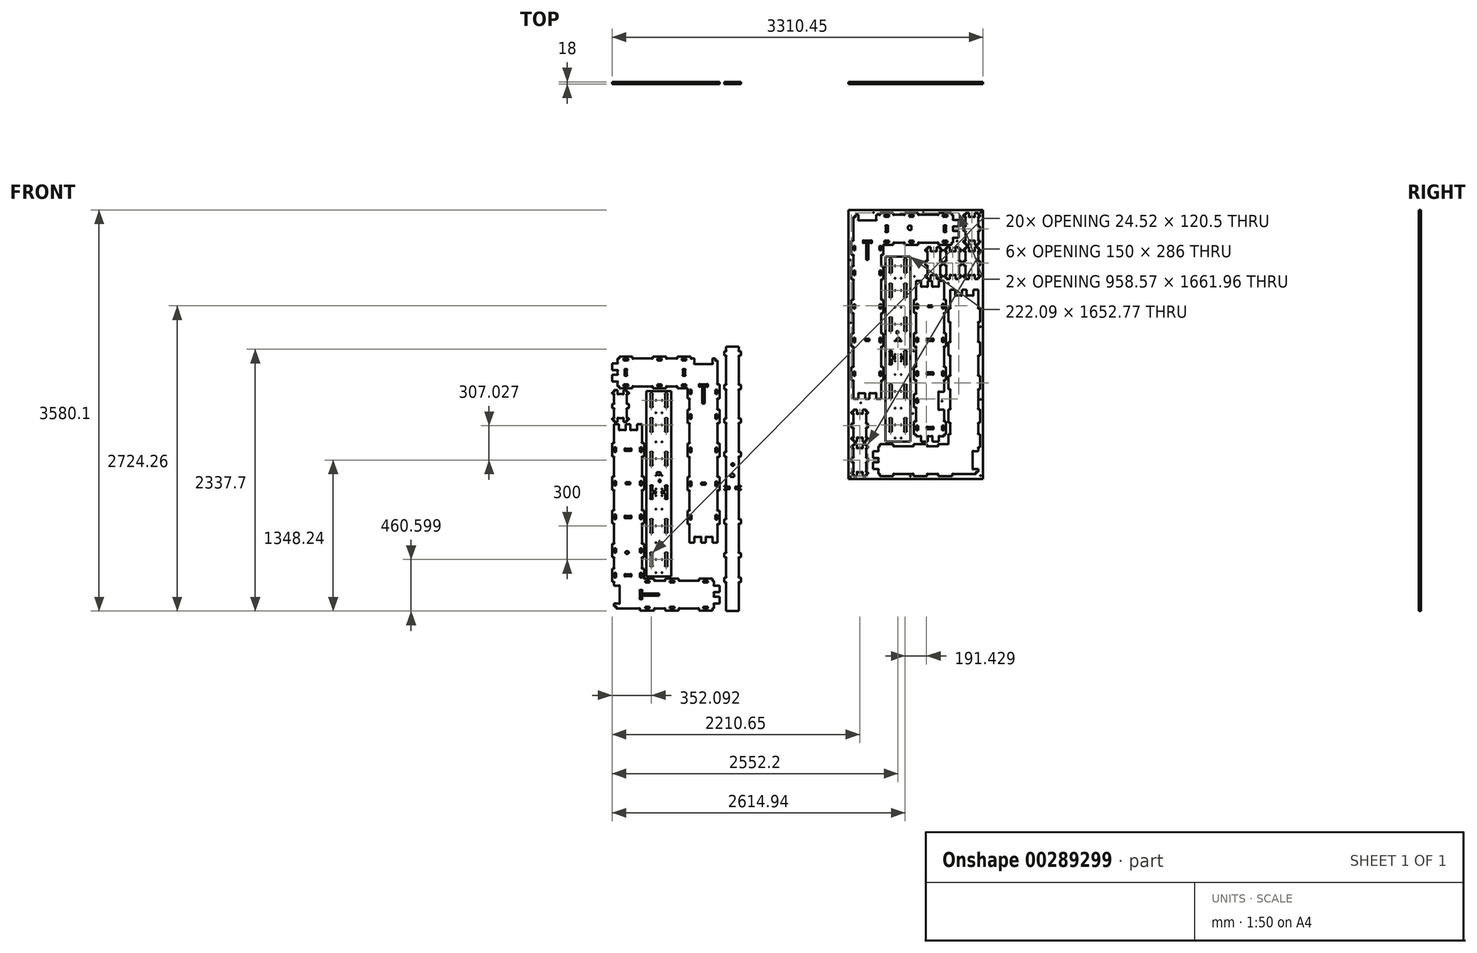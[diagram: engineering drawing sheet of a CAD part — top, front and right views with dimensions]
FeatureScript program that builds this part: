
annotation { "Feature Type Name" : "Feature", "Feature Type Description" : "" }
export const myFeature = defineFeature(function(context is Context, id is Id, definition is map)
    precondition{}
    {
        {
            var Q0;
            Q0=qCreatedBy(makeId("Front.planeOp"),FACE);
            var sketch = newSketch(context, id + "F0", { "sketchPlane" : qUnion([Q0])});
            skLineSegment(sketch, "E0", {"start": v(348.3, 849.32) * mm, "end": v(348.3, 1056.8) * mm});
            skLineSegment(sketch, "E1", {"start": v(348.3, 1056.8) * mm, "end": v(334.83, 1056.8) * mm});
            skArc(sketch, "E2", {"start": v(334.83, 1056.8) * mm, "mid": v(331.45, 1053.78) * mm, "end": v(328.3, 1057.05) * mm});
            skLineSegment(sketch, "E3", {"start": v(328.3, 1057.05) * mm, "end": v(328.3, 1074.8) * mm});
            skLineSegment(sketch, "E4", {"start": v(328.3, 1074.8) * mm, "end": v(303.8, 1074.8) * mm});
            skLineSegment(sketch, "E5", {"start": v(303.8, 1074.8) * mm, "end": v(303.8, 1031.32) * mm});
            skArc(sketch, "E6", {"start": v(303.8, 1031.32) * mm, "mid": v(306.82, 1027.93) * mm, "end": v(303.56, 1024.8) * mm});
            skLineSegment(sketch, "E7", {"start": v(303.56, 1024.8) * mm, "end": v(143.56, 1024.8) * mm});
            skArc(sketch, "E8", {"start": v(143.56, 1024.8) * mm, "mid": v(140.3, 1027.94) * mm, "end": v(143.3, 1031.32) * mm});
            skLineSegment(sketch, "E9", {"start": v(143.3, 1031.32) * mm, "end": v(143.3, 1074.8) * mm});
            skLineSegment(sketch, "E10", {"start": v(143.3, 1074.8) * mm, "end": v(117.06, 1074.8) * mm});
            skArc(sketch, "E11", {"start": v(117.06, 1074.8) * mm, "mid": v(113.68, 1071.78) * mm, "end": v(110.54, 1075.05) * mm});
            skLineSegment(sketch, "E12", {"start": v(110.54, 1075.05) * mm, "end": v(110.54, 1092.8) * mm});
            skLineSegment(sketch, "E13", {"start": v(110.54, 1092.8) * mm, "end": v(-8.96, 1092.8) * mm});
            skLineSegment(sketch, "E14", {"start": v(-8.96, 1092.8) * mm, "end": v(-8.96, 1075.05) * mm});
            skArc(sketch, "E15", {"start": v(-8.96, 1075.05) * mm, "mid": v(-12.1, 1071.79) * mm, "end": v(-15.48, 1074.8) * mm});
            skLineSegment(sketch, "E16", {"start": v(-15.48, 1074.8) * mm, "end": v(-102.94, 1074.8) * mm});
            skArc(sketch, "E17", {"start": v(-102.94, 1074.8) * mm, "mid": v(-106.32, 1071.78) * mm, "end": v(-109.46, 1075.05) * mm});
            skLineSegment(sketch, "E18", {"start": v(-109.46, 1075.05) * mm, "end": v(-109.46, 1092.8) * mm});
            skLineSegment(sketch, "E19", {"start": v(-109.46, 1092.8) * mm, "end": v(-228.96, 1092.8) * mm});
            skLineSegment(sketch, "E20", {"start": v(-228.96, 1092.8) * mm, "end": v(-228.96, 1075.05) * mm});
            skArc(sketch, "E21", {"start": v(-228.96, 1075.05) * mm, "mid": v(-232.1, 1071.79) * mm, "end": v(-235.48, 1074.8) * mm});
            skLineSegment(sketch, "E22", {"start": v(-235.48, 1074.8) * mm, "end": v(-402.94, 1074.8) * mm});
            skArc(sketch, "E23", {"start": v(-402.94, 1074.8) * mm, "mid": v(-406.32, 1071.78) * mm, "end": v(-409.46, 1075.05) * mm});
            skLineSegment(sketch, "E24", {"start": v(-409.46, 1075.05) * mm, "end": v(-409.46, 1092.8) * mm});
            skLineSegment(sketch, "E25", {"start": v(-409.46, 1092.8) * mm, "end": v(-528.96, 1092.8) * mm});
            skLineSegment(sketch, "E26", {"start": v(-528.96, 1092.8) * mm, "end": v(-528.96, 1075.05) * mm});
            skArc(sketch, "E27", {"start": v(-528.96, 1075.05) * mm, "mid": v(-532.1, 1071.79) * mm, "end": v(-535.48, 1074.8) * mm});
            skLineSegment(sketch, "E28", {"start": v(-535.48, 1074.8) * mm, "end": v(-542.26, 1074.8) * mm});
            skLineSegment(sketch, "E29", {"start": v(-542.26, 1074.8) * mm, "end": v(-542.26, 1036.32) * mm});
            skArc(sketch, "E30", {"start": v(-542.26, 1036.32) * mm, "mid": v(-539.25, 1032.94) * mm, "end": v(-542.51, 1029.8) * mm});
            skLineSegment(sketch, "E31", {"start": v(-542.51, 1029.8) * mm, "end": v(-592.26, 1029.8) * mm});
            skLineSegment(sketch, "E32", {"start": v(-592.26, 1029.8) * mm, "end": v(-592.26, 970.3) * mm});
            skLineSegment(sketch, "E33", {"start": v(-592.26, 970.3) * mm, "end": v(-542.51, 970.3) * mm});
            skArc(sketch, "E34", {"start": v(-542.51, 970.3) * mm, "mid": v(-539.26, 967.16) * mm, "end": v(-542.26, 963.78) * mm});
            skLineSegment(sketch, "E35", {"start": v(-542.26, 963.78) * mm, "end": v(-542.26, 936.32) * mm});
            skArc(sketch, "E36", {"start": v(-542.26, 936.32) * mm, "mid": v(-539.25, 932.94) * mm, "end": v(-542.51, 929.8) * mm});
            skLineSegment(sketch, "E37", {"start": v(-542.51, 929.8) * mm, "end": v(-592.26, 929.8) * mm});
            skLineSegment(sketch, "E38", {"start": v(-592.26, 929.8) * mm, "end": v(-592.26, 870.3) * mm});
            skLineSegment(sketch, "E39", {"start": v(-592.26, 870.3) * mm, "end": v(-542.51, 870.3) * mm});
            skArc(sketch, "E40", {"start": v(-542.51, 870.3) * mm, "mid": v(-539.26, 867.16) * mm, "end": v(-542.26, 863.78) * mm});
            skLineSegment(sketch, "E41", {"start": v(-542.26, 863.78) * mm, "end": v(-542.26, 825.3) * mm});
            skLineSegment(sketch, "E42", {"start": v(-542.26, 825.3) * mm, "end": v(-535.48, 825.3) * mm});
            skArc(sketch, "E43", {"start": v(-535.48, 825.3) * mm, "mid": v(-532.1, 828.31) * mm, "end": v(-528.96, 825.05) * mm});
            skLineSegment(sketch, "E44", {"start": v(-528.96, 825.05) * mm, "end": v(-528.96, 807.3) * mm});
            skLineSegment(sketch, "E45", {"start": v(-528.96, 807.3) * mm, "end": v(-409.46, 807.3) * mm});
            skLineSegment(sketch, "E46", {"start": v(-409.46, 807.3) * mm, "end": v(-409.46, 825.05) * mm});
            skArc(sketch, "E47", {"start": v(-409.46, 825.05) * mm, "mid": v(-406.32, 828.3) * mm, "end": v(-402.94, 825.3) * mm});
            skLineSegment(sketch, "E48", {"start": v(-402.94, 825.3) * mm, "end": v(-235.48, 825.3) * mm});
            skArc(sketch, "E49", {"start": v(-235.48, 825.3) * mm, "mid": v(-232.1, 828.31) * mm, "end": v(-228.96, 825.05) * mm});
            skLineSegment(sketch, "E50", {"start": v(-228.96, 825.05) * mm, "end": v(-228.96, 807.3) * mm});
            skLineSegment(sketch, "E51", {"start": v(-228.96, 807.3) * mm, "end": v(-109.46, 807.3) * mm});
            skLineSegment(sketch, "E52", {"start": v(-109.46, 807.3) * mm, "end": v(-109.46, 825.05) * mm});
            skArc(sketch, "E53", {"start": v(-109.46, 825.05) * mm, "mid": v(-106.32, 828.3) * mm, "end": v(-102.94, 825.3) * mm});
            skLineSegment(sketch, "E54", {"start": v(-102.94, 825.3) * mm, "end": v(-15.48, 825.3) * mm});
            skArc(sketch, "E55", {"start": v(-15.48, 825.3) * mm, "mid": v(-12.1, 828.31) * mm, "end": v(-8.96, 825.05) * mm});
            skLineSegment(sketch, "E56", {"start": v(-8.96, 825.05) * mm, "end": v(-8.96, 807.3) * mm});
            skLineSegment(sketch, "E57", {"start": v(-8.96, 807.3) * mm, "end": v(74.29, 807.3) * mm});
            skArc(sketch, "E58", {"start": v(74.29, 807.3) * mm, "mid": v(77.67, 810.31) * mm, "end": v(80.8, 807.05) * mm});
            skLineSegment(sketch, "E59", {"start": v(80.8, 807.05) * mm, "end": v(80.8, 717.53) * mm});
            skLineSegment(sketch, "E60", {"start": v(80.8, 717.53) * mm, "end": v(98.56, 717.53) * mm});
            skArc(sketch, "E61", {"start": v(98.56, 717.53) * mm, "mid": v(101.81, 714.39) * mm, "end": v(98.8, 711) * mm});
            skLineSegment(sketch, "E62", {"start": v(98.8, 711) * mm, "end": v(98.8, 623.55) * mm});
            skArc(sketch, "E63", {"start": v(98.8, 623.55) * mm, "mid": v(101.82, 620.17) * mm, "end": v(98.56, 617.03) * mm});
            skLineSegment(sketch, "E64", {"start": v(98.56, 617.03) * mm, "end": v(80.8, 617.03) * mm});
            skLineSegment(sketch, "E65", {"start": v(80.8, 617.03) * mm, "end": v(80.8, 497.53) * mm});
            skLineSegment(sketch, "E66", {"start": v(80.8, 497.53) * mm, "end": v(98.56, 497.53) * mm});
            skArc(sketch, "E67", {"start": v(98.56, 497.53) * mm, "mid": v(101.81, 494.39) * mm, "end": v(98.8, 491) * mm});
            skLineSegment(sketch, "E68", {"start": v(98.8, 491) * mm, "end": v(98.8, 323.55) * mm});
            skArc(sketch, "E69", {"start": v(98.8, 323.55) * mm, "mid": v(101.82, 320.17) * mm, "end": v(98.56, 317.03) * mm});
            skLineSegment(sketch, "E70", {"start": v(98.56, 317.03) * mm, "end": v(80.8, 317.03) * mm});
            skLineSegment(sketch, "E71", {"start": v(80.8, 317.03) * mm, "end": v(80.8, 197.53) * mm});
            skLineSegment(sketch, "E72", {"start": v(80.8, 197.53) * mm, "end": v(98.56, 197.53) * mm});
            skArc(sketch, "E73", {"start": v(98.56, 197.53) * mm, "mid": v(101.81, 194.39) * mm, "end": v(98.8, 191) * mm});
            skLineSegment(sketch, "E74", {"start": v(98.8, 191) * mm, "end": v(98.8, 23.55) * mm});
            skArc(sketch, "E75", {"start": v(98.8, 23.55) * mm, "mid": v(101.82, 20.17) * mm, "end": v(98.56, 17.03) * mm});
            skLineSegment(sketch, "E76", {"start": v(98.56, 17.03) * mm, "end": v(80.8, 17.03) * mm});
            skLineSegment(sketch, "E77", {"start": v(80.8, 17.03) * mm, "end": v(80.8, -102.47) * mm});
            skLineSegment(sketch, "E78", {"start": v(80.8, -102.47) * mm, "end": v(98.56, -102.47) * mm});
            skArc(sketch, "E79", {"start": v(98.56, -102.47) * mm, "mid": v(101.81, -105.61) * mm, "end": v(98.8, -109) * mm});
            skLineSegment(sketch, "E80", {"start": v(98.8, -109) * mm, "end": v(98.8, -276.45) * mm});
            skArc(sketch, "E81", {"start": v(98.8, -276.45) * mm, "mid": v(101.82, -279.83) * mm, "end": v(98.56, -282.97) * mm});
            skLineSegment(sketch, "E82", {"start": v(98.56, -282.97) * mm, "end": v(80.8, -282.97) * mm});
            skLineSegment(sketch, "E83", {"start": v(80.8, -282.97) * mm, "end": v(80.8, -402.47) * mm});
            skLineSegment(sketch, "E84", {"start": v(80.8, -402.47) * mm, "end": v(98.56, -402.47) * mm});
            skArc(sketch, "E85", {"start": v(98.56, -402.47) * mm, "mid": v(101.81, -405.61) * mm, "end": v(98.8, -409) * mm});
            skLineSegment(sketch, "E86", {"start": v(98.8, -409) * mm, "end": v(98.8, -569.17) * mm});
            skLineSegment(sketch, "E87", {"start": v(98.8, -569.17) * mm, "end": v(143.3, -569.17) * mm});
            skLineSegment(sketch, "E88", {"start": v(143.3, -569.17) * mm, "end": v(143.3, -519.42) * mm});
            skArc(sketch, "E89", {"start": v(143.3, -519.42) * mm, "mid": v(146.45, -516.16) * mm, "end": v(149.83, -519.17) * mm});
            skLineSegment(sketch, "E90", {"start": v(149.83, -519.17) * mm, "end": v(197.29, -519.17) * mm});
            skArc(sketch, "E91", {"start": v(197.29, -519.17) * mm, "mid": v(200.67, -516.15) * mm, "end": v(203.8, -519.42) * mm});
            skLineSegment(sketch, "E92", {"start": v(203.8, -519.42) * mm, "end": v(203.8, -569.17) * mm});
            skLineSegment(sketch, "E93", {"start": v(203.8, -569.17) * mm, "end": v(243.3, -569.17) * mm});
            skLineSegment(sketch, "E94", {"start": v(243.3, -569.17) * mm, "end": v(243.3, -519.42) * mm});
            skArc(sketch, "E95", {"start": v(243.3, -519.42) * mm, "mid": v(246.45, -516.16) * mm, "end": v(249.83, -519.17) * mm});
            skLineSegment(sketch, "E96", {"start": v(249.83, -519.17) * mm, "end": v(297.29, -519.17) * mm});
            skArc(sketch, "E97", {"start": v(297.29, -519.17) * mm, "mid": v(300.67, -516.15) * mm, "end": v(303.8, -519.42) * mm});
            skLineSegment(sketch, "E98", {"start": v(303.8, -519.42) * mm, "end": v(303.8, -569.17) * mm});
            skLineSegment(sketch, "E99", {"start": v(303.8, -569.17) * mm, "end": v(348.3, -569.17) * mm});
            skLineSegment(sketch, "E100", {"start": v(348.3, -569.17) * mm, "end": v(348.3, -409) * mm});
            skArc(sketch, "E101", {"start": v(348.3, -409) * mm, "mid": v(345.29, -405.6) * mm, "end": v(348.56, -402.47) * mm});
            skLineSegment(sketch, "E102", {"start": v(348.56, -402.47) * mm, "end": v(366.3, -402.47) * mm});
            skLineSegment(sketch, "E103", {"start": v(366.3, -402.47) * mm, "end": v(366.3, -282.97) * mm});
            skLineSegment(sketch, "E104", {"start": v(366.3, -282.97) * mm, "end": v(348.56, -282.97) * mm});
            skArc(sketch, "E105", {"start": v(348.56, -282.97) * mm, "mid": v(345.3, -279.83) * mm, "end": v(348.3, -276.45) * mm});
            skLineSegment(sketch, "E106", {"start": v(348.3, -276.45) * mm, "end": v(348.3, -109) * mm});
            skArc(sketch, "E107", {"start": v(348.3, -109) * mm, "mid": v(345.29, -105.6) * mm, "end": v(348.56, -102.47) * mm});
            skLineSegment(sketch, "E108", {"start": v(348.56, -102.47) * mm, "end": v(366.3, -102.47) * mm});
            skLineSegment(sketch, "E109", {"start": v(366.3, -102.47) * mm, "end": v(366.3, 17.03) * mm});
            skLineSegment(sketch, "E110", {"start": v(366.3, 17.03) * mm, "end": v(348.56, 17.03) * mm});
            skArc(sketch, "E111", {"start": v(348.56, 17.03) * mm, "mid": v(345.3, 20.17) * mm, "end": v(348.3, 23.55) * mm});
            skLineSegment(sketch, "E112", {"start": v(348.3, 23.55) * mm, "end": v(348.3, 191) * mm});
            skArc(sketch, "E113", {"start": v(348.3, 191) * mm, "mid": v(345.29, 194.4) * mm, "end": v(348.56, 197.53) * mm});
            skLineSegment(sketch, "E114", {"start": v(348.56, 197.53) * mm, "end": v(366.3, 197.53) * mm});
            skLineSegment(sketch, "E115", {"start": v(366.3, 197.53) * mm, "end": v(366.3, 317.03) * mm});
            skLineSegment(sketch, "E116", {"start": v(366.3, 317.03) * mm, "end": v(348.56, 317.03) * mm});
            skArc(sketch, "E117", {"start": v(348.56, 317.03) * mm, "mid": v(345.3, 320.17) * mm, "end": v(348.3, 323.55) * mm});
            skLineSegment(sketch, "E118", {"start": v(348.3, 323.55) * mm, "end": v(348.3, 491) * mm});
            skArc(sketch, "E119", {"start": v(348.3, 491) * mm, "mid": v(345.29, 494.39) * mm, "end": v(348.56, 497.53) * mm});
            skLineSegment(sketch, "E120", {"start": v(348.56, 497.53) * mm, "end": v(366.3, 497.53) * mm});
            skLineSegment(sketch, "E121", {"start": v(366.3, 497.53) * mm, "end": v(366.3, 617.03) * mm});
            skLineSegment(sketch, "E122", {"start": v(366.3, 617.03) * mm, "end": v(348.56, 617.03) * mm});
            skArc(sketch, "E123", {"start": v(348.56, 617.03) * mm, "mid": v(345.3, 620.17) * mm, "end": v(348.3, 623.55) * mm});
            skLineSegment(sketch, "E124", {"start": v(348.3, 623.55) * mm, "end": v(348.3, 711) * mm});
            skArc(sketch, "E125", {"start": v(348.3, 711) * mm, "mid": v(345.29, 714.39) * mm, "end": v(348.56, 717.53) * mm});
            skLineSegment(sketch, "E126", {"start": v(348.56, 717.53) * mm, "end": v(366.3, 717.53) * mm});
            skLineSegment(sketch, "E127", {"start": v(366.3, 717.53) * mm, "end": v(366.3, 842.8) * mm});
            skLineSegment(sketch, "E128", {"start": v(366.3, 842.8) * mm, "end": v(348.56, 842.8) * mm});
            skArc(sketch, "E129", {"start": v(348.56, 842.8) * mm, "mid": v(345.3, 845.94) * mm, "end": v(348.3, 849.32) * mm});
            skLineSegment(sketch, "E130", {"start": v(-588.56, 629.92) * mm, "end": v(-573.56, 629.92) * mm});
            skArc(sketch, "E131", {"start": v(-573.56, 629.92) * mm, "mid": v(-570.55, 626.9) * mm, "end": v(-573.56, 623.9) * mm});
            skLineSegment(sketch, "E132", {"start": v(-573.56, 623.9) * mm, "end": v(-573.56, 548.94) * mm});
            skArc(sketch, "E133", {"start": v(-573.56, 548.94) * mm, "mid": v(-570.55, 545.93) * mm, "end": v(-573.56, 542.92) * mm});
            skLineSegment(sketch, "E134", {"start": v(-573.56, 542.92) * mm, "end": v(-591.56, 542.92) * mm});
            skLineSegment(sketch, "E135", {"start": v(-591.56, 542.92) * mm, "end": v(-591.56, 524.92) * mm});
            skLineSegment(sketch, "E136", {"start": v(-591.56, 524.92) * mm, "end": v(-573.56, 524.92) * mm});
            skArc(sketch, "E137", {"start": v(-573.56, 524.92) * mm, "mid": v(-570.55, 521.9) * mm, "end": v(-573.56, 518.9) * mm});
            skLineSegment(sketch, "E138", {"start": v(-573.56, 518.9) * mm, "end": v(-573.56, 506.92) * mm});
            skLineSegment(sketch, "E139", {"start": v(-573.56, 506.92) * mm, "end": v(-542.56, 506.92) * mm});
            skLineSegment(sketch, "E140", {"start": v(-542.56, 506.92) * mm, "end": v(-542.56, 542.92) * mm});
            skArc(sketch, "E141", {"start": v(-542.56, 542.92) * mm, "mid": v(-539.55, 545.93) * mm, "end": v(-536.54, 542.92) * mm});
            skLineSegment(sketch, "E142", {"start": v(-536.54, 542.92) * mm, "end": v(-496.59, 542.92) * mm});
            skArc(sketch, "E143", {"start": v(-496.59, 542.92) * mm, "mid": v(-493.58, 545.93) * mm, "end": v(-490.57, 542.92) * mm});
            skLineSegment(sketch, "E144", {"start": v(-490.57, 542.92) * mm, "end": v(-490.57, 506.92) * mm});
            skLineSegment(sketch, "E145", {"start": v(-490.57, 506.92) * mm, "end": v(-459.57, 506.92) * mm});
            skLineSegment(sketch, "E146", {"start": v(-459.57, 506.92) * mm, "end": v(-459.57, 518.9) * mm});
            skArc(sketch, "E147", {"start": v(-459.57, 518.9) * mm, "mid": v(-462.58, 521.9) * mm, "end": v(-459.57, 524.92) * mm});
            skLineSegment(sketch, "E148", {"start": v(-459.57, 524.92) * mm, "end": v(-441.57, 524.92) * mm});
            skLineSegment(sketch, "E149", {"start": v(-441.57, 524.92) * mm, "end": v(-441.57, 542.92) * mm});
            skLineSegment(sketch, "E150", {"start": v(-441.57, 542.92) * mm, "end": v(-459.57, 542.92) * mm});
            skArc(sketch, "E151", {"start": v(-459.57, 542.92) * mm, "mid": v(-462.58, 545.93) * mm, "end": v(-459.57, 548.94) * mm});
            skLineSegment(sketch, "E152", {"start": v(-459.57, 548.94) * mm, "end": v(-459.57, 623.9) * mm});
            skArc(sketch, "E153", {"start": v(-459.57, 623.9) * mm, "mid": v(-462.58, 626.9) * mm, "end": v(-459.57, 629.92) * mm});
            skLineSegment(sketch, "E154", {"start": v(-459.57, 629.92) * mm, "end": v(-444.57, 629.92) * mm});
            skLineSegment(sketch, "E155", {"start": v(-444.57, 629.92) * mm, "end": v(-441.57, 632.92) * mm});
            skLineSegment(sketch, "E156", {"start": v(-441.57, 632.92) * mm, "end": v(-441.57, 666.92) * mm});
            skLineSegment(sketch, "E157", {"start": v(-441.57, 666.92) * mm, "end": v(-444.57, 669.92) * mm});
            skLineSegment(sketch, "E158", {"start": v(-444.57, 669.92) * mm, "end": v(-459.57, 669.92) * mm});
            skArc(sketch, "E159", {"start": v(-459.57, 669.92) * mm, "mid": v(-462.58, 672.93) * mm, "end": v(-459.57, 675.94) * mm});
            skLineSegment(sketch, "E160", {"start": v(-459.57, 675.94) * mm, "end": v(-459.57, 750.9) * mm});
            skArc(sketch, "E161", {"start": v(-459.57, 750.9) * mm, "mid": v(-462.58, 753.9) * mm, "end": v(-459.57, 756.92) * mm});
            skLineSegment(sketch, "E162", {"start": v(-459.57, 756.92) * mm, "end": v(-441.57, 756.92) * mm});
            skLineSegment(sketch, "E163", {"start": v(-441.57, 756.92) * mm, "end": v(-441.57, 774.92) * mm});
            skLineSegment(sketch, "E164", {"start": v(-441.57, 774.92) * mm, "end": v(-459.57, 774.92) * mm});
            skArc(sketch, "E165", {"start": v(-459.57, 774.92) * mm, "mid": v(-462.58, 777.93) * mm, "end": v(-459.57, 780.94) * mm});
            skLineSegment(sketch, "E166", {"start": v(-459.57, 780.94) * mm, "end": v(-459.57, 792.92) * mm});
            skLineSegment(sketch, "E167", {"start": v(-459.57, 792.92) * mm, "end": v(-490.57, 792.92) * mm});
            skLineSegment(sketch, "E168", {"start": v(-490.57, 792.92) * mm, "end": v(-490.57, 756.96) * mm});
            skArc(sketch, "E169", {"start": v(-490.57, 756.96) * mm, "mid": v(-493.58, 753.95) * mm, "end": v(-496.59, 756.96) * mm});
            skLineSegment(sketch, "E170", {"start": v(-496.59, 756.96) * mm, "end": v(-536.54, 756.96) * mm});
            skArc(sketch, "E171", {"start": v(-536.54, 756.96) * mm, "mid": v(-539.55, 753.95) * mm, "end": v(-542.56, 756.96) * mm});
            skLineSegment(sketch, "E172", {"start": v(-542.56, 756.96) * mm, "end": v(-542.56, 792.92) * mm});
            skLineSegment(sketch, "E173", {"start": v(-542.56, 792.92) * mm, "end": v(-573.56, 792.92) * mm});
            skLineSegment(sketch, "E174", {"start": v(-573.56, 792.92) * mm, "end": v(-573.56, 780.94) * mm});
            skArc(sketch, "E175", {"start": v(-573.56, 780.94) * mm, "mid": v(-570.55, 777.93) * mm, "end": v(-573.56, 774.92) * mm});
            skLineSegment(sketch, "E176", {"start": v(-573.56, 774.92) * mm, "end": v(-591.56, 774.92) * mm});
            skLineSegment(sketch, "E177", {"start": v(-591.56, 774.92) * mm, "end": v(-591.56, 756.92) * mm});
            skLineSegment(sketch, "E178", {"start": v(-591.56, 756.92) * mm, "end": v(-573.56, 756.92) * mm});
            skArc(sketch, "E179", {"start": v(-573.56, 756.92) * mm, "mid": v(-570.55, 753.9) * mm, "end": v(-573.56, 750.9) * mm});
            skLineSegment(sketch, "E180", {"start": v(-573.56, 750.9) * mm, "end": v(-573.56, 675.94) * mm});
            skArc(sketch, "E181", {"start": v(-573.56, 675.94) * mm, "mid": v(-570.55, 672.93) * mm, "end": v(-573.56, 669.92) * mm});
            skLineSegment(sketch, "E182", {"start": v(-573.56, 669.92) * mm, "end": v(-588.56, 669.92) * mm});
            skLineSegment(sketch, "E183", {"start": v(-588.56, 669.92) * mm, "end": v(-591.56, 666.92) * mm});
            skLineSegment(sketch, "E184", {"start": v(-591.56, 666.92) * mm, "end": v(-591.56, 632.92) * mm});
            skLineSegment(sketch, "E185", {"start": v(-591.56, 632.92) * mm, "end": v(-588.56, 629.92) * mm});
            skLineSegment(sketch, "E186", {"start": v(-40.77, 301.48) * mm, "end": v(-32.55, 293.27) * mm});
            skLineSegment(sketch, "E187", {"start": v(-32.55, 293.27) * mm, "end": v(51.01, 293.27) * mm});
            skLineSegment(sketch, "E188", {"start": v(51.01, 293.27) * mm, "end": v(59.23, 301.48) * mm});
            skLineSegment(sketch, "E189", {"start": v(59.23, 301.48) * mm, "end": v(59.23, 435.05) * mm});
            skLineSegment(sketch, "E190", {"start": v(59.23, 435.05) * mm, "end": v(51.01, 443.27) * mm});
            skLineSegment(sketch, "E191", {"start": v(51.01, 443.27) * mm, "end": v(-32.55, 443.27) * mm});
            skLineSegment(sketch, "E192", {"start": v(-32.55, 443.27) * mm, "end": v(-40.77, 435.05) * mm});
            skLineSegment(sketch, "E193", {"start": v(-40.77, 435.05) * mm, "end": v(-40.77, 301.48) * mm});
            skLineSegment(sketch, "E194", {"start": v(-40.77, 131.48) * mm, "end": v(-32.55, 123.27) * mm});
            skLineSegment(sketch, "E195", {"start": v(-32.55, 123.27) * mm, "end": v(51.01, 123.27) * mm});
            skLineSegment(sketch, "E196", {"start": v(51.01, 123.27) * mm, "end": v(59.23, 131.48) * mm});
            skLineSegment(sketch, "E197", {"start": v(59.23, 131.48) * mm, "end": v(59.23, 265.05) * mm});
            skLineSegment(sketch, "E198", {"start": v(59.23, 265.05) * mm, "end": v(51.01, 273.27) * mm});
            skLineSegment(sketch, "E199", {"start": v(51.01, 273.27) * mm, "end": v(-32.55, 273.27) * mm});
            skLineSegment(sketch, "E200", {"start": v(-32.55, 273.27) * mm, "end": v(-40.77, 265.05) * mm});
            skLineSegment(sketch, "E201", {"start": v(-40.77, 265.05) * mm, "end": v(-40.77, 131.48) * mm});
            skLineSegment(sketch, "E202", {"start": v(-40.77, -38.52) * mm, "end": v(-32.55, -46.73) * mm});
            skLineSegment(sketch, "E203", {"start": v(-32.55, -46.73) * mm, "end": v(51.01, -46.73) * mm});
            skLineSegment(sketch, "E204", {"start": v(51.01, -46.73) * mm, "end": v(59.23, -38.52) * mm});
            skLineSegment(sketch, "E205", {"start": v(59.23, -38.52) * mm, "end": v(59.23, 95.05) * mm});
            skLineSegment(sketch, "E206", {"start": v(59.23, 95.05) * mm, "end": v(51.01, 103.27) * mm});
            skLineSegment(sketch, "E207", {"start": v(51.01, 103.27) * mm, "end": v(-32.55, 103.27) * mm});
            skLineSegment(sketch, "E208", {"start": v(-32.55, 103.27) * mm, "end": v(-40.77, 95.05) * mm});
            skLineSegment(sketch, "E209", {"start": v(-40.77, 95.05) * mm, "end": v(-40.77, -38.52) * mm});
            skLineSegment(sketch, "E210", {"start": v(-40.77, -208.52) * mm, "end": v(-32.55, -216.73) * mm});
            skLineSegment(sketch, "E211", {"start": v(-32.55, -216.73) * mm, "end": v(51.01, -216.73) * mm});
            skLineSegment(sketch, "E212", {"start": v(51.01, -216.73) * mm, "end": v(59.23, -208.52) * mm});
            skLineSegment(sketch, "E213", {"start": v(59.23, -208.52) * mm, "end": v(59.23, -74.95) * mm});
            skLineSegment(sketch, "E214", {"start": v(59.23, -74.95) * mm, "end": v(51.01, -66.73) * mm});
            skLineSegment(sketch, "E215", {"start": v(51.01, -66.73) * mm, "end": v(-32.55, -66.73) * mm});
            skLineSegment(sketch, "E216", {"start": v(-32.55, -66.73) * mm, "end": v(-40.77, -74.95) * mm});
            skLineSegment(sketch, "E217", {"start": v(-40.77, -74.95) * mm, "end": v(-40.77, -208.52) * mm});
            skLineSegment(sketch, "E218", {"start": v(-40.77, -378.52) * mm, "end": v(-32.55, -386.74) * mm});
            skLineSegment(sketch, "E219", {"start": v(-32.55, -386.74) * mm, "end": v(51.01, -386.74) * mm});
            skLineSegment(sketch, "E220", {"start": v(51.01, -386.74) * mm, "end": v(59.23, -378.52) * mm});
            skLineSegment(sketch, "E221", {"start": v(59.23, -378.52) * mm, "end": v(59.23, -244.95) * mm});
            skLineSegment(sketch, "E222", {"start": v(59.23, -244.95) * mm, "end": v(51.01, -236.73) * mm});
            skLineSegment(sketch, "E223", {"start": v(51.01, -236.73) * mm, "end": v(-32.55, -236.73) * mm});
            skLineSegment(sketch, "E224", {"start": v(-32.55, -236.73) * mm, "end": v(-40.77, -244.95) * mm});
            skLineSegment(sketch, "E225", {"start": v(-40.77, -244.95) * mm, "end": v(-40.77, -378.52) * mm});
            skLineSegment(sketch, "E226", {"start": v(-40.77, -548.52) * mm, "end": v(-32.55, -556.74) * mm});
            skLineSegment(sketch, "E227", {"start": v(-32.55, -556.74) * mm, "end": v(51.01, -556.74) * mm});
            skLineSegment(sketch, "E228", {"start": v(51.01, -556.74) * mm, "end": v(59.23, -548.52) * mm});
            skLineSegment(sketch, "E229", {"start": v(59.23, -548.52) * mm, "end": v(59.23, -414.95) * mm});
            skLineSegment(sketch, "E230", {"start": v(59.23, -414.95) * mm, "end": v(51.01, -406.74) * mm});
            skLineSegment(sketch, "E231", {"start": v(51.01, -406.74) * mm, "end": v(-32.55, -406.74) * mm});
            skLineSegment(sketch, "E232", {"start": v(-32.55, -406.74) * mm, "end": v(-40.77, -414.95) * mm});
            skLineSegment(sketch, "E233", {"start": v(-40.77, -414.95) * mm, "end": v(-40.77, -548.52) * mm});
            skLineSegment(sketch, "E234", {"start": v(302.81, -1175) * mm, "end": v(302.81, -1157.25) * mm});
            skArc(sketch, "E235", {"start": v(302.81, -1157.25) * mm, "mid": v(305.95, -1154) * mm, "end": v(309.33, -1157) * mm});
            skLineSegment(sketch, "E236", {"start": v(309.33, -1157) * mm, "end": v(316.12, -1157) * mm});
            skLineSegment(sketch, "E237", {"start": v(316.12, -1157) * mm, "end": v(316.12, -1118.52) * mm});
            skArc(sketch, "E238", {"start": v(316.12, -1118.52) * mm, "mid": v(313.1, -1115.14) * mm, "end": v(316.37, -1112) * mm});
            skLineSegment(sketch, "E239", {"start": v(316.37, -1112) * mm, "end": v(366.12, -1112) * mm});
            skLineSegment(sketch, "E240", {"start": v(366.12, -1112) * mm, "end": v(366.12, -1052.5) * mm});
            skLineSegment(sketch, "E241", {"start": v(366.12, -1052.5) * mm, "end": v(316.37, -1052.5) * mm});
            skArc(sketch, "E242", {"start": v(316.37, -1052.5) * mm, "mid": v(313.11, -1049.36) * mm, "end": v(316.12, -1045.98) * mm});
            skLineSegment(sketch, "E243", {"start": v(316.12, -1045.98) * mm, "end": v(316.12, -1018.52) * mm});
            skArc(sketch, "E244", {"start": v(316.12, -1018.52) * mm, "mid": v(313.1, -1015.14) * mm, "end": v(316.37, -1012) * mm});
            skLineSegment(sketch, "E245", {"start": v(316.37, -1012) * mm, "end": v(366.12, -1012) * mm});
            skLineSegment(sketch, "E246", {"start": v(366.12, -1012) * mm, "end": v(366.12, -952.5) * mm});
            skLineSegment(sketch, "E247", {"start": v(366.12, -952.5) * mm, "end": v(316.37, -952.5) * mm});
            skArc(sketch, "E248", {"start": v(316.37, -952.5) * mm, "mid": v(313.11, -949.36) * mm, "end": v(316.12, -945.98) * mm});
            skLineSegment(sketch, "E249", {"start": v(316.12, -945.98) * mm, "end": v(316.12, -907.5) * mm});
            skLineSegment(sketch, "E250", {"start": v(316.12, -907.5) * mm, "end": v(309.33, -907.5) * mm});
            skArc(sketch, "E251", {"start": v(309.33, -907.5) * mm, "mid": v(305.95, -910.52) * mm, "end": v(302.81, -907.25) * mm});
            skLineSegment(sketch, "E252", {"start": v(302.81, -907.25) * mm, "end": v(302.81, -889.5) * mm});
            skLineSegment(sketch, "E253", {"start": v(302.81, -889.5) * mm, "end": v(183.31, -889.5) * mm});
            skLineSegment(sketch, "E254", {"start": v(183.31, -889.5) * mm, "end": v(183.31, -907.25) * mm});
            skArc(sketch, "E255", {"start": v(183.31, -907.25) * mm, "mid": v(180.17, -910.5) * mm, "end": v(176.8, -907.5) * mm});
            skLineSegment(sketch, "E256", {"start": v(176.8, -907.5) * mm, "end": v(9.33, -907.5) * mm});
            skArc(sketch, "E257", {"start": v(9.33, -907.5) * mm, "mid": v(5.95, -910.52) * mm, "end": v(2.81, -907.25) * mm});
            skLineSegment(sketch, "E258", {"start": v(2.81, -907.25) * mm, "end": v(2.81, -889.5) * mm});
            skLineSegment(sketch, "E259", {"start": v(2.81, -889.5) * mm, "end": v(-116.69, -889.5) * mm});
            skLineSegment(sketch, "E260", {"start": v(-116.69, -889.5) * mm, "end": v(-116.69, -907.25) * mm});
            skArc(sketch, "E261", {"start": v(-116.69, -907.25) * mm, "mid": v(-119.83, -910.5) * mm, "end": v(-123.2, -907.5) * mm});
            skLineSegment(sketch, "E262", {"start": v(-123.2, -907.5) * mm, "end": v(-210.67, -907.5) * mm});
            skArc(sketch, "E263", {"start": v(-210.67, -907.5) * mm, "mid": v(-214.05, -910.52) * mm, "end": v(-217.19, -907.25) * mm});
            skLineSegment(sketch, "E264", {"start": v(-217.19, -907.25) * mm, "end": v(-217.19, -889.5) * mm});
            skLineSegment(sketch, "E265", {"start": v(-217.19, -889.5) * mm, "end": v(-306.7, -889.5) * mm});
            skArc(sketch, "E266", {"start": v(-306.7, -889.5) * mm, "mid": v(-309.96, -886.36) * mm, "end": v(-306.95, -882.98) * mm});
            skLineSegment(sketch, "E267", {"start": v(-306.95, -882.98) * mm, "end": v(-306.95, -799.73) * mm});
            skLineSegment(sketch, "E268", {"start": v(-306.95, -799.73) * mm, "end": v(-324.7, -799.73) * mm});
            skArc(sketch, "E269", {"start": v(-324.7, -799.73) * mm, "mid": v(-327.96, -796.6) * mm, "end": v(-324.95, -793.21) * mm});
            skLineSegment(sketch, "E270", {"start": v(-324.95, -793.21) * mm, "end": v(-324.95, -705.75) * mm});
            skArc(sketch, "E271", {"start": v(-324.95, -705.75) * mm, "mid": v(-327.97, -702.37) * mm, "end": v(-324.7, -699.23) * mm});
            skLineSegment(sketch, "E272", {"start": v(-324.7, -699.23) * mm, "end": v(-306.95, -699.23) * mm});
            skLineSegment(sketch, "E273", {"start": v(-306.95, -699.23) * mm, "end": v(-306.95, -579.73) * mm});
            skLineSegment(sketch, "E274", {"start": v(-306.95, -579.73) * mm, "end": v(-324.7, -579.73) * mm});
            skArc(sketch, "E275", {"start": v(-324.7, -579.73) * mm, "mid": v(-327.96, -576.6) * mm, "end": v(-324.95, -573.21) * mm});
            skLineSegment(sketch, "E276", {"start": v(-324.95, -573.21) * mm, "end": v(-324.95, -405.75) * mm});
            skArc(sketch, "E277", {"start": v(-324.95, -405.75) * mm, "mid": v(-327.97, -402.37) * mm, "end": v(-324.7, -399.23) * mm});
            skLineSegment(sketch, "E278", {"start": v(-324.7, -399.23) * mm, "end": v(-306.95, -399.23) * mm});
            skLineSegment(sketch, "E279", {"start": v(-306.95, -399.23) * mm, "end": v(-306.95, -279.73) * mm});
            skLineSegment(sketch, "E280", {"start": v(-306.95, -279.73) * mm, "end": v(-324.7, -279.73) * mm});
            skArc(sketch, "E281", {"start": v(-324.7, -279.73) * mm, "mid": v(-327.96, -276.6) * mm, "end": v(-324.95, -273.21) * mm});
            skLineSegment(sketch, "E282", {"start": v(-324.95, -273.21) * mm, "end": v(-324.95, -105.75) * mm});
            skArc(sketch, "E283", {"start": v(-324.95, -105.75) * mm, "mid": v(-327.97, -102.37) * mm, "end": v(-324.7, -99.23) * mm});
            skLineSegment(sketch, "E284", {"start": v(-324.7, -99.23) * mm, "end": v(-306.95, -99.23) * mm});
            skLineSegment(sketch, "E285", {"start": v(-306.95, -99.23) * mm, "end": v(-306.95, 20.27) * mm});
            skLineSegment(sketch, "E286", {"start": v(-306.95, 20.27) * mm, "end": v(-324.7, 20.27) * mm});
            skArc(sketch, "E287", {"start": v(-324.7, 20.27) * mm, "mid": v(-327.96, 23.4) * mm, "end": v(-324.95, 26.79) * mm});
            skLineSegment(sketch, "E288", {"start": v(-324.95, 26.79) * mm, "end": v(-324.95, 194.25) * mm});
            skArc(sketch, "E289", {"start": v(-324.95, 194.25) * mm, "mid": v(-327.97, 197.63) * mm, "end": v(-324.7, 200.77) * mm});
            skLineSegment(sketch, "E290", {"start": v(-324.7, 200.77) * mm, "end": v(-306.95, 200.77) * mm});
            skLineSegment(sketch, "E291", {"start": v(-306.95, 200.77) * mm, "end": v(-306.95, 320.27) * mm});
            skLineSegment(sketch, "E292", {"start": v(-306.95, 320.27) * mm, "end": v(-324.7, 320.27) * mm});
            skArc(sketch, "E293", {"start": v(-324.7, 320.27) * mm, "mid": v(-327.96, 323.4) * mm, "end": v(-324.95, 326.79) * mm});
            skLineSegment(sketch, "E294", {"start": v(-324.95, 326.79) * mm, "end": v(-324.95, 486.96) * mm});
            skLineSegment(sketch, "E295", {"start": v(-324.95, 486.96) * mm, "end": v(-369.45, 486.96) * mm});
            skLineSegment(sketch, "E296", {"start": v(-369.45, 486.96) * mm, "end": v(-369.45, 437.21) * mm});
            skArc(sketch, "E297", {"start": v(-369.45, 437.21) * mm, "mid": v(-372.6, 433.95) * mm, "end": v(-375.97, 436.96) * mm});
            skLineSegment(sketch, "E298", {"start": v(-375.97, 436.96) * mm, "end": v(-423.43, 436.96) * mm});
            skArc(sketch, "E299", {"start": v(-423.43, 436.96) * mm, "mid": v(-426.81, 433.94) * mm, "end": v(-429.95, 437.21) * mm});
            skLineSegment(sketch, "E300", {"start": v(-429.95, 437.21) * mm, "end": v(-429.95, 486.96) * mm});
            skLineSegment(sketch, "E301", {"start": v(-429.95, 486.96) * mm, "end": v(-469.45, 486.96) * mm});
            skLineSegment(sketch, "E302", {"start": v(-469.45, 486.96) * mm, "end": v(-469.45, 437.21) * mm});
            skArc(sketch, "E303", {"start": v(-469.45, 437.21) * mm, "mid": v(-472.6, 433.95) * mm, "end": v(-475.97, 436.96) * mm});
            skLineSegment(sketch, "E304", {"start": v(-475.97, 436.96) * mm, "end": v(-523.43, 436.96) * mm});
            skArc(sketch, "E305", {"start": v(-523.43, 436.96) * mm, "mid": v(-526.81, 433.94) * mm, "end": v(-529.95, 437.21) * mm});
            skLineSegment(sketch, "E306", {"start": v(-529.95, 437.21) * mm, "end": v(-529.95, 486.96) * mm});
            skLineSegment(sketch, "E307", {"start": v(-529.95, 486.96) * mm, "end": v(-574.45, 486.96) * mm});
            skLineSegment(sketch, "E308", {"start": v(-574.45, 486.96) * mm, "end": v(-574.45, 326.79) * mm});
            skArc(sketch, "E309", {"start": v(-574.45, 326.79) * mm, "mid": v(-571.44, 323.4) * mm, "end": v(-574.7, 320.27) * mm});
            skLineSegment(sketch, "E310", {"start": v(-574.7, 320.27) * mm, "end": v(-592.45, 320.27) * mm});
            skLineSegment(sketch, "E311", {"start": v(-592.45, 320.27) * mm, "end": v(-592.45, 200.77) * mm});
            skLineSegment(sketch, "E312", {"start": v(-592.45, 200.77) * mm, "end": v(-574.7, 200.77) * mm});
            skArc(sketch, "E313", {"start": v(-574.7, 200.77) * mm, "mid": v(-571.45, 197.63) * mm, "end": v(-574.45, 194.25) * mm});
            skLineSegment(sketch, "E314", {"start": v(-574.45, 194.25) * mm, "end": v(-574.45, 26.79) * mm});
            skArc(sketch, "E315", {"start": v(-574.45, 26.79) * mm, "mid": v(-571.44, 23.4) * mm, "end": v(-574.7, 20.27) * mm});
            skLineSegment(sketch, "E316", {"start": v(-574.7, 20.27) * mm, "end": v(-592.45, 20.27) * mm});
            skLineSegment(sketch, "E317", {"start": v(-592.45, 20.27) * mm, "end": v(-592.45, -99.23) * mm});
            skLineSegment(sketch, "E318", {"start": v(-592.45, -99.23) * mm, "end": v(-574.7, -99.23) * mm});
            skArc(sketch, "E319", {"start": v(-574.7, -99.23) * mm, "mid": v(-571.45, -102.37) * mm, "end": v(-574.45, -105.75) * mm});
            skLineSegment(sketch, "E320", {"start": v(-574.45, -105.75) * mm, "end": v(-574.45, -273.21) * mm});
            skArc(sketch, "E321", {"start": v(-574.45, -273.21) * mm, "mid": v(-571.44, -276.6) * mm, "end": v(-574.7, -279.73) * mm});
            skLineSegment(sketch, "E322", {"start": v(-574.7, -279.73) * mm, "end": v(-592.45, -279.73) * mm});
            skLineSegment(sketch, "E323", {"start": v(-592.45, -279.73) * mm, "end": v(-592.45, -399.23) * mm});
            skLineSegment(sketch, "E324", {"start": v(-592.45, -399.23) * mm, "end": v(-574.7, -399.23) * mm});
            skArc(sketch, "E325", {"start": v(-574.7, -399.23) * mm, "mid": v(-571.45, -402.37) * mm, "end": v(-574.45, -405.75) * mm});
            skLineSegment(sketch, "E326", {"start": v(-574.45, -405.75) * mm, "end": v(-574.45, -573.21) * mm});
            skArc(sketch, "E327", {"start": v(-574.45, -573.21) * mm, "mid": v(-571.44, -576.6) * mm, "end": v(-574.7, -579.73) * mm});
            skLineSegment(sketch, "E328", {"start": v(-574.7, -579.73) * mm, "end": v(-592.45, -579.73) * mm});
            skLineSegment(sketch, "E329", {"start": v(-592.45, -579.73) * mm, "end": v(-592.45, -699.23) * mm});
            skLineSegment(sketch, "E330", {"start": v(-592.45, -699.23) * mm, "end": v(-574.7, -699.23) * mm});
            skArc(sketch, "E331", {"start": v(-574.7, -699.23) * mm, "mid": v(-571.45, -702.37) * mm, "end": v(-574.45, -705.75) * mm});
            skLineSegment(sketch, "E332", {"start": v(-574.45, -705.75) * mm, "end": v(-574.45, -793.21) * mm});
            skArc(sketch, "E333", {"start": v(-574.45, -793.21) * mm, "mid": v(-571.44, -796.6) * mm, "end": v(-574.7, -799.73) * mm});
            skLineSegment(sketch, "E334", {"start": v(-574.7, -799.73) * mm, "end": v(-592.45, -799.73) * mm});
            skLineSegment(sketch, "E335", {"start": v(-592.45, -799.73) * mm, "end": v(-592.45, -919.23) * mm});
            skLineSegment(sketch, "E336", {"start": v(-592.45, -919.23) * mm, "end": v(-574.7, -919.23) * mm});
            skArc(sketch, "E337", {"start": v(-574.7, -919.23) * mm, "mid": v(-571.45, -922.37) * mm, "end": v(-574.45, -925.75) * mm});
            skLineSegment(sketch, "E338", {"start": v(-574.45, -925.75) * mm, "end": v(-574.45, -952) * mm});
            skLineSegment(sketch, "E339", {"start": v(-574.45, -952) * mm, "end": v(-530.97, -952) * mm});
            skArc(sketch, "E340", {"start": v(-530.97, -952) * mm, "mid": v(-527.6, -948.98) * mm, "end": v(-524.45, -952.25) * mm});
            skLineSegment(sketch, "E341", {"start": v(-524.45, -952.25) * mm, "end": v(-524.45, -1112.25) * mm});
            skArc(sketch, "E342", {"start": v(-524.45, -1112.25) * mm, "mid": v(-527.6, -1115.5) * mm, "end": v(-530.97, -1112.5) * mm});
            skLineSegment(sketch, "E343", {"start": v(-530.97, -1112.5) * mm, "end": v(-574.45, -1112.5) * mm});
            skLineSegment(sketch, "E344", {"start": v(-574.45, -1112.5) * mm, "end": v(-574.45, -1137) * mm});
            skLineSegment(sketch, "E345", {"start": v(-574.45, -1137) * mm, "end": v(-556.7, -1137) * mm});
            skArc(sketch, "E346", {"start": v(-556.7, -1137) * mm, "mid": v(-553.45, -1140.14) * mm, "end": v(-556.45, -1143.52) * mm});
            skLineSegment(sketch, "E347", {"start": v(-556.45, -1143.52) * mm, "end": v(-556.45, -1157) * mm});
            skLineSegment(sketch, "E348", {"start": v(-556.45, -1157) * mm, "end": v(-348.98, -1157) * mm});
            skArc(sketch, "E349", {"start": v(-348.98, -1157) * mm, "mid": v(-345.6, -1153.98) * mm, "end": v(-342.46, -1157.25) * mm});
            skLineSegment(sketch, "E350", {"start": v(-342.46, -1157.25) * mm, "end": v(-342.46, -1175) * mm});
            skLineSegment(sketch, "E351", {"start": v(-342.46, -1175) * mm, "end": v(-217.19, -1175) * mm});
            skLineSegment(sketch, "E352", {"start": v(-217.19, -1175) * mm, "end": v(-217.19, -1157.25) * mm});
            skArc(sketch, "E353", {"start": v(-217.19, -1157.25) * mm, "mid": v(-214.05, -1154) * mm, "end": v(-210.67, -1157) * mm});
            skLineSegment(sketch, "E354", {"start": v(-210.67, -1157) * mm, "end": v(-123.2, -1157) * mm});
            skArc(sketch, "E355", {"start": v(-123.2, -1157) * mm, "mid": v(-119.83, -1153.98) * mm, "end": v(-116.69, -1157.25) * mm});
            skLineSegment(sketch, "E356", {"start": v(-116.69, -1157.25) * mm, "end": v(-116.69, -1175) * mm});
            skLineSegment(sketch, "E357", {"start": v(-116.69, -1175) * mm, "end": v(2.81, -1175) * mm});
            skLineSegment(sketch, "E358", {"start": v(2.81, -1175) * mm, "end": v(2.81, -1157.25) * mm});
            skArc(sketch, "E359", {"start": v(2.81, -1157.25) * mm, "mid": v(5.95, -1154) * mm, "end": v(9.33, -1157) * mm});
            skLineSegment(sketch, "E360", {"start": v(9.33, -1157) * mm, "end": v(176.8, -1157) * mm});
            skArc(sketch, "E361", {"start": v(176.8, -1157) * mm, "mid": v(180.17, -1153.98) * mm, "end": v(183.31, -1157.25) * mm});
            skLineSegment(sketch, "E362", {"start": v(183.31, -1157.25) * mm, "end": v(183.31, -1175) * mm});
            skLineSegment(sketch, "E363", {"start": v(183.31, -1175) * mm, "end": v(302.81, -1175) * mm});
            skLineSegment(sketch, "E364", {"start": v(-63.27, -869.5) * mm, "end": v(-63.27, 783.27) * mm});
            skLineSegment(sketch, "E365", {"start": v(-63.27, 783.27) * mm, "end": v(-285.36, 783.27) * mm});
            skLineSegment(sketch, "E366", {"start": v(-285.36, 783.27) * mm, "end": v(-285.36, -869.5) * mm});
            skLineSegment(sketch, "E367", {"start": v(-285.36, -869.5) * mm, "end": v(-63.27, -869.5) * mm});
            skLineSegment(sketch, "E368", {"start": v(554.55, 539.67) * mm, "end": v(539.55, 539.67) * mm});
            skArc(sketch, "E369", {"start": v(539.55, 539.67) * mm, "mid": v(536.54, 542.68) * mm, "end": v(539.55, 545.69) * mm});
            skLineSegment(sketch, "E370", {"start": v(539.55, 545.69) * mm, "end": v(539.55, 793.65) * mm});
            skArc(sketch, "E371", {"start": v(539.55, 793.65) * mm, "mid": v(536.54, 796.66) * mm, "end": v(539.55, 799.67) * mm});
            skLineSegment(sketch, "E372", {"start": v(539.55, 799.67) * mm, "end": v(554.55, 799.67) * mm});
            skLineSegment(sketch, "E373", {"start": v(554.55, 799.67) * mm, "end": v(557.55, 802.67) * mm});
            skLineSegment(sketch, "E374", {"start": v(557.55, 802.67) * mm, "end": v(557.55, 836.67) * mm});
            skLineSegment(sketch, "E375", {"start": v(557.55, 836.67) * mm, "end": v(554.55, 839.67) * mm});
            skLineSegment(sketch, "E376", {"start": v(554.55, 839.67) * mm, "end": v(539.55, 839.67) * mm});
            skArc(sketch, "E377", {"start": v(539.55, 839.67) * mm, "mid": v(536.54, 842.68) * mm, "end": v(539.55, 845.69) * mm});
            skLineSegment(sketch, "E378", {"start": v(539.55, 845.69) * mm, "end": v(539.55, 1093.65) * mm});
            skArc(sketch, "E379", {"start": v(539.55, 1093.65) * mm, "mid": v(536.54, 1096.66) * mm, "end": v(539.55, 1099.67) * mm});
            skLineSegment(sketch, "E380", {"start": v(539.55, 1099.67) * mm, "end": v(554.55, 1099.67) * mm});
            skLineSegment(sketch, "E381", {"start": v(554.55, 1099.67) * mm, "end": v(557.55, 1102.67) * mm});
            skLineSegment(sketch, "E382", {"start": v(557.55, 1102.67) * mm, "end": v(557.55, 1136.67) * mm});
            skLineSegment(sketch, "E383", {"start": v(557.55, 1136.67) * mm, "end": v(554.55, 1139.67) * mm});
            skLineSegment(sketch, "E384", {"start": v(554.55, 1139.67) * mm, "end": v(539.55, 1139.67) * mm});
            skArc(sketch, "E385", {"start": v(539.55, 1139.67) * mm, "mid": v(536.54, 1142.68) * mm, "end": v(539.55, 1145.7) * mm});
            skLineSegment(sketch, "E386", {"start": v(539.55, 1145.7) * mm, "end": v(539.55, 1179.67) * mm});
            skLineSegment(sketch, "E387", {"start": v(539.55, 1179.67) * mm, "end": v(425.55, 1179.67) * mm});
            skLineSegment(sketch, "E388", {"start": v(425.55, 1179.67) * mm, "end": v(425.55, 1145.7) * mm});
            skArc(sketch, "E389", {"start": v(425.55, 1145.7) * mm, "mid": v(428.56, 1142.68) * mm, "end": v(425.55, 1139.67) * mm});
            skLineSegment(sketch, "E390", {"start": v(425.55, 1139.67) * mm, "end": v(410.55, 1139.67) * mm});
            skLineSegment(sketch, "E391", {"start": v(410.55, 1139.67) * mm, "end": v(407.55, 1136.67) * mm});
            skLineSegment(sketch, "E392", {"start": v(407.55, 1136.67) * mm, "end": v(407.55, 1102.67) * mm});
            skLineSegment(sketch, "E393", {"start": v(407.55, 1102.67) * mm, "end": v(410.55, 1099.67) * mm});
            skLineSegment(sketch, "E394", {"start": v(410.55, 1099.67) * mm, "end": v(425.55, 1099.67) * mm});
            skArc(sketch, "E395", {"start": v(425.55, 1099.67) * mm, "mid": v(428.56, 1096.66) * mm, "end": v(425.55, 1093.65) * mm});
            skLineSegment(sketch, "E396", {"start": v(425.55, 1093.65) * mm, "end": v(425.55, 845.69) * mm});
            skArc(sketch, "E397", {"start": v(425.55, 845.69) * mm, "mid": v(428.56, 842.68) * mm, "end": v(425.55, 839.67) * mm});
            skLineSegment(sketch, "E398", {"start": v(425.55, 839.67) * mm, "end": v(410.55, 839.67) * mm});
            skLineSegment(sketch, "E399", {"start": v(410.55, 839.67) * mm, "end": v(407.55, 836.67) * mm});
            skLineSegment(sketch, "E400", {"start": v(407.55, 836.67) * mm, "end": v(407.55, 802.67) * mm});
            skLineSegment(sketch, "E401", {"start": v(407.55, 802.67) * mm, "end": v(410.55, 799.67) * mm});
            skLineSegment(sketch, "E402", {"start": v(410.55, 799.67) * mm, "end": v(425.55, 799.67) * mm});
            skArc(sketch, "E403", {"start": v(425.55, 799.67) * mm, "mid": v(428.56, 796.66) * mm, "end": v(425.55, 793.65) * mm});
            skLineSegment(sketch, "E404", {"start": v(425.55, 793.65) * mm, "end": v(425.55, 545.69) * mm});
            skArc(sketch, "E405", {"start": v(425.55, 545.69) * mm, "mid": v(428.56, 542.68) * mm, "end": v(425.55, 539.67) * mm});
            skLineSegment(sketch, "E406", {"start": v(425.55, 539.67) * mm, "end": v(410.55, 539.67) * mm});
            skLineSegment(sketch, "E407", {"start": v(410.55, 539.67) * mm, "end": v(407.55, 536.67) * mm});
            skLineSegment(sketch, "E408", {"start": v(407.55, 536.67) * mm, "end": v(407.55, 502.67) * mm});
            skLineSegment(sketch, "E409", {"start": v(407.55, 502.67) * mm, "end": v(410.55, 499.67) * mm});
            skLineSegment(sketch, "E410", {"start": v(410.55, 499.67) * mm, "end": v(425.55, 499.67) * mm});
            skArc(sketch, "E411", {"start": v(425.55, 499.67) * mm, "mid": v(428.56, 496.66) * mm, "end": v(425.55, 493.65) * mm});
            skLineSegment(sketch, "E412", {"start": v(425.55, 493.65) * mm, "end": v(425.55, 245.69) * mm});
            skArc(sketch, "E413", {"start": v(425.55, 245.69) * mm, "mid": v(428.56, 242.68) * mm, "end": v(425.55, 239.67) * mm});
            skLineSegment(sketch, "E414", {"start": v(425.55, 239.67) * mm, "end": v(410.55, 239.67) * mm});
            skLineSegment(sketch, "E415", {"start": v(410.55, 239.67) * mm, "end": v(407.55, 236.67) * mm});
            skLineSegment(sketch, "E416", {"start": v(407.55, 236.67) * mm, "end": v(407.55, 202.67) * mm});
            skLineSegment(sketch, "E417", {"start": v(407.55, 202.67) * mm, "end": v(410.55, 199.67) * mm});
            skLineSegment(sketch, "E418", {"start": v(410.55, 199.67) * mm, "end": v(425.55, 199.67) * mm});
            skArc(sketch, "E419", {"start": v(425.55, 199.67) * mm, "mid": v(428.56, 196.66) * mm, "end": v(425.55, 193.65) * mm});
            skLineSegment(sketch, "E420", {"start": v(425.55, 193.65) * mm, "end": v(425.55, -54.31) * mm});
            skArc(sketch, "E421", {"start": v(425.55, -54.31) * mm, "mid": v(428.56, -57.32) * mm, "end": v(425.55, -60.33) * mm});
            skLineSegment(sketch, "E422", {"start": v(425.55, -60.33) * mm, "end": v(410.55, -60.33) * mm});
            skLineSegment(sketch, "E423", {"start": v(410.55, -60.33) * mm, "end": v(407.55, -63.33) * mm});
            skLineSegment(sketch, "E424", {"start": v(407.55, -63.33) * mm, "end": v(407.55, -71.33) * mm});
            skLineSegment(sketch, "E425", {"start": v(407.55, -71.33) * mm, "end": v(450.53, -71.33) * mm});
            skArc(sketch, "E426", {"start": v(450.53, -71.33) * mm, "mid": v(453.54, -68.32) * mm, "end": v(456.55, -71.33) * mm});
            skLineSegment(sketch, "E427", {"start": v(456.55, -71.33) * mm, "end": v(456.55, -89.33) * mm});
            skArc(sketch, "E428", {"start": v(456.55, -89.33) * mm, "mid": v(453.54, -92.34) * mm, "end": v(450.53, -89.33) * mm});
            skLineSegment(sketch, "E429", {"start": v(450.53, -89.33) * mm, "end": v(407.55, -89.33) * mm});
            skLineSegment(sketch, "E430", {"start": v(407.55, -89.33) * mm, "end": v(407.55, -97.33) * mm});
            skLineSegment(sketch, "E431", {"start": v(407.55, -97.33) * mm, "end": v(410.55, -100.33) * mm});
            skLineSegment(sketch, "E432", {"start": v(410.55, -100.33) * mm, "end": v(425.55, -100.33) * mm});
            skArc(sketch, "E433", {"start": v(425.55, -100.33) * mm, "mid": v(428.56, -103.34) * mm, "end": v(425.55, -106.35) * mm});
            skLineSegment(sketch, "E434", {"start": v(425.55, -106.35) * mm, "end": v(425.55, -354.31) * mm});
            skArc(sketch, "E435", {"start": v(425.55, -354.31) * mm, "mid": v(428.56, -357.32) * mm, "end": v(425.55, -360.33) * mm});
            skLineSegment(sketch, "E436", {"start": v(425.55, -360.33) * mm, "end": v(410.55, -360.33) * mm});
            skLineSegment(sketch, "E437", {"start": v(410.55, -360.33) * mm, "end": v(407.55, -363.33) * mm});
            skLineSegment(sketch, "E438", {"start": v(407.55, -363.33) * mm, "end": v(407.55, -397.33) * mm});
            skLineSegment(sketch, "E439", {"start": v(407.55, -397.33) * mm, "end": v(410.55, -400.33) * mm});
            skLineSegment(sketch, "E440", {"start": v(410.55, -400.33) * mm, "end": v(425.55, -400.33) * mm});
            skArc(sketch, "E441", {"start": v(425.55, -400.33) * mm, "mid": v(428.56, -403.34) * mm, "end": v(425.55, -406.35) * mm});
            skLineSegment(sketch, "E442", {"start": v(425.55, -406.35) * mm, "end": v(425.55, -654.31) * mm});
            skArc(sketch, "E443", {"start": v(425.55, -654.31) * mm, "mid": v(428.56, -657.32) * mm, "end": v(425.55, -660.33) * mm});
            skLineSegment(sketch, "E444", {"start": v(425.55, -660.33) * mm, "end": v(410.55, -660.33) * mm});
            skLineSegment(sketch, "E445", {"start": v(410.55, -660.33) * mm, "end": v(407.55, -663.33) * mm});
            skLineSegment(sketch, "E446", {"start": v(407.55, -663.33) * mm, "end": v(407.55, -697.33) * mm});
            skLineSegment(sketch, "E447", {"start": v(407.55, -697.33) * mm, "end": v(410.55, -700.33) * mm});
            skLineSegment(sketch, "E448", {"start": v(410.55, -700.33) * mm, "end": v(425.55, -700.33) * mm});
            skArc(sketch, "E449", {"start": v(425.55, -700.33) * mm, "mid": v(428.56, -703.34) * mm, "end": v(425.55, -706.35) * mm});
            skLineSegment(sketch, "E450", {"start": v(425.55, -706.35) * mm, "end": v(425.55, -874.31) * mm});
            skArc(sketch, "E451", {"start": v(425.55, -874.31) * mm, "mid": v(428.56, -877.32) * mm, "end": v(425.55, -880.33) * mm});
            skLineSegment(sketch, "E452", {"start": v(425.55, -880.33) * mm, "end": v(410.55, -880.33) * mm});
            skLineSegment(sketch, "E453", {"start": v(410.55, -880.33) * mm, "end": v(407.55, -883.33) * mm});
            skLineSegment(sketch, "E454", {"start": v(407.55, -883.33) * mm, "end": v(407.55, -917.33) * mm});
            skLineSegment(sketch, "E455", {"start": v(407.55, -917.33) * mm, "end": v(410.55, -920.33) * mm});
            skLineSegment(sketch, "E456", {"start": v(410.55, -920.33) * mm, "end": v(425.55, -920.33) * mm});
            skArc(sketch, "E457", {"start": v(425.55, -920.33) * mm, "mid": v(428.56, -923.34) * mm, "end": v(425.55, -926.35) * mm});
            skLineSegment(sketch, "E458", {"start": v(425.55, -926.35) * mm, "end": v(425.55, -1180.1) * mm});
            skLineSegment(sketch, "E459", {"start": v(425.55, -1180.1) * mm, "end": v(539.55, -1180.1) * mm});
            skLineSegment(sketch, "E460", {"start": v(539.55, -1180.1) * mm, "end": v(539.55, -926.35) * mm});
            skArc(sketch, "E461", {"start": v(539.55, -926.35) * mm, "mid": v(536.54, -923.34) * mm, "end": v(539.55, -920.33) * mm});
            skLineSegment(sketch, "E462", {"start": v(539.55, -920.33) * mm, "end": v(554.55, -920.33) * mm});
            skLineSegment(sketch, "E463", {"start": v(554.55, -920.33) * mm, "end": v(557.55, -917.33) * mm});
            skLineSegment(sketch, "E464", {"start": v(557.55, -917.33) * mm, "end": v(557.55, -883.33) * mm});
            skLineSegment(sketch, "E465", {"start": v(557.55, -883.33) * mm, "end": v(554.55, -880.33) * mm});
            skLineSegment(sketch, "E466", {"start": v(554.55, -880.33) * mm, "end": v(539.55, -880.33) * mm});
            skArc(sketch, "E467", {"start": v(539.55, -880.33) * mm, "mid": v(536.54, -877.32) * mm, "end": v(539.55, -874.31) * mm});
            skLineSegment(sketch, "E468", {"start": v(539.55, -874.31) * mm, "end": v(539.55, -706.35) * mm});
            skArc(sketch, "E469", {"start": v(539.55, -706.35) * mm, "mid": v(536.54, -703.34) * mm, "end": v(539.55, -700.33) * mm});
            skLineSegment(sketch, "E470", {"start": v(539.55, -700.33) * mm, "end": v(554.55, -700.33) * mm});
            skLineSegment(sketch, "E471", {"start": v(554.55, -700.33) * mm, "end": v(557.55, -697.33) * mm});
            skLineSegment(sketch, "E472", {"start": v(557.55, -697.33) * mm, "end": v(557.55, -663.33) * mm});
            skLineSegment(sketch, "E473", {"start": v(557.55, -663.33) * mm, "end": v(554.55, -660.33) * mm});
            skLineSegment(sketch, "E474", {"start": v(554.55, -660.33) * mm, "end": v(539.55, -660.33) * mm});
            skArc(sketch, "E475", {"start": v(539.55, -660.33) * mm, "mid": v(536.54, -657.32) * mm, "end": v(539.55, -654.31) * mm});
            skLineSegment(sketch, "E476", {"start": v(539.55, -654.31) * mm, "end": v(539.55, -406.35) * mm});
            skArc(sketch, "E477", {"start": v(539.55, -406.35) * mm, "mid": v(536.54, -403.34) * mm, "end": v(539.55, -400.33) * mm});
            skLineSegment(sketch, "E478", {"start": v(539.55, -400.33) * mm, "end": v(554.55, -400.33) * mm});
            skLineSegment(sketch, "E479", {"start": v(554.55, -400.33) * mm, "end": v(557.55, -397.33) * mm});
            skLineSegment(sketch, "E480", {"start": v(557.55, -397.33) * mm, "end": v(557.55, -363.33) * mm});
            skLineSegment(sketch, "E481", {"start": v(557.55, -363.33) * mm, "end": v(554.55, -360.33) * mm});
            skLineSegment(sketch, "E482", {"start": v(554.55, -360.33) * mm, "end": v(539.55, -360.33) * mm});
            skArc(sketch, "E483", {"start": v(539.55, -360.33) * mm, "mid": v(536.54, -357.32) * mm, "end": v(539.55, -354.31) * mm});
            skLineSegment(sketch, "E484", {"start": v(539.55, -354.31) * mm, "end": v(539.55, -106.35) * mm});
            skArc(sketch, "E485", {"start": v(539.55, -106.35) * mm, "mid": v(536.54, -103.34) * mm, "end": v(539.55, -100.33) * mm});
            skLineSegment(sketch, "E486", {"start": v(539.55, -100.33) * mm, "end": v(554.55, -100.33) * mm});
            skLineSegment(sketch, "E487", {"start": v(554.55, -100.33) * mm, "end": v(557.55, -97.33) * mm});
            skLineSegment(sketch, "E488", {"start": v(557.55, -97.33) * mm, "end": v(557.54, -89.33) * mm});
            skLineSegment(sketch, "E489", {"start": v(557.54, -89.33) * mm, "end": v(514.56, -89.33) * mm});
            skArc(sketch, "E490", {"start": v(514.56, -89.33) * mm, "mid": v(511.55, -92.34) * mm, "end": v(508.54, -89.33) * mm});
            skLineSegment(sketch, "E491", {"start": v(508.54, -89.33) * mm, "end": v(508.54, -71.33) * mm});
            skArc(sketch, "E492", {"start": v(508.54, -71.33) * mm, "mid": v(511.55, -68.32) * mm, "end": v(514.56, -71.33) * mm});
            skLineSegment(sketch, "E493", {"start": v(514.56, -71.33) * mm, "end": v(557.54, -71.33) * mm});
            skLineSegment(sketch, "E494", {"start": v(557.54, -71.33) * mm, "end": v(557.55, -63.33) * mm});
            skLineSegment(sketch, "E495", {"start": v(557.55, -63.33) * mm, "end": v(554.55, -60.33) * mm});
            skLineSegment(sketch, "E496", {"start": v(554.55, -60.33) * mm, "end": v(539.55, -60.33) * mm});
            skArc(sketch, "E497", {"start": v(539.55, -60.33) * mm, "mid": v(536.54, -57.32) * mm, "end": v(539.55, -54.31) * mm});
            skLineSegment(sketch, "E498", {"start": v(539.55, -54.31) * mm, "end": v(539.55, 193.65) * mm});
            skArc(sketch, "E499", {"start": v(539.55, 193.65) * mm, "mid": v(536.54, 196.66) * mm, "end": v(539.55, 199.67) * mm});
            skLineSegment(sketch, "E500", {"start": v(539.55, 199.67) * mm, "end": v(554.55, 199.67) * mm});
            skLineSegment(sketch, "E501", {"start": v(554.55, 199.67) * mm, "end": v(557.55, 202.67) * mm});
            skLineSegment(sketch, "E502", {"start": v(557.55, 202.67) * mm, "end": v(557.55, 236.67) * mm});
            skLineSegment(sketch, "E503", {"start": v(557.55, 236.67) * mm, "end": v(554.55, 239.67) * mm});
            skLineSegment(sketch, "E504", {"start": v(554.55, 239.67) * mm, "end": v(539.55, 239.67) * mm});
            skArc(sketch, "E505", {"start": v(539.55, 239.67) * mm, "mid": v(536.54, 242.68) * mm, "end": v(539.55, 245.69) * mm});
            skLineSegment(sketch, "E506", {"start": v(539.55, 245.69) * mm, "end": v(539.55, 493.65) * mm});
            skArc(sketch, "E507", {"start": v(539.55, 493.65) * mm, "mid": v(536.54, 496.66) * mm, "end": v(539.55, 499.67) * mm});
            skLineSegment(sketch, "E508", {"start": v(539.55, 499.67) * mm, "end": v(554.55, 499.67) * mm});
            skLineSegment(sketch, "E509", {"start": v(554.55, 499.67) * mm, "end": v(557.55, 502.67) * mm});
            skLineSegment(sketch, "E510", {"start": v(557.55, 502.67) * mm, "end": v(557.55, 536.67) * mm});
            skLineSegment(sketch, "E511", {"start": v(557.55, 536.67) * mm, "end": v(554.55, 539.67) * mm});
            skLineSegment(sketch, "E512", {"start": v(-25.4, -627.52) * mm, "end": v(-25.4, -677.52) * mm});
            skLineSegment(sketch, "E513", {"start": v(-25.4, -677.52) * mm, "end": v(-2.4, -677.52) * mm});
            skLineSegment(sketch, "E514", {"start": v(-2.4, -677.52) * mm, "end": v(-2.4, -687.52) * mm});
            skLineSegment(sketch, "E515", {"start": v(-2.4, -687.52) * mm, "end": v(-7.4, -687.52) * mm});
            skLineSegment(sketch, "E516", {"start": v(-7.4, -687.52) * mm, "end": v(-7.4, -767.52) * mm});
            skLineSegment(sketch, "E517", {"start": v(-7.4, -767.52) * mm, "end": v(-2.4, -767.52) * mm});
            skLineSegment(sketch, "E518", {"start": v(-2.4, -767.52) * mm, "end": v(-2.4, -777.52) * mm});
            skLineSegment(sketch, "E519", {"start": v(-2.4, -777.52) * mm, "end": v(-25.4, -777.52) * mm});
            skLineSegment(sketch, "E520", {"start": v(-25.4, -777.52) * mm, "end": v(-25.4, -827.52) * mm});
            skLineSegment(sketch, "E521", {"start": v(-25.4, -827.52) * mm, "end": v(374.6, -827.52) * mm});
            skLineSegment(sketch, "E522", {"start": v(374.6, -827.52) * mm, "end": v(374.6, -777.52) * mm});
            skLineSegment(sketch, "E523", {"start": v(374.6, -777.52) * mm, "end": v(351.6, -777.52) * mm});
            skLineSegment(sketch, "E524", {"start": v(351.6, -777.52) * mm, "end": v(351.6, -767.52) * mm});
            skLineSegment(sketch, "E525", {"start": v(351.6, -767.52) * mm, "end": v(356.6, -767.52) * mm});
            skLineSegment(sketch, "E526", {"start": v(356.6, -767.52) * mm, "end": v(356.6, -687.52) * mm});
            skLineSegment(sketch, "E527", {"start": v(356.6, -687.52) * mm, "end": v(351.6, -687.52) * mm});
            skLineSegment(sketch, "E528", {"start": v(351.6, -687.52) * mm, "end": v(351.6, -677.52) * mm});
            skLineSegment(sketch, "E529", {"start": v(351.6, -677.52) * mm, "end": v(374.6, -677.52) * mm});
            skLineSegment(sketch, "E530", {"start": v(374.6, -677.52) * mm, "end": v(374.6, -627.52) * mm});
            skLineSegment(sketch, "E531", {"start": v(374.6, -627.52) * mm, "end": v(-25.4, -627.52) * mm});
            skLineSegment(sketch, "E532", {"start": v(223.06, -1139.25) * mm, "end": v(223.06, -1157.25) * mm});
            skLineSegment(sketch, "E533", {"start": v(223.06, -1157.25) * mm, "end": v(263.06, -1157.25) * mm});
            skLineSegment(sketch, "E534", {"start": v(263.06, -1157.25) * mm, "end": v(263.06, -1139.25) * mm});
            skLineSegment(sketch, "E535", {"start": v(263.06, -1139.25) * mm, "end": v(223.06, -1139.25) * mm});
            skLineSegment(sketch, "E536", {"start": v(-76.94, -1139.25) * mm, "end": v(-76.94, -1157.25) * mm});
            skLineSegment(sketch, "E537", {"start": v(-76.94, -1157.25) * mm, "end": v(-36.94, -1157.25) * mm});
            skLineSegment(sketch, "E538", {"start": v(-36.94, -1157.25) * mm, "end": v(-36.94, -1139.25) * mm});
            skLineSegment(sketch, "E539", {"start": v(-36.94, -1139.25) * mm, "end": v(-76.94, -1139.25) * mm});
            skLineSegment(sketch, "E540", {"start": v(-296.94, -1139.25) * mm, "end": v(-296.94, -1157.25) * mm});
            skLineSegment(sketch, "E541", {"start": v(-296.94, -1157.25) * mm, "end": v(-256.94, -1157.25) * mm});
            skLineSegment(sketch, "E542", {"start": v(-256.94, -1157.25) * mm, "end": v(-256.94, -1139.25) * mm});
            skLineSegment(sketch, "E543", {"start": v(-256.94, -1139.25) * mm, "end": v(-296.94, -1139.25) * mm});
            skLineSegment(sketch, "E544", {"start": v(223.06, -907.25) * mm, "end": v(223.06, -925.25) * mm});
            skLineSegment(sketch, "E545", {"start": v(223.06, -925.25) * mm, "end": v(263.06, -925.25) * mm});
            skLineSegment(sketch, "E546", {"start": v(263.06, -925.25) * mm, "end": v(263.06, -907.25) * mm});
            skLineSegment(sketch, "E547", {"start": v(263.06, -907.25) * mm, "end": v(223.06, -907.25) * mm});
            skLineSegment(sketch, "E548", {"start": v(-76.94, -907.25) * mm, "end": v(-76.94, -925.25) * mm});
            skLineSegment(sketch, "E549", {"start": v(-76.94, -925.25) * mm, "end": v(-36.94, -925.25) * mm});
            skLineSegment(sketch, "E550", {"start": v(-36.94, -925.25) * mm, "end": v(-36.94, -907.25) * mm});
            skLineSegment(sketch, "E551", {"start": v(-36.94, -907.25) * mm, "end": v(-76.94, -907.25) * mm});
            skLineSegment(sketch, "E552", {"start": v(-296.94, -907.25) * mm, "end": v(-296.94, -925.25) * mm});
            skLineSegment(sketch, "E553", {"start": v(-296.94, -925.25) * mm, "end": v(-256.94, -925.25) * mm});
            skLineSegment(sketch, "E554", {"start": v(-256.94, -925.25) * mm, "end": v(-256.94, -907.25) * mm});
            skLineSegment(sketch, "E555", {"start": v(-256.94, -907.25) * mm, "end": v(-296.94, -907.25) * mm});
            skLineSegment(sketch, "E556", {"start": v(-556.7, -839.48) * mm, "end": v(-574.7, -839.48) * mm});
            skLineSegment(sketch, "E557", {"start": v(-574.7, -839.48) * mm, "end": v(-574.7, -879.48) * mm});
            skLineSegment(sketch, "E558", {"start": v(-574.7, -879.48) * mm, "end": v(-556.7, -879.48) * mm});
            skLineSegment(sketch, "E559", {"start": v(-556.7, -879.48) * mm, "end": v(-556.7, -839.48) * mm});
            skLineSegment(sketch, "E560", {"start": v(-342.7, -839.48) * mm, "end": v(-342.7, -879.48) * mm});
            skLineSegment(sketch, "E561", {"start": v(-342.7, -879.48) * mm, "end": v(-324.7, -879.48) * mm});
            skLineSegment(sketch, "E562", {"start": v(-324.7, -879.48) * mm, "end": v(-324.7, -839.48) * mm});
            skLineSegment(sketch, "E563", {"start": v(-324.7, -839.48) * mm, "end": v(-342.7, -839.48) * mm});
            skLineSegment(sketch, "E564", {"start": v(-556.7, -619.48) * mm, "end": v(-574.7, -619.48) * mm});
            skLineSegment(sketch, "E565", {"start": v(-574.7, -619.48) * mm, "end": v(-574.7, -659.48) * mm});
            skLineSegment(sketch, "E566", {"start": v(-574.7, -659.48) * mm, "end": v(-556.7, -659.48) * mm});
            skLineSegment(sketch, "E567", {"start": v(-556.7, -659.48) * mm, "end": v(-556.7, -619.48) * mm});
            skLineSegment(sketch, "E568", {"start": v(-342.7, -619.48) * mm, "end": v(-342.7, -659.48) * mm});
            skLineSegment(sketch, "E569", {"start": v(-342.7, -659.48) * mm, "end": v(-324.7, -659.48) * mm});
            skLineSegment(sketch, "E570", {"start": v(-324.7, -659.48) * mm, "end": v(-324.7, -619.48) * mm});
            skLineSegment(sketch, "E571", {"start": v(-324.7, -619.48) * mm, "end": v(-342.7, -619.48) * mm});
            skLineSegment(sketch, "E572", {"start": v(-556.7, -319.48) * mm, "end": v(-574.7, -319.48) * mm});
            skLineSegment(sketch, "E573", {"start": v(-574.7, -319.48) * mm, "end": v(-574.7, -359.48) * mm});
            skLineSegment(sketch, "E574", {"start": v(-574.7, -359.48) * mm, "end": v(-556.7, -359.48) * mm});
            skLineSegment(sketch, "E575", {"start": v(-556.7, -359.48) * mm, "end": v(-556.7, -319.48) * mm});
            skLineSegment(sketch, "E576", {"start": v(-342.7, -319.48) * mm, "end": v(-342.7, -359.48) * mm});
            skLineSegment(sketch, "E577", {"start": v(-342.7, -359.48) * mm, "end": v(-324.7, -359.48) * mm});
            skLineSegment(sketch, "E578", {"start": v(-324.7, -359.48) * mm, "end": v(-324.7, -319.48) * mm});
            skLineSegment(sketch, "E579", {"start": v(-324.7, -319.48) * mm, "end": v(-342.7, -319.48) * mm});
            skLineSegment(sketch, "E580", {"start": v(-556.7, 240.52) * mm, "end": v(-556.7, 280.52) * mm});
            skLineSegment(sketch, "E581", {"start": v(-556.7, 280.52) * mm, "end": v(-574.7, 280.52) * mm});
            skLineSegment(sketch, "E582", {"start": v(-574.7, 280.52) * mm, "end": v(-574.7, 240.52) * mm});
            skLineSegment(sketch, "E583", {"start": v(-574.7, 240.52) * mm, "end": v(-556.7, 240.52) * mm});
            skLineSegment(sketch, "E584", {"start": v(-556.7, -19.48) * mm, "end": v(-574.7, -19.48) * mm});
            skLineSegment(sketch, "E585", {"start": v(-574.7, -19.48) * mm, "end": v(-574.7, -59.48) * mm});
            skLineSegment(sketch, "E586", {"start": v(-574.7, -59.48) * mm, "end": v(-556.7, -59.48) * mm});
            skLineSegment(sketch, "E587", {"start": v(-556.7, -59.48) * mm, "end": v(-556.7, -19.48) * mm});
            skLineSegment(sketch, "E588", {"start": v(-342.7, 240.52) * mm, "end": v(-324.7, 240.52) * mm});
            skLineSegment(sketch, "E589", {"start": v(-324.7, 240.52) * mm, "end": v(-324.7, 280.52) * mm});
            skLineSegment(sketch, "E590", {"start": v(-324.7, 280.52) * mm, "end": v(-342.7, 280.52) * mm});
            skLineSegment(sketch, "E591", {"start": v(-342.7, 280.52) * mm, "end": v(-342.7, 240.52) * mm});
            skLineSegment(sketch, "E592", {"start": v(-429.7, -30.48) * mm, "end": v(-469.7, -30.48) * mm});
            skLineSegment(sketch, "E593", {"start": v(-469.7, -30.48) * mm, "end": v(-469.7, -48.48) * mm});
            skLineSegment(sketch, "E594", {"start": v(-469.7, -48.48) * mm, "end": v(-429.7, -48.48) * mm});
            skLineSegment(sketch, "E595", {"start": v(-429.7, -48.48) * mm, "end": v(-429.7, -30.48) * mm});
            skLineSegment(sketch, "E596", {"start": v(-342.7, -19.48) * mm, "end": v(-342.7, -59.48) * mm});
            skLineSegment(sketch, "E597", {"start": v(-342.7, -59.48) * mm, "end": v(-324.7, -59.48) * mm});
            skLineSegment(sketch, "E598", {"start": v(-324.7, -59.48) * mm, "end": v(-324.7, -19.48) * mm});
            skLineSegment(sketch, "E599", {"start": v(-324.7, -19.48) * mm, "end": v(-342.7, -19.48) * mm});
            skArc(sketch, "E600", {"start": v(-419.45, 269.52) * mm, "mid": v(-422.6, 272.78) * mm, "end": v(-425.97, 269.77) * mm});
            skLineSegment(sketch, "E601", {"start": v(-425.97, 269.77) * mm, "end": v(-473.44, 269.77) * mm});
            skArc(sketch, "E602", {"start": v(-473.44, 269.77) * mm, "mid": v(-476.81, 272.77) * mm, "end": v(-479.95, 269.52) * mm});
            skLineSegment(sketch, "E603", {"start": v(-479.95, 269.52) * mm, "end": v(-479.95, 251.52) * mm});
            skArc(sketch, "E604", {"start": v(-479.95, 251.52) * mm, "mid": v(-476.81, 248.25) * mm, "end": v(-473.44, 251.27) * mm});
            skLineSegment(sketch, "E605", {"start": v(-473.44, 251.27) * mm, "end": v(-425.97, 251.27) * mm});
            skArc(sketch, "E606", {"start": v(-425.97, 251.27) * mm, "mid": v(-422.6, 248.26) * mm, "end": v(-419.45, 251.52) * mm});
            skLineSegment(sketch, "E607", {"start": v(-419.45, 251.52) * mm, "end": v(-419.45, 269.52) * mm});
            skArc(sketch, "E608", {"start": v(-419.45, -330.48) * mm, "mid": v(-422.6, -327.22) * mm, "end": v(-425.97, -330.23) * mm});
            skLineSegment(sketch, "E609", {"start": v(-425.97, -330.23) * mm, "end": v(-473.44, -330.23) * mm});
            skArc(sketch, "E610", {"start": v(-473.44, -330.23) * mm, "mid": v(-476.81, -327.23) * mm, "end": v(-479.95, -330.48) * mm});
            skLineSegment(sketch, "E611", {"start": v(-479.95, -330.48) * mm, "end": v(-479.95, -348.48) * mm});
            skArc(sketch, "E612", {"start": v(-479.95, -348.48) * mm, "mid": v(-476.81, -351.75) * mm, "end": v(-473.44, -348.73) * mm});
            skLineSegment(sketch, "E613", {"start": v(-473.44, -348.73) * mm, "end": v(-425.97, -348.73) * mm});
            skArc(sketch, "E614", {"start": v(-425.97, -348.73) * mm, "mid": v(-422.6, -351.74) * mm, "end": v(-419.45, -348.48) * mm});
            skLineSegment(sketch, "E615", {"start": v(-419.45, -348.48) * mm, "end": v(-419.45, -330.48) * mm});
            skArc(sketch, "E616", {"start": v(-419.45, -850.48) * mm, "mid": v(-422.6, -847.22) * mm, "end": v(-425.97, -850.23) * mm});
            skLineSegment(sketch, "E617", {"start": v(-425.97, -850.23) * mm, "end": v(-473.44, -850.23) * mm});
            skArc(sketch, "E618", {"start": v(-473.44, -850.23) * mm, "mid": v(-476.81, -847.23) * mm, "end": v(-479.95, -850.48) * mm});
            skLineSegment(sketch, "E619", {"start": v(-479.95, -850.48) * mm, "end": v(-479.95, -868.48) * mm});
            skArc(sketch, "E620", {"start": v(-479.95, -868.48) * mm, "mid": v(-476.81, -871.75) * mm, "end": v(-473.44, -868.73) * mm});
            skLineSegment(sketch, "E621", {"start": v(-473.44, -868.73) * mm, "end": v(-425.97, -868.73) * mm});
            skArc(sketch, "E622", {"start": v(-425.97, -868.73) * mm, "mid": v(-422.6, -871.74) * mm, "end": v(-419.45, -868.48) * mm});
            skLineSegment(sketch, "E623", {"start": v(-419.45, -868.48) * mm, "end": v(-419.45, -850.48) * mm});
            skArc(sketch, "E624", {"start": v(-342.7, -992) * mm, "mid": v(-345.97, -995.14) * mm, "end": v(-342.95, -998.52) * mm});
            skLineSegment(sketch, "E625", {"start": v(-342.95, -998.52) * mm, "end": v(-342.95, -1065.98) * mm});
            skArc(sketch, "E626", {"start": v(-342.95, -1065.98) * mm, "mid": v(-345.96, -1069.36) * mm, "end": v(-342.7, -1072.5) * mm});
            skLineSegment(sketch, "E627", {"start": v(-342.7, -1072.5) * mm, "end": v(-324.7, -1072.5) * mm});
            skArc(sketch, "E628", {"start": v(-324.7, -1072.5) * mm, "mid": v(-321.44, -1069.36) * mm, "end": v(-324.45, -1065.98) * mm});
            skLineSegment(sketch, "E629", {"start": v(-324.45, -1065.98) * mm, "end": v(-324.45, -998.52) * mm});
            skArc(sketch, "E630", {"start": v(-324.45, -998.52) * mm, "mid": v(-321.45, -995.14) * mm, "end": v(-324.7, -992) * mm});
            skLineSegment(sketch, "E631", {"start": v(-324.7, -992) * mm, "end": v(-342.7, -992) * mm});
            skLineSegment(sketch, "E632", {"start": v(330.56, -322.72) * mm, "end": v(330.56, -362.72) * mm});
            skLineSegment(sketch, "E633", {"start": v(330.56, -362.72) * mm, "end": v(348.56, -362.72) * mm});
            skLineSegment(sketch, "E634", {"start": v(348.56, -362.72) * mm, "end": v(348.56, -322.72) * mm});
            skLineSegment(sketch, "E635", {"start": v(348.56, -322.72) * mm, "end": v(330.56, -322.72) * mm});
            skLineSegment(sketch, "E636", {"start": v(98.56, -322.72) * mm, "end": v(98.56, -362.72) * mm});
            skLineSegment(sketch, "E637", {"start": v(98.56, -362.72) * mm, "end": v(116.56, -362.72) * mm});
            skLineSegment(sketch, "E638", {"start": v(116.56, -362.72) * mm, "end": v(116.56, -322.72) * mm});
            skLineSegment(sketch, "E639", {"start": v(116.56, -322.72) * mm, "end": v(98.56, -322.72) * mm});
            skLineSegment(sketch, "E640", {"start": v(330.56, -22.72) * mm, "end": v(330.56, -62.72) * mm});
            skLineSegment(sketch, "E641", {"start": v(330.56, -62.72) * mm, "end": v(348.56, -62.72) * mm});
            skLineSegment(sketch, "E642", {"start": v(348.56, -62.72) * mm, "end": v(348.56, -22.72) * mm});
            skLineSegment(sketch, "E643", {"start": v(348.56, -22.72) * mm, "end": v(330.56, -22.72) * mm});
            skLineSegment(sketch, "E644", {"start": v(203.56, -33.72) * mm, "end": v(203.56, -51.72) * mm});
            skLineSegment(sketch, "E645", {"start": v(203.56, -51.72) * mm, "end": v(243.56, -51.72) * mm});
            skLineSegment(sketch, "E646", {"start": v(243.56, -51.72) * mm, "end": v(243.56, -33.72) * mm});
            skLineSegment(sketch, "E647", {"start": v(243.56, -33.72) * mm, "end": v(203.56, -33.72) * mm});
            skLineSegment(sketch, "E648", {"start": v(98.56, -22.72) * mm, "end": v(98.56, -62.72) * mm});
            skLineSegment(sketch, "E649", {"start": v(98.56, -62.72) * mm, "end": v(116.56, -62.72) * mm});
            skLineSegment(sketch, "E650", {"start": v(116.56, -62.72) * mm, "end": v(116.56, -22.72) * mm});
            skLineSegment(sketch, "E651", {"start": v(116.56, -22.72) * mm, "end": v(98.56, -22.72) * mm});
            skLineSegment(sketch, "E652", {"start": v(330.56, 277.28) * mm, "end": v(330.56, 237.28) * mm});
            skLineSegment(sketch, "E653", {"start": v(330.56, 237.28) * mm, "end": v(348.56, 237.28) * mm});
            skLineSegment(sketch, "E654", {"start": v(348.56, 237.28) * mm, "end": v(348.56, 277.28) * mm});
            skLineSegment(sketch, "E655", {"start": v(348.56, 277.28) * mm, "end": v(330.56, 277.28) * mm});
            skLineSegment(sketch, "E656", {"start": v(98.56, 277.28) * mm, "end": v(98.56, 237.28) * mm});
            skLineSegment(sketch, "E657", {"start": v(98.56, 237.28) * mm, "end": v(116.56, 237.28) * mm});
            skLineSegment(sketch, "E658", {"start": v(116.56, 237.28) * mm, "end": v(116.56, 277.28) * mm});
            skLineSegment(sketch, "E659", {"start": v(116.56, 277.28) * mm, "end": v(98.56, 277.28) * mm});
            skLineSegment(sketch, "E660", {"start": v(330.56, 577.28) * mm, "end": v(330.56, 537.28) * mm});
            skLineSegment(sketch, "E661", {"start": v(330.56, 537.28) * mm, "end": v(348.56, 537.28) * mm});
            skLineSegment(sketch, "E662", {"start": v(348.56, 537.28) * mm, "end": v(348.56, 577.28) * mm});
            skLineSegment(sketch, "E663", {"start": v(348.56, 577.28) * mm, "end": v(330.56, 577.28) * mm});
            skLineSegment(sketch, "E664", {"start": v(330.56, 797.28) * mm, "end": v(330.56, 757.28) * mm});
            skLineSegment(sketch, "E665", {"start": v(330.56, 757.28) * mm, "end": v(348.56, 757.28) * mm});
            skLineSegment(sketch, "E666", {"start": v(348.56, 757.28) * mm, "end": v(348.56, 797.28) * mm});
            skLineSegment(sketch, "E667", {"start": v(348.56, 797.28) * mm, "end": v(330.56, 797.28) * mm});
            skLineSegment(sketch, "E668", {"start": v(98.56, 577.28) * mm, "end": v(98.56, 537.28) * mm});
            skLineSegment(sketch, "E669", {"start": v(98.56, 537.28) * mm, "end": v(116.56, 537.28) * mm});
            skLineSegment(sketch, "E670", {"start": v(116.56, 537.28) * mm, "end": v(116.56, 577.28) * mm});
            skLineSegment(sketch, "E671", {"start": v(116.56, 577.28) * mm, "end": v(98.56, 577.28) * mm});
            skLineSegment(sketch, "E672", {"start": v(-449.2, 843.05) * mm, "end": v(-489.2, 843.05) * mm});
            skLineSegment(sketch, "E673", {"start": v(-489.2, 843.05) * mm, "end": v(-489.2, 825.05) * mm});
            skLineSegment(sketch, "E674", {"start": v(-489.2, 825.05) * mm, "end": v(-449.2, 825.05) * mm});
            skLineSegment(sketch, "E675", {"start": v(-449.2, 825.05) * mm, "end": v(-449.2, 843.05) * mm});
            skLineSegment(sketch, "E676", {"start": v(98.56, 797.28) * mm, "end": v(98.56, 757.28) * mm});
            skLineSegment(sketch, "E677", {"start": v(98.56, 757.28) * mm, "end": v(116.56, 757.28) * mm});
            skLineSegment(sketch, "E678", {"start": v(116.56, 757.28) * mm, "end": v(116.56, 797.28) * mm});
            skLineSegment(sketch, "E679", {"start": v(116.56, 797.28) * mm, "end": v(98.56, 797.28) * mm});
            skLineSegment(sketch, "E680", {"start": v(-449.2, 1057.05) * mm, "end": v(-449.2, 1075.05) * mm});
            skLineSegment(sketch, "E681", {"start": v(-449.2, 1075.05) * mm, "end": v(-489.2, 1075.05) * mm});
            skLineSegment(sketch, "E682", {"start": v(-489.2, 1075.05) * mm, "end": v(-489.2, 1057.05) * mm});
            skLineSegment(sketch, "E683", {"start": v(-489.2, 1057.05) * mm, "end": v(-449.2, 1057.05) * mm});
            skLineSegment(sketch, "E684", {"start": v(30.8, 843.05) * mm, "end": v(30.8, 825.05) * mm});
            skLineSegment(sketch, "E685", {"start": v(30.8, 825.05) * mm, "end": v(70.8, 825.05) * mm});
            skLineSegment(sketch, "E686", {"start": v(70.8, 825.05) * mm, "end": v(70.8, 843.05) * mm});
            skLineSegment(sketch, "E687", {"start": v(70.8, 843.05) * mm, "end": v(30.8, 843.05) * mm});
            skLineSegment(sketch, "E688", {"start": v(30.8, 1057.05) * mm, "end": v(70.8, 1057.05) * mm});
            skLineSegment(sketch, "E689", {"start": v(70.8, 1057.05) * mm, "end": v(70.8, 1075.05) * mm});
            skLineSegment(sketch, "E690", {"start": v(70.8, 1075.05) * mm, "end": v(30.8, 1075.05) * mm});
            skLineSegment(sketch, "E691", {"start": v(30.8, 1075.05) * mm, "end": v(30.8, 1057.05) * mm});
            skLineSegment(sketch, "E692", {"start": v(-149.2, 843.05) * mm, "end": v(-189.2, 843.05) * mm});
            skLineSegment(sketch, "E693", {"start": v(-189.2, 843.05) * mm, "end": v(-189.2, 825.05) * mm});
            skLineSegment(sketch, "E694", {"start": v(-189.2, 825.05) * mm, "end": v(-149.2, 825.05) * mm});
            skLineSegment(sketch, "E695", {"start": v(-149.2, 825.05) * mm, "end": v(-149.2, 843.05) * mm});
            skLineSegment(sketch, "E696", {"start": v(-149.2, 1057.05) * mm, "end": v(-149.2, 1075.05) * mm});
            skLineSegment(sketch, "E697", {"start": v(-149.2, 1075.05) * mm, "end": v(-189.2, 1075.05) * mm});
            skLineSegment(sketch, "E698", {"start": v(-189.2, 1075.05) * mm, "end": v(-189.2, 1057.05) * mm});
            skLineSegment(sketch, "E699", {"start": v(-189.2, 1057.05) * mm, "end": v(-149.2, 1057.05) * mm});
            skArc(sketch, "E700", {"start": v(-478.46, 926.31) * mm, "mid": v(-481.47, 922.94) * mm, "end": v(-478.2, 919.8) * mm});
            skLineSegment(sketch, "E701", {"start": v(-478.2, 919.8) * mm, "end": v(-460.2, 919.8) * mm});
            skArc(sketch, "E702", {"start": v(-460.2, 919.8) * mm, "mid": v(-456.95, 922.94) * mm, "end": v(-459.96, 926.31) * mm});
            skLineSegment(sketch, "E703", {"start": v(-459.96, 926.31) * mm, "end": v(-459.96, 973.78) * mm});
            skArc(sketch, "E704", {"start": v(-459.96, 973.78) * mm, "mid": v(-456.95, 977.16) * mm, "end": v(-460.2, 980.3) * mm});
            skLineSegment(sketch, "E705", {"start": v(-460.2, 980.3) * mm, "end": v(-478.2, 980.3) * mm});
            skArc(sketch, "E706", {"start": v(-478.2, 980.3) * mm, "mid": v(-481.47, 977.16) * mm, "end": v(-478.46, 973.78) * mm});
            skLineSegment(sketch, "E707", {"start": v(-478.46, 973.78) * mm, "end": v(-478.46, 926.31) * mm});
            skArc(sketch, "E708", {"start": v(41.54, 926.31) * mm, "mid": v(38.53, 922.93) * mm, "end": v(41.8, 919.8) * mm});
            skLineSegment(sketch, "E709", {"start": v(41.8, 919.8) * mm, "end": v(59.8, 919.8) * mm});
            skArc(sketch, "E710", {"start": v(59.8, 919.8) * mm, "mid": v(63.05, 922.93) * mm, "end": v(60.04, 926.31) * mm});
            skLineSegment(sketch, "E711", {"start": v(60.04, 926.31) * mm, "end": v(60.04, 973.78) * mm});
            skArc(sketch, "E712", {"start": v(60.04, 973.78) * mm, "mid": v(63.05, 977.16) * mm, "end": v(59.8, 980.3) * mm});
            skLineSegment(sketch, "E713", {"start": v(59.8, 980.3) * mm, "end": v(41.8, 980.3) * mm});
            skArc(sketch, "E714", {"start": v(41.8, 980.3) * mm, "mid": v(38.53, 977.16) * mm, "end": v(41.54, 973.78) * mm});
            skLineSegment(sketch, "E715", {"start": v(41.54, 973.78) * mm, "end": v(41.54, 926.31) * mm});
            skArc(sketch, "E716", {"start": v(183.3, 825.05) * mm, "mid": v(186.44, 821.78) * mm, "end": v(189.82, 824.8) * mm});
            skLineSegment(sketch, "E717", {"start": v(189.82, 824.8) * mm, "end": v(257.29, 824.8) * mm});
            skArc(sketch, "E718", {"start": v(257.29, 824.8) * mm, "mid": v(260.67, 821.79) * mm, "end": v(263.8, 825.05) * mm});
            skLineSegment(sketch, "E719", {"start": v(263.8, 825.05) * mm, "end": v(263.8, 843.05) * mm});
            skArc(sketch, "E720", {"start": v(263.8, 843.05) * mm, "mid": v(260.67, 846.31) * mm, "end": v(257.29, 843.3) * mm});
            skLineSegment(sketch, "E721", {"start": v(257.29, 843.3) * mm, "end": v(189.82, 843.3) * mm});
            skArc(sketch, "E722", {"start": v(189.82, 843.3) * mm, "mid": v(186.44, 846.3) * mm, "end": v(183.3, 843.05) * mm});
            skLineSegment(sketch, "E723", {"start": v(183.3, 843.05) * mm, "end": v(183.3, 825.05) * mm});
            skLineSegment(sketch, "E724", {"start": v(-117.52, 640.25) * mm, "end": v(-99.02, 640.25) * mm});
            skArc(sketch, "E725", {"start": v(-99.02, 640.25) * mm, "mid": v(-96, 643.26) * mm, "end": v(-99.02, 646.27) * mm});
            skLineSegment(sketch, "E726", {"start": v(-99.02, 646.27) * mm, "end": v(-99.02, 754.73) * mm});
            skArc(sketch, "E727", {"start": v(-99.02, 754.73) * mm, "mid": v(-96, 757.74) * mm, "end": v(-99.02, 760.75) * mm});
            skLineSegment(sketch, "E728", {"start": v(-99.02, 760.75) * mm, "end": v(-117.52, 760.75) * mm});
            skArc(sketch, "E729", {"start": v(-117.52, 760.75) * mm, "mid": v(-120.53, 757.74) * mm, "end": v(-117.52, 754.73) * mm});
            skLineSegment(sketch, "E730", {"start": v(-117.52, 754.73) * mm, "end": v(-117.52, 646.27) * mm});
            skArc(sketch, "E731", {"start": v(-117.52, 646.27) * mm, "mid": v(-120.53, 643.26) * mm, "end": v(-117.52, 640.25) * mm});
            skLineSegment(sketch, "E732", {"start": v(-249.6, 754.73) * mm, "end": v(-249.6, 646.27) * mm});
            skArc(sketch, "E733", {"start": v(-249.6, 646.27) * mm, "mid": v(-252.62, 643.26) * mm, "end": v(-249.6, 640.25) * mm});
            skLineSegment(sketch, "E734", {"start": v(-249.6, 640.25) * mm, "end": v(-231.1, 640.25) * mm});
            skArc(sketch, "E735", {"start": v(-231.1, 640.25) * mm, "mid": v(-228.1, 643.26) * mm, "end": v(-231.1, 646.27) * mm});
            skLineSegment(sketch, "E736", {"start": v(-231.1, 646.27) * mm, "end": v(-231.1, 754.73) * mm});
            skArc(sketch, "E737", {"start": v(-231.1, 754.73) * mm, "mid": v(-228.1, 757.74) * mm, "end": v(-231.1, 760.75) * mm});
            skLineSegment(sketch, "E738", {"start": v(-231.1, 760.75) * mm, "end": v(-249.6, 760.75) * mm});
            skArc(sketch, "E739", {"start": v(-249.6, 760.75) * mm, "mid": v(-252.62, 757.74) * mm, "end": v(-249.6, 754.73) * mm});
            skLineSegment(sketch, "E740", {"start": v(-231.1, 426.27) * mm, "end": v(-231.1, 534.73) * mm});
            skArc(sketch, "E741", {"start": v(-231.1, 534.73) * mm, "mid": v(-228.1, 537.74) * mm, "end": v(-231.1, 540.75) * mm});
            skLineSegment(sketch, "E742", {"start": v(-231.1, 540.75) * mm, "end": v(-249.6, 540.75) * mm});
            skArc(sketch, "E743", {"start": v(-249.6, 540.75) * mm, "mid": v(-252.62, 537.74) * mm, "end": v(-249.6, 534.73) * mm});
            skLineSegment(sketch, "E744", {"start": v(-249.6, 534.73) * mm, "end": v(-249.6, 426.27) * mm});
            skArc(sketch, "E745", {"start": v(-249.6, 426.27) * mm, "mid": v(-252.62, 423.26) * mm, "end": v(-249.6, 420.25) * mm});
            skLineSegment(sketch, "E746", {"start": v(-249.6, 420.25) * mm, "end": v(-231.1, 420.25) * mm});
            skArc(sketch, "E747", {"start": v(-231.1, 420.25) * mm, "mid": v(-228.1, 423.26) * mm, "end": v(-231.1, 426.27) * mm});
            skLineSegment(sketch, "E748", {"start": v(-231.1, 126.27) * mm, "end": v(-231.1, 234.73) * mm});
            skArc(sketch, "E749", {"start": v(-231.1, 234.73) * mm, "mid": v(-228.1, 237.74) * mm, "end": v(-231.1, 240.75) * mm});
            skLineSegment(sketch, "E750", {"start": v(-231.1, 240.75) * mm, "end": v(-249.6, 240.75) * mm});
            skArc(sketch, "E751", {"start": v(-249.6, 240.75) * mm, "mid": v(-252.62, 237.74) * mm, "end": v(-249.6, 234.73) * mm});
            skLineSegment(sketch, "E752", {"start": v(-249.6, 234.73) * mm, "end": v(-249.6, 126.27) * mm});
            skArc(sketch, "E753", {"start": v(-249.6, 126.27) * mm, "mid": v(-252.62, 123.26) * mm, "end": v(-249.6, 120.25) * mm});
            skLineSegment(sketch, "E754", {"start": v(-249.6, 120.25) * mm, "end": v(-231.1, 120.25) * mm});
            skArc(sketch, "E755", {"start": v(-231.1, 120.25) * mm, "mid": v(-228.1, 123.26) * mm, "end": v(-231.1, 126.27) * mm});
            skLineSegment(sketch, "E756", {"start": v(-249.6, -65.27) * mm, "end": v(-249.6, -173.73) * mm});
            skArc(sketch, "E757", {"start": v(-249.6, -173.73) * mm, "mid": v(-252.62, -176.74) * mm, "end": v(-249.6, -179.75) * mm});
            skLineSegment(sketch, "E758", {"start": v(-249.6, -179.75) * mm, "end": v(-231.1, -179.75) * mm});
            skArc(sketch, "E759", {"start": v(-231.1, -179.75) * mm, "mid": v(-228.1, -176.74) * mm, "end": v(-231.1, -173.73) * mm});
            skLineSegment(sketch, "E760", {"start": v(-231.1, -173.73) * mm, "end": v(-231.1, -128.75) * mm});
            skLineSegment(sketch, "E761", {"start": v(-231.1, -128.75) * mm, "end": v(-206.13, -128.75) * mm});
            skArc(sketch, "E762", {"start": v(-206.13, -128.75) * mm, "mid": v(-203.12, -131.76) * mm, "end": v(-200.1, -128.75) * mm});
            skLineSegment(sketch, "E763", {"start": v(-200.1, -128.75) * mm, "end": v(-200.1, -110.25) * mm});
            skArc(sketch, "E764", {"start": v(-200.1, -110.25) * mm, "mid": v(-203.12, -107.24) * mm, "end": v(-206.13, -110.25) * mm});
            skLineSegment(sketch, "E765", {"start": v(-206.13, -110.25) * mm, "end": v(-231.1, -110.25) * mm});
            skLineSegment(sketch, "E766", {"start": v(-231.1, -110.25) * mm, "end": v(-231.1, -65.27) * mm});
            skArc(sketch, "E767", {"start": v(-231.1, -65.27) * mm, "mid": v(-228.1, -62.26) * mm, "end": v(-231.1, -59.25) * mm});
            skLineSegment(sketch, "E768", {"start": v(-231.1, -59.25) * mm, "end": v(-249.6, -59.25) * mm});
            skArc(sketch, "E769", {"start": v(-249.6, -59.25) * mm, "mid": v(-252.62, -62.26) * mm, "end": v(-249.6, -65.27) * mm});
            skLineSegment(sketch, "E770", {"start": v(-249.6, -479.75) * mm, "end": v(-231.1, -479.75) * mm});
            skArc(sketch, "E771", {"start": v(-231.1, -479.75) * mm, "mid": v(-228.1, -476.74) * mm, "end": v(-231.1, -473.73) * mm});
            skLineSegment(sketch, "E772", {"start": v(-231.1, -473.73) * mm, "end": v(-231.1, -365.27) * mm});
            skArc(sketch, "E773", {"start": v(-231.1, -365.27) * mm, "mid": v(-228.1, -362.26) * mm, "end": v(-231.1, -359.25) * mm});
            skLineSegment(sketch, "E774", {"start": v(-231.1, -359.25) * mm, "end": v(-249.6, -359.25) * mm});
            skArc(sketch, "E775", {"start": v(-249.6, -359.25) * mm, "mid": v(-252.62, -362.26) * mm, "end": v(-249.6, -365.27) * mm});
            skLineSegment(sketch, "E776", {"start": v(-249.6, -365.27) * mm, "end": v(-249.6, -473.73) * mm});
            skArc(sketch, "E777", {"start": v(-249.6, -473.73) * mm, "mid": v(-252.62, -476.74) * mm, "end": v(-249.6, -479.75) * mm});
            skLineSegment(sketch, "E778", {"start": v(-249.6, -665.27) * mm, "end": v(-249.6, -773.73) * mm});
            skArc(sketch, "E779", {"start": v(-249.6, -773.73) * mm, "mid": v(-252.62, -776.74) * mm, "end": v(-249.6, -779.75) * mm});
            skLineSegment(sketch, "E780", {"start": v(-249.6, -779.75) * mm, "end": v(-231.1, -779.75) * mm});
            skArc(sketch, "E781", {"start": v(-231.1, -779.75) * mm, "mid": v(-228.1, -776.74) * mm, "end": v(-231.1, -773.73) * mm});
            skLineSegment(sketch, "E782", {"start": v(-231.1, -773.73) * mm, "end": v(-231.1, -665.27) * mm});
            skArc(sketch, "E783", {"start": v(-231.1, -665.27) * mm, "mid": v(-228.1, -662.26) * mm, "end": v(-231.1, -659.25) * mm});
            skLineSegment(sketch, "E784", {"start": v(-231.1, -659.25) * mm, "end": v(-249.6, -659.25) * mm});
            skArc(sketch, "E785", {"start": v(-249.6, -659.25) * mm, "mid": v(-252.62, -662.26) * mm, "end": v(-249.6, -665.27) * mm});
            skLineSegment(sketch, "E786", {"start": v(-99.02, -773.73) * mm, "end": v(-99.02, -665.27) * mm});
            skArc(sketch, "E787", {"start": v(-99.02, -665.27) * mm, "mid": v(-96, -662.26) * mm, "end": v(-99.02, -659.25) * mm});
            skLineSegment(sketch, "E788", {"start": v(-99.02, -659.25) * mm, "end": v(-117.52, -659.25) * mm});
            skArc(sketch, "E789", {"start": v(-117.52, -659.25) * mm, "mid": v(-120.53, -662.26) * mm, "end": v(-117.52, -665.27) * mm});
            skLineSegment(sketch, "E790", {"start": v(-117.52, -665.27) * mm, "end": v(-117.52, -773.73) * mm});
            skArc(sketch, "E791", {"start": v(-117.52, -773.73) * mm, "mid": v(-120.53, -776.74) * mm, "end": v(-117.52, -779.75) * mm});
            skLineSegment(sketch, "E792", {"start": v(-117.52, -779.75) * mm, "end": v(-99.02, -779.75) * mm});
            skArc(sketch, "E793", {"start": v(-99.02, -779.75) * mm, "mid": v(-96, -776.74) * mm, "end": v(-99.02, -773.73) * mm});
            skLineSegment(sketch, "E794", {"start": v(-117.52, -365.27) * mm, "end": v(-117.52, -473.73) * mm});
            skArc(sketch, "E795", {"start": v(-117.52, -473.73) * mm, "mid": v(-120.53, -476.74) * mm, "end": v(-117.52, -479.75) * mm});
            skLineSegment(sketch, "E796", {"start": v(-117.52, -479.75) * mm, "end": v(-99.02, -479.75) * mm});
            skArc(sketch, "E797", {"start": v(-99.02, -479.75) * mm, "mid": v(-96, -476.74) * mm, "end": v(-99.02, -473.73) * mm});
            skLineSegment(sketch, "E798", {"start": v(-99.02, -473.73) * mm, "end": v(-99.02, -365.27) * mm});
            skArc(sketch, "E799", {"start": v(-99.02, -365.27) * mm, "mid": v(-96, -362.26) * mm, "end": v(-99.02, -359.25) * mm});
            skLineSegment(sketch, "E800", {"start": v(-99.02, -359.25) * mm, "end": v(-117.52, -359.25) * mm});
            skArc(sketch, "E801", {"start": v(-117.52, -359.25) * mm, "mid": v(-120.53, -362.26) * mm, "end": v(-117.52, -365.27) * mm});
            skLineSegment(sketch, "E802", {"start": v(-148.6, -110.25) * mm, "end": v(-148.6, -128.75) * mm});
            skArc(sketch, "E803", {"start": v(-148.6, -128.75) * mm, "mid": v(-145.6, -131.76) * mm, "end": v(-142.59, -128.75) * mm});
            skLineSegment(sketch, "E804", {"start": v(-142.59, -128.75) * mm, "end": v(-117.52, -128.75) * mm});
            skLineSegment(sketch, "E805", {"start": v(-117.52, -128.75) * mm, "end": v(-117.52, -173.73) * mm});
            skArc(sketch, "E806", {"start": v(-117.52, -173.73) * mm, "mid": v(-120.53, -176.74) * mm, "end": v(-117.52, -179.75) * mm});
            skLineSegment(sketch, "E807", {"start": v(-117.52, -179.75) * mm, "end": v(-99.02, -179.75) * mm});
            skArc(sketch, "E808", {"start": v(-99.02, -179.75) * mm, "mid": v(-96, -176.74) * mm, "end": v(-99.02, -173.73) * mm});
            skLineSegment(sketch, "E809", {"start": v(-99.02, -173.73) * mm, "end": v(-99.02, -65.27) * mm});
            skArc(sketch, "E810", {"start": v(-99.02, -65.27) * mm, "mid": v(-96, -62.26) * mm, "end": v(-99.02, -59.25) * mm});
            skLineSegment(sketch, "E811", {"start": v(-99.02, -59.25) * mm, "end": v(-117.52, -59.25) * mm});
            skArc(sketch, "E812", {"start": v(-117.52, -59.25) * mm, "mid": v(-120.53, -62.26) * mm, "end": v(-117.52, -65.27) * mm});
            skLineSegment(sketch, "E813", {"start": v(-117.52, -65.27) * mm, "end": v(-117.52, -110.25) * mm});
            skLineSegment(sketch, "E814", {"start": v(-117.52, -110.25) * mm, "end": v(-142.59, -110.25) * mm});
            skArc(sketch, "E815", {"start": v(-142.59, -110.25) * mm, "mid": v(-145.6, -107.24) * mm, "end": v(-148.6, -110.25) * mm});
            skLineSegment(sketch, "E816", {"start": v(-117.52, 234.73) * mm, "end": v(-117.52, 126.27) * mm});
            skArc(sketch, "E817", {"start": v(-117.52, 126.27) * mm, "mid": v(-120.53, 123.26) * mm, "end": v(-117.52, 120.25) * mm});
            skLineSegment(sketch, "E818", {"start": v(-117.52, 120.25) * mm, "end": v(-99.02, 120.25) * mm});
            skArc(sketch, "E819", {"start": v(-99.02, 120.25) * mm, "mid": v(-96, 123.26) * mm, "end": v(-99.02, 126.27) * mm});
            skLineSegment(sketch, "E820", {"start": v(-99.02, 126.27) * mm, "end": v(-99.02, 234.73) * mm});
            skArc(sketch, "E821", {"start": v(-99.02, 234.73) * mm, "mid": v(-96, 237.74) * mm, "end": v(-99.02, 240.75) * mm});
            skLineSegment(sketch, "E822", {"start": v(-99.02, 240.75) * mm, "end": v(-117.52, 240.75) * mm});
            skArc(sketch, "E823", {"start": v(-117.52, 240.75) * mm, "mid": v(-120.53, 237.74) * mm, "end": v(-117.52, 234.73) * mm});
            skLineSegment(sketch, "E824", {"start": v(-117.52, 534.73) * mm, "end": v(-117.52, 426.27) * mm});
            skArc(sketch, "E825", {"start": v(-117.52, 426.27) * mm, "mid": v(-120.53, 423.26) * mm, "end": v(-117.52, 420.25) * mm});
            skLineSegment(sketch, "E826", {"start": v(-117.52, 420.25) * mm, "end": v(-99.02, 420.25) * mm});
            skArc(sketch, "E827", {"start": v(-99.02, 420.25) * mm, "mid": v(-96, 423.26) * mm, "end": v(-99.02, 426.27) * mm});
            skLineSegment(sketch, "E828", {"start": v(-99.02, 426.27) * mm, "end": v(-99.02, 534.73) * mm});
            skArc(sketch, "E829", {"start": v(-99.02, 534.73) * mm, "mid": v(-96, 537.74) * mm, "end": v(-99.02, 540.75) * mm});
            skLineSegment(sketch, "E830", {"start": v(-99.02, 540.75) * mm, "end": v(-117.52, 540.75) * mm});
            skArc(sketch, "E831", {"start": v(-117.52, 540.75) * mm, "mid": v(-120.53, 537.74) * mm, "end": v(-117.52, 534.73) * mm});
            skLineSegment(sketch, "E832", {"start": v(124.6, -685.52) * mm, "end": v(124.6, -660.52) * mm});
            skLineSegment(sketch, "E833", {"start": v(124.6, -660.52) * mm, "end": v(224.6, -660.52) * mm});
            skLineSegment(sketch, "E834", {"start": v(224.6, -660.52) * mm, "end": v(224.6, -685.52) * mm});
            skLineSegment(sketch, "E835", {"start": v(224.6, -685.52) * mm, "end": v(124.6, -685.52) * mm});
            skLineSegment(sketch, "E836", {"start": v(-473.14, -526.6) * mm, "end": v(-433.14, -526.6) * mm});
            skLineSegment(sketch, "E837", {"start": v(-433.14, -526.6) * mm, "end": v(-433.14, -551.46) * mm});
            skLineSegment(sketch, "E838", {"start": v(-452.25, -526.6) * mm, "end": v(-452.25, -549.67) * mm});
            skLineSegment(sketch, "E839", {"start": v(-473.12, -612.9) * mm, "end": v(-433.14, -635.37) * mm});
            skLineSegment(sketch, "E840", {"start": v(-473.55, -657.55) * mm, "end": v(-473.55, -657.24) * mm});
            skLineSegment(sketch, "E841", {"start": v(-473.55, -657.24) * mm, "end": v(-473.54, -656.92) * mm});
            skLineSegment(sketch, "E842", {"start": v(-473.54, -656.92) * mm, "end": v(-473.53, -656.61) * mm});
            skLineSegment(sketch, "E843", {"start": v(-473.53, -656.61) * mm, "end": v(-473.5, -656.3) * mm});
            skLineSegment(sketch, "E844", {"start": v(-473.5, -656.3) * mm, "end": v(-473.47, -655.99) * mm});
            skLineSegment(sketch, "E845", {"start": v(-473.47, -655.99) * mm, "end": v(-473.43, -655.68) * mm});
            skLineSegment(sketch, "E846", {"start": v(-473.43, -655.68) * mm, "end": v(-473.38, -655.37) * mm});
            skLineSegment(sketch, "E847", {"start": v(-473.38, -655.37) * mm, "end": v(-473.33, -655.07) * mm});
            skLineSegment(sketch, "E848", {"start": v(-473.33, -655.07) * mm, "end": v(-473.26, -654.76) * mm});
            skLineSegment(sketch, "E849", {"start": v(-473.26, -654.76) * mm, "end": v(-473.2, -654.46) * mm});
            skLineSegment(sketch, "E850", {"start": v(-473.2, -654.46) * mm, "end": v(-473.11, -654.16) * mm});
            skLineSegment(sketch, "E851", {"start": v(-473.11, -654.16) * mm, "end": v(-473.03, -653.86) * mm});
            skLineSegment(sketch, "E852", {"start": v(-473.03, -653.86) * mm, "end": v(-472.93, -653.57) * mm});
            skLineSegment(sketch, "E853", {"start": v(-472.93, -653.57) * mm, "end": v(-472.83, -653.27) * mm});
            skLineSegment(sketch, "E854", {"start": v(-472.83, -653.27) * mm, "end": v(-472.73, -652.98) * mm});
            skLineSegment(sketch, "E855", {"start": v(-472.73, -652.98) * mm, "end": v(-472.61, -652.7) * mm});
            skLineSegment(sketch, "E856", {"start": v(-472.61, -652.7) * mm, "end": v(-472.49, -652.4) * mm});
            skLineSegment(sketch, "E857", {"start": v(-472.49, -652.4) * mm, "end": v(-472.36, -652.13) * mm});
            skLineSegment(sketch, "E858", {"start": v(-472.36, -652.13) * mm, "end": v(-472.22, -651.85) * mm});
            skLineSegment(sketch, "E859", {"start": v(-472.22, -651.85) * mm, "end": v(-472.08, -651.58) * mm});
            skLineSegment(sketch, "E860", {"start": v(-472.08, -651.58) * mm, "end": v(-471.93, -651.3) * mm});
            skLineSegment(sketch, "E861", {"start": v(-471.93, -651.3) * mm, "end": v(-471.77, -651.04) * mm});
            skLineSegment(sketch, "E862", {"start": v(-471.77, -651.04) * mm, "end": v(-471.6, -650.77) * mm});
            skLineSegment(sketch, "E863", {"start": v(-471.6, -650.77) * mm, "end": v(-471.44, -650.51) * mm});
            skLineSegment(sketch, "E864", {"start": v(-471.44, -650.51) * mm, "end": v(-471.26, -650.26) * mm});
            skLineSegment(sketch, "E865", {"start": v(-471.26, -650.26) * mm, "end": v(-471.07, -650) * mm});
            skLineSegment(sketch, "E866", {"start": v(-471.07, -650) * mm, "end": v(-470.88, -649.76) * mm});
            skLineSegment(sketch, "E867", {"start": v(-470.88, -649.76) * mm, "end": v(-470.69, -649.52) * mm});
            skLineSegment(sketch, "E868", {"start": v(-470.69, -649.52) * mm, "end": v(-470.48, -649.28) * mm});
            skLineSegment(sketch, "E869", {"start": v(-470.48, -649.28) * mm, "end": v(-470.27, -649.05) * mm});
            skLineSegment(sketch, "E870", {"start": v(-470.27, -649.05) * mm, "end": v(-470.06, -648.82) * mm});
            skLineSegment(sketch, "E871", {"start": v(-470.06, -648.82) * mm, "end": v(-469.83, -648.6) * mm});
            skLineSegment(sketch, "E872", {"start": v(-469.83, -648.6) * mm, "end": v(-469.55, -648.32) * mm});
            skLineSegment(sketch, "E873", {"start": v(-469.55, -648.32) * mm, "end": v(-469.26, -648.05) * mm});
            skLineSegment(sketch, "E874", {"start": v(-469.26, -648.05) * mm, "end": v(-468.96, -647.8) * mm});
            skLineSegment(sketch, "E875", {"start": v(-468.96, -647.8) * mm, "end": v(-468.66, -647.54) * mm});
            skLineSegment(sketch, "E876", {"start": v(-468.66, -647.54) * mm, "end": v(-468.34, -647.3) * mm});
            skLineSegment(sketch, "E877", {"start": v(-468.34, -647.3) * mm, "end": v(-468.03, -647.06) * mm});
            skLineSegment(sketch, "E878", {"start": v(-468.03, -647.06) * mm, "end": v(-467.7, -646.83) * mm});
            skLineSegment(sketch, "E879", {"start": v(-467.7, -646.83) * mm, "end": v(-467.38, -646.61) * mm});
            skLineSegment(sketch, "E880", {"start": v(-467.38, -646.61) * mm, "end": v(-467.05, -646.4) * mm});
            skLineSegment(sketch, "E881", {"start": v(-467.05, -646.4) * mm, "end": v(-466.7, -646.2) * mm});
            skLineSegment(sketch, "E882", {"start": v(-466.7, -646.2) * mm, "end": v(-466.37, -646) * mm});
            skLineSegment(sketch, "E883", {"start": v(-466.37, -646) * mm, "end": v(-466.02, -645.83) * mm});
            skLineSegment(sketch, "E884", {"start": v(-466.02, -645.83) * mm, "end": v(-465.67, -645.65) * mm});
            skLineSegment(sketch, "E885", {"start": v(-465.67, -645.65) * mm, "end": v(-465.31, -645.49) * mm});
            skLineSegment(sketch, "E886", {"start": v(-465.31, -645.49) * mm, "end": v(-464.95, -645.33) * mm});
            skLineSegment(sketch, "E887", {"start": v(-464.95, -645.33) * mm, "end": v(-464.6, -645.19) * mm});
            skLineSegment(sketch, "E888", {"start": v(-464.6, -645.19) * mm, "end": v(-464.22, -645.05) * mm});
            skLineSegment(sketch, "E889", {"start": v(-464.22, -645.05) * mm, "end": v(-463.85, -644.92) * mm});
            skLineSegment(sketch, "E890", {"start": v(-463.85, -644.92) * mm, "end": v(-463.48, -644.8) * mm});
            skLineSegment(sketch, "E891", {"start": v(-463.48, -644.8) * mm, "end": v(-463.1, -644.7) * mm});
            skLineSegment(sketch, "E892", {"start": v(-463.1, -644.7) * mm, "end": v(-462.72, -644.6) * mm});
            skLineSegment(sketch, "E893", {"start": v(-462.72, -644.6) * mm, "end": v(-462.34, -644.5) * mm});
            skLineSegment(sketch, "E894", {"start": v(-462.34, -644.5) * mm, "end": v(-461.96, -644.43) * mm});
            skLineSegment(sketch, "E895", {"start": v(-461.96, -644.43) * mm, "end": v(-461.57, -644.36) * mm});
            skLineSegment(sketch, "E896", {"start": v(-461.57, -644.36) * mm, "end": v(-461.18, -644.3) * mm});
            skLineSegment(sketch, "E897", {"start": v(-461.18, -644.3) * mm, "end": v(-460.79, -644.25) * mm});
            skLineSegment(sketch, "E898", {"start": v(-460.79, -644.25) * mm, "end": v(-460.4, -644.21) * mm});
            skLineSegment(sketch, "E899", {"start": v(-460.4, -644.21) * mm, "end": v(-460, -644.18) * mm});
            skLineSegment(sketch, "E900", {"start": v(-460, -644.18) * mm, "end": v(-459.6, -644.17) * mm});
            skLineSegment(sketch, "E901", {"start": v(-459.6, -644.17) * mm, "end": v(-459.21, -644.16) * mm});
            skLineSegment(sketch, "E902", {"start": v(-459.21, -644.16) * mm, "end": v(-458.81, -644.16) * mm});
            skLineSegment(sketch, "E903", {"start": v(-458.81, -644.16) * mm, "end": v(-458.42, -644.17) * mm});
            skLineSegment(sketch, "E904", {"start": v(-458.42, -644.17) * mm, "end": v(-457.99, -644.16) * mm});
            skLineSegment(sketch, "E905", {"start": v(-457.99, -644.16) * mm, "end": v(-457.56, -644.15) * mm});
            skLineSegment(sketch, "E906", {"start": v(-457.56, -644.15) * mm, "end": v(-457.14, -644.16) * mm});
            skLineSegment(sketch, "E907", {"start": v(-457.14, -644.16) * mm, "end": v(-456.72, -644.18) * mm});
            skLineSegment(sketch, "E908", {"start": v(-456.72, -644.18) * mm, "end": v(-456.3, -644.2) * mm});
            skLineSegment(sketch, "E909", {"start": v(-456.3, -644.2) * mm, "end": v(-455.87, -644.24) * mm});
            skLineSegment(sketch, "E910", {"start": v(-455.87, -644.24) * mm, "end": v(-455.45, -644.29) * mm});
            skLineSegment(sketch, "E911", {"start": v(-455.45, -644.29) * mm, "end": v(-455.04, -644.35) * mm});
            skLineSegment(sketch, "E912", {"start": v(-455.04, -644.35) * mm, "end": v(-454.62, -644.42) * mm});
            skLineSegment(sketch, "E913", {"start": v(-454.62, -644.42) * mm, "end": v(-454.2, -644.5) * mm});
            skLineSegment(sketch, "E914", {"start": v(-454.2, -644.5) * mm, "end": v(-453.8, -644.59) * mm});
            skLineSegment(sketch, "E915", {"start": v(-453.8, -644.59) * mm, "end": v(-453.39, -644.69) * mm});
            skLineSegment(sketch, "E916", {"start": v(-453.39, -644.69) * mm, "end": v(-452.98, -644.8) * mm});
            skLineSegment(sketch, "E917", {"start": v(-452.98, -644.8) * mm, "end": v(-452.58, -644.91) * mm});
            skLineSegment(sketch, "E918", {"start": v(-452.58, -644.91) * mm, "end": v(-452.18, -645.04) * mm});
            skLineSegment(sketch, "E919", {"start": v(-452.18, -645.04) * mm, "end": v(-451.78, -645.18) * mm});
            skLineSegment(sketch, "E920", {"start": v(-451.78, -645.18) * mm, "end": v(-451.4, -645.33) * mm});
            skLineSegment(sketch, "E921", {"start": v(-451.4, -645.33) * mm, "end": v(-451, -645.5) * mm});
            skLineSegment(sketch, "E922", {"start": v(-451, -645.5) * mm, "end": v(-450.62, -645.66) * mm});
            skLineSegment(sketch, "E923", {"start": v(-450.62, -645.66) * mm, "end": v(-450.24, -645.84) * mm});
            skLineSegment(sketch, "E924", {"start": v(-450.24, -645.84) * mm, "end": v(-449.86, -646.02) * mm});
            skLineSegment(sketch, "E925", {"start": v(-449.86, -646.02) * mm, "end": v(-449.49, -646.22) * mm});
            skLineSegment(sketch, "E926", {"start": v(-449.49, -646.22) * mm, "end": v(-449.12, -646.43) * mm});
            skLineSegment(sketch, "E927", {"start": v(-449.12, -646.43) * mm, "end": v(-448.76, -646.64) * mm});
            skLineSegment(sketch, "E928", {"start": v(-448.76, -646.64) * mm, "end": v(-448.4, -646.87) * mm});
            skLineSegment(sketch, "E929", {"start": v(-448.4, -646.87) * mm, "end": v(-448.05, -647.1) * mm});
            skLineSegment(sketch, "E930", {"start": v(-448.05, -647.1) * mm, "end": v(-447.7, -647.34) * mm});
            skLineSegment(sketch, "E931", {"start": v(-447.7, -647.34) * mm, "end": v(-447.37, -647.6) * mm});
            skLineSegment(sketch, "E932", {"start": v(-447.37, -647.6) * mm, "end": v(-447.03, -647.85) * mm});
            skLineSegment(sketch, "E933", {"start": v(-447.03, -647.85) * mm, "end": v(-446.7, -648.12) * mm});
            skLineSegment(sketch, "E934", {"start": v(-446.7, -648.12) * mm, "end": v(-446.38, -648.4) * mm});
            skLineSegment(sketch, "E935", {"start": v(-446.38, -648.4) * mm, "end": v(-446.07, -648.69) * mm});
            skLineSegment(sketch, "E936", {"start": v(-446.07, -648.69) * mm, "end": v(-445.67, -649.08) * mm});
            skLineSegment(sketch, "E937", {"start": v(-445.67, -649.08) * mm, "end": v(-445.3, -649.5) * mm});
            skLineSegment(sketch, "E938", {"start": v(-445.3, -649.5) * mm, "end": v(-444.95, -649.92) * mm});
            skLineSegment(sketch, "E939", {"start": v(-444.95, -649.92) * mm, "end": v(-444.63, -650.37) * mm});
            skLineSegment(sketch, "E940", {"start": v(-444.63, -650.37) * mm, "end": v(-444.32, -650.83) * mm});
            skLineSegment(sketch, "E941", {"start": v(-444.32, -650.83) * mm, "end": v(-444.05, -651.3) * mm});
            skLineSegment(sketch, "E942", {"start": v(-444.05, -651.3) * mm, "end": v(-443.8, -651.8) * mm});
            skLineSegment(sketch, "E943", {"start": v(-443.8, -651.8) * mm, "end": v(-443.57, -652.3) * mm});
            skLineSegment(sketch, "E944", {"start": v(-443.57, -652.3) * mm, "end": v(-443.37, -652.8) * mm});
            skLineSegment(sketch, "E945", {"start": v(-443.37, -652.8) * mm, "end": v(-443.2, -653.33) * mm});
            skLineSegment(sketch, "E946", {"start": v(-443.2, -653.33) * mm, "end": v(-443.04, -653.86) * mm});
            skLineSegment(sketch, "E947", {"start": v(-443.04, -653.86) * mm, "end": v(-442.92, -654.4) * mm});
            skLineSegment(sketch, "E948", {"start": v(-442.92, -654.4) * mm, "end": v(-442.83, -654.94) * mm});
            skLineSegment(sketch, "E949", {"start": v(-442.83, -654.94) * mm, "end": v(-442.76, -655.49) * mm});
            skLineSegment(sketch, "E950", {"start": v(-442.76, -655.49) * mm, "end": v(-442.73, -656.04) * mm});
            skLineSegment(sketch, "E951", {"start": v(-442.73, -656.04) * mm, "end": v(-442.72, -656.6) * mm});
            skLineSegment(sketch, "E952", {"start": v(-442.72, -656.6) * mm, "end": v(-442.72, -656.91) * mm});
            skLineSegment(sketch, "E953", {"start": v(-442.72, -656.91) * mm, "end": v(-442.73, -657.23) * mm});
            skLineSegment(sketch, "E954", {"start": v(-442.73, -657.23) * mm, "end": v(-442.75, -657.54) * mm});
            skLineSegment(sketch, "E955", {"start": v(-442.75, -657.54) * mm, "end": v(-442.78, -657.85) * mm});
            skLineSegment(sketch, "E956", {"start": v(-442.78, -657.85) * mm, "end": v(-442.82, -658.16) * mm});
            skLineSegment(sketch, "E957", {"start": v(-442.82, -658.16) * mm, "end": v(-442.86, -658.47) * mm});
            skLineSegment(sketch, "E958", {"start": v(-442.86, -658.47) * mm, "end": v(-442.91, -658.77) * mm});
            skLineSegment(sketch, "E959", {"start": v(-442.91, -658.77) * mm, "end": v(-442.97, -659.08) * mm});
            skLineSegment(sketch, "E960", {"start": v(-442.97, -659.08) * mm, "end": v(-443.04, -659.38) * mm});
            skLineSegment(sketch, "E961", {"start": v(-443.04, -659.38) * mm, "end": v(-443.11, -659.68) * mm});
            skLineSegment(sketch, "E962", {"start": v(-443.11, -659.68) * mm, "end": v(-443.2, -659.98) * mm});
            skLineSegment(sketch, "E963", {"start": v(-443.2, -659.98) * mm, "end": v(-443.28, -660.27) * mm});
            skLineSegment(sketch, "E964", {"start": v(-443.28, -660.27) * mm, "end": v(-443.38, -660.57) * mm});
            skLineSegment(sketch, "E965", {"start": v(-443.38, -660.57) * mm, "end": v(-443.48, -660.86) * mm});
            skLineSegment(sketch, "E966", {"start": v(-443.48, -660.86) * mm, "end": v(-443.6, -661.15) * mm});
            skLineSegment(sketch, "E967", {"start": v(-443.6, -661.15) * mm, "end": v(-443.7, -661.43) * mm});
            skLineSegment(sketch, "E968", {"start": v(-443.7, -661.43) * mm, "end": v(-443.83, -661.71) * mm});
            skLineSegment(sketch, "E969", {"start": v(-443.83, -661.71) * mm, "end": v(-443.97, -662) * mm});
            skLineSegment(sketch, "E970", {"start": v(-443.97, -662) * mm, "end": v(-444.1, -662.27) * mm});
            skLineSegment(sketch, "E971", {"start": v(-444.1, -662.27) * mm, "end": v(-444.25, -662.54) * mm});
            skLineSegment(sketch, "E972", {"start": v(-444.25, -662.54) * mm, "end": v(-444.4, -662.81) * mm});
            skLineSegment(sketch, "E973", {"start": v(-444.4, -662.81) * mm, "end": v(-444.56, -663.08) * mm});
            skLineSegment(sketch, "E974", {"start": v(-444.56, -663.08) * mm, "end": v(-444.73, -663.34) * mm});
            skLineSegment(sketch, "E975", {"start": v(-444.73, -663.34) * mm, "end": v(-444.9, -663.6) * mm});
            skLineSegment(sketch, "E976", {"start": v(-444.9, -663.6) * mm, "end": v(-445.08, -663.85) * mm});
            skLineSegment(sketch, "E977", {"start": v(-445.08, -663.85) * mm, "end": v(-445.27, -664.1) * mm});
            skLineSegment(sketch, "E978", {"start": v(-445.27, -664.1) * mm, "end": v(-445.46, -664.34) * mm});
            skLineSegment(sketch, "E979", {"start": v(-445.46, -664.34) * mm, "end": v(-445.66, -664.58) * mm});
            skLineSegment(sketch, "E980", {"start": v(-445.66, -664.58) * mm, "end": v(-445.86, -664.81) * mm});
            skLineSegment(sketch, "E981", {"start": v(-445.86, -664.81) * mm, "end": v(-446.07, -665.04) * mm});
            skLineSegment(sketch, "E982", {"start": v(-446.07, -665.04) * mm, "end": v(-446.3, -665.27) * mm});
            skLineSegment(sketch, "E983", {"start": v(-446.3, -665.27) * mm, "end": v(-446.51, -665.49) * mm});
            skLineSegment(sketch, "E984", {"start": v(-446.51, -665.49) * mm, "end": v(-446.81, -665.75) * mm});
            skLineSegment(sketch, "E985", {"start": v(-446.81, -665.75) * mm, "end": v(-447.12, -666) * mm});
            skLineSegment(sketch, "E986", {"start": v(-447.12, -666) * mm, "end": v(-447.43, -666.26) * mm});
            skLineSegment(sketch, "E987", {"start": v(-447.43, -666.26) * mm, "end": v(-447.75, -666.5) * mm});
            skLineSegment(sketch, "E988", {"start": v(-447.75, -666.5) * mm, "end": v(-448.07, -666.73) * mm});
            skLineSegment(sketch, "E989", {"start": v(-448.07, -666.73) * mm, "end": v(-448.4, -666.95) * mm});
            skLineSegment(sketch, "E990", {"start": v(-448.4, -666.95) * mm, "end": v(-448.74, -667.17) * mm});
            skLineSegment(sketch, "E991", {"start": v(-448.74, -667.17) * mm, "end": v(-449.07, -667.38) * mm});
            skLineSegment(sketch, "E992", {"start": v(-449.07, -667.38) * mm, "end": v(-449.42, -667.57) * mm});
            skLineSegment(sketch, "E993", {"start": v(-449.42, -667.57) * mm, "end": v(-449.76, -667.76) * mm});
            skLineSegment(sketch, "E994", {"start": v(-449.76, -667.76) * mm, "end": v(-450.12, -667.94) * mm});
            skLineSegment(sketch, "E995", {"start": v(-450.12, -667.94) * mm, "end": v(-450.47, -668.12) * mm});
            skLineSegment(sketch, "E996", {"start": v(-450.47, -668.12) * mm, "end": v(-450.83, -668.28) * mm});
            skLineSegment(sketch, "E997", {"start": v(-450.83, -668.28) * mm, "end": v(-451.2, -668.43) * mm});
            skLineSegment(sketch, "E998", {"start": v(-451.2, -668.43) * mm, "end": v(-451.56, -668.58) * mm});
            skLineSegment(sketch, "E999", {"start": v(-451.56, -668.58) * mm, "end": v(-451.93, -668.71) * mm});
            skLineSegment(sketch, "E1000", {"start": v(-451.93, -668.71) * mm, "end": v(-452.3, -668.84) * mm});
            skLineSegment(sketch, "E1001", {"start": v(-452.3, -668.84) * mm, "end": v(-452.68, -668.96) * mm});
            skLineSegment(sketch, "E1002", {"start": v(-452.68, -668.96) * mm, "end": v(-453.06, -669.07) * mm});
            skLineSegment(sketch, "E1003", {"start": v(-453.06, -669.07) * mm, "end": v(-453.45, -669.17) * mm});
            skLineSegment(sketch, "E1004", {"start": v(-453.45, -669.17) * mm, "end": v(-453.83, -669.26) * mm});
            skLineSegment(sketch, "E1005", {"start": v(-453.83, -669.26) * mm, "end": v(-454.22, -669.34) * mm});
            skLineSegment(sketch, "E1006", {"start": v(-454.22, -669.34) * mm, "end": v(-454.6, -669.4) * mm});
            skLineSegment(sketch, "E1007", {"start": v(-454.6, -669.4) * mm, "end": v(-455, -669.47) * mm});
            skLineSegment(sketch, "E1008", {"start": v(-455, -669.47) * mm, "end": v(-455.4, -669.52) * mm});
            skLineSegment(sketch, "E1009", {"start": v(-455.4, -669.52) * mm, "end": v(-455.79, -669.56) * mm});
            skLineSegment(sketch, "E1010", {"start": v(-455.79, -669.56) * mm, "end": v(-456.18, -669.6) * mm});
            skLineSegment(sketch, "E1011", {"start": v(-456.18, -669.6) * mm, "end": v(-456.58, -669.62) * mm});
            skLineSegment(sketch, "E1012", {"start": v(-456.58, -669.62) * mm, "end": v(-456.98, -669.63) * mm});
            skLineSegment(sketch, "E1013", {"start": v(-456.98, -669.63) * mm, "end": v(-457.38, -669.64) * mm});
            skLineSegment(sketch, "E1014", {"start": v(-457.38, -669.64) * mm, "end": v(-457.78, -669.63) * mm});
            skLineSegment(sketch, "E1015", {"start": v(-457.78, -669.63) * mm, "end": v(-458.18, -669.61) * mm});
            skLineSegment(sketch, "E1016", {"start": v(-458.18, -669.61) * mm, "end": v(-458.58, -669.63) * mm});
            skLineSegment(sketch, "E1017", {"start": v(-458.58, -669.63) * mm, "end": v(-459, -669.63) * mm});
            skLineSegment(sketch, "E1018", {"start": v(-459, -669.63) * mm, "end": v(-459.4, -669.63) * mm});
            skLineSegment(sketch, "E1019", {"start": v(-459.4, -669.63) * mm, "end": v(-459.8, -669.61) * mm});
            skLineSegment(sketch, "E1020", {"start": v(-459.8, -669.61) * mm, "end": v(-460.21, -669.59) * mm});
            skLineSegment(sketch, "E1021", {"start": v(-460.21, -669.59) * mm, "end": v(-460.62, -669.55) * mm});
            skLineSegment(sketch, "E1022", {"start": v(-460.62, -669.55) * mm, "end": v(-461.02, -669.5) * mm});
            skLineSegment(sketch, "E1023", {"start": v(-461.02, -669.5) * mm, "end": v(-461.42, -669.45) * mm});
            skLineSegment(sketch, "E1024", {"start": v(-461.42, -669.45) * mm, "end": v(-461.82, -669.38) * mm});
            skLineSegment(sketch, "E1025", {"start": v(-461.82, -669.38) * mm, "end": v(-462.22, -669.3) * mm});
            skLineSegment(sketch, "E1026", {"start": v(-462.22, -669.3) * mm, "end": v(-462.61, -669.22) * mm});
            skLineSegment(sketch, "E1027", {"start": v(-462.61, -669.22) * mm, "end": v(-463, -669.12) * mm});
            skLineSegment(sketch, "E1028", {"start": v(-463, -669.12) * mm, "end": v(-463.4, -669.01) * mm});
            skLineSegment(sketch, "E1029", {"start": v(-463.4, -669.01) * mm, "end": v(-463.78, -668.9) * mm});
            skLineSegment(sketch, "E1030", {"start": v(-463.78, -668.9) * mm, "end": v(-464.16, -668.77) * mm});
            skLineSegment(sketch, "E1031", {"start": v(-464.16, -668.77) * mm, "end": v(-464.54, -668.64) * mm});
            skLineSegment(sketch, "E1032", {"start": v(-464.54, -668.64) * mm, "end": v(-464.92, -668.5) * mm});
            skLineSegment(sketch, "E1033", {"start": v(-464.92, -668.5) * mm, "end": v(-465.3, -668.34) * mm});
            skLineSegment(sketch, "E1034", {"start": v(-465.3, -668.34) * mm, "end": v(-465.66, -668.18) * mm});
            skLineSegment(sketch, "E1035", {"start": v(-465.66, -668.18) * mm, "end": v(-466.03, -668) * mm});
            skLineSegment(sketch, "E1036", {"start": v(-466.03, -668) * mm, "end": v(-466.39, -667.83) * mm});
            skLineSegment(sketch, "E1037", {"start": v(-466.39, -667.83) * mm, "end": v(-466.74, -667.64) * mm});
            skLineSegment(sketch, "E1038", {"start": v(-466.74, -667.64) * mm, "end": v(-467.1, -667.44) * mm});
            skLineSegment(sketch, "E1039", {"start": v(-467.1, -667.44) * mm, "end": v(-467.44, -667.23) * mm});
            skLineSegment(sketch, "E1040", {"start": v(-467.44, -667.23) * mm, "end": v(-467.78, -667.01) * mm});
            skLineSegment(sketch, "E1041", {"start": v(-467.78, -667.01) * mm, "end": v(-468.12, -666.79) * mm});
            skLineSegment(sketch, "E1042", {"start": v(-468.12, -666.79) * mm, "end": v(-468.45, -666.55) * mm});
            skLineSegment(sketch, "E1043", {"start": v(-468.45, -666.55) * mm, "end": v(-468.78, -666.3) * mm});
            skLineSegment(sketch, "E1044", {"start": v(-468.78, -666.3) * mm, "end": v(-469.1, -666.06) * mm});
            skLineSegment(sketch, "E1045", {"start": v(-469.1, -666.06) * mm, "end": v(-469.4, -665.8) * mm});
            skLineSegment(sketch, "E1046", {"start": v(-469.4, -665.8) * mm, "end": v(-469.72, -665.53) * mm});
            skLineSegment(sketch, "E1047", {"start": v(-469.72, -665.53) * mm, "end": v(-470.02, -665.25) * mm});
            skLineSegment(sketch, "E1048", {"start": v(-470.02, -665.25) * mm, "end": v(-470.42, -664.87) * mm});
            skLineSegment(sketch, "E1049", {"start": v(-470.42, -664.87) * mm, "end": v(-470.8, -664.47) * mm});
            skLineSegment(sketch, "E1050", {"start": v(-470.8, -664.47) * mm, "end": v(-471.15, -664.06) * mm});
            skLineSegment(sketch, "E1051", {"start": v(-471.15, -664.06) * mm, "end": v(-471.48, -663.63) * mm});
            skLineSegment(sketch, "E1052", {"start": v(-471.48, -663.63) * mm, "end": v(-471.79, -663.18) * mm});
            skLineSegment(sketch, "E1053", {"start": v(-471.79, -663.18) * mm, "end": v(-472.08, -662.72) * mm});
            skLineSegment(sketch, "E1054", {"start": v(-472.08, -662.72) * mm, "end": v(-472.34, -662.25) * mm});
            skLineSegment(sketch, "E1055", {"start": v(-472.34, -662.25) * mm, "end": v(-472.58, -661.76) * mm});
            skLineSegment(sketch, "E1056", {"start": v(-472.58, -661.76) * mm, "end": v(-472.79, -661.27) * mm});
            skLineSegment(sketch, "E1057", {"start": v(-472.79, -661.27) * mm, "end": v(-472.98, -660.76) * mm});
            skLineSegment(sketch, "E1058", {"start": v(-472.98, -660.76) * mm, "end": v(-473.14, -660.24) * mm});
            skLineSegment(sketch, "E1059", {"start": v(-473.14, -660.24) * mm, "end": v(-473.28, -659.72) * mm});
            skLineSegment(sketch, "E1060", {"start": v(-473.28, -659.72) * mm, "end": v(-473.39, -659.18) * mm});
            skLineSegment(sketch, "E1061", {"start": v(-473.39, -659.18) * mm, "end": v(-473.47, -658.64) * mm});
            skLineSegment(sketch, "E1062", {"start": v(-473.47, -658.64) * mm, "end": v(-473.52, -658.1) * mm});
            skLineSegment(sketch, "E1063", {"start": v(-473.52, -658.1) * mm, "end": v(-473.55, -657.55) * mm});
            skLineSegment(sketch, "E1064", {"start": v(-473.12, -669.61) * mm, "end": v(-433.14, -669.61) * mm});
            skLineSegment(sketch, "E1065", {"start": v(-138.75, 971.77) * mm, "end": v(-138.75, 931.78) * mm});
            skLineSegment(sketch, "E1066", {"start": v(-138.75, 931.78) * mm, "end": v(-163.62, 931.78) * mm});
            skLineSegment(sketch, "E1067", {"start": v(-138.75, 950.89) * mm, "end": v(-161.82, 950.89) * mm});
            skLineSegment(sketch, "E1068", {"start": v(-225.05, 971.75) * mm, "end": v(-247.52, 931.78) * mm});
            skLineSegment(sketch, "E1069", {"start": v(-261.69, 971.75) * mm, "end": v(-261.69, 935.1) * mm});
            skLineSegment(sketch, "E1070", {"start": v(-261.69, 935.1) * mm, "end": v(-261.7, 934.94) * mm});
            skLineSegment(sketch, "E1071", {"start": v(-261.7, 934.94) * mm, "end": v(-261.7, 934.8) * mm});
            skLineSegment(sketch, "E1072", {"start": v(-261.7, 934.8) * mm, "end": v(-261.72, 934.64) * mm});
            skLineSegment(sketch, "E1073", {"start": v(-261.72, 934.64) * mm, "end": v(-261.75, 934.5) * mm});
            skLineSegment(sketch, "E1074", {"start": v(-261.75, 934.5) * mm, "end": v(-261.83, 934.2) * mm});
            skLineSegment(sketch, "E1075", {"start": v(-261.83, 934.2) * mm, "end": v(-261.93, 933.92) * mm});
            skLineSegment(sketch, "E1076", {"start": v(-261.93, 933.92) * mm, "end": v(-262.06, 933.66) * mm});
            skLineSegment(sketch, "E1077", {"start": v(-262.06, 933.66) * mm, "end": v(-262.22, 933.4) * mm});
            skLineSegment(sketch, "E1078", {"start": v(-262.22, 933.4) * mm, "end": v(-262.3, 933.28) * mm});
            skLineSegment(sketch, "E1079", {"start": v(-262.3, 933.28) * mm, "end": v(-262.4, 933.16) * mm});
            skLineSegment(sketch, "E1080", {"start": v(-262.4, 933.16) * mm, "end": v(-262.5, 933.05) * mm});
            skLineSegment(sketch, "E1081", {"start": v(-262.5, 933.05) * mm, "end": v(-262.6, 932.94) * mm});
            skLineSegment(sketch, "E1082", {"start": v(-262.6, 932.94) * mm, "end": v(-262.83, 932.76) * mm});
            skLineSegment(sketch, "E1083", {"start": v(-262.83, 932.76) * mm, "end": v(-263.06, 932.6) * mm});
            skLineSegment(sketch, "E1084", {"start": v(-263.06, 932.6) * mm, "end": v(-263.3, 932.44) * mm});
            skLineSegment(sketch, "E1085", {"start": v(-263.3, 932.44) * mm, "end": v(-263.55, 932.3) * mm});
            skLineSegment(sketch, "E1086", {"start": v(-263.55, 932.3) * mm, "end": v(-263.8, 932.18) * mm});
            skLineSegment(sketch, "E1087", {"start": v(-263.8, 932.18) * mm, "end": v(-264.06, 932.06) * mm});
            skLineSegment(sketch, "E1088", {"start": v(-264.06, 932.06) * mm, "end": v(-264.32, 931.97) * mm});
            skLineSegment(sketch, "E1089", {"start": v(-264.32, 931.97) * mm, "end": v(-264.6, 931.88) * mm});
            skLineSegment(sketch, "E1090", {"start": v(-264.6, 931.88) * mm, "end": v(-264.87, 931.82) * mm});
            skLineSegment(sketch, "E1091", {"start": v(-264.87, 931.82) * mm, "end": v(-265.14, 931.76) * mm});
            skLineSegment(sketch, "E1092", {"start": v(-265.14, 931.76) * mm, "end": v(-265.42, 931.73) * mm});
            skLineSegment(sketch, "E1093", {"start": v(-265.42, 931.73) * mm, "end": v(-265.7, 931.7) * mm});
            skLineSegment(sketch, "E1094", {"start": v(-265.7, 931.7) * mm, "end": v(-266, 931.7) * mm});
            skLineSegment(sketch, "E1095", {"start": v(-266, 931.7) * mm, "end": v(-266.27, 931.7) * mm});
            skLineSegment(sketch, "E1096", {"start": v(-266.27, 931.7) * mm, "end": v(-266.56, 931.73) * mm});
            skLineSegment(sketch, "E1097", {"start": v(-266.56, 931.73) * mm, "end": v(-266.84, 931.78) * mm});
            skLineSegment(sketch, "E1098", {"start": v(-267.95, 941.8) * mm, "end": v(-256.32, 941.8) * mm});
            skLineSegment(sketch, "E1099", {"start": v(-158, 101.6) * mm, "end": v(-181.03, 101.59) * mm});
            skLineSegment(sketch, "E1100", {"start": v(-181.03, 101.59) * mm, "end": v(-181.33, 101.6) * mm});
            skLineSegment(sketch, "E1101", {"start": v(-181.33, 101.6) * mm, "end": v(-181.62, 101.6) * mm});
            skLineSegment(sketch, "E1102", {"start": v(-181.62, 101.6) * mm, "end": v(-181.92, 101.62) * mm});
            skLineSegment(sketch, "E1103", {"start": v(-181.92, 101.62) * mm, "end": v(-182.21, 101.64) * mm});
            skLineSegment(sketch, "E1104", {"start": v(-182.21, 101.64) * mm, "end": v(-182.8, 101.72) * mm});
            skLineSegment(sketch, "E1105", {"start": v(-182.8, 101.72) * mm, "end": v(-183.37, 101.82) * mm});
            skLineSegment(sketch, "E1106", {"start": v(-183.37, 101.82) * mm, "end": v(-183.94, 101.95) * mm});
            skLineSegment(sketch, "E1107", {"start": v(-183.94, 101.95) * mm, "end": v(-184.5, 102.11) * mm});
            skLineSegment(sketch, "E1108", {"start": v(-184.5, 102.11) * mm, "end": v(-185.06, 102.3) * mm});
            skLineSegment(sketch, "E1109", {"start": v(-185.06, 102.3) * mm, "end": v(-185.6, 102.52) * mm});
            skLineSegment(sketch, "E1110", {"start": v(-185.6, 102.52) * mm, "end": v(-186.13, 102.76) * mm});
            skLineSegment(sketch, "E1111", {"start": v(-186.13, 102.76) * mm, "end": v(-186.65, 103.03) * mm});
            skLineSegment(sketch, "E1112", {"start": v(-186.65, 103.03) * mm, "end": v(-187.15, 103.32) * mm});
            skLineSegment(sketch, "E1113", {"start": v(-187.15, 103.32) * mm, "end": v(-187.64, 103.64) * mm});
            skLineSegment(sketch, "E1114", {"start": v(-187.64, 103.64) * mm, "end": v(-188.12, 104) * mm});
            skLineSegment(sketch, "E1115", {"start": v(-188.12, 104) * mm, "end": v(-188.35, 104.17) * mm});
            skLineSegment(sketch, "E1116", {"start": v(-188.35, 104.17) * mm, "end": v(-188.57, 104.36) * mm});
            skLineSegment(sketch, "E1117", {"start": v(-188.57, 104.36) * mm, "end": v(-188.8, 104.55) * mm});
            skLineSegment(sketch, "E1118", {"start": v(-188.8, 104.55) * mm, "end": v(-189.01, 104.76) * mm});
            skLineSegment(sketch, "E1119", {"start": v(-189.01, 104.76) * mm, "end": v(-189.22, 104.96) * mm});
            skLineSegment(sketch, "E1120", {"start": v(-189.22, 104.96) * mm, "end": v(-189.43, 105.17) * mm});
            skLineSegment(sketch, "E1121", {"start": v(-189.43, 105.17) * mm, "end": v(-189.66, 105.4) * mm});
            skLineSegment(sketch, "E1122", {"start": v(-189.66, 105.4) * mm, "end": v(-189.88, 105.64) * mm});
            skLineSegment(sketch, "E1123", {"start": v(-189.88, 105.64) * mm, "end": v(-190.09, 105.88) * mm});
            skLineSegment(sketch, "E1124", {"start": v(-190.09, 105.88) * mm, "end": v(-190.3, 106.12) * mm});
            skLineSegment(sketch, "E1125", {"start": v(-190.3, 106.12) * mm, "end": v(-190.5, 106.37) * mm});
            skLineSegment(sketch, "E1126", {"start": v(-190.5, 106.37) * mm, "end": v(-190.69, 106.63) * mm});
            skLineSegment(sketch, "E1127", {"start": v(-190.69, 106.63) * mm, "end": v(-190.87, 106.89) * mm});
            skLineSegment(sketch, "E1128", {"start": v(-190.87, 106.89) * mm, "end": v(-191.05, 107.15) * mm});
            skLineSegment(sketch, "E1129", {"start": v(-191.05, 107.15) * mm, "end": v(-191.23, 107.42) * mm});
            skLineSegment(sketch, "E1130", {"start": v(-191.23, 107.42) * mm, "end": v(-191.4, 107.69) * mm});
            skLineSegment(sketch, "E1131", {"start": v(-191.4, 107.69) * mm, "end": v(-191.55, 107.96) * mm});
            skLineSegment(sketch, "E1132", {"start": v(-191.55, 107.96) * mm, "end": v(-191.7, 108.24) * mm});
            skLineSegment(sketch, "E1133", {"start": v(-191.7, 108.24) * mm, "end": v(-191.85, 108.52) * mm});
            skLineSegment(sketch, "E1134", {"start": v(-191.85, 108.52) * mm, "end": v(-192, 108.8) * mm});
            skLineSegment(sketch, "E1135", {"start": v(-192, 108.8) * mm, "end": v(-192.13, 109.1) * mm});
            skLineSegment(sketch, "E1136", {"start": v(-192.13, 109.1) * mm, "end": v(-192.25, 109.39) * mm});
            skLineSegment(sketch, "E1137", {"start": v(-192.25, 109.39) * mm, "end": v(-192.37, 109.68) * mm});
            skLineSegment(sketch, "E1138", {"start": v(-192.37, 109.68) * mm, "end": v(-192.48, 109.98) * mm});
            skLineSegment(sketch, "E1139", {"start": v(-192.48, 109.98) * mm, "end": v(-192.58, 110.28) * mm});
            skLineSegment(sketch, "E1140", {"start": v(-192.58, 110.28) * mm, "end": v(-192.68, 110.58) * mm});
            skLineSegment(sketch, "E1141", {"start": v(-192.68, 110.58) * mm, "end": v(-192.77, 110.89) * mm});
            skLineSegment(sketch, "E1142", {"start": v(-192.77, 110.89) * mm, "end": v(-192.85, 111.2) * mm});
            skLineSegment(sketch, "E1143", {"start": v(-192.85, 111.2) * mm, "end": v(-192.93, 111.5) * mm});
            skLineSegment(sketch, "E1144", {"start": v(-192.93, 111.5) * mm, "end": v(-193, 111.81) * mm});
            skLineSegment(sketch, "E1145", {"start": v(-193, 111.81) * mm, "end": v(-193.05, 112.13) * mm});
            skLineSegment(sketch, "E1146", {"start": v(-193.05, 112.13) * mm, "end": v(-193.1, 112.44) * mm});
            skLineSegment(sketch, "E1147", {"start": v(-193.1, 112.44) * mm, "end": v(-193.15, 112.76) * mm});
            skLineSegment(sketch, "E1148", {"start": v(-193.15, 112.76) * mm, "end": v(-193.18, 113.08) * mm});
            skLineSegment(sketch, "E1149", {"start": v(-193.18, 113.08) * mm, "end": v(-193.21, 113.4) * mm});
            skLineSegment(sketch, "E1150", {"start": v(-193.21, 113.4) * mm, "end": v(-193.23, 113.71) * mm});
            skLineSegment(sketch, "E1151", {"start": v(-193.23, 113.71) * mm, "end": v(-193.24, 114.04) * mm});
            skLineSegment(sketch, "E1152", {"start": v(-193.24, 114.04) * mm, "end": v(-193.25, 114.36) * mm});
            skLineSegment(sketch, "E1153", {"start": v(-193.25, 114.36) * mm, "end": v(-193.25, 114.68) * mm});
            skLineSegment(sketch, "E1154", {"start": v(-193.25, 114.68) * mm, "end": v(-193.24, 115) * mm});
            skLineSegment(sketch, "E1155", {"start": v(-193.24, 115) * mm, "end": v(-193.23, 115.32) * mm});
            skLineSegment(sketch, "E1156", {"start": v(-193.23, 115.32) * mm, "end": v(-193.2, 115.64) * mm});
            skLineSegment(sketch, "E1157", {"start": v(-193.2, 115.64) * mm, "end": v(-193.18, 115.95) * mm});
            skLineSegment(sketch, "E1158", {"start": v(-193.18, 115.95) * mm, "end": v(-193.14, 116.27) * mm});
            skLineSegment(sketch, "E1159", {"start": v(-193.14, 116.27) * mm, "end": v(-193.1, 116.59) * mm});
            skLineSegment(sketch, "E1160", {"start": v(-193.1, 116.59) * mm, "end": v(-193.04, 116.9) * mm});
            skLineSegment(sketch, "E1161", {"start": v(-193.04, 116.9) * mm, "end": v(-192.98, 117.2) * mm});
            skLineSegment(sketch, "E1162", {"start": v(-192.98, 117.2) * mm, "end": v(-192.9, 117.52) * mm});
            skLineSegment(sketch, "E1163", {"start": v(-192.9, 117.52) * mm, "end": v(-192.83, 117.83) * mm});
            skLineSegment(sketch, "E1164", {"start": v(-192.83, 117.83) * mm, "end": v(-192.75, 118.13) * mm});
            skLineSegment(sketch, "E1165", {"start": v(-192.75, 118.13) * mm, "end": v(-192.66, 118.44) * mm});
            skLineSegment(sketch, "E1166", {"start": v(-192.66, 118.44) * mm, "end": v(-192.56, 118.74) * mm});
            skLineSegment(sketch, "E1167", {"start": v(-192.56, 118.74) * mm, "end": v(-192.45, 119.03) * mm});
            skLineSegment(sketch, "E1168", {"start": v(-192.45, 119.03) * mm, "end": v(-192.34, 119.33) * mm});
            skLineSegment(sketch, "E1169", {"start": v(-192.34, 119.33) * mm, "end": v(-192.22, 119.62) * mm});
            skLineSegment(sketch, "E1170", {"start": v(-192.22, 119.62) * mm, "end": v(-192.1, 119.91) * mm});
            skLineSegment(sketch, "E1171", {"start": v(-192.1, 119.91) * mm, "end": v(-191.96, 120.2) * mm});
            skLineSegment(sketch, "E1172", {"start": v(-191.96, 120.2) * mm, "end": v(-191.82, 120.48) * mm});
            skLineSegment(sketch, "E1173", {"start": v(-191.82, 120.48) * mm, "end": v(-191.67, 120.76) * mm});
            skLineSegment(sketch, "E1174", {"start": v(-191.67, 120.76) * mm, "end": v(-191.51, 121.04) * mm});
            skLineSegment(sketch, "E1175", {"start": v(-191.51, 121.04) * mm, "end": v(-191.35, 121.31) * mm});
            skLineSegment(sketch, "E1176", {"start": v(-191.35, 121.31) * mm, "end": v(-191.18, 121.58) * mm});
            skLineSegment(sketch, "E1177", {"start": v(-191.18, 121.58) * mm, "end": v(-191, 121.84) * mm});
            skLineSegment(sketch, "E1178", {"start": v(-191, 121.84) * mm, "end": v(-190.83, 122.1) * mm});
            skLineSegment(sketch, "E1179", {"start": v(-190.83, 122.1) * mm, "end": v(-190.64, 122.36) * mm});
            skLineSegment(sketch, "E1180", {"start": v(-190.64, 122.36) * mm, "end": v(-190.44, 122.61) * mm});
            skLineSegment(sketch, "E1181", {"start": v(-190.44, 122.61) * mm, "end": v(-190.24, 122.86) * mm});
            skLineSegment(sketch, "E1182", {"start": v(-190.24, 122.86) * mm, "end": v(-190.03, 123.1) * mm});
            skLineSegment(sketch, "E1183", {"start": v(-190.03, 123.1) * mm, "end": v(-189.82, 123.34) * mm});
            skLineSegment(sketch, "E1184", {"start": v(-189.82, 123.34) * mm, "end": v(-189.6, 123.57) * mm});
            skLineSegment(sketch, "E1185", {"start": v(-189.6, 123.57) * mm, "end": v(-189.39, 123.8) * mm});
            skLineSegment(sketch, "E1186", {"start": v(-189.39, 123.8) * mm, "end": v(-189.17, 124) * mm});
            skLineSegment(sketch, "E1187", {"start": v(-189.17, 124) * mm, "end": v(-188.95, 124.2) * mm});
            skLineSegment(sketch, "E1188", {"start": v(-188.95, 124.2) * mm, "end": v(-188.72, 124.4) * mm});
            skLineSegment(sketch, "E1189", {"start": v(-188.72, 124.4) * mm, "end": v(-188.5, 124.6) * mm});
            skLineSegment(sketch, "E1190", {"start": v(-188.5, 124.6) * mm, "end": v(-188.26, 124.79) * mm});
            skLineSegment(sketch, "E1191", {"start": v(-188.26, 124.79) * mm, "end": v(-188.02, 124.97) * mm});
            skLineSegment(sketch, "E1192", {"start": v(-188.02, 124.97) * mm, "end": v(-187.78, 125.14) * mm});
            skLineSegment(sketch, "E1193", {"start": v(-187.78, 125.14) * mm, "end": v(-187.53, 125.31) * mm});
            skLineSegment(sketch, "E1194", {"start": v(-187.53, 125.31) * mm, "end": v(-187.28, 125.47) * mm});
            skLineSegment(sketch, "E1195", {"start": v(-187.28, 125.47) * mm, "end": v(-187.02, 125.63) * mm});
            skLineSegment(sketch, "E1196", {"start": v(-187.02, 125.63) * mm, "end": v(-186.76, 125.78) * mm});
            skLineSegment(sketch, "E1197", {"start": v(-186.76, 125.78) * mm, "end": v(-186.24, 126.06) * mm});
            skLineSegment(sketch, "E1198", {"start": v(-186.24, 126.06) * mm, "end": v(-185.7, 126.3) * mm});
            skLineSegment(sketch, "E1199", {"start": v(-185.7, 126.3) * mm, "end": v(-185.14, 126.53) * mm});
            skLineSegment(sketch, "E1200", {"start": v(-185.14, 126.53) * mm, "end": v(-184.86, 126.63) * mm});
            skLineSegment(sketch, "E1201", {"start": v(-184.86, 126.63) * mm, "end": v(-184.58, 126.72) * mm});
            skLineSegment(sketch, "E1202", {"start": v(-184.58, 126.72) * mm, "end": v(-184.3, 126.81) * mm});
            skLineSegment(sketch, "E1203", {"start": v(-184.3, 126.81) * mm, "end": v(-184, 126.9) * mm});
            skLineSegment(sketch, "E1204", {"start": v(-184, 126.9) * mm, "end": v(-183.71, 126.96) * mm});
            skLineSegment(sketch, "E1205", {"start": v(-183.71, 126.96) * mm, "end": v(-183.42, 127.03) * mm});
            skLineSegment(sketch, "E1206", {"start": v(-183.42, 127.03) * mm, "end": v(-183.13, 127.09) * mm});
            skLineSegment(sketch, "E1207", {"start": v(-183.13, 127.09) * mm, "end": v(-182.83, 127.14) * mm});
            skLineSegment(sketch, "E1208", {"start": v(-182.83, 127.14) * mm, "end": v(-182.54, 127.18) * mm});
            skLineSegment(sketch, "E1209", {"start": v(-182.54, 127.18) * mm, "end": v(-182.24, 127.21) * mm});
            skLineSegment(sketch, "E1210", {"start": v(-182.24, 127.21) * mm, "end": v(-181.94, 127.24) * mm});
            skLineSegment(sketch, "E1211", {"start": v(-181.94, 127.24) * mm, "end": v(-181.64, 127.26) * mm});
            skLineSegment(sketch, "E1212", {"start": v(-181.64, 127.26) * mm, "end": v(-181.33, 127.27) * mm});
            skLineSegment(sketch, "E1213", {"start": v(-181.33, 127.27) * mm, "end": v(-181.03, 127.28) * mm});
            skLineSegment(sketch, "E1214", {"start": v(-181.03, 127.28) * mm, "end": v(-158, 127.28) * mm});
            skLineSegment(sketch, "E1215", {"start": v(-192.95, 93.7) * mm, "end": v(-157.98, 93.7) * mm});
            skLineSegment(sketch, "E1216", {"start": v(-157.98, 93.7) * mm, "end": v(-157.98, 92.36) * mm});
            skLineSegment(sketch, "E1217", {"start": v(-157.98, 92.36) * mm, "end": v(-192.95, 69.4) * mm});
            skLineSegment(sketch, "E1218", {"start": v(-192.95, 69.4) * mm, "end": v(-192.95, 68) * mm});
            skLineSegment(sketch, "E1219", {"start": v(-192.95, 68) * mm, "end": v(-158, 68) * mm});
            skLineSegment(sketch, "E1220", {"start": v(-192.96, 60.1) * mm, "end": v(-157.98, 60.1) * mm});
            skLineSegment(sketch, "E1221", {"start": v(-157.98, 60.1) * mm, "end": v(-157.98, 47.28) * mm});
            skLineSegment(sketch, "E1222", {"start": v(-157.98, 47.28) * mm, "end": v(-158, 46.97) * mm});
            skLineSegment(sketch, "E1223", {"start": v(-158, 46.97) * mm, "end": v(-158.01, 46.67) * mm});
            skLineSegment(sketch, "E1224", {"start": v(-158.01, 46.67) * mm, "end": v(-158.04, 46.37) * mm});
            skLineSegment(sketch, "E1225", {"start": v(-158.04, 46.37) * mm, "end": v(-158.08, 46.07) * mm});
            skLineSegment(sketch, "E1226", {"start": v(-158.08, 46.07) * mm, "end": v(-158.12, 45.77) * mm});
            skLineSegment(sketch, "E1227", {"start": v(-158.12, 45.77) * mm, "end": v(-158.18, 45.47) * mm});
            skLineSegment(sketch, "E1228", {"start": v(-158.18, 45.47) * mm, "end": v(-158.24, 45.18) * mm});
            skLineSegment(sketch, "E1229", {"start": v(-158.24, 45.18) * mm, "end": v(-158.3, 44.88) * mm});
            skLineSegment(sketch, "E1230", {"start": v(-158.3, 44.88) * mm, "end": v(-158.38, 44.6) * mm});
            skLineSegment(sketch, "E1231", {"start": v(-158.38, 44.6) * mm, "end": v(-158.46, 44.3) * mm});
            skLineSegment(sketch, "E1232", {"start": v(-158.46, 44.3) * mm, "end": v(-158.55, 44.02) * mm});
            skLineSegment(sketch, "E1233", {"start": v(-158.55, 44.02) * mm, "end": v(-158.65, 43.73) * mm});
            skLineSegment(sketch, "E1234", {"start": v(-158.65, 43.73) * mm, "end": v(-158.86, 43.17) * mm});
            skLineSegment(sketch, "E1235", {"start": v(-158.86, 43.17) * mm, "end": v(-159.1, 42.62) * mm});
            skLineSegment(sketch, "E1236", {"start": v(-159.1, 42.62) * mm, "end": v(-159.37, 42.09) * mm});
            skLineSegment(sketch, "E1237", {"start": v(-159.37, 42.09) * mm, "end": v(-159.66, 41.56) * mm});
            skLineSegment(sketch, "E1238", {"start": v(-159.66, 41.56) * mm, "end": v(-159.82, 41.3) * mm});
            skLineSegment(sketch, "E1239", {"start": v(-159.82, 41.3) * mm, "end": v(-159.98, 41.06) * mm});
            skLineSegment(sketch, "E1240", {"start": v(-159.98, 41.06) * mm, "end": v(-160.15, 40.8) * mm});
            skLineSegment(sketch, "E1241", {"start": v(-160.15, 40.8) * mm, "end": v(-160.33, 40.57) * mm});
            skLineSegment(sketch, "E1242", {"start": v(-160.33, 40.57) * mm, "end": v(-160.5, 40.33) * mm});
            skLineSegment(sketch, "E1243", {"start": v(-160.5, 40.33) * mm, "end": v(-160.7, 40.1) * mm});
            skLineSegment(sketch, "E1244", {"start": v(-160.7, 40.1) * mm, "end": v(-160.9, 39.86) * mm});
            skLineSegment(sketch, "E1245", {"start": v(-160.9, 39.86) * mm, "end": v(-161.1, 39.63) * mm});
            skLineSegment(sketch, "E1246", {"start": v(-161.1, 39.63) * mm, "end": v(-161.3, 39.41) * mm});
            skLineSegment(sketch, "E1247", {"start": v(-161.3, 39.41) * mm, "end": v(-161.51, 39.2) * mm});
            skLineSegment(sketch, "E1248", {"start": v(-161.51, 39.2) * mm, "end": v(-161.73, 38.99) * mm});
            skLineSegment(sketch, "E1249", {"start": v(-161.73, 38.99) * mm, "end": v(-161.95, 38.78) * mm});
            skLineSegment(sketch, "E1250", {"start": v(-161.95, 38.78) * mm, "end": v(-162.32, 38.43) * mm});
            skLineSegment(sketch, "E1251", {"start": v(-162.32, 38.43) * mm, "end": v(-162.68, 38.09) * mm});
            skLineSegment(sketch, "E1252", {"start": v(-162.68, 38.09) * mm, "end": v(-163.06, 37.76) * mm});
            skLineSegment(sketch, "E1253", {"start": v(-163.06, 37.76) * mm, "end": v(-163.45, 37.44) * mm});
            skLineSegment(sketch, "E1254", {"start": v(-163.45, 37.44) * mm, "end": v(-163.84, 37.13) * mm});
            skLineSegment(sketch, "E1255", {"start": v(-163.84, 37.13) * mm, "end": v(-164.24, 36.83) * mm});
            skLineSegment(sketch, "E1256", {"start": v(-164.24, 36.83) * mm, "end": v(-164.64, 36.54) * mm});
            skLineSegment(sketch, "E1257", {"start": v(-164.64, 36.54) * mm, "end": v(-165.05, 36.26) * mm});
            skLineSegment(sketch, "E1258", {"start": v(-165.05, 36.26) * mm, "end": v(-165.47, 36) * mm});
            skLineSegment(sketch, "E1259", {"start": v(-165.47, 36) * mm, "end": v(-165.9, 35.74) * mm});
            skLineSegment(sketch, "E1260", {"start": v(-165.9, 35.74) * mm, "end": v(-166.33, 35.49) * mm});
            skLineSegment(sketch, "E1261", {"start": v(-166.33, 35.49) * mm, "end": v(-166.77, 35.25) * mm});
            skLineSegment(sketch, "E1262", {"start": v(-166.77, 35.25) * mm, "end": v(-167.2, 35.03) * mm});
            skLineSegment(sketch, "E1263", {"start": v(-167.2, 35.03) * mm, "end": v(-167.66, 34.82) * mm});
            skLineSegment(sketch, "E1264", {"start": v(-167.66, 34.82) * mm, "end": v(-168.1, 34.61) * mm});
            skLineSegment(sketch, "E1265", {"start": v(-168.1, 34.61) * mm, "end": v(-168.57, 34.42) * mm});
            skLineSegment(sketch, "E1266", {"start": v(-168.57, 34.42) * mm, "end": v(-169.03, 34.25) * mm});
            skLineSegment(sketch, "E1267", {"start": v(-169.03, 34.25) * mm, "end": v(-169.5, 34.08) * mm});
            skLineSegment(sketch, "E1268", {"start": v(-169.5, 34.08) * mm, "end": v(-169.96, 33.92) * mm});
            skLineSegment(sketch, "E1269", {"start": v(-169.96, 33.92) * mm, "end": v(-170.44, 33.78) * mm});
            skLineSegment(sketch, "E1270", {"start": v(-170.44, 33.78) * mm, "end": v(-170.92, 33.64) * mm});
            skLineSegment(sketch, "E1271", {"start": v(-170.92, 33.64) * mm, "end": v(-171.4, 33.52) * mm});
            skLineSegment(sketch, "E1272", {"start": v(-171.4, 33.52) * mm, "end": v(-171.88, 33.42) * mm});
            skLineSegment(sketch, "E1273", {"start": v(-171.88, 33.42) * mm, "end": v(-172.37, 33.32) * mm});
            skLineSegment(sketch, "E1274", {"start": v(-172.37, 33.32) * mm, "end": v(-172.86, 33.23) * mm});
            skLineSegment(sketch, "E1275", {"start": v(-172.86, 33.23) * mm, "end": v(-173.36, 33.16) * mm});
            skLineSegment(sketch, "E1276", {"start": v(-173.36, 33.16) * mm, "end": v(-173.85, 33.1) * mm});
            skLineSegment(sketch, "E1277", {"start": v(-173.85, 33.1) * mm, "end": v(-174.35, 33.05) * mm});
            skLineSegment(sketch, "E1278", {"start": v(-174.35, 33.05) * mm, "end": v(-174.85, 33.02) * mm});
            skLineSegment(sketch, "E1279", {"start": v(-174.85, 33.02) * mm, "end": v(-175.35, 33) * mm});
            skLineSegment(sketch, "E1280", {"start": v(-175.35, 33) * mm, "end": v(-175.85, 32.99) * mm});
            skLineSegment(sketch, "E1281", {"start": v(-175.85, 32.99) * mm, "end": v(-176.35, 33) * mm});
            skLineSegment(sketch, "E1282", {"start": v(-176.35, 33) * mm, "end": v(-176.78, 32.98) * mm});
            skLineSegment(sketch, "E1283", {"start": v(-176.78, 32.98) * mm, "end": v(-177.2, 32.98) * mm});
            skLineSegment(sketch, "E1284", {"start": v(-177.2, 32.98) * mm, "end": v(-177.62, 33) * mm});
            skLineSegment(sketch, "E1285", {"start": v(-177.62, 33) * mm, "end": v(-178.04, 33.01) * mm});
            skLineSegment(sketch, "E1286", {"start": v(-178.04, 33.01) * mm, "end": v(-178.45, 33.05) * mm});
            skLineSegment(sketch, "E1287", {"start": v(-178.45, 33.05) * mm, "end": v(-178.87, 33.09) * mm});
            skLineSegment(sketch, "E1288", {"start": v(-178.87, 33.09) * mm, "end": v(-179.28, 33.14) * mm});
            skLineSegment(sketch, "E1289", {"start": v(-179.28, 33.14) * mm, "end": v(-179.7, 33.2) * mm});
            skLineSegment(sketch, "E1290", {"start": v(-179.7, 33.2) * mm, "end": v(-180.1, 33.27) * mm});
            skLineSegment(sketch, "E1291", {"start": v(-180.1, 33.27) * mm, "end": v(-180.52, 33.36) * mm});
            skLineSegment(sketch, "E1292", {"start": v(-180.52, 33.36) * mm, "end": v(-180.92, 33.45) * mm});
            skLineSegment(sketch, "E1293", {"start": v(-180.92, 33.45) * mm, "end": v(-181.33, 33.55) * mm});
            skLineSegment(sketch, "E1294", {"start": v(-181.33, 33.55) * mm, "end": v(-181.73, 33.66) * mm});
            skLineSegment(sketch, "E1295", {"start": v(-181.73, 33.66) * mm, "end": v(-182.12, 33.78) * mm});
            skLineSegment(sketch, "E1296", {"start": v(-182.12, 33.78) * mm, "end": v(-182.52, 33.91) * mm});
            skLineSegment(sketch, "E1297", {"start": v(-182.52, 33.91) * mm, "end": v(-182.9, 34.06) * mm});
            skLineSegment(sketch, "E1298", {"start": v(-182.9, 34.06) * mm, "end": v(-183.3, 34.2) * mm});
            skLineSegment(sketch, "E1299", {"start": v(-183.3, 34.2) * mm, "end": v(-183.68, 34.37) * mm});
            skLineSegment(sketch, "E1300", {"start": v(-183.68, 34.37) * mm, "end": v(-184.06, 34.53) * mm});
            skLineSegment(sketch, "E1301", {"start": v(-184.06, 34.53) * mm, "end": v(-184.44, 34.71) * mm});
            skLineSegment(sketch, "E1302", {"start": v(-184.44, 34.71) * mm, "end": v(-184.8, 34.9) * mm});
            skLineSegment(sketch, "E1303", {"start": v(-184.8, 34.9) * mm, "end": v(-185.18, 35.1) * mm});
            skLineSegment(sketch, "E1304", {"start": v(-185.18, 35.1) * mm, "end": v(-185.54, 35.3) * mm});
            skLineSegment(sketch, "E1305", {"start": v(-185.54, 35.3) * mm, "end": v(-185.9, 35.52) * mm});
            skLineSegment(sketch, "E1306", {"start": v(-185.9, 35.52) * mm, "end": v(-186.25, 35.74) * mm});
            skLineSegment(sketch, "E1307", {"start": v(-186.25, 35.74) * mm, "end": v(-186.6, 35.97) * mm});
            skLineSegment(sketch, "E1308", {"start": v(-186.6, 35.97) * mm, "end": v(-186.94, 36.21) * mm});
            skLineSegment(sketch, "E1309", {"start": v(-186.94, 36.21) * mm, "end": v(-187.27, 36.46) * mm});
            skLineSegment(sketch, "E1310", {"start": v(-187.27, 36.46) * mm, "end": v(-187.6, 36.72) * mm});
            skLineSegment(sketch, "E1311", {"start": v(-187.6, 36.72) * mm, "end": v(-187.93, 37) * mm});
            skLineSegment(sketch, "E1312", {"start": v(-187.93, 37) * mm, "end": v(-188.24, 37.27) * mm});
            skLineSegment(sketch, "E1313", {"start": v(-188.24, 37.27) * mm, "end": v(-188.56, 37.55) * mm});
            skLineSegment(sketch, "E1314", {"start": v(-188.56, 37.55) * mm, "end": v(-188.8, 37.8) * mm});
            skLineSegment(sketch, "E1315", {"start": v(-188.8, 37.8) * mm, "end": v(-189.05, 38.04) * mm});
            skLineSegment(sketch, "E1316", {"start": v(-189.05, 38.04) * mm, "end": v(-189.28, 38.29) * mm});
            skLineSegment(sketch, "E1317", {"start": v(-189.28, 38.29) * mm, "end": v(-189.51, 38.54) * mm});
            skLineSegment(sketch, "E1318", {"start": v(-189.51, 38.54) * mm, "end": v(-189.73, 38.8) * mm});
            skLineSegment(sketch, "E1319", {"start": v(-189.73, 38.8) * mm, "end": v(-189.95, 39.07) * mm});
            skLineSegment(sketch, "E1320", {"start": v(-189.95, 39.07) * mm, "end": v(-190.16, 39.34) * mm});
            skLineSegment(sketch, "E1321", {"start": v(-190.16, 39.34) * mm, "end": v(-190.36, 39.62) * mm});
            skLineSegment(sketch, "E1322", {"start": v(-190.36, 39.62) * mm, "end": v(-190.56, 39.9) * mm});
            skLineSegment(sketch, "E1323", {"start": v(-190.56, 39.9) * mm, "end": v(-190.74, 40.18) * mm});
            skLineSegment(sketch, "E1324", {"start": v(-190.74, 40.18) * mm, "end": v(-190.92, 40.47) * mm});
            skLineSegment(sketch, "E1325", {"start": v(-190.92, 40.47) * mm, "end": v(-191.1, 40.77) * mm});
            skLineSegment(sketch, "E1326", {"start": v(-191.1, 40.77) * mm, "end": v(-191.26, 41.06) * mm});
            skLineSegment(sketch, "E1327", {"start": v(-191.26, 41.06) * mm, "end": v(-191.42, 41.36) * mm});
            skLineSegment(sketch, "E1328", {"start": v(-191.42, 41.36) * mm, "end": v(-191.57, 41.67) * mm});
            skLineSegment(sketch, "E1329", {"start": v(-191.57, 41.67) * mm, "end": v(-191.72, 41.98) * mm});
            skLineSegment(sketch, "E1330", {"start": v(-191.72, 41.98) * mm, "end": v(-191.85, 42.3) * mm});
            skLineSegment(sketch, "E1331", {"start": v(-191.85, 42.3) * mm, "end": v(-191.98, 42.6) * mm});
            skLineSegment(sketch, "E1332", {"start": v(-191.98, 42.6) * mm, "end": v(-192.1, 42.92) * mm});
            skLineSegment(sketch, "E1333", {"start": v(-192.1, 42.92) * mm, "end": v(-192.22, 43.24) * mm});
            skLineSegment(sketch, "E1334", {"start": v(-192.22, 43.24) * mm, "end": v(-192.32, 43.57) * mm});
            skLineSegment(sketch, "E1335", {"start": v(-192.32, 43.57) * mm, "end": v(-192.42, 43.9) * mm});
            skLineSegment(sketch, "E1336", {"start": v(-192.42, 43.9) * mm, "end": v(-192.51, 44.23) * mm});
            skLineSegment(sketch, "E1337", {"start": v(-192.51, 44.23) * mm, "end": v(-192.6, 44.56) * mm});
            skLineSegment(sketch, "E1338", {"start": v(-192.6, 44.56) * mm, "end": v(-192.67, 44.9) * mm});
            skLineSegment(sketch, "E1339", {"start": v(-192.67, 44.9) * mm, "end": v(-192.73, 45.23) * mm});
            skLineSegment(sketch, "E1340", {"start": v(-192.73, 45.23) * mm, "end": v(-192.8, 45.56) * mm});
            skLineSegment(sketch, "E1341", {"start": v(-192.8, 45.56) * mm, "end": v(-192.84, 45.9) * mm});
            skLineSegment(sketch, "E1342", {"start": v(-192.84, 45.9) * mm, "end": v(-192.88, 46.24) * mm});
            skLineSegment(sketch, "E1343", {"start": v(-192.88, 46.24) * mm, "end": v(-192.92, 46.59) * mm});
            skLineSegment(sketch, "E1344", {"start": v(-192.92, 46.59) * mm, "end": v(-192.94, 46.93) * mm});
            skLineSegment(sketch, "E1345", {"start": v(-192.94, 46.93) * mm, "end": v(-192.96, 47.28) * mm});
            skLineSegment(sketch, "E1346", {"start": v(-192.96, 47.28) * mm, "end": v(-192.96, 60.1) * mm});
            skLineSegment(sketch, "E1347", {"start": v(-192.95, 2.07) * mm, "end": v(-192.95, 25.1) * mm});
            skLineSegment(sketch, "E1348", {"start": v(-192.95, 25.1) * mm, "end": v(-158, 25.1) * mm});
            skLineSegment(sketch, "E1349", {"start": v(-158, 25.1) * mm, "end": v(-158, 2.07) * mm});
            skLineSegment(sketch, "E1350", {"start": v(-174.84, 25.1) * mm, "end": v(-174.84, 4.96) * mm});
            skLineSegment(sketch, "E1351", {"start": v(-192.95, -5.63) * mm, "end": v(-157.98, -5.63) * mm});
            skLineSegment(sketch, "E1352", {"start": v(-157.98, -5.63) * mm, "end": v(-157.98, -21) * mm});
            skLineSegment(sketch, "E1353", {"start": v(-157.98, -21) * mm, "end": v(-157.99, -21.43) * mm});
            skLineSegment(sketch, "E1354", {"start": v(-157.99, -21.43) * mm, "end": v(-158.01, -21.86) * mm});
            skLineSegment(sketch, "E1355", {"start": v(-158.01, -21.86) * mm, "end": v(-158.06, -22.28) * mm});
            skLineSegment(sketch, "E1356", {"start": v(-158.06, -22.28) * mm, "end": v(-158.13, -22.7) * mm});
            skLineSegment(sketch, "E1357", {"start": v(-158.13, -22.7) * mm, "end": v(-158.22, -23.12) * mm});
            skLineSegment(sketch, "E1358", {"start": v(-158.22, -23.12) * mm, "end": v(-158.33, -23.54) * mm});
            skLineSegment(sketch, "E1359", {"start": v(-158.33, -23.54) * mm, "end": v(-158.46, -23.94) * mm});
            skLineSegment(sketch, "E1360", {"start": v(-158.46, -23.94) * mm, "end": v(-158.61, -24.34) * mm});
            skLineSegment(sketch, "E1361", {"start": v(-158.61, -24.34) * mm, "end": v(-158.79, -24.73) * mm});
            skLineSegment(sketch, "E1362", {"start": v(-158.79, -24.73) * mm, "end": v(-158.98, -25.1) * mm});
            skLineSegment(sketch, "E1363", {"start": v(-158.98, -25.1) * mm, "end": v(-159.19, -25.48) * mm});
            skLineSegment(sketch, "E1364", {"start": v(-159.19, -25.48) * mm, "end": v(-159.42, -25.84) * mm});
            skLineSegment(sketch, "E1365", {"start": v(-159.42, -25.84) * mm, "end": v(-159.67, -26.19) * mm});
            skLineSegment(sketch, "E1366", {"start": v(-159.67, -26.19) * mm, "end": v(-159.93, -26.52) * mm});
            skLineSegment(sketch, "E1367", {"start": v(-159.93, -26.52) * mm, "end": v(-160.22, -26.85) * mm});
            skLineSegment(sketch, "E1368", {"start": v(-160.22, -26.85) * mm, "end": v(-160.52, -27.16) * mm});
            skLineSegment(sketch, "E1369", {"start": v(-160.52, -27.16) * mm, "end": v(-160.83, -27.45) * mm});
            skLineSegment(sketch, "E1370", {"start": v(-160.83, -27.45) * mm, "end": v(-161.15, -27.74) * mm});
            skLineSegment(sketch, "E1371", {"start": v(-161.15, -27.74) * mm, "end": v(-161.48, -28) * mm});
            skLineSegment(sketch, "E1372", {"start": v(-161.48, -28) * mm, "end": v(-161.83, -28.25) * mm});
            skLineSegment(sketch, "E1373", {"start": v(-161.83, -28.25) * mm, "end": v(-162.19, -28.47) * mm});
            skLineSegment(sketch, "E1374", {"start": v(-162.19, -28.47) * mm, "end": v(-162.55, -28.68) * mm});
            skLineSegment(sketch, "E1375", {"start": v(-162.55, -28.68) * mm, "end": v(-162.93, -28.87) * mm});
            skLineSegment(sketch, "E1376", {"start": v(-162.93, -28.87) * mm, "end": v(-163.32, -29.05) * mm});
            skLineSegment(sketch, "E1377", {"start": v(-163.32, -29.05) * mm, "end": v(-163.71, -29.2) * mm});
            skLineSegment(sketch, "E1378", {"start": v(-163.71, -29.2) * mm, "end": v(-164.11, -29.33) * mm});
            skLineSegment(sketch, "E1379", {"start": v(-164.11, -29.33) * mm, "end": v(-164.52, -29.45) * mm});
            skLineSegment(sketch, "E1380", {"start": v(-164.52, -29.45) * mm, "end": v(-164.93, -29.54) * mm});
            skLineSegment(sketch, "E1381", {"start": v(-164.93, -29.54) * mm, "end": v(-165.35, -29.62) * mm});
            skLineSegment(sketch, "E1382", {"start": v(-165.35, -29.62) * mm, "end": v(-165.77, -29.67) * mm});
            skLineSegment(sketch, "E1383", {"start": v(-165.77, -29.67) * mm, "end": v(-166.2, -29.7) * mm});
            skLineSegment(sketch, "E1384", {"start": v(-166.2, -29.7) * mm, "end": v(-166.63, -29.7) * mm});
            skLineSegment(sketch, "E1385", {"start": v(-166.63, -29.7) * mm, "end": v(-167.06, -29.71) * mm});
            skLineSegment(sketch, "E1386", {"start": v(-167.06, -29.71) * mm, "end": v(-167.5, -29.7) * mm});
            skLineSegment(sketch, "E1387", {"start": v(-167.5, -29.7) * mm, "end": v(-167.93, -29.65) * mm});
            skLineSegment(sketch, "E1388", {"start": v(-167.93, -29.65) * mm, "end": v(-168.36, -29.59) * mm});
            skLineSegment(sketch, "E1389", {"start": v(-168.36, -29.59) * mm, "end": v(-168.79, -29.5) * mm});
            skLineSegment(sketch, "E1390", {"start": v(-168.79, -29.5) * mm, "end": v(-169.2, -29.4) * mm});
            skLineSegment(sketch, "E1391", {"start": v(-169.2, -29.4) * mm, "end": v(-169.62, -29.27) * mm});
            skLineSegment(sketch, "E1392", {"start": v(-169.62, -29.27) * mm, "end": v(-170.03, -29.12) * mm});
            skLineSegment(sketch, "E1393", {"start": v(-170.03, -29.12) * mm, "end": v(-170.43, -28.95) * mm});
            skLineSegment(sketch, "E1394", {"start": v(-170.43, -28.95) * mm, "end": v(-170.82, -28.76) * mm});
            skLineSegment(sketch, "E1395", {"start": v(-170.82, -28.76) * mm, "end": v(-171.2, -28.55) * mm});
            skLineSegment(sketch, "E1396", {"start": v(-171.2, -28.55) * mm, "end": v(-171.57, -28.32) * mm});
            skLineSegment(sketch, "E1397", {"start": v(-171.57, -28.32) * mm, "end": v(-171.92, -28.08) * mm});
            skLineSegment(sketch, "E1398", {"start": v(-171.92, -28.08) * mm, "end": v(-172.27, -27.81) * mm});
            skLineSegment(sketch, "E1399", {"start": v(-172.27, -27.81) * mm, "end": v(-172.6, -27.53) * mm});
            skLineSegment(sketch, "E1400", {"start": v(-172.6, -27.53) * mm, "end": v(-172.92, -27.23) * mm});
            skLineSegment(sketch, "E1401", {"start": v(-172.92, -27.23) * mm, "end": v(-173.22, -26.91) * mm});
            skLineSegment(sketch, "E1402", {"start": v(-173.22, -26.91) * mm, "end": v(-173.5, -26.58) * mm});
            skLineSegment(sketch, "E1403", {"start": v(-173.5, -26.58) * mm, "end": v(-173.77, -26.24) * mm});
            skLineSegment(sketch, "E1404", {"start": v(-173.77, -26.24) * mm, "end": v(-174.02, -25.89) * mm});
            skLineSegment(sketch, "E1405", {"start": v(-174.02, -25.89) * mm, "end": v(-174.25, -25.52) * mm});
            skLineSegment(sketch, "E1406", {"start": v(-174.25, -25.52) * mm, "end": v(-174.46, -25.15) * mm});
            skLineSegment(sketch, "E1407", {"start": v(-174.46, -25.15) * mm, "end": v(-174.65, -24.76) * mm});
            skLineSegment(sketch, "E1408", {"start": v(-174.65, -24.76) * mm, "end": v(-174.82, -24.37) * mm});
            skLineSegment(sketch, "E1409", {"start": v(-174.82, -24.37) * mm, "end": v(-174.97, -23.97) * mm});
            skLineSegment(sketch, "E1410", {"start": v(-174.97, -23.97) * mm, "end": v(-175.1, -23.56) * mm});
            skLineSegment(sketch, "E1411", {"start": v(-175.1, -23.56) * mm, "end": v(-175.22, -23.14) * mm});
            skLineSegment(sketch, "E1412", {"start": v(-175.22, -23.14) * mm, "end": v(-175.3, -22.72) * mm});
            skLineSegment(sketch, "E1413", {"start": v(-175.3, -22.72) * mm, "end": v(-175.38, -22.3) * mm});
            skLineSegment(sketch, "E1414", {"start": v(-175.38, -22.3) * mm, "end": v(-175.43, -21.86) * mm});
            skLineSegment(sketch, "E1415", {"start": v(-175.43, -21.86) * mm, "end": v(-175.45, -21.43) * mm});
            skLineSegment(sketch, "E1416", {"start": v(-175.45, -21.43) * mm, "end": v(-175.46, -21) * mm});
            skLineSegment(sketch, "E1417", {"start": v(-175.46, -21) * mm, "end": v(-175.46, -5.63) * mm});
            skLineSegment(sketch, "E1418", {"start": v(-175.46, -21) * mm, "end": v(-175.46, -21.35) * mm});
            skLineSegment(sketch, "E1419", {"start": v(-175.46, -21.35) * mm, "end": v(-175.48, -21.7) * mm});
            skLineSegment(sketch, "E1420", {"start": v(-175.48, -21.7) * mm, "end": v(-175.52, -22.06) * mm});
            skLineSegment(sketch, "E1421", {"start": v(-175.52, -22.06) * mm, "end": v(-175.57, -22.41) * mm});
            skLineSegment(sketch, "E1422", {"start": v(-175.57, -22.41) * mm, "end": v(-175.65, -22.76) * mm});
            skLineSegment(sketch, "E1423", {"start": v(-175.65, -22.76) * mm, "end": v(-175.74, -23.1) * mm});
            skLineSegment(sketch, "E1424", {"start": v(-175.74, -23.1) * mm, "end": v(-175.85, -23.44) * mm});
            skLineSegment(sketch, "E1425", {"start": v(-175.85, -23.44) * mm, "end": v(-175.97, -23.77) * mm});
            skLineSegment(sketch, "E1426", {"start": v(-175.97, -23.77) * mm, "end": v(-176.11, -24.1) * mm});
            skLineSegment(sketch, "E1427", {"start": v(-176.11, -24.1) * mm, "end": v(-176.27, -24.4) * mm});
            skLineSegment(sketch, "E1428", {"start": v(-176.27, -24.4) * mm, "end": v(-176.44, -24.72) * mm});
            skLineSegment(sketch, "E1429", {"start": v(-176.44, -24.72) * mm, "end": v(-176.63, -25.02) * mm});
            skLineSegment(sketch, "E1430", {"start": v(-176.63, -25.02) * mm, "end": v(-176.84, -25.3) * mm});
            skLineSegment(sketch, "E1431", {"start": v(-176.84, -25.3) * mm, "end": v(-177.06, -25.59) * mm});
            skLineSegment(sketch, "E1432", {"start": v(-177.06, -25.59) * mm, "end": v(-177.3, -25.86) * mm});
            skLineSegment(sketch, "E1433", {"start": v(-177.3, -25.86) * mm, "end": v(-177.54, -26.11) * mm});
            skLineSegment(sketch, "E1434", {"start": v(-177.54, -26.11) * mm, "end": v(-177.98, -26.41) * mm});
            skLineSegment(sketch, "E1435", {"start": v(-177.98, -26.41) * mm, "end": v(-178.43, -26.7) * mm});
            skLineSegment(sketch, "E1436", {"start": v(-178.43, -26.7) * mm, "end": v(-178.89, -26.95) * mm});
            skLineSegment(sketch, "E1437", {"start": v(-178.89, -26.95) * mm, "end": v(-179.36, -27.18) * mm});
            skLineSegment(sketch, "E1438", {"start": v(-179.36, -27.18) * mm, "end": v(-179.84, -27.4) * mm});
            skLineSegment(sketch, "E1439", {"start": v(-179.84, -27.4) * mm, "end": v(-180.33, -27.59) * mm});
            skLineSegment(sketch, "E1440", {"start": v(-180.33, -27.59) * mm, "end": v(-180.82, -27.76) * mm});
            skLineSegment(sketch, "E1441", {"start": v(-180.82, -27.76) * mm, "end": v(-181.32, -27.9) * mm});
            skLineSegment(sketch, "E1442", {"start": v(-181.32, -27.9) * mm, "end": v(-181.83, -28.03) * mm});
            skLineSegment(sketch, "E1443", {"start": v(-181.83, -28.03) * mm, "end": v(-182.35, -28.14) * mm});
            skLineSegment(sketch, "E1444", {"start": v(-182.35, -28.14) * mm, "end": v(-182.86, -28.22) * mm});
            skLineSegment(sketch, "E1445", {"start": v(-182.86, -28.22) * mm, "end": v(-183.39, -28.27) * mm});
            skLineSegment(sketch, "E1446", {"start": v(-183.39, -28.27) * mm, "end": v(-183.91, -28.3) * mm});
            skLineSegment(sketch, "E1447", {"start": v(-183.91, -28.3) * mm, "end": v(-184.44, -28.32) * mm});
            skLineSegment(sketch, "E1448", {"start": v(-184.44, -28.32) * mm, "end": v(-184.96, -28.3) * mm});
            skLineSegment(sketch, "E1449", {"start": v(-184.96, -28.3) * mm, "end": v(-185.5, -28.27) * mm});
            skLineSegment(sketch, "E1450", {"start": v(-185.5, -28.27) * mm, "end": v(-185.96, -28.26) * mm});
            skLineSegment(sketch, "E1451", {"start": v(-185.96, -28.26) * mm, "end": v(-186.43, -28.26) * mm});
            skLineSegment(sketch, "E1452", {"start": v(-186.43, -28.26) * mm, "end": v(-186.9, -28.27) * mm});
            skLineSegment(sketch, "E1453", {"start": v(-186.9, -28.27) * mm, "end": v(-187.38, -28.3) * mm});
            skLineSegment(sketch, "E1454", {"start": v(-187.38, -28.3) * mm, "end": v(-187.85, -28.32) * mm});
            skLineSegment(sketch, "E1455", {"start": v(-187.85, -28.32) * mm, "end": v(-188.32, -28.35) * mm});
            skLineSegment(sketch, "E1456", {"start": v(-188.32, -28.35) * mm, "end": v(-188.78, -28.4) * mm});
            skLineSegment(sketch, "E1457", {"start": v(-188.78, -28.4) * mm, "end": v(-189.25, -28.45) * mm});
            skLineSegment(sketch, "E1458", {"start": v(-189.25, -28.45) * mm, "end": v(-189.72, -28.51) * mm});
            skLineSegment(sketch, "E1459", {"start": v(-189.72, -28.51) * mm, "end": v(-190.19, -28.58) * mm});
            skLineSegment(sketch, "E1460", {"start": v(-190.19, -28.58) * mm, "end": v(-190.65, -28.66) * mm});
            skLineSegment(sketch, "E1461", {"start": v(-190.65, -28.66) * mm, "end": v(-191.11, -28.74) * mm});
            skLineSegment(sketch, "E1462", {"start": v(-191.11, -28.74) * mm, "end": v(-191.58, -28.84) * mm});
            skLineSegment(sketch, "E1463", {"start": v(-191.58, -28.84) * mm, "end": v(-192.04, -28.94) * mm});
            skLineSegment(sketch, "E1464", {"start": v(-192.04, -28.94) * mm, "end": v(-192.5, -29.05) * mm});
            skLineSegment(sketch, "E1465", {"start": v(-192.5, -29.05) * mm, "end": v(-192.95, -29.17) * mm});
            skLineSegment(sketch, "E1466", {"start": v(489.44, -21.04) * mm, "end": v(489.84, -20.9) * mm});
            skLineSegment(sketch, "E1467", {"start": v(489.84, -20.9) * mm, "end": v(490.22, -20.76) * mm});
            skLineSegment(sketch, "E1468", {"start": v(490.22, -20.76) * mm, "end": v(490.6, -20.6) * mm});
            skLineSegment(sketch, "E1469", {"start": v(490.6, -20.6) * mm, "end": v(490.98, -20.44) * mm});
            skLineSegment(sketch, "E1470", {"start": v(490.98, -20.44) * mm, "end": v(491.35, -20.26) * mm});
            skLineSegment(sketch, "E1471", {"start": v(491.35, -20.26) * mm, "end": v(491.72, -20.07) * mm});
            skLineSegment(sketch, "E1472", {"start": v(491.72, -20.07) * mm, "end": v(492.08, -19.86) * mm});
            skLineSegment(sketch, "E1473", {"start": v(492.08, -19.86) * mm, "end": v(492.43, -19.65) * mm});
            skLineSegment(sketch, "E1474", {"start": v(492.43, -19.65) * mm, "end": v(492.78, -19.43) * mm});
            skLineSegment(sketch, "E1475", {"start": v(492.78, -19.43) * mm, "end": v(493.11, -19.2) * mm});
            skLineSegment(sketch, "E1476", {"start": v(493.11, -19.2) * mm, "end": v(493.44, -18.94) * mm});
            skLineSegment(sketch, "E1477", {"start": v(493.44, -18.94) * mm, "end": v(493.77, -18.69) * mm});
            skLineSegment(sketch, "E1478", {"start": v(493.77, -18.69) * mm, "end": v(494.08, -18.42) * mm});
            skLineSegment(sketch, "E1479", {"start": v(494.08, -18.42) * mm, "end": v(494.39, -18.14) * mm});
            skLineSegment(sketch, "E1480", {"start": v(494.39, -18.14) * mm, "end": v(494.69, -17.86) * mm});
            skLineSegment(sketch, "E1481", {"start": v(494.69, -17.86) * mm, "end": v(494.97, -17.56) * mm});
            skLineSegment(sketch, "E1482", {"start": v(494.97, -17.56) * mm, "end": v(495.2, -17.31) * mm});
            skLineSegment(sketch, "E1483", {"start": v(495.2, -17.31) * mm, "end": v(495.43, -17.06) * mm});
            skLineSegment(sketch, "E1484", {"start": v(495.43, -17.06) * mm, "end": v(495.64, -16.8) * mm});
            skLineSegment(sketch, "E1485", {"start": v(495.64, -16.8) * mm, "end": v(495.85, -16.54) * mm});
            skLineSegment(sketch, "E1486", {"start": v(495.85, -16.54) * mm, "end": v(496.05, -16.27) * mm});
            skLineSegment(sketch, "E1487", {"start": v(496.05, -16.27) * mm, "end": v(496.25, -16) * mm});
            skLineSegment(sketch, "E1488", {"start": v(496.25, -16) * mm, "end": v(496.43, -15.73) * mm});
            skLineSegment(sketch, "E1489", {"start": v(496.43, -15.73) * mm, "end": v(496.61, -15.45) * mm});
            skLineSegment(sketch, "E1490", {"start": v(496.61, -15.45) * mm, "end": v(496.79, -15.16) * mm});
            skLineSegment(sketch, "E1491", {"start": v(496.79, -15.16) * mm, "end": v(496.95, -14.87) * mm});
            skLineSegment(sketch, "E1492", {"start": v(496.95, -14.87) * mm, "end": v(497.1, -14.58) * mm});
            skLineSegment(sketch, "E1493", {"start": v(497.1, -14.58) * mm, "end": v(497.26, -14.28) * mm});
            skLineSegment(sketch, "E1494", {"start": v(497.26, -14.28) * mm, "end": v(497.4, -13.98) * mm});
            skLineSegment(sketch, "E1495", {"start": v(497.4, -13.98) * mm, "end": v(497.53, -13.68) * mm});
            skLineSegment(sketch, "E1496", {"start": v(497.53, -13.68) * mm, "end": v(497.66, -13.37) * mm});
            skLineSegment(sketch, "E1497", {"start": v(497.66, -13.37) * mm, "end": v(497.78, -13.06) * mm});
            skLineSegment(sketch, "E1498", {"start": v(497.78, -13.06) * mm, "end": v(497.9, -12.75) * mm});
            skLineSegment(sketch, "E1499", {"start": v(497.9, -12.75) * mm, "end": v(498, -12.43) * mm});
            skLineSegment(sketch, "E1500", {"start": v(498, -12.43) * mm, "end": v(498.09, -12.12) * mm});
            skLineSegment(sketch, "E1501", {"start": v(498.09, -12.12) * mm, "end": v(498.17, -11.8) * mm});
            skLineSegment(sketch, "E1502", {"start": v(498.17, -11.8) * mm, "end": v(498.25, -11.47) * mm});
            skLineSegment(sketch, "E1503", {"start": v(498.25, -11.47) * mm, "end": v(498.32, -11.15) * mm});
            skLineSegment(sketch, "E1504", {"start": v(498.32, -11.15) * mm, "end": v(498.39, -10.82) * mm});
            skLineSegment(sketch, "E1505", {"start": v(498.39, -10.82) * mm, "end": v(498.44, -10.5) * mm});
            skLineSegment(sketch, "E1506", {"start": v(498.44, -10.5) * mm, "end": v(498.48, -10.16) * mm});
            skLineSegment(sketch, "E1507", {"start": v(498.48, -10.16) * mm, "end": v(498.52, -9.83) * mm});
            skLineSegment(sketch, "E1508", {"start": v(498.52, -9.83) * mm, "end": v(498.55, -9.5) * mm});
            skLineSegment(sketch, "E1509", {"start": v(498.55, -9.5) * mm, "end": v(498.57, -9.16) * mm});
            skLineSegment(sketch, "E1510", {"start": v(498.57, -9.16) * mm, "end": v(498.58, -8.83) * mm});
            skLineSegment(sketch, "E1511", {"start": v(498.58, -8.83) * mm, "end": v(498.58, -8.5) * mm});
            skLineSegment(sketch, "E1512", {"start": v(498.58, -8.5) * mm, "end": v(498.58, -8.16) * mm});
            skLineSegment(sketch, "E1513", {"start": v(498.58, -8.16) * mm, "end": v(498.56, -7.82) * mm});
            skLineSegment(sketch, "E1514", {"start": v(498.56, -7.82) * mm, "end": v(498.57, -7.51) * mm});
            skLineSegment(sketch, "E1515", {"start": v(498.57, -7.51) * mm, "end": v(498.57, -7.2) * mm});
            skLineSegment(sketch, "E1516", {"start": v(498.57, -7.2) * mm, "end": v(498.57, -6.9) * mm});
            skLineSegment(sketch, "E1517", {"start": v(498.57, -6.9) * mm, "end": v(498.55, -6.59) * mm});
            skLineSegment(sketch, "E1518", {"start": v(498.55, -6.59) * mm, "end": v(498.53, -6.28) * mm});
            skLineSegment(sketch, "E1519", {"start": v(498.53, -6.28) * mm, "end": v(498.5, -5.97) * mm});
            skLineSegment(sketch, "E1520", {"start": v(498.5, -5.97) * mm, "end": v(498.46, -5.67) * mm});
            skLineSegment(sketch, "E1521", {"start": v(498.46, -5.67) * mm, "end": v(498.41, -5.37) * mm});
            skLineSegment(sketch, "E1522", {"start": v(498.41, -5.37) * mm, "end": v(498.36, -5.07) * mm});
            skLineSegment(sketch, "E1523", {"start": v(498.36, -5.07) * mm, "end": v(498.3, -4.77) * mm});
            skLineSegment(sketch, "E1524", {"start": v(498.3, -4.77) * mm, "end": v(498.23, -4.47) * mm});
            skLineSegment(sketch, "E1525", {"start": v(498.23, -4.47) * mm, "end": v(498.15, -4.17) * mm});
            skLineSegment(sketch, "E1526", {"start": v(498.15, -4.17) * mm, "end": v(498.07, -3.88) * mm});
            skLineSegment(sketch, "E1527", {"start": v(498.07, -3.88) * mm, "end": v(497.98, -3.59) * mm});
            skLineSegment(sketch, "E1528", {"start": v(497.98, -3.59) * mm, "end": v(497.88, -3.3) * mm});
            skLineSegment(sketch, "E1529", {"start": v(497.88, -3.3) * mm, "end": v(497.77, -3.01) * mm});
            skLineSegment(sketch, "E1530", {"start": v(497.77, -3.01) * mm, "end": v(497.66, -2.73) * mm});
            skLineSegment(sketch, "E1531", {"start": v(497.66, -2.73) * mm, "end": v(497.54, -2.45) * mm});
            skLineSegment(sketch, "E1532", {"start": v(497.54, -2.45) * mm, "end": v(497.4, -2.17) * mm});
            skLineSegment(sketch, "E1533", {"start": v(497.4, -2.17) * mm, "end": v(497.27, -1.9) * mm});
            skLineSegment(sketch, "E1534", {"start": v(497.27, -1.9) * mm, "end": v(497.13, -1.63) * mm});
            skLineSegment(sketch, "E1535", {"start": v(497.13, -1.63) * mm, "end": v(496.98, -1.36) * mm});
            skLineSegment(sketch, "E1536", {"start": v(496.98, -1.36) * mm, "end": v(496.83, -1.1) * mm});
            skLineSegment(sketch, "E1537", {"start": v(496.83, -1.1) * mm, "end": v(496.67, -0.84) * mm});
            skLineSegment(sketch, "E1538", {"start": v(496.67, -0.84) * mm, "end": v(496.5, -0.59) * mm});
            skLineSegment(sketch, "E1539", {"start": v(496.5, -0.59) * mm, "end": v(496.32, -0.33) * mm});
            skLineSegment(sketch, "E1540", {"start": v(496.32, -0.33) * mm, "end": v(496.14, -0.09) * mm});
            skLineSegment(sketch, "E1541", {"start": v(496.14, -0.09) * mm, "end": v(495.95, 0.15) * mm});
            skLineSegment(sketch, "E1542", {"start": v(495.95, 0.15) * mm, "end": v(495.75, 0.4) * mm});
            skLineSegment(sketch, "E1543", {"start": v(495.75, 0.4) * mm, "end": v(495.55, 0.63) * mm});
            skLineSegment(sketch, "E1544", {"start": v(495.55, 0.63) * mm, "end": v(495.34, 0.85) * mm});
            skLineSegment(sketch, "E1545", {"start": v(495.34, 0.85) * mm, "end": v(495.13, 1.08) * mm});
            skLineSegment(sketch, "E1546", {"start": v(495.13, 1.08) * mm, "end": v(494.83, 1.38) * mm});
            skLineSegment(sketch, "E1547", {"start": v(494.83, 1.38) * mm, "end": v(494.52, 1.66) * mm});
            skLineSegment(sketch, "E1548", {"start": v(494.52, 1.66) * mm, "end": v(494.2, 1.93) * mm});
            skLineSegment(sketch, "E1549", {"start": v(494.2, 1.93) * mm, "end": v(493.87, 2.18) * mm});
            skLineSegment(sketch, "E1550", {"start": v(493.87, 2.18) * mm, "end": v(493.53, 2.42) * mm});
            skLineSegment(sketch, "E1551", {"start": v(493.53, 2.42) * mm, "end": v(493.18, 2.63) * mm});
            skLineSegment(sketch, "E1552", {"start": v(493.18, 2.63) * mm, "end": v(492.82, 2.83) * mm});
            skLineSegment(sketch, "E1553", {"start": v(492.82, 2.83) * mm, "end": v(492.46, 3) * mm});
            skLineSegment(sketch, "E1554", {"start": v(492.46, 3) * mm, "end": v(492.08, 3.17) * mm});
            skLineSegment(sketch, "E1555", {"start": v(492.08, 3.17) * mm, "end": v(491.7, 3.32) * mm});
            skLineSegment(sketch, "E1556", {"start": v(491.7, 3.32) * mm, "end": v(491.33, 3.45) * mm});
            skLineSegment(sketch, "E1557", {"start": v(491.33, 3.45) * mm, "end": v(490.94, 3.55) * mm});
            skLineSegment(sketch, "E1558", {"start": v(490.94, 3.55) * mm, "end": v(490.55, 3.65) * mm});
            skLineSegment(sketch, "E1559", {"start": v(490.55, 3.65) * mm, "end": v(490.15, 3.72) * mm});
            skLineSegment(sketch, "E1560", {"start": v(490.15, 3.72) * mm, "end": v(489.76, 3.78) * mm});
            skLineSegment(sketch, "E1561", {"start": v(489.76, 3.78) * mm, "end": v(489.36, 3.81) * mm});
            skLineSegment(sketch, "E1562", {"start": v(489.36, 3.81) * mm, "end": v(488.96, 3.83) * mm});
            skLineSegment(sketch, "E1563", {"start": v(488.96, 3.83) * mm, "end": v(488.56, 3.84) * mm});
            skLineSegment(sketch, "E1564", {"start": v(488.56, 3.84) * mm, "end": v(488.16, 3.82) * mm});
            skLineSegment(sketch, "E1565", {"start": v(488.16, 3.82) * mm, "end": v(487.76, 3.79) * mm});
            skLineSegment(sketch, "E1566", {"start": v(487.76, 3.79) * mm, "end": v(487.36, 3.73) * mm});
            skLineSegment(sketch, "E1567", {"start": v(487.36, 3.73) * mm, "end": v(486.96, 3.66) * mm});
            skLineSegment(sketch, "E1568", {"start": v(486.96, 3.66) * mm, "end": v(486.57, 3.57) * mm});
            skLineSegment(sketch, "E1569", {"start": v(486.57, 3.57) * mm, "end": v(486.17, 3.46) * mm});
            skLineSegment(sketch, "E1570", {"start": v(486.17, 3.46) * mm, "end": v(485.79, 3.34) * mm});
            skLineSegment(sketch, "E1571", {"start": v(485.79, 3.34) * mm, "end": v(485.4, 3.2) * mm});
            skLineSegment(sketch, "E1572", {"start": v(485.4, 3.2) * mm, "end": v(485.03, 3.03) * mm});
            skLineSegment(sketch, "E1573", {"start": v(485.03, 3.03) * mm, "end": v(484.66, 2.85) * mm});
            skLineSegment(sketch, "E1574", {"start": v(484.66, 2.85) * mm, "end": v(484.3, 2.65) * mm});
            skLineSegment(sketch, "E1575", {"start": v(484.3, 2.65) * mm, "end": v(483.94, 2.43) * mm});
            skLineSegment(sketch, "E1576", {"start": v(483.94, 2.43) * mm, "end": v(483.6, 2.2) * mm});
            skLineSegment(sketch, "E1577", {"start": v(483.6, 2.2) * mm, "end": v(483.25, 1.94) * mm});
            skLineSegment(sketch, "E1578", {"start": v(483.25, 1.94) * mm, "end": v(482.99, 1.68) * mm});
            skLineSegment(sketch, "E1579", {"start": v(482.99, 1.68) * mm, "end": v(482.73, 1.41) * mm});
            skLineSegment(sketch, "E1580", {"start": v(482.73, 1.41) * mm, "end": v(482.49, 1.14) * mm});
            skLineSegment(sketch, "E1581", {"start": v(482.49, 1.14) * mm, "end": v(482.25, 0.87) * mm});
            skLineSegment(sketch, "E1582", {"start": v(482.25, 0.87) * mm, "end": v(482.02, 0.58) * mm});
            skLineSegment(sketch, "E1583", {"start": v(482.02, 0.58) * mm, "end": v(481.8, 0.3) * mm});
            skLineSegment(sketch, "E1584", {"start": v(481.8, 0.3) * mm, "end": v(481.58, 0) * mm});
            skLineSegment(sketch, "E1585", {"start": v(481.58, 0) * mm, "end": v(481.37, -0.3) * mm});
            skLineSegment(sketch, "E1586", {"start": v(481.37, -0.3) * mm, "end": v(481.17, -0.6) * mm});
            skLineSegment(sketch, "E1587", {"start": v(481.17, -0.6) * mm, "end": v(480.98, -0.91) * mm});
            skLineSegment(sketch, "E1588", {"start": v(480.98, -0.91) * mm, "end": v(480.8, -1.23) * mm});
            skLineSegment(sketch, "E1589", {"start": v(480.8, -1.23) * mm, "end": v(480.63, -1.55) * mm});
            skLineSegment(sketch, "E1590", {"start": v(480.63, -1.55) * mm, "end": v(480.47, -1.87) * mm});
            skLineSegment(sketch, "E1591", {"start": v(480.47, -1.87) * mm, "end": v(480.31, -2.2) * mm});
            skLineSegment(sketch, "E1592", {"start": v(480.31, -2.2) * mm, "end": v(480.17, -2.53) * mm});
            skLineSegment(sketch, "E1593", {"start": v(480.17, -2.53) * mm, "end": v(480.03, -2.86) * mm});
            skLineSegment(sketch, "E1594", {"start": v(480.03, -2.86) * mm, "end": v(479.9, -3.2) * mm});
            skLineSegment(sketch, "E1595", {"start": v(479.9, -3.2) * mm, "end": v(479.78, -3.54) * mm});
            skLineSegment(sketch, "E1596", {"start": v(479.78, -3.54) * mm, "end": v(479.67, -3.88) * mm});
            skLineSegment(sketch, "E1597", {"start": v(479.67, -3.88) * mm, "end": v(479.57, -4.23) * mm});
            skLineSegment(sketch, "E1598", {"start": v(479.57, -4.23) * mm, "end": v(479.48, -4.58) * mm});
            skLineSegment(sketch, "E1599", {"start": v(479.48, -4.58) * mm, "end": v(479.4, -4.94) * mm});
            skLineSegment(sketch, "E1600", {"start": v(479.4, -4.94) * mm, "end": v(479.32, -5.3) * mm});
            skLineSegment(sketch, "E1601", {"start": v(479.32, -5.3) * mm, "end": v(479.26, -5.65) * mm});
            skLineSegment(sketch, "E1602", {"start": v(479.26, -5.65) * mm, "end": v(479.2, -6) * mm});
            skLineSegment(sketch, "E1603", {"start": v(479.2, -6) * mm, "end": v(479.16, -6.37) * mm});
            skLineSegment(sketch, "E1604", {"start": v(479.16, -6.37) * mm, "end": v(479.12, -6.73) * mm});
            skLineSegment(sketch, "E1605", {"start": v(479.12, -6.73) * mm, "end": v(479.1, -7.1) * mm});
            skLineSegment(sketch, "E1606", {"start": v(479.1, -7.1) * mm, "end": v(479.08, -7.46) * mm});
            skLineSegment(sketch, "E1607", {"start": v(479.08, -7.46) * mm, "end": v(479.08, -7.83) * mm});
            skLineSegment(sketch, "E1608", {"start": v(479.08, -7.83) * mm, "end": v(479.08, -8.2) * mm});
            skLineSegment(sketch, "E1609", {"start": v(479.08, -8.2) * mm, "end": v(479.1, -8.57) * mm});
            skLineSegment(sketch, "E1610", {"start": v(479.1, -8.57) * mm, "end": v(479.15, -9.06) * mm});
            skLineSegment(sketch, "E1611", {"start": v(479.15, -9.06) * mm, "end": v(479.18, -9.54) * mm});
            skLineSegment(sketch, "E1612", {"start": v(479.18, -9.54) * mm, "end": v(479.19, -10.03) * mm});
            skLineSegment(sketch, "E1613", {"start": v(479.19, -10.03) * mm, "end": v(479.17, -10.51) * mm});
            skLineSegment(sketch, "E1614", {"start": v(479.17, -10.51) * mm, "end": v(479.13, -10.99) * mm});
            skLineSegment(sketch, "E1615", {"start": v(479.13, -10.99) * mm, "end": v(479.07, -11.46) * mm});
            skLineSegment(sketch, "E1616", {"start": v(479.07, -11.46) * mm, "end": v(478.99, -11.93) * mm});
            skLineSegment(sketch, "E1617", {"start": v(478.99, -11.93) * mm, "end": v(478.88, -12.39) * mm});
            skLineSegment(sketch, "E1618", {"start": v(478.88, -12.39) * mm, "end": v(478.75, -12.84) * mm});
            skLineSegment(sketch, "E1619", {"start": v(478.75, -12.84) * mm, "end": v(478.6, -13.28) * mm});
            skLineSegment(sketch, "E1620", {"start": v(478.6, -13.28) * mm, "end": v(478.44, -13.72) * mm});
            skLineSegment(sketch, "E1621", {"start": v(478.44, -13.72) * mm, "end": v(478.25, -14.15) * mm});
            skLineSegment(sketch, "E1622", {"start": v(478.25, -14.15) * mm, "end": v(478.04, -14.56) * mm});
            skLineSegment(sketch, "E1623", {"start": v(478.04, -14.56) * mm, "end": v(477.82, -14.97) * mm});
            skLineSegment(sketch, "E1624", {"start": v(477.82, -14.97) * mm, "end": v(477.58, -15.36) * mm});
            skLineSegment(sketch, "E1625", {"start": v(477.58, -15.36) * mm, "end": v(477.31, -15.75) * mm});
            skLineSegment(sketch, "E1626", {"start": v(477.31, -15.75) * mm, "end": v(477.03, -16.12) * mm});
            skLineSegment(sketch, "E1627", {"start": v(477.03, -16.12) * mm, "end": v(476.74, -16.48) * mm});
            skLineSegment(sketch, "E1628", {"start": v(476.74, -16.48) * mm, "end": v(476.43, -16.82) * mm});
            skLineSegment(sketch, "E1629", {"start": v(476.43, -16.82) * mm, "end": v(476.1, -17.15) * mm});
            skLineSegment(sketch, "E1630", {"start": v(476.1, -17.15) * mm, "end": v(475.75, -17.47) * mm});
            skLineSegment(sketch, "E1631", {"start": v(475.75, -17.47) * mm, "end": v(475.4, -17.77) * mm});
            skLineSegment(sketch, "E1632", {"start": v(475.4, -17.77) * mm, "end": v(475.02, -18.05) * mm});
            skLineSegment(sketch, "E1633", {"start": v(475.02, -18.05) * mm, "end": v(474.63, -18.32) * mm});
            skLineSegment(sketch, "E1634", {"start": v(474.63, -18.32) * mm, "end": v(474.23, -18.56) * mm});
            skLineSegment(sketch, "E1635", {"start": v(474.23, -18.56) * mm, "end": v(473.82, -18.8) * mm});
            skLineSegment(sketch, "E1636", {"start": v(473.82, -18.8) * mm, "end": v(473.4, -19) * mm});
            skLineSegment(sketch, "E1637", {"start": v(473.4, -19) * mm, "end": v(472.95, -19.2) * mm});
            skLineSegment(sketch, "E1638", {"start": v(472.95, -19.2) * mm, "end": v(472.5, -19.37) * mm});
            skLineSegment(sketch, "E1639", {"start": v(472.5, -19.37) * mm, "end": v(472.04, -19.52) * mm});
            skLineSegment(sketch, "E1640", {"start": v(472.04, -19.52) * mm, "end": v(471.57, -19.64) * mm});
            skLineSegment(sketch, "E1641", {"start": v(471.57, -19.64) * mm, "end": v(471.09, -19.75) * mm});
            skLineSegment(sketch, "E1642", {"start": v(471.09, -19.75) * mm, "end": v(470.69, -19.75) * mm});
            skLineSegment(sketch, "E1643", {"start": v(470.69, -19.75) * mm, "end": v(470.29, -19.72) * mm});
            skLineSegment(sketch, "E1644", {"start": v(470.29, -19.72) * mm, "end": v(469.9, -19.68) * mm});
            skLineSegment(sketch, "E1645", {"start": v(469.9, -19.68) * mm, "end": v(469.5, -19.61) * mm});
            skLineSegment(sketch, "E1646", {"start": v(469.5, -19.61) * mm, "end": v(469.12, -19.52) * mm});
            skLineSegment(sketch, "E1647", {"start": v(469.12, -19.52) * mm, "end": v(468.75, -19.41) * mm});
            skLineSegment(sketch, "E1648", {"start": v(468.75, -19.41) * mm, "end": v(468.38, -19.28) * mm});
            skLineSegment(sketch, "E1649", {"start": v(468.38, -19.28) * mm, "end": v(468.01, -19.13) * mm});
            skLineSegment(sketch, "E1650", {"start": v(468.01, -19.13) * mm, "end": v(467.66, -18.96) * mm});
            skLineSegment(sketch, "E1651", {"start": v(467.66, -18.96) * mm, "end": v(467.32, -18.77) * mm});
            skLineSegment(sketch, "E1652", {"start": v(467.32, -18.77) * mm, "end": v(466.98, -18.56) * mm});
            skLineSegment(sketch, "E1653", {"start": v(466.98, -18.56) * mm, "end": v(466.66, -18.34) * mm});
            skLineSegment(sketch, "E1654", {"start": v(466.66, -18.34) * mm, "end": v(466.35, -18.09) * mm});
            skLineSegment(sketch, "E1655", {"start": v(466.35, -18.09) * mm, "end": v(466.06, -17.83) * mm});
            skLineSegment(sketch, "E1656", {"start": v(466.06, -17.83) * mm, "end": v(465.78, -17.55) * mm});
            skLineSegment(sketch, "E1657", {"start": v(465.78, -17.55) * mm, "end": v(465.5, -17.25) * mm});
            skLineSegment(sketch, "E1658", {"start": v(465.5, -17.25) * mm, "end": v(465.3, -17) * mm});
            skLineSegment(sketch, "E1659", {"start": v(465.3, -17) * mm, "end": v(465.08, -16.75) * mm});
            skLineSegment(sketch, "E1660", {"start": v(465.08, -16.75) * mm, "end": v(464.88, -16.5) * mm});
            skLineSegment(sketch, "E1661", {"start": v(464.88, -16.5) * mm, "end": v(464.68, -16.24) * mm});
            skLineSegment(sketch, "E1662", {"start": v(464.68, -16.24) * mm, "end": v(464.5, -15.98) * mm});
            skLineSegment(sketch, "E1663", {"start": v(464.5, -15.98) * mm, "end": v(464.3, -15.71) * mm});
            skLineSegment(sketch, "E1664", {"start": v(464.3, -15.71) * mm, "end": v(464.13, -15.44) * mm});
            skLineSegment(sketch, "E1665", {"start": v(464.13, -15.44) * mm, "end": v(463.96, -15.16) * mm});
            skLineSegment(sketch, "E1666", {"start": v(463.96, -15.16) * mm, "end": v(463.8, -14.88) * mm});
            skLineSegment(sketch, "E1667", {"start": v(463.8, -14.88) * mm, "end": v(463.65, -14.6) * mm});
            skLineSegment(sketch, "E1668", {"start": v(463.65, -14.6) * mm, "end": v(463.5, -14.31) * mm});
            skLineSegment(sketch, "E1669", {"start": v(463.5, -14.31) * mm, "end": v(463.36, -14.02) * mm});
            skLineSegment(sketch, "E1670", {"start": v(463.36, -14.02) * mm, "end": v(463.23, -13.73) * mm});
            skLineSegment(sketch, "E1671", {"start": v(463.23, -13.73) * mm, "end": v(463.1, -13.43) * mm});
            skLineSegment(sketch, "E1672", {"start": v(463.1, -13.43) * mm, "end": v(462.98, -13.13) * mm});
            skLineSegment(sketch, "E1673", {"start": v(462.98, -13.13) * mm, "end": v(462.87, -12.83) * mm});
            skLineSegment(sketch, "E1674", {"start": v(462.87, -12.83) * mm, "end": v(462.77, -12.53) * mm});
            skLineSegment(sketch, "E1675", {"start": v(462.77, -12.53) * mm, "end": v(462.67, -12.22) * mm});
            skLineSegment(sketch, "E1676", {"start": v(462.67, -12.22) * mm, "end": v(462.59, -11.9) * mm});
            skLineSegment(sketch, "E1677", {"start": v(462.59, -11.9) * mm, "end": v(462.5, -11.6) * mm});
            skLineSegment(sketch, "E1678", {"start": v(462.5, -11.6) * mm, "end": v(462.43, -11.28) * mm});
            skLineSegment(sketch, "E1679", {"start": v(462.43, -11.28) * mm, "end": v(462.37, -10.97) * mm});
            skLineSegment(sketch, "E1680", {"start": v(462.37, -10.97) * mm, "end": v(462.31, -10.65) * mm});
            skLineSegment(sketch, "E1681", {"start": v(462.31, -10.65) * mm, "end": v(462.27, -10.33) * mm});
            skLineSegment(sketch, "E1682", {"start": v(462.27, -10.33) * mm, "end": v(462.22, -10) * mm});
            skLineSegment(sketch, "E1683", {"start": v(462.22, -10) * mm, "end": v(462.2, -9.68) * mm});
            skLineSegment(sketch, "E1684", {"start": v(462.2, -9.68) * mm, "end": v(462.17, -9.36) * mm});
            skLineSegment(sketch, "E1685", {"start": v(462.17, -9.36) * mm, "end": v(462.15, -9.04) * mm});
            skLineSegment(sketch, "E1686", {"start": v(462.15, -9.04) * mm, "end": v(462.14, -8.71) * mm});
            skLineSegment(sketch, "E1687", {"start": v(462.14, -8.71) * mm, "end": v(462.14, -8.39) * mm});
            skLineSegment(sketch, "E1688", {"start": v(462.14, -8.39) * mm, "end": v(462.15, -8.06) * mm});
            skLineSegment(sketch, "E1689", {"start": v(462.15, -8.06) * mm, "end": v(462.17, -7.73) * mm});
            skLineSegment(sketch, "E1690", {"start": v(462.17, -7.73) * mm, "end": v(462.17, -7.16) * mm});
            skLineSegment(sketch, "E1691", {"start": v(462.17, -7.16) * mm, "end": v(462.2, -6.59) * mm});
            skLineSegment(sketch, "E1692", {"start": v(462.2, -6.59) * mm, "end": v(462.25, -6.02) * mm});
            skLineSegment(sketch, "E1693", {"start": v(462.25, -6.02) * mm, "end": v(462.34, -5.46) * mm});
            skLineSegment(sketch, "E1694", {"start": v(462.34, -5.46) * mm, "end": v(462.44, -4.9) * mm});
            skLineSegment(sketch, "E1695", {"start": v(462.44, -4.9) * mm, "end": v(462.58, -4.35) * mm});
            skLineSegment(sketch, "E1696", {"start": v(462.58, -4.35) * mm, "end": v(462.74, -3.8) * mm});
            skLineSegment(sketch, "E1697", {"start": v(462.74, -3.8) * mm, "end": v(462.93, -3.27) * mm});
            skLineSegment(sketch, "E1698", {"start": v(462.93, -3.27) * mm, "end": v(463.14, -2.74) * mm});
            skLineSegment(sketch, "E1699", {"start": v(463.14, -2.74) * mm, "end": v(463.38, -2.23) * mm});
            skLineSegment(sketch, "E1700", {"start": v(463.38, -2.23) * mm, "end": v(463.64, -1.72) * mm});
            skLineSegment(sketch, "E1701", {"start": v(463.64, -1.72) * mm, "end": v(463.93, -1.23) * mm});
            skLineSegment(sketch, "E1702", {"start": v(463.93, -1.23) * mm, "end": v(464.24, -0.75) * mm});
            skLineSegment(sketch, "E1703", {"start": v(464.24, -0.75) * mm, "end": v(464.58, -0.3) * mm});
            skLineSegment(sketch, "E1704", {"start": v(464.58, -0.3) * mm, "end": v(464.93, 0.16) * mm});
            skLineSegment(sketch, "E1705", {"start": v(464.93, 0.16) * mm, "end": v(465.31, 0.59) * mm});
            skLineSegment(sketch, "E1706", {"start": v(465.31, 0.59) * mm, "end": v(465.6, 0.85) * mm});
            skLineSegment(sketch, "E1707", {"start": v(465.6, 0.85) * mm, "end": v(465.9, 1.1) * mm});
            skLineSegment(sketch, "E1708", {"start": v(465.9, 1.1) * mm, "end": v(466.2, 1.34) * mm});
            skLineSegment(sketch, "E1709", {"start": v(466.2, 1.34) * mm, "end": v(466.5, 1.57) * mm});
            skLineSegment(sketch, "E1710", {"start": v(466.5, 1.57) * mm, "end": v(466.83, 1.78) * mm});
            skLineSegment(sketch, "E1711", {"start": v(466.83, 1.78) * mm, "end": v(467.15, 2) * mm});
            skLineSegment(sketch, "E1712", {"start": v(467.15, 2) * mm, "end": v(467.48, 2.19) * mm});
            skLineSegment(sketch, "E1713", {"start": v(467.48, 2.19) * mm, "end": v(467.82, 2.37) * mm});
            skLineSegment(sketch, "E1714", {"start": v(467.82, 2.37) * mm, "end": v(468.17, 2.54) * mm});
            skLineSegment(sketch, "E1715", {"start": v(468.17, 2.54) * mm, "end": v(468.52, 2.7) * mm});
            skLineSegment(sketch, "E1716", {"start": v(468.52, 2.7) * mm, "end": v(468.87, 2.85) * mm});
            skLineSegment(sketch, "E1717", {"start": v(468.87, 2.85) * mm, "end": v(469.24, 2.98) * mm});
            skLineSegment(sketch, "E1718", {"start": v(469.24, 2.98) * mm, "end": v(469.6, 3.1) * mm});
            skLineSegment(sketch, "E1719", {"start": v(469.6, 3.1) * mm, "end": v(469.97, 3.22) * mm});
            skLineSegment(sketch, "E1720", {"start": v(469.97, 3.22) * mm, "end": v(470.35, 3.31) * mm});
            skLineSegment(sketch, "E1721", {"start": v(470.35, 3.31) * mm, "end": v(470.72, 3.4) * mm});
            skLineSegment(sketch, "E1722", {"start": v(497.84, 11.68) * mm, "end": v(462.88, 11.68) * mm});
            skLineSegment(sketch, "E1723", {"start": v(497.84, 19.38) * mm, "end": v(462.86, 19.38) * mm});
            skLineSegment(sketch, "E1724", {"start": v(462.86, 19.38) * mm, "end": v(462.86, 32.2) * mm});
            skLineSegment(sketch, "E1725", {"start": v(462.86, 32.2) * mm, "end": v(462.88, 32.51) * mm});
            skLineSegment(sketch, "E1726", {"start": v(462.88, 32.51) * mm, "end": v(462.9, 32.81) * mm});
            skLineSegment(sketch, "E1727", {"start": v(462.9, 32.81) * mm, "end": v(462.93, 33.12) * mm});
            skLineSegment(sketch, "E1728", {"start": v(462.93, 33.12) * mm, "end": v(462.97, 33.42) * mm});
            skLineSegment(sketch, "E1729", {"start": v(462.97, 33.42) * mm, "end": v(463.01, 33.72) * mm});
            skLineSegment(sketch, "E1730", {"start": v(463.01, 33.72) * mm, "end": v(463.06, 34.01) * mm});
            skLineSegment(sketch, "E1731", {"start": v(463.06, 34.01) * mm, "end": v(463.12, 34.3) * mm});
            skLineSegment(sketch, "E1732", {"start": v(463.12, 34.3) * mm, "end": v(463.2, 34.6) * mm});
            skLineSegment(sketch, "E1733", {"start": v(463.2, 34.6) * mm, "end": v(463.27, 34.9) * mm});
            skLineSegment(sketch, "E1734", {"start": v(463.27, 34.9) * mm, "end": v(463.35, 35.18) * mm});
            skLineSegment(sketch, "E1735", {"start": v(463.35, 35.18) * mm, "end": v(463.44, 35.47) * mm});
            skLineSegment(sketch, "E1736", {"start": v(463.44, 35.47) * mm, "end": v(463.53, 35.75) * mm});
            skLineSegment(sketch, "E1737", {"start": v(463.53, 35.75) * mm, "end": v(463.75, 36.31) * mm});
            skLineSegment(sketch, "E1738", {"start": v(463.75, 36.31) * mm, "end": v(463.99, 36.86) * mm});
            skLineSegment(sketch, "E1739", {"start": v(463.99, 36.86) * mm, "end": v(464.25, 37.4) * mm});
            skLineSegment(sketch, "E1740", {"start": v(464.25, 37.4) * mm, "end": v(464.55, 37.92) * mm});
            skLineSegment(sketch, "E1741", {"start": v(464.55, 37.92) * mm, "end": v(464.7, 38.18) * mm});
            skLineSegment(sketch, "E1742", {"start": v(464.7, 38.18) * mm, "end": v(464.87, 38.43) * mm});
            skLineSegment(sketch, "E1743", {"start": v(464.87, 38.43) * mm, "end": v(465.04, 38.68) * mm});
            skLineSegment(sketch, "E1744", {"start": v(465.04, 38.68) * mm, "end": v(465.21, 38.92) * mm});
            skLineSegment(sketch, "E1745", {"start": v(465.21, 38.92) * mm, "end": v(465.4, 39.16) * mm});
            skLineSegment(sketch, "E1746", {"start": v(465.4, 39.16) * mm, "end": v(465.58, 39.4) * mm});
            skLineSegment(sketch, "E1747", {"start": v(465.58, 39.4) * mm, "end": v(465.78, 39.62) * mm});
            skLineSegment(sketch, "E1748", {"start": v(465.78, 39.62) * mm, "end": v(465.98, 39.85) * mm});
            skLineSegment(sketch, "E1749", {"start": v(465.98, 39.85) * mm, "end": v(466.19, 40.07) * mm});
            skLineSegment(sketch, "E1750", {"start": v(466.19, 40.07) * mm, "end": v(466.4, 40.29) * mm});
            skLineSegment(sketch, "E1751", {"start": v(466.4, 40.29) * mm, "end": v(466.62, 40.5) * mm});
            skLineSegment(sketch, "E1752", {"start": v(466.62, 40.5) * mm, "end": v(466.84, 40.7) * mm});
            skLineSegment(sketch, "E1753", {"start": v(466.84, 40.7) * mm, "end": v(467.2, 41.05) * mm});
            skLineSegment(sketch, "E1754", {"start": v(467.2, 41.05) * mm, "end": v(467.57, 41.4) * mm});
            skLineSegment(sketch, "E1755", {"start": v(467.57, 41.4) * mm, "end": v(467.95, 41.73) * mm});
            skLineSegment(sketch, "E1756", {"start": v(467.95, 41.73) * mm, "end": v(468.33, 42.05) * mm});
            skLineSegment(sketch, "E1757", {"start": v(468.33, 42.05) * mm, "end": v(468.72, 42.36) * mm});
            skLineSegment(sketch, "E1758", {"start": v(468.72, 42.36) * mm, "end": v(469.12, 42.66) * mm});
            skLineSegment(sketch, "E1759", {"start": v(469.12, 42.66) * mm, "end": v(469.53, 42.94) * mm});
            skLineSegment(sketch, "E1760", {"start": v(469.53, 42.94) * mm, "end": v(469.94, 43.22) * mm});
            skLineSegment(sketch, "E1761", {"start": v(469.94, 43.22) * mm, "end": v(470.36, 43.5) * mm});
            skLineSegment(sketch, "E1762", {"start": v(470.36, 43.5) * mm, "end": v(470.79, 43.75) * mm});
            skLineSegment(sketch, "E1763", {"start": v(470.79, 43.75) * mm, "end": v(471.22, 44) * mm});
            skLineSegment(sketch, "E1764", {"start": v(471.22, 44) * mm, "end": v(471.65, 44.23) * mm});
            skLineSegment(sketch, "E1765", {"start": v(471.65, 44.23) * mm, "end": v(472.1, 44.45) * mm});
            skLineSegment(sketch, "E1766", {"start": v(472.1, 44.45) * mm, "end": v(472.54, 44.67) * mm});
            skLineSegment(sketch, "E1767", {"start": v(472.54, 44.67) * mm, "end": v(473, 44.87) * mm});
            skLineSegment(sketch, "E1768", {"start": v(473, 44.87) * mm, "end": v(473.45, 45.06) * mm});
            skLineSegment(sketch, "E1769", {"start": v(473.45, 45.06) * mm, "end": v(473.91, 45.24) * mm});
            skLineSegment(sketch, "E1770", {"start": v(473.91, 45.24) * mm, "end": v(474.38, 45.4) * mm});
            skLineSegment(sketch, "E1771", {"start": v(474.38, 45.4) * mm, "end": v(474.85, 45.56) * mm});
            skLineSegment(sketch, "E1772", {"start": v(474.85, 45.56) * mm, "end": v(475.33, 45.7) * mm});
            skLineSegment(sketch, "E1773", {"start": v(475.33, 45.7) * mm, "end": v(475.8, 45.84) * mm});
            skLineSegment(sketch, "E1774", {"start": v(475.8, 45.84) * mm, "end": v(476.29, 45.96) * mm});
            skLineSegment(sketch, "E1775", {"start": v(476.29, 45.96) * mm, "end": v(476.77, 46.07) * mm});
            skLineSegment(sketch, "E1776", {"start": v(476.77, 46.07) * mm, "end": v(477.26, 46.17) * mm});
            skLineSegment(sketch, "E1777", {"start": v(477.26, 46.17) * mm, "end": v(477.75, 46.25) * mm});
            skLineSegment(sketch, "E1778", {"start": v(477.75, 46.25) * mm, "end": v(478.24, 46.32) * mm});
            skLineSegment(sketch, "E1779", {"start": v(478.24, 46.32) * mm, "end": v(478.74, 46.38) * mm});
            skLineSegment(sketch, "E1780", {"start": v(478.74, 46.38) * mm, "end": v(479.23, 46.43) * mm});
            skLineSegment(sketch, "E1781", {"start": v(479.23, 46.43) * mm, "end": v(479.73, 46.46) * mm});
            skLineSegment(sketch, "E1782", {"start": v(479.73, 46.46) * mm, "end": v(480.23, 46.49) * mm});
            skLineSegment(sketch, "E1783", {"start": v(480.23, 46.49) * mm, "end": v(480.74, 46.5) * mm});
            skLineSegment(sketch, "E1784", {"start": v(480.74, 46.5) * mm, "end": v(481.24, 46.5) * mm});
            skLineSegment(sketch, "E1785", {"start": v(481.24, 46.5) * mm, "end": v(481.66, 46.5) * mm});
            skLineSegment(sketch, "E1786", {"start": v(481.66, 46.5) * mm, "end": v(482.08, 46.5) * mm});
            skLineSegment(sketch, "E1787", {"start": v(482.08, 46.5) * mm, "end": v(482.5, 46.5) * mm});
            skLineSegment(sketch, "E1788", {"start": v(482.5, 46.5) * mm, "end": v(482.92, 46.47) * mm});
            skLineSegment(sketch, "E1789", {"start": v(482.92, 46.47) * mm, "end": v(483.34, 46.44) * mm});
            skLineSegment(sketch, "E1790", {"start": v(483.34, 46.44) * mm, "end": v(483.76, 46.4) * mm});
            skLineSegment(sketch, "E1791", {"start": v(483.76, 46.4) * mm, "end": v(484.17, 46.34) * mm});
            skLineSegment(sketch, "E1792", {"start": v(484.17, 46.34) * mm, "end": v(484.58, 46.28) * mm});
            skLineSegment(sketch, "E1793", {"start": v(484.58, 46.28) * mm, "end": v(485, 46.21) * mm});
            skLineSegment(sketch, "E1794", {"start": v(485, 46.21) * mm, "end": v(485.4, 46.13) * mm});
            skLineSegment(sketch, "E1795", {"start": v(485.4, 46.13) * mm, "end": v(485.8, 46.04) * mm});
            skLineSegment(sketch, "E1796", {"start": v(485.8, 46.04) * mm, "end": v(486.21, 45.93) * mm});
            skLineSegment(sketch, "E1797", {"start": v(486.21, 45.93) * mm, "end": v(486.61, 45.82) * mm});
            skLineSegment(sketch, "E1798", {"start": v(486.61, 45.82) * mm, "end": v(487.01, 45.7) * mm});
            skLineSegment(sketch, "E1799", {"start": v(487.01, 45.7) * mm, "end": v(487.4, 45.57) * mm});
            skLineSegment(sketch, "E1800", {"start": v(487.4, 45.57) * mm, "end": v(487.8, 45.43) * mm});
            skLineSegment(sketch, "E1801", {"start": v(487.8, 45.43) * mm, "end": v(488.18, 45.28) * mm});
            skLineSegment(sketch, "E1802", {"start": v(488.18, 45.28) * mm, "end": v(488.57, 45.12) * mm});
            skLineSegment(sketch, "E1803", {"start": v(488.57, 45.12) * mm, "end": v(488.95, 44.95) * mm});
            skLineSegment(sketch, "E1804", {"start": v(488.95, 44.95) * mm, "end": v(489.32, 44.77) * mm});
            skLineSegment(sketch, "E1805", {"start": v(489.32, 44.77) * mm, "end": v(489.7, 44.58) * mm});
            skLineSegment(sketch, "E1806", {"start": v(489.7, 44.58) * mm, "end": v(490.06, 44.39) * mm});
            skLineSegment(sketch, "E1807", {"start": v(490.06, 44.39) * mm, "end": v(490.42, 44.18) * mm});
            skLineSegment(sketch, "E1808", {"start": v(490.42, 44.18) * mm, "end": v(490.78, 43.97) * mm});
            skLineSegment(sketch, "E1809", {"start": v(490.78, 43.97) * mm, "end": v(491.13, 43.74) * mm});
            skLineSegment(sketch, "E1810", {"start": v(491.13, 43.74) * mm, "end": v(491.48, 43.51) * mm});
            skLineSegment(sketch, "E1811", {"start": v(491.48, 43.51) * mm, "end": v(491.82, 43.27) * mm});
            skLineSegment(sketch, "E1812", {"start": v(491.82, 43.27) * mm, "end": v(492.16, 43.02) * mm});
            skLineSegment(sketch, "E1813", {"start": v(492.16, 43.02) * mm, "end": v(492.49, 42.76) * mm});
            skLineSegment(sketch, "E1814", {"start": v(492.49, 42.76) * mm, "end": v(492.81, 42.5) * mm});
            skLineSegment(sketch, "E1815", {"start": v(492.81, 42.5) * mm, "end": v(493.13, 42.22) * mm});
            skLineSegment(sketch, "E1816", {"start": v(493.13, 42.22) * mm, "end": v(493.44, 41.93) * mm});
            skLineSegment(sketch, "E1817", {"start": v(493.44, 41.93) * mm, "end": v(493.7, 41.7) * mm});
            skLineSegment(sketch, "E1818", {"start": v(493.7, 41.7) * mm, "end": v(493.93, 41.45) * mm});
            skLineSegment(sketch, "E1819", {"start": v(493.93, 41.45) * mm, "end": v(494.17, 41.2) * mm});
            skLineSegment(sketch, "E1820", {"start": v(494.17, 41.2) * mm, "end": v(494.4, 40.94) * mm});
            skLineSegment(sketch, "E1821", {"start": v(494.4, 40.94) * mm, "end": v(494.62, 40.68) * mm});
            skLineSegment(sketch, "E1822", {"start": v(494.62, 40.68) * mm, "end": v(494.84, 40.41) * mm});
            skLineSegment(sketch, "E1823", {"start": v(494.84, 40.41) * mm, "end": v(495.05, 40.14) * mm});
            skLineSegment(sketch, "E1824", {"start": v(495.05, 40.14) * mm, "end": v(495.25, 39.87) * mm});
            skLineSegment(sketch, "E1825", {"start": v(495.25, 39.87) * mm, "end": v(495.44, 39.59) * mm});
            skLineSegment(sketch, "E1826", {"start": v(495.44, 39.59) * mm, "end": v(495.63, 39.3) * mm});
            skLineSegment(sketch, "E1827", {"start": v(495.63, 39.3) * mm, "end": v(495.81, 39.01) * mm});
            skLineSegment(sketch, "E1828", {"start": v(495.81, 39.01) * mm, "end": v(495.98, 38.72) * mm});
            skLineSegment(sketch, "E1829", {"start": v(495.98, 38.72) * mm, "end": v(496.15, 38.42) * mm});
            skLineSegment(sketch, "E1830", {"start": v(496.15, 38.42) * mm, "end": v(496.3, 38.12) * mm});
            skLineSegment(sketch, "E1831", {"start": v(496.3, 38.12) * mm, "end": v(496.46, 37.81) * mm});
            skLineSegment(sketch, "E1832", {"start": v(496.46, 37.81) * mm, "end": v(496.6, 37.5) * mm});
            skLineSegment(sketch, "E1833", {"start": v(496.6, 37.5) * mm, "end": v(496.74, 37.2) * mm});
            skLineSegment(sketch, "E1834", {"start": v(496.74, 37.2) * mm, "end": v(496.87, 36.88) * mm});
            skLineSegment(sketch, "E1835", {"start": v(496.87, 36.88) * mm, "end": v(497, 36.56) * mm});
            skLineSegment(sketch, "E1836", {"start": v(497, 36.56) * mm, "end": v(497.1, 36.24) * mm});
            skLineSegment(sketch, "E1837", {"start": v(497.1, 36.24) * mm, "end": v(497.21, 35.92) * mm});
            skLineSegment(sketch, "E1838", {"start": v(497.21, 35.92) * mm, "end": v(497.3, 35.59) * mm});
            skLineSegment(sketch, "E1839", {"start": v(497.3, 35.59) * mm, "end": v(497.4, 35.26) * mm});
            skLineSegment(sketch, "E1840", {"start": v(497.4, 35.26) * mm, "end": v(497.48, 34.93) * mm});
            skLineSegment(sketch, "E1841", {"start": v(497.48, 34.93) * mm, "end": v(497.56, 34.6) * mm});
            skLineSegment(sketch, "E1842", {"start": v(497.56, 34.6) * mm, "end": v(497.62, 34.26) * mm});
            skLineSegment(sketch, "E1843", {"start": v(497.62, 34.26) * mm, "end": v(497.68, 33.92) * mm});
            skLineSegment(sketch, "E1844", {"start": v(497.68, 33.92) * mm, "end": v(497.73, 33.58) * mm});
            skLineSegment(sketch, "E1845", {"start": v(497.73, 33.58) * mm, "end": v(497.77, 33.24) * mm});
            skLineSegment(sketch, "E1846", {"start": v(497.77, 33.24) * mm, "end": v(497.8, 32.9) * mm});
            skLineSegment(sketch, "E1847", {"start": v(497.8, 32.9) * mm, "end": v(497.83, 32.55) * mm});
            skLineSegment(sketch, "E1848", {"start": v(497.83, 32.55) * mm, "end": v(497.84, 32.2) * mm});
            skLineSegment(sketch, "E1849", {"start": v(497.84, 32.2) * mm, "end": v(497.84, 19.38) * mm});
            skLineSegment(sketch, "E1850", {"start": v(497.84, 77.42) * mm, "end": v(497.84, 54.39) * mm});
            skLineSegment(sketch, "E1851", {"start": v(497.84, 54.39) * mm, "end": v(462.88, 54.39) * mm});
            skLineSegment(sketch, "E1852", {"start": v(462.88, 54.39) * mm, "end": v(462.88, 77.42) * mm});
            skLineSegment(sketch, "E1853", {"start": v(479.72, 54.39) * mm, "end": v(479.72, 74.53) * mm});
            skLineSegment(sketch, "E1854", {"start": v(484.77, 85.12) * mm, "end": v(484.77, 109.24) * mm});
            skLineSegment(sketch, "E1855", {"start": v(498.27, 128.5) * mm, "end": v(498.27, 128) * mm});
            skLineSegment(sketch, "E1856", {"start": v(498.27, 128) * mm, "end": v(498.24, 127.48) * mm});
            skLineSegment(sketch, "E1857", {"start": v(498.24, 127.48) * mm, "end": v(498.2, 126.97) * mm});
            skLineSegment(sketch, "E1858", {"start": v(498.2, 126.97) * mm, "end": v(498.12, 126.47) * mm});
            skLineSegment(sketch, "E1859", {"start": v(498.12, 126.47) * mm, "end": v(498.01, 125.97) * mm});
            skLineSegment(sketch, "E1860", {"start": v(498.01, 125.97) * mm, "end": v(497.88, 125.48) * mm});
            skLineSegment(sketch, "E1861", {"start": v(497.88, 125.48) * mm, "end": v(497.73, 125) * mm});
            skLineSegment(sketch, "E1862", {"start": v(497.73, 125) * mm, "end": v(497.56, 124.52) * mm});
            skLineSegment(sketch, "E1863", {"start": v(497.56, 124.52) * mm, "end": v(497.35, 124.05) * mm});
            skLineSegment(sketch, "E1864", {"start": v(497.35, 124.05) * mm, "end": v(497.13, 123.6) * mm});
            skLineSegment(sketch, "E1865", {"start": v(497.13, 123.6) * mm, "end": v(496.88, 123.15) * mm});
            skLineSegment(sketch, "E1866", {"start": v(496.88, 123.15) * mm, "end": v(496.61, 122.72) * mm});
            skLineSegment(sketch, "E1867", {"start": v(496.61, 122.72) * mm, "end": v(496.32, 122.3) * mm});
            skLineSegment(sketch, "E1868", {"start": v(496.32, 122.3) * mm, "end": v(496, 121.9) * mm});
            skLineSegment(sketch, "E1869", {"start": v(496, 121.9) * mm, "end": v(495.67, 121.51) * mm});
            skLineSegment(sketch, "E1870", {"start": v(495.67, 121.51) * mm, "end": v(495.32, 121.14) * mm});
            skLineSegment(sketch, "E1871", {"start": v(495.32, 121.14) * mm, "end": v(495.06, 120.88) * mm});
            skLineSegment(sketch, "E1872", {"start": v(495.06, 120.88) * mm, "end": v(494.8, 120.63) * mm});
            skLineSegment(sketch, "E1873", {"start": v(494.8, 120.63) * mm, "end": v(494.53, 120.39) * mm});
            skLineSegment(sketch, "E1874", {"start": v(494.53, 120.39) * mm, "end": v(494.26, 120.15) * mm});
            skLineSegment(sketch, "E1875", {"start": v(494.26, 120.15) * mm, "end": v(493.98, 119.92) * mm});
            skLineSegment(sketch, "E1876", {"start": v(493.98, 119.92) * mm, "end": v(493.7, 119.7) * mm});
            skLineSegment(sketch, "E1877", {"start": v(493.7, 119.7) * mm, "end": v(493.4, 119.5) * mm});
            skLineSegment(sketch, "E1878", {"start": v(493.4, 119.5) * mm, "end": v(493.1, 119.29) * mm});
            skLineSegment(sketch, "E1879", {"start": v(493.1, 119.29) * mm, "end": v(492.8, 119.09) * mm});
            skLineSegment(sketch, "E1880", {"start": v(492.8, 119.09) * mm, "end": v(492.5, 118.9) * mm});
            skLineSegment(sketch, "E1881", {"start": v(492.5, 118.9) * mm, "end": v(492.2, 118.72) * mm});
            skLineSegment(sketch, "E1882", {"start": v(492.2, 118.72) * mm, "end": v(491.88, 118.55) * mm});
            skLineSegment(sketch, "E1883", {"start": v(491.88, 118.55) * mm, "end": v(491.56, 118.39) * mm});
            skLineSegment(sketch, "E1884", {"start": v(491.56, 118.39) * mm, "end": v(491.24, 118.23) * mm});
            skLineSegment(sketch, "E1885", {"start": v(491.24, 118.23) * mm, "end": v(490.9, 118.08) * mm});
            skLineSegment(sketch, "E1886", {"start": v(490.9, 118.08) * mm, "end": v(490.58, 117.94) * mm});
            skLineSegment(sketch, "E1887", {"start": v(490.58, 117.94) * mm, "end": v(490.25, 117.81) * mm});
            skLineSegment(sketch, "E1888", {"start": v(490.25, 117.81) * mm, "end": v(489.91, 117.7) * mm});
            skLineSegment(sketch, "E1889", {"start": v(489.91, 117.7) * mm, "end": v(489.57, 117.58) * mm});
            skLineSegment(sketch, "E1890", {"start": v(489.57, 117.58) * mm, "end": v(489.23, 117.48) * mm});
            skLineSegment(sketch, "E1891", {"start": v(489.23, 117.48) * mm, "end": v(488.88, 117.38) * mm});
            skLineSegment(sketch, "E1892", {"start": v(488.88, 117.38) * mm, "end": v(488.54, 117.3) * mm});
            skLineSegment(sketch, "E1893", {"start": v(488.54, 117.3) * mm, "end": v(488.18, 117.22) * mm});
            skLineSegment(sketch, "E1894", {"start": v(488.18, 117.22) * mm, "end": v(487.83, 117.15) * mm});
            skLineSegment(sketch, "E1895", {"start": v(487.83, 117.15) * mm, "end": v(487.48, 117.1) * mm});
            skLineSegment(sketch, "E1896", {"start": v(487.48, 117.1) * mm, "end": v(487.12, 117.04) * mm});
            skLineSegment(sketch, "E1897", {"start": v(487.12, 117.04) * mm, "end": v(486.76, 117) * mm});
            skLineSegment(sketch, "E1898", {"start": v(486.76, 117) * mm, "end": v(486.4, 116.97) * mm});
            skLineSegment(sketch, "E1899", {"start": v(486.4, 116.97) * mm, "end": v(486.04, 116.95) * mm});
            skLineSegment(sketch, "E1900", {"start": v(486.04, 116.95) * mm, "end": v(485.68, 116.94) * mm});
            skLineSegment(sketch, "E1901", {"start": v(485.68, 116.94) * mm, "end": v(485.32, 116.94) * mm});
            skLineSegment(sketch, "E1902", {"start": v(485.32, 116.94) * mm, "end": v(484.96, 116.94) * mm});
            skLineSegment(sketch, "E1903", {"start": v(484.96, 116.94) * mm, "end": v(484.6, 116.93) * mm});
            skLineSegment(sketch, "E1904", {"start": v(484.6, 116.93) * mm, "end": v(484.23, 116.92) * mm});
            skLineSegment(sketch, "E1905", {"start": v(484.23, 116.92) * mm, "end": v(483.87, 116.93) * mm});
            skLineSegment(sketch, "E1906", {"start": v(483.87, 116.93) * mm, "end": v(483.51, 116.94) * mm});
            skLineSegment(sketch, "E1907", {"start": v(483.51, 116.94) * mm, "end": v(483.15, 116.96) * mm});
            skLineSegment(sketch, "E1908", {"start": v(483.15, 116.96) * mm, "end": v(482.8, 117) * mm});
            skLineSegment(sketch, "E1909", {"start": v(482.8, 117) * mm, "end": v(482.44, 117.03) * mm});
            skLineSegment(sketch, "E1910", {"start": v(482.44, 117.03) * mm, "end": v(482.08, 117.08) * mm});
            skLineSegment(sketch, "E1911", {"start": v(482.08, 117.08) * mm, "end": v(481.73, 117.14) * mm});
            skLineSegment(sketch, "E1912", {"start": v(481.73, 117.14) * mm, "end": v(481.38, 117.2) * mm});
            skLineSegment(sketch, "E1913", {"start": v(481.38, 117.2) * mm, "end": v(481.03, 117.28) * mm});
            skLineSegment(sketch, "E1914", {"start": v(481.03, 117.28) * mm, "end": v(480.68, 117.36) * mm});
            skLineSegment(sketch, "E1915", {"start": v(480.68, 117.36) * mm, "end": v(480.33, 117.45) * mm});
            skLineSegment(sketch, "E1916", {"start": v(480.33, 117.45) * mm, "end": v(479.99, 117.55) * mm});
            skLineSegment(sketch, "E1917", {"start": v(479.99, 117.55) * mm, "end": v(479.65, 117.66) * mm});
            skLineSegment(sketch, "E1918", {"start": v(479.65, 117.66) * mm, "end": v(479.3, 117.77) * mm});
            skLineSegment(sketch, "E1919", {"start": v(479.3, 117.77) * mm, "end": v(478.97, 117.9) * mm});
            skLineSegment(sketch, "E1920", {"start": v(478.97, 117.9) * mm, "end": v(478.64, 118.03) * mm});
            skLineSegment(sketch, "E1921", {"start": v(478.64, 118.03) * mm, "end": v(478.31, 118.17) * mm});
            skLineSegment(sketch, "E1922", {"start": v(478.31, 118.17) * mm, "end": v(477.99, 118.31) * mm});
            skLineSegment(sketch, "E1923", {"start": v(477.99, 118.31) * mm, "end": v(477.67, 118.47) * mm});
            skLineSegment(sketch, "E1924", {"start": v(477.67, 118.47) * mm, "end": v(477.35, 118.63) * mm});
            skLineSegment(sketch, "E1925", {"start": v(477.35, 118.63) * mm, "end": v(477.03, 118.8) * mm});
            skLineSegment(sketch, "E1926", {"start": v(477.03, 118.8) * mm, "end": v(476.72, 118.98) * mm});
            skLineSegment(sketch, "E1927", {"start": v(476.72, 118.98) * mm, "end": v(476.42, 119.17) * mm});
            skLineSegment(sketch, "E1928", {"start": v(476.42, 119.17) * mm, "end": v(476.12, 119.37) * mm});
            skLineSegment(sketch, "E1929", {"start": v(476.12, 119.37) * mm, "end": v(475.82, 119.57) * mm});
            skLineSegment(sketch, "E1930", {"start": v(475.82, 119.57) * mm, "end": v(475.53, 119.78) * mm});
            skLineSegment(sketch, "E1931", {"start": v(475.53, 119.78) * mm, "end": v(475.24, 120) * mm});
            skLineSegment(sketch, "E1932", {"start": v(475.24, 120) * mm, "end": v(474.96, 120.22) * mm});
            skLineSegment(sketch, "E1933", {"start": v(474.96, 120.22) * mm, "end": v(474.68, 120.45) * mm});
            skLineSegment(sketch, "E1934", {"start": v(474.68, 120.45) * mm, "end": v(474.4, 120.69) * mm});
            skLineSegment(sketch, "E1935", {"start": v(474.4, 120.69) * mm, "end": v(474.04, 121.1) * mm});
            skLineSegment(sketch, "E1936", {"start": v(474.04, 121.1) * mm, "end": v(473.7, 121.51) * mm});
            skLineSegment(sketch, "E1937", {"start": v(473.7, 121.51) * mm, "end": v(473.38, 121.94) * mm});
            skLineSegment(sketch, "E1938", {"start": v(473.38, 121.94) * mm, "end": v(473.08, 122.4) * mm});
            skLineSegment(sketch, "E1939", {"start": v(473.08, 122.4) * mm, "end": v(472.8, 122.85) * mm});
            skLineSegment(sketch, "E1940", {"start": v(472.8, 122.85) * mm, "end": v(472.54, 123.32) * mm});
            skLineSegment(sketch, "E1941", {"start": v(472.54, 123.32) * mm, "end": v(472.31, 123.8) * mm});
            skLineSegment(sketch, "E1942", {"start": v(472.31, 123.8) * mm, "end": v(472.1, 124.3) * mm});
            skLineSegment(sketch, "E1943", {"start": v(472.1, 124.3) * mm, "end": v(471.91, 124.8) * mm});
            skLineSegment(sketch, "E1944", {"start": v(471.91, 124.8) * mm, "end": v(471.75, 125.31) * mm});
            skLineSegment(sketch, "E1945", {"start": v(471.75, 125.31) * mm, "end": v(471.61, 125.83) * mm});
            skLineSegment(sketch, "E1946", {"start": v(471.61, 125.83) * mm, "end": v(471.5, 126.36) * mm});
            skLineSegment(sketch, "E1947", {"start": v(471.5, 126.36) * mm, "end": v(471.41, 126.89) * mm});
            skLineSegment(sketch, "E1948", {"start": v(471.41, 126.89) * mm, "end": v(471.35, 127.43) * mm});
            skLineSegment(sketch, "E1949", {"start": v(471.35, 127.43) * mm, "end": v(471.3, 127.97) * mm});
            skLineSegment(sketch, "E1950", {"start": v(471.3, 127.97) * mm, "end": v(471.3, 128.5) * mm});
            skLineSegment(sketch, "E1951", {"start": v(471.3, 128.5) * mm, "end": v(471.32, 129.03) * mm});
            skLineSegment(sketch, "E1952", {"start": v(471.32, 129.03) * mm, "end": v(471.37, 129.56) * mm});
            skLineSegment(sketch, "E1953", {"start": v(471.37, 129.56) * mm, "end": v(471.45, 130.07) * mm});
            skLineSegment(sketch, "E1954", {"start": v(471.45, 130.07) * mm, "end": v(471.56, 130.58) * mm});
            skLineSegment(sketch, "E1955", {"start": v(471.56, 130.58) * mm, "end": v(471.7, 131.09) * mm});
            skLineSegment(sketch, "E1956", {"start": v(471.7, 131.09) * mm, "end": v(471.85, 131.58) * mm});
            skLineSegment(sketch, "E1957", {"start": v(471.85, 131.58) * mm, "end": v(472.04, 132.06) * mm});
            skLineSegment(sketch, "E1958", {"start": v(472.04, 132.06) * mm, "end": v(472.25, 132.54) * mm});
            skLineSegment(sketch, "E1959", {"start": v(472.25, 132.54) * mm, "end": v(472.48, 133) * mm});
            skLineSegment(sketch, "E1960", {"start": v(472.48, 133) * mm, "end": v(472.74, 133.45) * mm});
            skLineSegment(sketch, "E1961", {"start": v(472.74, 133.45) * mm, "end": v(473.02, 133.89) * mm});
            skLineSegment(sketch, "E1962", {"start": v(473.02, 133.89) * mm, "end": v(473.32, 134.3) * mm});
            skLineSegment(sketch, "E1963", {"start": v(473.32, 134.3) * mm, "end": v(473.65, 134.72) * mm});
            skLineSegment(sketch, "E1964", {"start": v(473.65, 134.72) * mm, "end": v(474, 135.1) * mm});
            skLineSegment(sketch, "E1965", {"start": v(474, 135.1) * mm, "end": v(474.37, 135.48) * mm});
            skLineSegment(sketch, "E1966", {"start": v(474.37, 135.48) * mm, "end": v(474.76, 135.83) * mm});
            skLineSegment(sketch, "E1967", {"start": v(474.76, 135.83) * mm, "end": v(475.02, 136.07) * mm});
            skLineSegment(sketch, "E1968", {"start": v(475.02, 136.07) * mm, "end": v(475.28, 136.3) * mm});
            skLineSegment(sketch, "E1969", {"start": v(475.28, 136.3) * mm, "end": v(475.55, 136.53) * mm});
            skLineSegment(sketch, "E1970", {"start": v(475.55, 136.53) * mm, "end": v(475.82, 136.75) * mm});
            skLineSegment(sketch, "E1971", {"start": v(475.82, 136.75) * mm, "end": v(476.1, 136.96) * mm});
            skLineSegment(sketch, "E1972", {"start": v(476.1, 136.96) * mm, "end": v(476.39, 137.16) * mm});
            skLineSegment(sketch, "E1973", {"start": v(476.39, 137.16) * mm, "end": v(476.68, 137.36) * mm});
            skLineSegment(sketch, "E1974", {"start": v(476.68, 137.36) * mm, "end": v(476.97, 137.54) * mm});
            skLineSegment(sketch, "E1975", {"start": v(476.97, 137.54) * mm, "end": v(477.27, 137.72) * mm});
            skLineSegment(sketch, "E1976", {"start": v(477.27, 137.72) * mm, "end": v(477.57, 137.9) * mm});
            skLineSegment(sketch, "E1977", {"start": v(477.57, 137.9) * mm, "end": v(477.88, 138.06) * mm});
            skLineSegment(sketch, "E1978", {"start": v(477.88, 138.06) * mm, "end": v(478.2, 138.21) * mm});
            skLineSegment(sketch, "E1979", {"start": v(478.2, 138.21) * mm, "end": v(478.5, 138.36) * mm});
            skLineSegment(sketch, "E1980", {"start": v(478.5, 138.36) * mm, "end": v(478.82, 138.5) * mm});
            skLineSegment(sketch, "E1981", {"start": v(478.82, 138.5) * mm, "end": v(479.14, 138.63) * mm});
            skLineSegment(sketch, "E1982", {"start": v(479.14, 138.63) * mm, "end": v(479.47, 138.75) * mm});
            skLineSegment(sketch, "E1983", {"start": v(479.47, 138.75) * mm, "end": v(479.8, 138.87) * mm});
            skLineSegment(sketch, "E1984", {"start": v(479.8, 138.87) * mm, "end": v(480.13, 138.97) * mm});
            skLineSegment(sketch, "E1985", {"start": v(480.13, 138.97) * mm, "end": v(480.46, 139.07) * mm});
            skLineSegment(sketch, "E1986", {"start": v(480.46, 139.07) * mm, "end": v(480.8, 139.16) * mm});
            skLineSegment(sketch, "E1987", {"start": v(480.8, 139.16) * mm, "end": v(481.13, 139.24) * mm});
            skLineSegment(sketch, "E1988", {"start": v(481.13, 139.24) * mm, "end": v(481.47, 139.31) * mm});
            skLineSegment(sketch, "E1989", {"start": v(481.47, 139.31) * mm, "end": v(481.81, 139.38) * mm});
            skLineSegment(sketch, "E1990", {"start": v(481.81, 139.38) * mm, "end": v(482.16, 139.43) * mm});
            skLineSegment(sketch, "E1991", {"start": v(482.16, 139.43) * mm, "end": v(482.5, 139.48) * mm});
            skLineSegment(sketch, "E1992", {"start": v(482.5, 139.48) * mm, "end": v(482.85, 139.51) * mm});
            skLineSegment(sketch, "E1993", {"start": v(482.85, 139.51) * mm, "end": v(483.2, 139.54) * mm});
            skLineSegment(sketch, "E1994", {"start": v(483.2, 139.54) * mm, "end": v(483.55, 139.56) * mm});
            skLineSegment(sketch, "E1995", {"start": v(483.55, 139.56) * mm, "end": v(483.9, 139.57) * mm});
            skLineSegment(sketch, "E1996", {"start": v(483.9, 139.57) * mm, "end": v(484.25, 139.57) * mm});
            skLineSegment(sketch, "E1997", {"start": v(484.25, 139.57) * mm, "end": v(484.6, 139.56) * mm});
            skLineSegment(sketch, "E1998", {"start": v(484.6, 139.56) * mm, "end": v(484.96, 139.54) * mm});
            skLineSegment(sketch, "E1999", {"start": v(484.96, 139.54) * mm, "end": v(485.3, 139.56) * mm});
            skLineSegment(sketch, "E2000", {"start": v(485.3, 139.56) * mm, "end": v(485.65, 139.56) * mm});
            skLineSegment(sketch, "E2001", {"start": v(485.65, 139.56) * mm, "end": v(486, 139.55) * mm});
            skLineSegment(sketch, "E2002", {"start": v(486, 139.55) * mm, "end": v(486.35, 139.54) * mm});
            skLineSegment(sketch, "E2003", {"start": v(486.35, 139.54) * mm, "end": v(486.7, 139.51) * mm});
            skLineSegment(sketch, "E2004", {"start": v(486.7, 139.51) * mm, "end": v(487.04, 139.48) * mm});
            skLineSegment(sketch, "E2005", {"start": v(487.04, 139.48) * mm, "end": v(487.39, 139.44) * mm});
            skLineSegment(sketch, "E2006", {"start": v(487.39, 139.44) * mm, "end": v(487.73, 139.4) * mm});
            skLineSegment(sketch, "E2007", {"start": v(487.73, 139.4) * mm, "end": v(488.07, 139.33) * mm});
            skLineSegment(sketch, "E2008", {"start": v(488.07, 139.33) * mm, "end": v(488.4, 139.27) * mm});
            skLineSegment(sketch, "E2009", {"start": v(488.4, 139.27) * mm, "end": v(488.75, 139.2) * mm});
            skLineSegment(sketch, "E2010", {"start": v(488.75, 139.2) * mm, "end": v(489.08, 139.1) * mm});
            skLineSegment(sketch, "E2011", {"start": v(489.08, 139.1) * mm, "end": v(489.41, 139.02) * mm});
            skLineSegment(sketch, "E2012", {"start": v(489.41, 139.02) * mm, "end": v(489.74, 138.92) * mm});
            skLineSegment(sketch, "E2013", {"start": v(489.74, 138.92) * mm, "end": v(490.07, 138.8) * mm});
            skLineSegment(sketch, "E2014", {"start": v(490.07, 138.8) * mm, "end": v(490.4, 138.7) * mm});
            skLineSegment(sketch, "E2015", {"start": v(490.4, 138.7) * mm, "end": v(490.71, 138.57) * mm});
            skLineSegment(sketch, "E2016", {"start": v(490.71, 138.57) * mm, "end": v(491.03, 138.44) * mm});
            skLineSegment(sketch, "E2017", {"start": v(491.03, 138.44) * mm, "end": v(491.35, 138.3) * mm});
            skLineSegment(sketch, "E2018", {"start": v(491.35, 138.3) * mm, "end": v(491.66, 138.15) * mm});
            skLineSegment(sketch, "E2019", {"start": v(491.66, 138.15) * mm, "end": v(491.97, 138) * mm});
            skLineSegment(sketch, "E2020", {"start": v(491.97, 138) * mm, "end": v(492.27, 137.83) * mm});
            skLineSegment(sketch, "E2021", {"start": v(492.27, 137.83) * mm, "end": v(492.57, 137.66) * mm});
            skLineSegment(sketch, "E2022", {"start": v(492.57, 137.66) * mm, "end": v(492.87, 137.48) * mm});
            skLineSegment(sketch, "E2023", {"start": v(492.87, 137.48) * mm, "end": v(493.16, 137.3) * mm});
            skLineSegment(sketch, "E2024", {"start": v(493.16, 137.3) * mm, "end": v(493.45, 137.1) * mm});
            skLineSegment(sketch, "E2025", {"start": v(493.45, 137.1) * mm, "end": v(493.73, 136.9) * mm});
            skLineSegment(sketch, "E2026", {"start": v(493.73, 136.9) * mm, "end": v(494, 136.69) * mm});
            skLineSegment(sketch, "E2027", {"start": v(494, 136.69) * mm, "end": v(494.28, 136.47) * mm});
            skLineSegment(sketch, "E2028", {"start": v(494.28, 136.47) * mm, "end": v(494.55, 136.25) * mm});
            skLineSegment(sketch, "E2029", {"start": v(494.55, 136.25) * mm, "end": v(494.8, 136.02) * mm});
            skLineSegment(sketch, "E2030", {"start": v(494.8, 136.02) * mm, "end": v(495.07, 135.78) * mm});
            skLineSegment(sketch, "E2031", {"start": v(495.07, 135.78) * mm, "end": v(495.43, 135.42) * mm});
            skLineSegment(sketch, "E2032", {"start": v(495.43, 135.42) * mm, "end": v(495.78, 135.04) * mm});
            skLineSegment(sketch, "E2033", {"start": v(495.78, 135.04) * mm, "end": v(496.1, 134.65) * mm});
            skLineSegment(sketch, "E2034", {"start": v(496.1, 134.65) * mm, "end": v(496.41, 134.24) * mm});
            skLineSegment(sketch, "E2035", {"start": v(496.41, 134.24) * mm, "end": v(496.7, 133.82) * mm});
            skLineSegment(sketch, "E2036", {"start": v(496.7, 133.82) * mm, "end": v(496.96, 133.38) * mm});
            skLineSegment(sketch, "E2037", {"start": v(496.96, 133.38) * mm, "end": v(497.2, 132.93) * mm});
            skLineSegment(sketch, "E2038", {"start": v(497.2, 132.93) * mm, "end": v(497.42, 132.48) * mm});
            skLineSegment(sketch, "E2039", {"start": v(497.42, 132.48) * mm, "end": v(497.6, 132) * mm});
            skLineSegment(sketch, "E2040", {"start": v(497.6, 132) * mm, "end": v(497.78, 131.53) * mm});
            skLineSegment(sketch, "E2041", {"start": v(497.78, 131.53) * mm, "end": v(497.92, 131.04) * mm});
            skLineSegment(sketch, "E2042", {"start": v(497.92, 131.04) * mm, "end": v(498.04, 130.54) * mm});
            skLineSegment(sketch, "E2043", {"start": v(498.04, 130.54) * mm, "end": v(498.14, 130.04) * mm});
            skLineSegment(sketch, "E2044", {"start": v(498.14, 130.04) * mm, "end": v(498.2, 129.54) * mm});
            skLineSegment(sketch, "E2045", {"start": v(498.2, 129.54) * mm, "end": v(498.25, 129.02) * mm});
            skLineSegment(sketch, "E2046", {"start": v(498.25, 129.02) * mm, "end": v(498.27, 128.5) * mm});
            skLineSegment(sketch, "E2047", {"start": v(497.85, 166.45) * mm, "end": v(471.72, 166.45) * mm});
            skLineSegment(sketch, "E2048", {"start": v(488.42, 166.45) * mm, "end": v(488.9, 166.43) * mm});
            skLineSegment(sketch, "E2049", {"start": v(488.9, 166.43) * mm, "end": v(489.37, 166.38) * mm});
            skLineSegment(sketch, "E2050", {"start": v(489.37, 166.38) * mm, "end": v(489.84, 166.32) * mm});
            skLineSegment(sketch, "E2051", {"start": v(489.84, 166.32) * mm, "end": v(490.3, 166.23) * mm});
            skLineSegment(sketch, "E2052", {"start": v(490.3, 166.23) * mm, "end": v(490.76, 166.11) * mm});
            skLineSegment(sketch, "E2053", {"start": v(490.76, 166.11) * mm, "end": v(491.21, 165.98) * mm});
            skLineSegment(sketch, "E2054", {"start": v(491.21, 165.98) * mm, "end": v(491.65, 165.82) * mm});
            skLineSegment(sketch, "E2055", {"start": v(491.65, 165.82) * mm, "end": v(492.09, 165.64) * mm});
            skLineSegment(sketch, "E2056", {"start": v(492.09, 165.64) * mm, "end": v(492.52, 165.44) * mm});
            skLineSegment(sketch, "E2057", {"start": v(492.52, 165.44) * mm, "end": v(492.93, 165.22) * mm});
            skLineSegment(sketch, "E2058", {"start": v(492.93, 165.22) * mm, "end": v(493.34, 164.98) * mm});
            skLineSegment(sketch, "E2059", {"start": v(493.34, 164.98) * mm, "end": v(493.73, 164.72) * mm});
            skLineSegment(sketch, "E2060", {"start": v(493.73, 164.72) * mm, "end": v(494.1, 164.43) * mm});
            skLineSegment(sketch, "E2061", {"start": v(494.1, 164.43) * mm, "end": v(494.48, 164.13) * mm});
            skLineSegment(sketch, "E2062", {"start": v(494.48, 164.13) * mm, "end": v(494.83, 163.81) * mm});
            skLineSegment(sketch, "E2063", {"start": v(494.83, 163.81) * mm, "end": v(495.16, 163.47) * mm});
            skLineSegment(sketch, "E2064", {"start": v(495.16, 163.47) * mm, "end": v(495.5, 163.13) * mm});
            skLineSegment(sketch, "E2065", {"start": v(495.5, 163.13) * mm, "end": v(495.82, 162.77) * mm});
            skLineSegment(sketch, "E2066", {"start": v(495.82, 162.77) * mm, "end": v(496.12, 162.4) * mm});
            skLineSegment(sketch, "E2067", {"start": v(496.12, 162.4) * mm, "end": v(496.4, 162.01) * mm});
            skLineSegment(sketch, "E2068", {"start": v(496.4, 162.01) * mm, "end": v(496.66, 161.61) * mm});
            skLineSegment(sketch, "E2069", {"start": v(496.66, 161.61) * mm, "end": v(496.9, 161.2) * mm});
            skLineSegment(sketch, "E2070", {"start": v(496.9, 161.2) * mm, "end": v(497.12, 160.78) * mm});
            skLineSegment(sketch, "E2071", {"start": v(497.12, 160.78) * mm, "end": v(497.31, 160.34) * mm});
            skLineSegment(sketch, "E2072", {"start": v(497.31, 160.34) * mm, "end": v(497.5, 159.9) * mm});
            skLineSegment(sketch, "E2073", {"start": v(497.5, 159.9) * mm, "end": v(497.64, 159.45) * mm});
            skLineSegment(sketch, "E2074", {"start": v(497.64, 159.45) * mm, "end": v(497.78, 159) * mm});
            skLineSegment(sketch, "E2075", {"start": v(497.78, 159) * mm, "end": v(497.88, 158.53) * mm});
            skLineSegment(sketch, "E2076", {"start": v(497.88, 158.53) * mm, "end": v(497.97, 158.06) * mm});
            skLineSegment(sketch, "E2077", {"start": v(497.97, 158.06) * mm, "end": v(498.03, 157.59) * mm});
            skLineSegment(sketch, "E2078", {"start": v(498.03, 157.59) * mm, "end": v(498.07, 157.1) * mm});
            skLineSegment(sketch, "E2079", {"start": v(498.07, 157.1) * mm, "end": v(498.09, 156.63) * mm});
            skLineSegment(sketch, "E2080", {"start": v(498.09, 156.63) * mm, "end": v(498.12, 156.16) * mm});
            skLineSegment(sketch, "E2081", {"start": v(498.12, 156.16) * mm, "end": v(498.14, 155.69) * mm});
            skLineSegment(sketch, "E2082", {"start": v(498.14, 155.69) * mm, "end": v(498.13, 155.22) * mm});
            skLineSegment(sketch, "E2083", {"start": v(498.13, 155.22) * mm, "end": v(498.1, 154.75) * mm});
            skLineSegment(sketch, "E2084", {"start": v(498.1, 154.75) * mm, "end": v(498.04, 154.29) * mm});
            skLineSegment(sketch, "E2085", {"start": v(498.04, 154.29) * mm, "end": v(497.96, 153.83) * mm});
            skLineSegment(sketch, "E2086", {"start": v(497.96, 153.83) * mm, "end": v(497.85, 153.37) * mm});
            skLineSegment(sketch, "E2087", {"start": v(497.85, 153.37) * mm, "end": v(497.73, 152.92) * mm});
            skLineSegment(sketch, "E2088", {"start": v(497.73, 152.92) * mm, "end": v(497.58, 152.48) * mm});
            skLineSegment(sketch, "E2089", {"start": v(497.58, 152.48) * mm, "end": v(497.42, 152.05) * mm});
            skLineSegment(sketch, "E2090", {"start": v(497.42, 152.05) * mm, "end": v(497.23, 151.62) * mm});
            skLineSegment(sketch, "E2091", {"start": v(497.23, 151.62) * mm, "end": v(497.02, 151.2) * mm});
            skLineSegment(sketch, "E2092", {"start": v(497.02, 151.2) * mm, "end": v(496.79, 150.8) * mm});
            skLineSegment(sketch, "E2093", {"start": v(496.79, 150.8) * mm, "end": v(496.53, 150.4) * mm});
            skLineSegment(sketch, "E2094", {"start": v(496.53, 150.4) * mm, "end": v(496.26, 150.02) * mm});
            skLineSegment(sketch, "E2095", {"start": v(496.26, 150.02) * mm, "end": v(495.97, 149.65) * mm});
            skLineSegment(sketch, "E2096", {"start": v(495.97, 149.65) * mm, "end": v(495.65, 149.37) * mm});
            skLineSegment(sketch, "E2097", {"start": v(495.65, 149.37) * mm, "end": v(495.32, 149.1) * mm});
            skLineSegment(sketch, "E2098", {"start": v(495.32, 149.1) * mm, "end": v(494.98, 148.86) * mm});
            skLineSegment(sketch, "E2099", {"start": v(494.98, 148.86) * mm, "end": v(494.63, 148.63) * mm});
            skLineSegment(sketch, "E2100", {"start": v(494.63, 148.63) * mm, "end": v(494.27, 148.42) * mm});
            skLineSegment(sketch, "E2101", {"start": v(494.27, 148.42) * mm, "end": v(493.9, 148.23) * mm});
            skLineSegment(sketch, "E2102", {"start": v(493.9, 148.23) * mm, "end": v(493.51, 148.06) * mm});
            skLineSegment(sketch, "E2103", {"start": v(493.51, 148.06) * mm, "end": v(493.12, 147.91) * mm});
            skLineSegment(sketch, "E2104", {"start": v(493.12, 147.91) * mm, "end": v(492.73, 147.78) * mm});
            skLineSegment(sketch, "E2105", {"start": v(492.73, 147.78) * mm, "end": v(492.32, 147.67) * mm});
            skLineSegment(sketch, "E2106", {"start": v(492.32, 147.67) * mm, "end": v(491.92, 147.58) * mm});
            skLineSegment(sketch, "E2107", {"start": v(491.92, 147.58) * mm, "end": v(491.5, 147.5) * mm});
            skLineSegment(sketch, "E2108", {"start": v(491.5, 147.5) * mm, "end": v(491.09, 147.46) * mm});
            skLineSegment(sketch, "E2109", {"start": v(491.09, 147.46) * mm, "end": v(490.67, 147.43) * mm});
            skLineSegment(sketch, "E2110", {"start": v(490.67, 147.43) * mm, "end": v(490.24, 147.43) * mm});
            skLineSegment(sketch, "E2111", {"start": v(490.24, 147.43) * mm, "end": v(489.82, 147.45) * mm});
            skLineSegment(sketch, "E2112", {"start": v(489.82, 147.45) * mm, "end": v(471.72, 147.45) * mm});
            skLineSegment(sketch, "E2113", {"start": v(497.7, 182.78) * mm, "end": v(497.83, 182.55) * mm});
            skLineSegment(sketch, "E2114", {"start": v(497.83, 182.55) * mm, "end": v(497.94, 182.31) * mm});
            skLineSegment(sketch, "E2115", {"start": v(497.94, 182.31) * mm, "end": v(498.03, 182.07) * mm});
            skLineSegment(sketch, "E2116", {"start": v(498.03, 182.07) * mm, "end": v(498.1, 181.82) * mm});
            skLineSegment(sketch, "E2117", {"start": v(498.1, 181.82) * mm, "end": v(498.16, 181.56) * mm});
            skLineSegment(sketch, "E2118", {"start": v(498.16, 181.56) * mm, "end": v(498.2, 181.3) * mm});
            skLineSegment(sketch, "E2119", {"start": v(498.2, 181.3) * mm, "end": v(498.21, 181.04) * mm});
            skLineSegment(sketch, "E2120", {"start": v(498.21, 181.04) * mm, "end": v(498.21, 180.78) * mm});
            skLineSegment(sketch, "E2121", {"start": v(498.21, 180.78) * mm, "end": v(498.21, 180.6) * mm});
            skLineSegment(sketch, "E2122", {"start": v(498.21, 180.6) * mm, "end": v(498.2, 180.4) * mm});
            skLineSegment(sketch, "E2123", {"start": v(498.2, 180.4) * mm, "end": v(498.18, 180.22) * mm});
            skLineSegment(sketch, "E2124", {"start": v(498.18, 180.22) * mm, "end": v(498.15, 180.03) * mm});
            skLineSegment(sketch, "E2125", {"start": v(498.15, 180.03) * mm, "end": v(498.12, 179.84) * mm});
            skLineSegment(sketch, "E2126", {"start": v(498.12, 179.84) * mm, "end": v(498.07, 179.66) * mm});
            skLineSegment(sketch, "E2127", {"start": v(498.07, 179.66) * mm, "end": v(498.02, 179.48) * mm});
            skLineSegment(sketch, "E2128", {"start": v(498.02, 179.48) * mm, "end": v(497.96, 179.3) * mm});
            skLineSegment(sketch, "E2129", {"start": v(497.96, 179.3) * mm, "end": v(497.9, 179.13) * mm});
            skLineSegment(sketch, "E2130", {"start": v(497.9, 179.13) * mm, "end": v(497.82, 178.96) * mm});
            skLineSegment(sketch, "E2131", {"start": v(497.82, 178.96) * mm, "end": v(497.74, 178.79) * mm});
            skLineSegment(sketch, "E2132", {"start": v(497.74, 178.79) * mm, "end": v(497.64, 178.62) * mm});
            skLineSegment(sketch, "E2133", {"start": v(497.64, 178.62) * mm, "end": v(497.55, 178.46) * mm});
            skLineSegment(sketch, "E2134", {"start": v(497.55, 178.46) * mm, "end": v(497.44, 178.3) * mm});
            skLineSegment(sketch, "E2135", {"start": v(497.44, 178.3) * mm, "end": v(497.33, 178.15) * mm});
            skLineSegment(sketch, "E2136", {"start": v(497.33, 178.15) * mm, "end": v(497.2, 178) * mm});
            skLineSegment(sketch, "E2137", {"start": v(497.2, 178) * mm, "end": v(497.08, 177.89) * mm});
            skLineSegment(sketch, "E2138", {"start": v(497.08, 177.89) * mm, "end": v(496.96, 177.77) * mm});
            skLineSegment(sketch, "E2139", {"start": v(496.96, 177.77) * mm, "end": v(496.82, 177.67) * mm});
            skLineSegment(sketch, "E2140", {"start": v(496.82, 177.67) * mm, "end": v(496.69, 177.57) * mm});
            skLineSegment(sketch, "E2141", {"start": v(496.69, 177.57) * mm, "end": v(496.55, 177.48) * mm});
            skLineSegment(sketch, "E2142", {"start": v(496.55, 177.48) * mm, "end": v(496.4, 177.4) * mm});
            skLineSegment(sketch, "E2143", {"start": v(496.4, 177.4) * mm, "end": v(496.25, 177.32) * mm});
            skLineSegment(sketch, "E2144", {"start": v(496.25, 177.32) * mm, "end": v(496.1, 177.25) * mm});
            skLineSegment(sketch, "E2145", {"start": v(496.1, 177.25) * mm, "end": v(495.94, 177.18) * mm});
            skLineSegment(sketch, "E2146", {"start": v(495.94, 177.18) * mm, "end": v(495.78, 177.13) * mm});
            skLineSegment(sketch, "E2147", {"start": v(495.78, 177.13) * mm, "end": v(495.62, 177.08) * mm});
            skLineSegment(sketch, "E2148", {"start": v(495.62, 177.08) * mm, "end": v(495.46, 177.05) * mm});
            skLineSegment(sketch, "E2149", {"start": v(495.46, 177.05) * mm, "end": v(495.3, 177.02) * mm});
            skLineSegment(sketch, "E2150", {"start": v(495.3, 177.02) * mm, "end": v(495.12, 177) * mm});
            skLineSegment(sketch, "E2151", {"start": v(495.12, 177) * mm, "end": v(494.96, 176.98) * mm});
            skLineSegment(sketch, "E2152", {"start": v(494.96, 176.98) * mm, "end": v(494.79, 176.98) * mm});
            skLineSegment(sketch, "E2153", {"start": v(494.79, 176.98) * mm, "end": v(464.42, 176.98) * mm});
            skLineSegment(sketch, "E2154", {"start": v(471.55, 174.34) * mm, "end": v(471.55, 182.4) * mm});
            skArc(sketch, "E2155", {"start": v(-198.36, 700.5) * mm, "mid": v(-199.24, 702.62) * mm, "end": v(-201.36, 703.5) * mm});
            skArc(sketch, "E2156", {"start": v(-201.36, 703.5) * mm, "mid": v(-203.48, 702.62) * mm, "end": v(-204.36, 700.5) * mm});
            skArc(sketch, "E2157", {"start": v(-204.36, 700.5) * mm, "mid": v(-203.48, 698.38) * mm, "end": v(-201.36, 697.5) * mm});
            skArc(sketch, "E2158", {"start": v(-201.36, 697.5) * mm, "mid": v(-199.24, 698.38) * mm, "end": v(-198.36, 700.5) * mm});
            skArc(sketch, "E2159", {"start": v(-144.27, 700.5) * mm, "mid": v(-145.15, 702.62) * mm, "end": v(-147.27, 703.5) * mm});
            skArc(sketch, "E2160", {"start": v(-147.27, 703.5) * mm, "mid": v(-149.4, 702.62) * mm, "end": v(-150.27, 700.5) * mm});
            skArc(sketch, "E2161", {"start": v(-150.27, 700.5) * mm, "mid": v(-149.4, 698.38) * mm, "end": v(-147.27, 697.5) * mm});
            skArc(sketch, "E2162", {"start": v(-147.27, 697.5) * mm, "mid": v(-145.15, 698.38) * mm, "end": v(-144.27, 700.5) * mm});
            skArc(sketch, "E2163", {"start": v(-198.36, 480.5) * mm, "mid": v(-199.24, 482.62) * mm, "end": v(-201.36, 483.5) * mm});
            skArc(sketch, "E2164", {"start": v(-201.36, 483.5) * mm, "mid": v(-203.48, 482.62) * mm, "end": v(-204.36, 480.5) * mm});
            skArc(sketch, "E2165", {"start": v(-204.36, 480.5) * mm, "mid": v(-203.48, 478.38) * mm, "end": v(-201.36, 477.5) * mm});
            skArc(sketch, "E2166", {"start": v(-201.36, 477.5) * mm, "mid": v(-199.24, 478.38) * mm, "end": v(-198.36, 480.5) * mm});
            skArc(sketch, "E2167", {"start": v(-144.27, 480.5) * mm, "mid": v(-145.15, 482.62) * mm, "end": v(-147.27, 483.5) * mm});
            skArc(sketch, "E2168", {"start": v(-147.27, 483.5) * mm, "mid": v(-149.4, 482.62) * mm, "end": v(-150.27, 480.5) * mm});
            skArc(sketch, "E2169", {"start": v(-150.27, 480.5) * mm, "mid": v(-149.4, 478.38) * mm, "end": v(-147.27, 477.5) * mm});
            skArc(sketch, "E2170", {"start": v(-147.27, 477.5) * mm, "mid": v(-145.15, 478.38) * mm, "end": v(-144.27, 480.5) * mm});
            skArc(sketch, "E2171", {"start": v(-198.36, 330.5) * mm, "mid": v(-199.24, 332.62) * mm, "end": v(-201.36, 333.5) * mm});
            skArc(sketch, "E2172", {"start": v(-201.36, 333.5) * mm, "mid": v(-203.48, 332.62) * mm, "end": v(-204.36, 330.5) * mm});
            skArc(sketch, "E2173", {"start": v(-204.36, 330.5) * mm, "mid": v(-203.48, 328.38) * mm, "end": v(-201.36, 327.5) * mm});
            skArc(sketch, "E2174", {"start": v(-201.36, 327.5) * mm, "mid": v(-199.24, 328.38) * mm, "end": v(-198.36, 330.5) * mm});
            skArc(sketch, "E2175", {"start": v(-144.27, 330.5) * mm, "mid": v(-145.15, 332.62) * mm, "end": v(-147.27, 333.5) * mm});
            skArc(sketch, "E2176", {"start": v(-147.27, 333.5) * mm, "mid": v(-149.4, 332.62) * mm, "end": v(-150.27, 330.5) * mm});
            skArc(sketch, "E2177", {"start": v(-150.27, 330.5) * mm, "mid": v(-149.4, 328.38) * mm, "end": v(-147.27, 327.5) * mm});
            skArc(sketch, "E2178", {"start": v(-147.27, 327.5) * mm, "mid": v(-145.15, 328.38) * mm, "end": v(-144.27, 330.5) * mm});
            skArc(sketch, "E2179", {"start": v(-198.36, 180.5) * mm, "mid": v(-199.24, 182.62) * mm, "end": v(-201.36, 183.5) * mm});
            skArc(sketch, "E2180", {"start": v(-201.36, 183.5) * mm, "mid": v(-203.48, 182.62) * mm, "end": v(-204.36, 180.5) * mm});
            skArc(sketch, "E2181", {"start": v(-204.36, 180.5) * mm, "mid": v(-203.48, 178.38) * mm, "end": v(-201.36, 177.5) * mm});
            skArc(sketch, "E2182", {"start": v(-201.36, 177.5) * mm, "mid": v(-199.24, 178.38) * mm, "end": v(-198.36, 180.5) * mm});
            skArc(sketch, "E2183", {"start": v(-144.27, 180.5) * mm, "mid": v(-145.15, 182.62) * mm, "end": v(-147.27, 183.5) * mm});
            skArc(sketch, "E2184", {"start": v(-147.27, 183.5) * mm, "mid": v(-149.4, 182.62) * mm, "end": v(-150.27, 180.5) * mm});
            skArc(sketch, "E2185", {"start": v(-150.27, 180.5) * mm, "mid": v(-149.4, 178.38) * mm, "end": v(-147.27, 177.5) * mm});
            skArc(sketch, "E2186", {"start": v(-147.27, 177.5) * mm, "mid": v(-145.15, 178.38) * mm, "end": v(-144.27, 180.5) * mm});
            skArc(sketch, "E2187", {"start": v(-198.36, 30.5) * mm, "mid": v(-199.24, 32.62) * mm, "end": v(-201.36, 33.5) * mm});
            skArc(sketch, "E2188", {"start": v(-201.36, 33.5) * mm, "mid": v(-203.48, 32.62) * mm, "end": v(-204.36, 30.5) * mm});
            skArc(sketch, "E2189", {"start": v(-204.36, 30.5) * mm, "mid": v(-203.48, 28.38) * mm, "end": v(-201.36, 27.5) * mm});
            skArc(sketch, "E2190", {"start": v(-201.36, 27.5) * mm, "mid": v(-199.24, 28.38) * mm, "end": v(-198.36, 30.5) * mm});
            skArc(sketch, "E2191", {"start": v(-144.27, 30.5) * mm, "mid": v(-145.15, 32.62) * mm, "end": v(-147.27, 33.5) * mm});
            skArc(sketch, "E2192", {"start": v(-147.27, 33.5) * mm, "mid": v(-149.4, 32.62) * mm, "end": v(-150.27, 30.5) * mm});
            skArc(sketch, "E2193", {"start": v(-150.27, 30.5) * mm, "mid": v(-149.4, 28.38) * mm, "end": v(-147.27, 27.5) * mm});
            skArc(sketch, "E2194", {"start": v(-147.27, 27.5) * mm, "mid": v(-145.15, 28.38) * mm, "end": v(-144.27, 30.5) * mm});
            skArc(sketch, "E2195", {"start": v(-198.36, -89.5) * mm, "mid": v(-199.24, -87.38) * mm, "end": v(-201.36, -86.5) * mm});
            skArc(sketch, "E2196", {"start": v(-201.36, -86.5) * mm, "mid": v(-203.48, -87.38) * mm, "end": v(-204.36, -89.5) * mm});
            skArc(sketch, "E2197", {"start": v(-204.36, -89.5) * mm, "mid": v(-203.48, -91.62) * mm, "end": v(-201.36, -92.5) * mm});
            skArc(sketch, "E2198", {"start": v(-201.36, -92.5) * mm, "mid": v(-199.24, -91.62) * mm, "end": v(-198.36, -89.5) * mm});
            skArc(sketch, "E2199", {"start": v(-144.27, -89.5) * mm, "mid": v(-145.15, -87.38) * mm, "end": v(-147.27, -86.5) * mm});
            skArc(sketch, "E2200", {"start": v(-147.27, -86.5) * mm, "mid": v(-149.4, -87.38) * mm, "end": v(-150.27, -89.5) * mm});
            skArc(sketch, "E2201", {"start": v(-150.27, -89.5) * mm, "mid": v(-149.4, -91.62) * mm, "end": v(-147.27, -92.5) * mm});
            skArc(sketch, "E2202", {"start": v(-147.27, -92.5) * mm, "mid": v(-145.15, -91.62) * mm, "end": v(-144.27, -89.5) * mm});
            skArc(sketch, "E2203", {"start": v(-198.36, -269.5) * mm, "mid": v(-199.24, -267.38) * mm, "end": v(-201.36, -266.5) * mm});
            skArc(sketch, "E2204", {"start": v(-201.36, -266.5) * mm, "mid": v(-203.48, -267.38) * mm, "end": v(-204.36, -269.5) * mm});
            skArc(sketch, "E2205", {"start": v(-204.36, -269.5) * mm, "mid": v(-203.48, -271.62) * mm, "end": v(-201.36, -272.5) * mm});
            skArc(sketch, "E2206", {"start": v(-201.36, -272.5) * mm, "mid": v(-199.24, -271.62) * mm, "end": v(-198.36, -269.5) * mm});
            skArc(sketch, "E2207", {"start": v(-144.27, -269.5) * mm, "mid": v(-145.15, -267.38) * mm, "end": v(-147.27, -266.5) * mm});
            skArc(sketch, "E2208", {"start": v(-147.27, -266.5) * mm, "mid": v(-149.4, -267.38) * mm, "end": v(-150.27, -269.5) * mm});
            skArc(sketch, "E2209", {"start": v(-150.27, -269.5) * mm, "mid": v(-149.4, -271.62) * mm, "end": v(-147.27, -272.5) * mm});
            skArc(sketch, "E2210", {"start": v(-147.27, -272.5) * mm, "mid": v(-145.15, -271.62) * mm, "end": v(-144.27, -269.5) * mm});
            skArc(sketch, "E2211", {"start": v(-198.36, -419.5) * mm, "mid": v(-199.24, -417.38) * mm, "end": v(-201.36, -416.5) * mm});
            skArc(sketch, "E2212", {"start": v(-201.36, -416.5) * mm, "mid": v(-203.48, -417.38) * mm, "end": v(-204.36, -419.5) * mm});
            skArc(sketch, "E2213", {"start": v(-204.36, -419.5) * mm, "mid": v(-203.48, -421.62) * mm, "end": v(-201.36, -422.5) * mm});
            skArc(sketch, "E2214", {"start": v(-201.36, -422.5) * mm, "mid": v(-199.24, -421.62) * mm, "end": v(-198.36, -419.5) * mm});
            skArc(sketch, "E2215", {"start": v(-144.27, -419.5) * mm, "mid": v(-145.15, -417.38) * mm, "end": v(-147.27, -416.5) * mm});
            skArc(sketch, "E2216", {"start": v(-147.27, -416.5) * mm, "mid": v(-149.4, -417.38) * mm, "end": v(-150.27, -419.5) * mm});
            skArc(sketch, "E2217", {"start": v(-150.27, -419.5) * mm, "mid": v(-149.4, -421.62) * mm, "end": v(-147.27, -422.5) * mm});
            skArc(sketch, "E2218", {"start": v(-147.27, -422.5) * mm, "mid": v(-145.15, -421.62) * mm, "end": v(-144.27, -419.5) * mm});
            skArc(sketch, "E2219", {"start": v(-198.36, -569.5) * mm, "mid": v(-199.24, -567.38) * mm, "end": v(-201.36, -566.5) * mm});
            skArc(sketch, "E2220", {"start": v(-201.36, -566.5) * mm, "mid": v(-203.48, -567.38) * mm, "end": v(-204.36, -569.5) * mm});
            skArc(sketch, "E2221", {"start": v(-204.36, -569.5) * mm, "mid": v(-203.48, -571.62) * mm, "end": v(-201.36, -572.5) * mm});
            skArc(sketch, "E2222", {"start": v(-201.36, -572.5) * mm, "mid": v(-199.24, -571.62) * mm, "end": v(-198.36, -569.5) * mm});
            skArc(sketch, "E2223", {"start": v(-144.27, -569.5) * mm, "mid": v(-145.15, -567.38) * mm, "end": v(-147.27, -566.5) * mm});
            skArc(sketch, "E2224", {"start": v(-147.27, -566.5) * mm, "mid": v(-149.4, -567.38) * mm, "end": v(-150.27, -569.5) * mm});
            skArc(sketch, "E2225", {"start": v(-150.27, -569.5) * mm, "mid": v(-149.4, -571.62) * mm, "end": v(-147.27, -572.5) * mm});
            skArc(sketch, "E2226", {"start": v(-147.27, -572.5) * mm, "mid": v(-145.15, -571.62) * mm, "end": v(-144.27, -569.5) * mm});
            skArc(sketch, "E2227", {"start": v(-198.36, -719.5) * mm, "mid": v(-199.24, -717.38) * mm, "end": v(-201.36, -716.5) * mm});
            skArc(sketch, "E2228", {"start": v(-201.36, -716.5) * mm, "mid": v(-203.48, -717.38) * mm, "end": v(-204.36, -719.5) * mm});
            skArc(sketch, "E2229", {"start": v(-204.36, -719.5) * mm, "mid": v(-203.48, -721.62) * mm, "end": v(-201.36, -722.5) * mm});
            skArc(sketch, "E2230", {"start": v(-201.36, -722.5) * mm, "mid": v(-199.24, -721.62) * mm, "end": v(-198.36, -719.5) * mm});
            skArc(sketch, "E2231", {"start": v(-144.27, -719.5) * mm, "mid": v(-145.15, -717.38) * mm, "end": v(-147.27, -716.5) * mm});
            skArc(sketch, "E2232", {"start": v(-147.27, -716.5) * mm, "mid": v(-149.4, -717.38) * mm, "end": v(-150.27, -719.5) * mm});
            skArc(sketch, "E2233", {"start": v(-150.27, -719.5) * mm, "mid": v(-149.4, -721.62) * mm, "end": v(-147.27, -722.5) * mm});
            skArc(sketch, "E2234", {"start": v(-147.27, -722.5) * mm, "mid": v(-145.15, -721.62) * mm, "end": v(-144.27, -719.5) * mm});
            skArc(sketch, "E2235", {"start": v(-198.36, -149.5) * mm, "mid": v(-199.24, -147.38) * mm, "end": v(-201.36, -146.5) * mm});
            skArc(sketch, "E2236", {"start": v(-201.36, -146.5) * mm, "mid": v(-203.48, -147.38) * mm, "end": v(-204.36, -149.5) * mm});
            skArc(sketch, "E2237", {"start": v(-204.36, -149.5) * mm, "mid": v(-203.48, -151.62) * mm, "end": v(-201.36, -152.5) * mm});
            skArc(sketch, "E2238", {"start": v(-201.36, -152.5) * mm, "mid": v(-199.24, -151.62) * mm, "end": v(-198.36, -149.5) * mm});
            skArc(sketch, "E2239", {"start": v(-144.27, -149.5) * mm, "mid": v(-145.15, -147.38) * mm, "end": v(-147.27, -146.5) * mm});
            skArc(sketch, "E2240", {"start": v(-147.27, -146.5) * mm, "mid": v(-149.4, -147.38) * mm, "end": v(-150.27, -149.5) * mm});
            skArc(sketch, "E2241", {"start": v(-150.27, -149.5) * mm, "mid": v(-149.4, -151.62) * mm, "end": v(-147.27, -152.5) * mm});
            skArc(sketch, "E2242", {"start": v(-147.27, -152.5) * mm, "mid": v(-145.15, -151.62) * mm, "end": v(-144.27, -149.5) * mm});
            skArc(sketch, "E2243", {"start": v(-198.36, 590.15) * mm, "mid": v(-199.24, 592.27) * mm, "end": v(-201.36, 593.15) * mm});
            skArc(sketch, "E2244", {"start": v(-201.36, 593.15) * mm, "mid": v(-203.48, 592.27) * mm, "end": v(-204.36, 590.15) * mm});
            skArc(sketch, "E2245", {"start": v(-204.36, 590.15) * mm, "mid": v(-203.48, 588.03) * mm, "end": v(-201.36, 587.15) * mm});
            skArc(sketch, "E2246", {"start": v(-201.36, 587.15) * mm, "mid": v(-199.24, 588.03) * mm, "end": v(-198.36, 590.15) * mm});
            skArc(sketch, "E2247", {"start": v(-144.27, 590.15) * mm, "mid": v(-145.15, 592.27) * mm, "end": v(-147.27, 593.15) * mm});
            skArc(sketch, "E2248", {"start": v(-147.27, 593.15) * mm, "mid": v(-149.4, 592.27) * mm, "end": v(-150.27, 590.15) * mm});
            skArc(sketch, "E2249", {"start": v(-150.27, 590.15) * mm, "mid": v(-149.4, 588.03) * mm, "end": v(-147.27, 587.15) * mm});
            skArc(sketch, "E2250", {"start": v(-147.27, 587.15) * mm, "mid": v(-145.15, 588.03) * mm, "end": v(-144.27, 590.15) * mm});
            skArc(sketch, "E2251", {"start": v(-198.36, -836.6) * mm, "mid": v(-199.24, -834.48) * mm, "end": v(-201.36, -833.6) * mm});
            skArc(sketch, "E2252", {"start": v(-201.36, -833.6) * mm, "mid": v(-203.48, -834.48) * mm, "end": v(-204.36, -836.6) * mm});
            skArc(sketch, "E2253", {"start": v(-204.36, -836.6) * mm, "mid": v(-203.48, -838.72) * mm, "end": v(-201.36, -839.6) * mm});
            skArc(sketch, "E2254", {"start": v(-201.36, -839.6) * mm, "mid": v(-199.24, -838.72) * mm, "end": v(-198.36, -836.6) * mm});
            skArc(sketch, "E2255", {"start": v(-144.27, -836.6) * mm, "mid": v(-145.15, -834.48) * mm, "end": v(-147.27, -833.6) * mm});
            skArc(sketch, "E2256", {"start": v(-147.27, -833.6) * mm, "mid": v(-149.4, -834.48) * mm, "end": v(-150.27, -836.6) * mm});
            skArc(sketch, "E2257", {"start": v(-150.27, -836.6) * mm, "mid": v(-149.4, -838.72) * mm, "end": v(-147.27, -839.6) * mm});
            skArc(sketch, "E2258", {"start": v(-147.27, -839.6) * mm, "mid": v(-145.15, -838.72) * mm, "end": v(-144.27, -836.6) * mm});
            skArc(sketch, "E2259", {"start": v(-585.79, -1167.96) * mm, "mid": v(-587.9, -1168.84) * mm, "end": v(-588.79, -1170.96) * mm});
            skArc(sketch, "E2260", {"start": v(-588.79, -1170.96) * mm, "mid": v(-587.9, -1173.08) * mm, "end": v(-585.79, -1173.96) * mm});
            skArc(sketch, "E2261", {"start": v(-585.79, -1173.96) * mm, "mid": v(-583.67, -1173.08) * mm, "end": v(-582.79, -1170.96) * mm});
            skArc(sketch, "E2262", {"start": v(-582.79, -1170.96) * mm, "mid": v(-583.67, -1168.84) * mm, "end": v(-585.79, -1167.96) * mm});
            skArc(sketch, "E2263", {"start": v(43.66, -1175.71) * mm, "mid": v(41.54, -1176.59) * mm, "end": v(40.66, -1178.71) * mm});
            skArc(sketch, "E2264", {"start": v(40.66, -1178.71) * mm, "mid": v(41.54, -1180.83) * mm, "end": v(43.66, -1181.71) * mm});
            skArc(sketch, "E2265", {"start": v(43.66, -1181.71) * mm, "mid": v(45.78, -1180.83) * mm, "end": v(46.66, -1178.71) * mm});
            skArc(sketch, "E2266", {"start": v(46.66, -1178.71) * mm, "mid": v(45.78, -1176.59) * mm, "end": v(43.66, -1175.71) * mm});
            skArc(sketch, "E2267", {"start": v(562.85, -1179.72) * mm, "mid": v(560.73, -1180.6) * mm, "end": v(559.85, -1182.72) * mm});
            skArc(sketch, "E2268", {"start": v(559.85, -1182.72) * mm, "mid": v(560.73, -1184.84) * mm, "end": v(562.85, -1185.72) * mm});
            skArc(sketch, "E2269", {"start": v(562.85, -1185.72) * mm, "mid": v(564.97, -1184.84) * mm, "end": v(565.85, -1182.72) * mm});
            skArc(sketch, "E2270", {"start": v(565.85, -1182.72) * mm, "mid": v(564.97, -1180.6) * mm, "end": v(562.85, -1179.72) * mm});
            skArc(sketch, "E2271", {"start": v(-597.55, -488.4) * mm, "mid": v(-599.67, -489.28) * mm, "end": v(-600.55, -491.4) * mm});
            skArc(sketch, "E2272", {"start": v(-600.55, -491.4) * mm, "mid": v(-599.67, -493.52) * mm, "end": v(-597.55, -494.4) * mm});
            skArc(sketch, "E2273", {"start": v(-597.55, -494.4) * mm, "mid": v(-595.43, -493.52) * mm, "end": v(-594.55, -491.4) * mm});
            skArc(sketch, "E2274", {"start": v(-594.55, -491.4) * mm, "mid": v(-595.43, -489.28) * mm, "end": v(-597.55, -488.4) * mm});
            skArc(sketch, "E2275", {"start": v(17.94, -590.98) * mm, "mid": v(15.82, -591.86) * mm, "end": v(14.94, -593.98) * mm});
            skArc(sketch, "E2276", {"start": v(14.94, -593.98) * mm, "mid": v(15.82, -596.1) * mm, "end": v(17.94, -596.98) * mm});
            skArc(sketch, "E2277", {"start": v(17.94, -596.98) * mm, "mid": v(20.07, -596.1) * mm, "end": v(20.94, -593.98) * mm});
            skArc(sketch, "E2278", {"start": v(20.94, -593.98) * mm, "mid": v(20.07, -591.86) * mm, "end": v(17.94, -590.98) * mm});
            skArc(sketch, "E2279", {"start": v(387.12, -441.77) * mm, "mid": v(385, -442.65) * mm, "end": v(384.12, -444.77) * mm});
            skArc(sketch, "E2280", {"start": v(384.12, -444.77) * mm, "mid": v(385, -446.9) * mm, "end": v(387.12, -447.77) * mm});
            skArc(sketch, "E2281", {"start": v(387.12, -447.77) * mm, "mid": v(389.24, -446.9) * mm, "end": v(390.12, -444.77) * mm});
            skArc(sketch, "E2282", {"start": v(390.12, -444.77) * mm, "mid": v(389.24, -442.65) * mm, "end": v(387.12, -441.77) * mm});
            skArc(sketch, "E2283", {"start": v(557.87, 67.39) * mm, "mid": v(555.75, 66.5) * mm, "end": v(554.87, 64.38) * mm});
            skArc(sketch, "E2284", {"start": v(554.87, 64.38) * mm, "mid": v(555.75, 62.26) * mm, "end": v(557.87, 61.38) * mm});
            skArc(sketch, "E2285", {"start": v(557.87, 61.38) * mm, "mid": v(559.99, 62.26) * mm, "end": v(560.87, 64.38) * mm});
            skArc(sketch, "E2286", {"start": v(560.87, 64.38) * mm, "mid": v(559.99, 66.5) * mm, "end": v(557.87, 67.39) * mm});
            skArc(sketch, "E2287", {"start": v(79.47, 121.22) * mm, "mid": v(77.35, 120.34) * mm, "end": v(76.47, 118.22) * mm});
            skArc(sketch, "E2288", {"start": v(76.47, 118.22) * mm, "mid": v(77.35, 116.1) * mm, "end": v(79.47, 115.22) * mm});
            skArc(sketch, "E2289", {"start": v(79.47, 115.22) * mm, "mid": v(81.6, 116.1) * mm, "end": v(82.47, 118.22) * mm});
            skArc(sketch, "E2290", {"start": v(82.47, 118.22) * mm, "mid": v(81.6, 120.34) * mm, "end": v(79.47, 121.22) * mm});
            skArc(sketch, "E2291", {"start": v(-596.3, 166.7) * mm, "mid": v(-598.42, 165.82) * mm, "end": v(-599.3, 163.7) * mm});
            skArc(sketch, "E2292", {"start": v(-599.3, 163.7) * mm, "mid": v(-598.42, 161.58) * mm, "end": v(-596.3, 160.7) * mm});
            skArc(sketch, "E2293", {"start": v(-596.3, 160.7) * mm, "mid": v(-594.18, 161.58) * mm, "end": v(-593.3, 163.7) * mm});
            skArc(sketch, "E2294", {"start": v(-593.3, 163.7) * mm, "mid": v(-594.18, 165.82) * mm, "end": v(-596.3, 166.7) * mm});
            skArc(sketch, "E2295", {"start": v(-580.53, 831.99) * mm, "mid": v(-582.65, 831.11) * mm, "end": v(-583.53, 828.99) * mm});
            skArc(sketch, "E2296", {"start": v(-583.53, 828.99) * mm, "mid": v(-582.65, 826.87) * mm, "end": v(-580.53, 825.99) * mm});
            skArc(sketch, "E2297", {"start": v(-580.53, 825.99) * mm, "mid": v(-578.4, 826.87) * mm, "end": v(-577.53, 828.99) * mm});
            skArc(sketch, "E2298", {"start": v(-577.53, 828.99) * mm, "mid": v(-578.4, 831.11) * mm, "end": v(-580.53, 831.99) * mm});
            skArc(sketch, "E2299", {"start": v(-330.56, 551.26) * mm, "mid": v(-332.69, 550.38) * mm, "end": v(-333.56, 548.26) * mm});
            skArc(sketch, "E2300", {"start": v(-333.56, 548.26) * mm, "mid": v(-332.69, 546.14) * mm, "end": v(-330.56, 545.26) * mm});
            skArc(sketch, "E2301", {"start": v(-330.56, 545.26) * mm, "mid": v(-328.44, 546.14) * mm, "end": v(-327.56, 548.26) * mm});
            skArc(sketch, "E2302", {"start": v(-327.56, 548.26) * mm, "mid": v(-328.44, 550.38) * mm, "end": v(-330.56, 551.26) * mm});
            skArc(sketch, "E2303", {"start": v(36.7, 758.92) * mm, "mid": v(34.57, 758.04) * mm, "end": v(33.7, 755.92) * mm});
            skArc(sketch, "E2304", {"start": v(33.7, 755.92) * mm, "mid": v(34.57, 753.8) * mm, "end": v(36.7, 752.92) * mm});
            skArc(sketch, "E2305", {"start": v(36.7, 752.92) * mm, "mid": v(38.81, 753.8) * mm, "end": v(39.7, 755.92) * mm});
            skArc(sketch, "E2306", {"start": v(39.7, 755.92) * mm, "mid": v(38.81, 758.04) * mm, "end": v(36.7, 758.92) * mm});
            skArc(sketch, "E2307", {"start": v(390.49, 660.86) * mm, "mid": v(388.37, 659.98) * mm, "end": v(387.49, 657.86) * mm});
            skArc(sketch, "E2308", {"start": v(387.49, 657.86) * mm, "mid": v(388.37, 655.74) * mm, "end": v(390.49, 654.86) * mm});
            skArc(sketch, "E2309", {"start": v(390.49, 654.86) * mm, "mid": v(392.6, 655.74) * mm, "end": v(393.49, 657.86) * mm});
            skArc(sketch, "E2310", {"start": v(393.49, 657.86) * mm, "mid": v(392.6, 659.98) * mm, "end": v(390.49, 660.86) * mm});
            skArc(sketch, "E2311", {"start": v(567.39, 1176.17) * mm, "mid": v(565.26, 1175.3) * mm, "end": v(564.39, 1173.17) * mm});
            skArc(sketch, "E2312", {"start": v(564.39, 1173.17) * mm, "mid": v(565.26, 1171.05) * mm, "end": v(567.39, 1170.17) * mm});
            skArc(sketch, "E2313", {"start": v(567.39, 1170.17) * mm, "mid": v(569.5, 1171.05) * mm, "end": v(570.39, 1173.17) * mm});
            skArc(sketch, "E2314", {"start": v(570.39, 1173.17) * mm, "mid": v(569.5, 1175.3) * mm, "end": v(567.39, 1176.17) * mm});
            skArc(sketch, "E2315", {"start": v(-263.27, 1101.18) * mm, "mid": v(-265.39, 1100.3) * mm, "end": v(-266.27, 1098.18) * mm});
            skArc(sketch, "E2316", {"start": v(-266.27, 1098.18) * mm, "mid": v(-265.39, 1096.06) * mm, "end": v(-263.27, 1095.18) * mm});
            skArc(sketch, "E2317", {"start": v(-263.27, 1095.18) * mm, "mid": v(-261.15, 1096.06) * mm, "end": v(-260.27, 1098.18) * mm});
            skArc(sketch, "E2318", {"start": v(-260.27, 1098.18) * mm, "mid": v(-261.15, 1100.3) * mm, "end": v(-263.27, 1101.18) * mm});
            skArc(sketch, "E2319", {"start": v(269.35, 1064.65) * mm, "mid": v(267.23, 1063.77) * mm, "end": v(266.35, 1061.65) * mm});
            skArc(sketch, "E2320", {"start": v(266.35, 1061.65) * mm, "mid": v(267.23, 1059.53) * mm, "end": v(269.35, 1058.65) * mm});
            skArc(sketch, "E2321", {"start": v(269.35, 1058.65) * mm, "mid": v(271.47, 1059.53) * mm, "end": v(272.35, 1061.65) * mm});
            skArc(sketch, "E2322", {"start": v(272.35, 1061.65) * mm, "mid": v(271.47, 1063.77) * mm, "end": v(269.35, 1064.65) * mm});
            skArc(sketch, "E2323", {"start": v(-305.34, -188.2) * mm, "mid": v(-307.46, -189.08) * mm, "end": v(-308.34, -191.2) * mm});
            skArc(sketch, "E2324", {"start": v(-308.34, -191.2) * mm, "mid": v(-307.46, -193.32) * mm, "end": v(-305.34, -194.2) * mm});
            skArc(sketch, "E2325", {"start": v(-305.34, -194.2) * mm, "mid": v(-303.22, -193.32) * mm, "end": v(-302.34, -191.2) * mm});
            skArc(sketch, "E2326", {"start": v(-302.34, -191.2) * mm, "mid": v(-303.22, -189.08) * mm, "end": v(-305.34, -188.2) * mm});
            skLineSegment(sketch, "E2327", {"start": v(-599.45, -1200) * mm, "end": v(600.55, -1200) * mm});
            skLineSegment(sketch, "E2328", {"start": v(600.55, -1200) * mm, "end": v(600.55, 1200) * mm});
            skLineSegment(sketch, "E2329", {"start": v(600.55, 1200) * mm, "end": v(-599.45, 1200) * mm});
            skLineSegment(sketch, "E2330", {"start": v(-599.45, 1200) * mm, "end": v(-599.45, -1200) * mm});
            skLineSegment(sketch, "E2331", {"start": v(-312.7, -1042.25) * mm, "end": v(-172.7, -1042.25) * mm});
            skLineSegment(sketch, "E2332", {"start": v(-172.7, -1042.25) * mm, "end": v(-172.7, -1022.25) * mm});
            skLineSegment(sketch, "E2333", {"start": v(-172.7, -1022.25) * mm, "end": v(-312.7, -1022.25) * mm});
            skLineSegment(sketch, "E2334", {"start": v(-312.7, -1022.25) * mm, "end": v(-312.7, -1042.25) * mm});
            skLineSegment(sketch, "E2335", {"start": v(233.56, 673.05) * mm, "end": v(233.56, 813.05) * mm});
            skLineSegment(sketch, "E2336", {"start": v(233.56, 813.05) * mm, "end": v(213.56, 813.05) * mm});
            skLineSegment(sketch, "E2337", {"start": v(213.56, 813.05) * mm, "end": v(213.56, 673.05) * mm});
            skLineSegment(sketch, "E2338", {"start": v(213.56, 673.05) * mm, "end": v(233.56, 673.05) * mm});
            skSolve(sketch);
        }
        {
            var Q0;
            Q0=makeQuery(id+"F0.imprint","IMPRINT",FACE,{"disambiguationData":[TD([[makeQuery(id+"F0.imprint","IMPRINT",EDGE,{"derivedFrom":sQuery(id+"F0.wireOp",EDGE,"E234")}),1.0]])]});
            extrude(context, id + "F1", {"entities" : qUnion([Q0]), "depth" : 18 * mm});
        }
        {
            var Q0;
            Q0=makeQuery(id+"F0.imprint","IMPRINT",FACE,{"disambiguationData":[TD([[makeQuery(id+"F0.imprint","IMPRINT",EDGE,{"derivedFrom":sQuery(id+"F0.wireOp",EDGE,"E130")}),1.0]])]});
            extrude(context, id + "F2", {"entities" : qUnion([Q0]), "depth" : 18 * mm});
        }
        {
            var Q0;
            Q0=makeQuery(id+"F0.imprint","IMPRINT",FACE,{"disambiguationData":[TD([[makeQuery(id+"F0.imprint","IMPRINT",EDGE,{"derivedFrom":sQuery(id+"F0.wireOp",EDGE,"E364")}),1.0]])]});
            extrude(context, id + "F3", {"entities" : qUnion([Q0]), "depth" : 18 * mm});
        }
        {
            var Q0;
            Q0=makeQuery(id+"F0.imprint","IMPRINT",FACE,{"disambiguationData":[TD([[makeQuery(id+"F0.imprint","IMPRINT",EDGE,{"derivedFrom":sQuery(id+"F0.wireOp",EDGE,"E368")}),1.0]])]});
            extrude(context, id + "F4", {"entities" : qUnion([Q0]), "depth" : 18 * mm});
        }
        {
            var Q0;
            Q0=qCreatedBy(makeId("Front.planeOp"),FACE);
            var sketch = newSketch(context, id + "F5", { "sketchPlane" : qUnion([Q0])});
            skLineSegment(sketch, "E2339", {"start": v(1848.7, 331.22) * mm, "end": v(1848.7, 1983.98) * mm});
            skLineSegment(sketch, "E2340", {"start": v(1848.7, 1983.98) * mm, "end": v(2070.8, 1983.98) * mm});
            skLineSegment(sketch, "E2341", {"start": v(2070.8, 1983.98) * mm, "end": v(2070.8, 331.22) * mm});
            skLineSegment(sketch, "E2342", {"start": v(2070.8, 331.22) * mm, "end": v(1848.7, 331.22) * mm});
            skLineSegment(sketch, "E2343", {"start": v(1518, 0) * mm, "end": v(2718, 0) * mm});
            skLineSegment(sketch, "E2344", {"start": v(2718, 0) * mm, "end": v(2718, 2400) * mm});
            skLineSegment(sketch, "E2345", {"start": v(2718, 2400) * mm, "end": v(1518, 2400) * mm});
            skLineSegment(sketch, "E2346", {"start": v(1518, 2400) * mm, "end": v(1518, 0) * mm});
            skLineSegment(sketch, "E2347", {"start": v(1546.2, 148.14) * mm, "end": v(1561.2, 148.14) * mm});
            skArc(sketch, "E2348", {"start": v(1561.2, 148.14) * mm, "mid": v(1564.21, 145.13) * mm, "end": v(1561.2, 142.12) * mm});
            skLineSegment(sketch, "E2349", {"start": v(1561.2, 142.12) * mm, "end": v(1561.2, 67.16) * mm});
            skArc(sketch, "E2350", {"start": v(1561.2, 67.16) * mm, "mid": v(1564.21, 64.15) * mm, "end": v(1561.2, 61.14) * mm});
            skLineSegment(sketch, "E2351", {"start": v(1561.2, 61.14) * mm, "end": v(1543.2, 61.14) * mm});
            skLineSegment(sketch, "E2352", {"start": v(1543.2, 61.14) * mm, "end": v(1543.2, 43.14) * mm});
            skLineSegment(sketch, "E2353", {"start": v(1543.2, 43.14) * mm, "end": v(1561.2, 43.14) * mm});
            skArc(sketch, "E2354", {"start": v(1561.2, 43.14) * mm, "mid": v(1564.21, 40.13) * mm, "end": v(1561.2, 37.12) * mm});
            skLineSegment(sketch, "E2355", {"start": v(1561.2, 37.12) * mm, "end": v(1561.2, 25.14) * mm});
            skLineSegment(sketch, "E2356", {"start": v(1561.2, 25.14) * mm, "end": v(1592.2, 25.14) * mm});
            skLineSegment(sketch, "E2357", {"start": v(1592.2, 25.14) * mm, "end": v(1592.2, 61.14) * mm});
            skArc(sketch, "E2358", {"start": v(1592.2, 61.14) * mm, "mid": v(1595.21, 64.15) * mm, "end": v(1598.22, 61.14) * mm});
            skLineSegment(sketch, "E2359", {"start": v(1598.22, 61.14) * mm, "end": v(1638.18, 61.14) * mm});
            skArc(sketch, "E2360", {"start": v(1638.18, 61.14) * mm, "mid": v(1641.2, 64.15) * mm, "end": v(1644.2, 61.14) * mm});
            skLineSegment(sketch, "E2361", {"start": v(1644.2, 61.14) * mm, "end": v(1644.2, 25.14) * mm});
            skLineSegment(sketch, "E2362", {"start": v(1644.2, 25.14) * mm, "end": v(1675.2, 25.14) * mm});
            skLineSegment(sketch, "E2363", {"start": v(1675.2, 25.14) * mm, "end": v(1675.2, 37.12) * mm});
            skArc(sketch, "E2364", {"start": v(1675.2, 37.12) * mm, "mid": v(1672.2, 40.13) * mm, "end": v(1675.2, 43.14) * mm});
            skLineSegment(sketch, "E2365", {"start": v(1675.2, 43.14) * mm, "end": v(1693.2, 43.14) * mm});
            skLineSegment(sketch, "E2366", {"start": v(1693.2, 43.14) * mm, "end": v(1693.2, 61.14) * mm});
            skLineSegment(sketch, "E2367", {"start": v(1693.2, 61.14) * mm, "end": v(1675.2, 61.14) * mm});
            skArc(sketch, "E2368", {"start": v(1675.2, 61.14) * mm, "mid": v(1672.2, 64.15) * mm, "end": v(1675.2, 67.16) * mm});
            skLineSegment(sketch, "E2369", {"start": v(1675.2, 67.16) * mm, "end": v(1675.2, 142.12) * mm});
            skArc(sketch, "E2370", {"start": v(1675.2, 142.12) * mm, "mid": v(1672.2, 145.13) * mm, "end": v(1675.2, 148.14) * mm});
            skLineSegment(sketch, "E2371", {"start": v(1675.2, 148.14) * mm, "end": v(1690.2, 148.14) * mm});
            skLineSegment(sketch, "E2372", {"start": v(1690.2, 148.14) * mm, "end": v(1693.2, 151.14) * mm});
            skLineSegment(sketch, "E2373", {"start": v(1693.2, 151.14) * mm, "end": v(1693.2, 185.14) * mm});
            skLineSegment(sketch, "E2374", {"start": v(1693.2, 185.14) * mm, "end": v(1690.2, 188.14) * mm});
            skLineSegment(sketch, "E2375", {"start": v(1690.2, 188.14) * mm, "end": v(1675.2, 188.14) * mm});
            skArc(sketch, "E2376", {"start": v(1675.2, 188.14) * mm, "mid": v(1672.2, 191.15) * mm, "end": v(1675.2, 194.16) * mm});
            skLineSegment(sketch, "E2377", {"start": v(1675.2, 194.16) * mm, "end": v(1675.2, 269.12) * mm});
            skArc(sketch, "E2378", {"start": v(1675.2, 269.12) * mm, "mid": v(1672.2, 272.13) * mm, "end": v(1675.2, 275.14) * mm});
            skLineSegment(sketch, "E2379", {"start": v(1675.2, 275.14) * mm, "end": v(1693.2, 275.14) * mm});
            skLineSegment(sketch, "E2380", {"start": v(1693.2, 275.14) * mm, "end": v(1693.2, 293.14) * mm});
            skLineSegment(sketch, "E2381", {"start": v(1693.2, 293.14) * mm, "end": v(1675.2, 293.14) * mm});
            skArc(sketch, "E2382", {"start": v(1675.2, 293.14) * mm, "mid": v(1672.2, 296.15) * mm, "end": v(1675.2, 299.16) * mm});
            skLineSegment(sketch, "E2383", {"start": v(1675.2, 299.16) * mm, "end": v(1675.2, 311.14) * mm});
            skLineSegment(sketch, "E2384", {"start": v(1675.2, 311.14) * mm, "end": v(1644.2, 311.14) * mm});
            skLineSegment(sketch, "E2385", {"start": v(1644.2, 311.14) * mm, "end": v(1644.2, 275.18) * mm});
            skArc(sketch, "E2386", {"start": v(1644.2, 275.18) * mm, "mid": v(1641.2, 272.17) * mm, "end": v(1638.18, 275.18) * mm});
            skLineSegment(sketch, "E2387", {"start": v(1638.18, 275.18) * mm, "end": v(1598.22, 275.18) * mm});
            skArc(sketch, "E2388", {"start": v(1598.22, 275.18) * mm, "mid": v(1595.21, 272.17) * mm, "end": v(1592.2, 275.18) * mm});
            skLineSegment(sketch, "E2389", {"start": v(1592.2, 275.18) * mm, "end": v(1592.2, 311.14) * mm});
            skLineSegment(sketch, "E2390", {"start": v(1592.2, 311.14) * mm, "end": v(1561.2, 311.14) * mm});
            skLineSegment(sketch, "E2391", {"start": v(1561.2, 311.14) * mm, "end": v(1561.2, 299.16) * mm});
            skArc(sketch, "E2392", {"start": v(1561.2, 299.16) * mm, "mid": v(1564.21, 296.15) * mm, "end": v(1561.2, 293.14) * mm});
            skLineSegment(sketch, "E2393", {"start": v(1561.2, 293.14) * mm, "end": v(1543.2, 293.14) * mm});
            skLineSegment(sketch, "E2394", {"start": v(1543.2, 293.14) * mm, "end": v(1543.2, 275.14) * mm});
            skLineSegment(sketch, "E2395", {"start": v(1543.2, 275.14) * mm, "end": v(1561.2, 275.14) * mm});
            skArc(sketch, "E2396", {"start": v(1561.2, 275.14) * mm, "mid": v(1564.21, 272.13) * mm, "end": v(1561.2, 269.12) * mm});
            skLineSegment(sketch, "E2397", {"start": v(1561.2, 269.12) * mm, "end": v(1561.2, 194.16) * mm});
            skArc(sketch, "E2398", {"start": v(1561.2, 194.16) * mm, "mid": v(1564.21, 191.15) * mm, "end": v(1561.2, 188.14) * mm});
            skLineSegment(sketch, "E2399", {"start": v(1561.2, 188.14) * mm, "end": v(1546.2, 188.14) * mm});
            skLineSegment(sketch, "E2400", {"start": v(1546.2, 188.14) * mm, "end": v(1543.2, 185.14) * mm});
            skLineSegment(sketch, "E2401", {"start": v(1543.2, 185.14) * mm, "end": v(1543.2, 151.14) * mm});
            skLineSegment(sketch, "E2402", {"start": v(1543.2, 151.14) * mm, "end": v(1546.2, 148.14) * mm});
            skLineSegment(sketch, "E2403", {"start": v(1546.2, 455.17) * mm, "end": v(1561.2, 455.17) * mm});
            skArc(sketch, "E2404", {"start": v(1561.2, 455.17) * mm, "mid": v(1564.21, 452.16) * mm, "end": v(1561.2, 449.15) * mm});
            skLineSegment(sketch, "E2405", {"start": v(1561.2, 449.15) * mm, "end": v(1561.2, 374.19) * mm});
            skArc(sketch, "E2406", {"start": v(1561.2, 374.19) * mm, "mid": v(1564.21, 371.18) * mm, "end": v(1561.2, 368.17) * mm});
            skLineSegment(sketch, "E2407", {"start": v(1561.2, 368.17) * mm, "end": v(1543.2, 368.17) * mm});
            skLineSegment(sketch, "E2408", {"start": v(1543.2, 368.17) * mm, "end": v(1543.2, 350.17) * mm});
            skLineSegment(sketch, "E2409", {"start": v(1543.2, 350.17) * mm, "end": v(1561.2, 350.17) * mm});
            skArc(sketch, "E2410", {"start": v(1561.2, 350.17) * mm, "mid": v(1564.21, 347.16) * mm, "end": v(1561.2, 344.15) * mm});
            skLineSegment(sketch, "E2411", {"start": v(1561.2, 344.15) * mm, "end": v(1561.2, 332.17) * mm});
            skLineSegment(sketch, "E2412", {"start": v(1561.2, 332.17) * mm, "end": v(1592.2, 332.17) * mm});
            skLineSegment(sketch, "E2413", {"start": v(1592.2, 332.17) * mm, "end": v(1592.2, 368.17) * mm});
            skArc(sketch, "E2414", {"start": v(1592.2, 368.17) * mm, "mid": v(1595.21, 371.18) * mm, "end": v(1598.22, 368.17) * mm});
            skLineSegment(sketch, "E2415", {"start": v(1598.22, 368.17) * mm, "end": v(1638.18, 368.17) * mm});
            skArc(sketch, "E2416", {"start": v(1638.18, 368.17) * mm, "mid": v(1641.2, 371.18) * mm, "end": v(1644.2, 368.17) * mm});
            skLineSegment(sketch, "E2417", {"start": v(1644.2, 368.17) * mm, "end": v(1644.2, 332.17) * mm});
            skLineSegment(sketch, "E2418", {"start": v(1644.2, 332.17) * mm, "end": v(1675.2, 332.17) * mm});
            skLineSegment(sketch, "E2419", {"start": v(1675.2, 332.17) * mm, "end": v(1675.2, 344.15) * mm});
            skArc(sketch, "E2420", {"start": v(1675.2, 344.15) * mm, "mid": v(1672.2, 347.16) * mm, "end": v(1675.2, 350.17) * mm});
            skLineSegment(sketch, "E2421", {"start": v(1675.2, 350.17) * mm, "end": v(1693.2, 350.17) * mm});
            skLineSegment(sketch, "E2422", {"start": v(1693.2, 350.17) * mm, "end": v(1693.2, 368.17) * mm});
            skLineSegment(sketch, "E2423", {"start": v(1693.2, 368.17) * mm, "end": v(1675.2, 368.17) * mm});
            skArc(sketch, "E2424", {"start": v(1675.2, 368.17) * mm, "mid": v(1672.2, 371.18) * mm, "end": v(1675.2, 374.19) * mm});
            skLineSegment(sketch, "E2425", {"start": v(1675.2, 374.19) * mm, "end": v(1675.2, 449.15) * mm});
            skArc(sketch, "E2426", {"start": v(1675.2, 449.15) * mm, "mid": v(1672.2, 452.16) * mm, "end": v(1675.2, 455.17) * mm});
            skLineSegment(sketch, "E2427", {"start": v(1675.2, 455.17) * mm, "end": v(1690.2, 455.17) * mm});
            skLineSegment(sketch, "E2428", {"start": v(1690.2, 455.17) * mm, "end": v(1693.2, 458.17) * mm});
            skLineSegment(sketch, "E2429", {"start": v(1693.2, 458.17) * mm, "end": v(1693.2, 492.17) * mm});
            skLineSegment(sketch, "E2430", {"start": v(1693.2, 492.17) * mm, "end": v(1690.2, 495.17) * mm});
            skLineSegment(sketch, "E2431", {"start": v(1690.2, 495.17) * mm, "end": v(1675.2, 495.17) * mm});
            skArc(sketch, "E2432", {"start": v(1675.2, 495.17) * mm, "mid": v(1672.2, 498.18) * mm, "end": v(1675.2, 501.19) * mm});
            skLineSegment(sketch, "E2433", {"start": v(1675.2, 501.19) * mm, "end": v(1675.2, 576.15) * mm});
            skArc(sketch, "E2434", {"start": v(1675.2, 576.15) * mm, "mid": v(1672.2, 579.16) * mm, "end": v(1675.2, 582.17) * mm});
            skLineSegment(sketch, "E2435", {"start": v(1675.2, 582.17) * mm, "end": v(1693.2, 582.17) * mm});
            skLineSegment(sketch, "E2436", {"start": v(1693.2, 582.17) * mm, "end": v(1693.2, 600.17) * mm});
            skLineSegment(sketch, "E2437", {"start": v(1693.2, 600.17) * mm, "end": v(1675.2, 600.17) * mm});
            skArc(sketch, "E2438", {"start": v(1675.2, 600.17) * mm, "mid": v(1672.2, 603.18) * mm, "end": v(1675.2, 606.19) * mm});
            skLineSegment(sketch, "E2439", {"start": v(1675.2, 606.19) * mm, "end": v(1675.2, 618.17) * mm});
            skLineSegment(sketch, "E2440", {"start": v(1675.2, 618.17) * mm, "end": v(1644.2, 618.17) * mm});
            skLineSegment(sketch, "E2441", {"start": v(1644.2, 618.17) * mm, "end": v(1644.2, 582.2) * mm});
            skArc(sketch, "E2442", {"start": v(1644.2, 582.2) * mm, "mid": v(1641.2, 579.2) * mm, "end": v(1638.18, 582.2) * mm});
            skLineSegment(sketch, "E2443", {"start": v(1638.18, 582.2) * mm, "end": v(1598.22, 582.2) * mm});
            skArc(sketch, "E2444", {"start": v(1598.22, 582.2) * mm, "mid": v(1595.21, 579.2) * mm, "end": v(1592.2, 582.2) * mm});
            skLineSegment(sketch, "E2445", {"start": v(1592.2, 582.2) * mm, "end": v(1592.2, 618.17) * mm});
            skLineSegment(sketch, "E2446", {"start": v(1592.2, 618.17) * mm, "end": v(1561.2, 618.17) * mm});
            skLineSegment(sketch, "E2447", {"start": v(1561.2, 618.17) * mm, "end": v(1561.2, 606.19) * mm});
            skArc(sketch, "E2448", {"start": v(1561.2, 606.19) * mm, "mid": v(1564.21, 603.18) * mm, "end": v(1561.2, 600.17) * mm});
            skLineSegment(sketch, "E2449", {"start": v(1561.2, 600.17) * mm, "end": v(1543.2, 600.17) * mm});
            skLineSegment(sketch, "E2450", {"start": v(1543.2, 600.17) * mm, "end": v(1543.2, 582.17) * mm});
            skLineSegment(sketch, "E2451", {"start": v(1543.2, 582.17) * mm, "end": v(1561.2, 582.17) * mm});
            skArc(sketch, "E2452", {"start": v(1561.2, 582.17) * mm, "mid": v(1564.21, 579.16) * mm, "end": v(1561.2, 576.15) * mm});
            skLineSegment(sketch, "E2453", {"start": v(1561.2, 576.15) * mm, "end": v(1561.2, 501.19) * mm});
            skArc(sketch, "E2454", {"start": v(1561.2, 501.19) * mm, "mid": v(1564.21, 498.18) * mm, "end": v(1561.2, 495.17) * mm});
            skLineSegment(sketch, "E2455", {"start": v(1561.2, 495.17) * mm, "end": v(1546.2, 495.17) * mm});
            skLineSegment(sketch, "E2456", {"start": v(1546.2, 495.17) * mm, "end": v(1543.2, 492.17) * mm});
            skLineSegment(sketch, "E2457", {"start": v(1543.2, 492.17) * mm, "end": v(1543.2, 458.17) * mm});
            skLineSegment(sketch, "E2458", {"start": v(1543.2, 458.17) * mm, "end": v(1546.2, 455.17) * mm});
            skLineSegment(sketch, "E2459", {"start": v(2546.2, 2212.14) * mm, "end": v(2561.2, 2212.14) * mm});
            skArc(sketch, "E2460", {"start": v(2561.2, 2212.14) * mm, "mid": v(2564.21, 2209.13) * mm, "end": v(2561.2, 2206.12) * mm});
            skLineSegment(sketch, "E2461", {"start": v(2561.2, 2206.12) * mm, "end": v(2561.2, 2131.16) * mm});
            skArc(sketch, "E2462", {"start": v(2561.2, 2131.16) * mm, "mid": v(2564.21, 2128.15) * mm, "end": v(2561.2, 2125.14) * mm});
            skLineSegment(sketch, "E2463", {"start": v(2561.2, 2125.14) * mm, "end": v(2543.2, 2125.14) * mm});
            skLineSegment(sketch, "E2464", {"start": v(2543.2, 2125.14) * mm, "end": v(2543.2, 2107.14) * mm});
            skLineSegment(sketch, "E2465", {"start": v(2543.2, 2107.14) * mm, "end": v(2561.2, 2107.14) * mm});
            skArc(sketch, "E2466", {"start": v(2561.2, 2107.14) * mm, "mid": v(2564.21, 2104.13) * mm, "end": v(2561.2, 2101.12) * mm});
            skLineSegment(sketch, "E2467", {"start": v(2561.2, 2101.12) * mm, "end": v(2561.2, 2089.14) * mm});
            skLineSegment(sketch, "E2468", {"start": v(2561.2, 2089.14) * mm, "end": v(2592.2, 2089.14) * mm});
            skLineSegment(sketch, "E2469", {"start": v(2592.2, 2089.14) * mm, "end": v(2592.2, 2125.14) * mm});
            skArc(sketch, "E2470", {"start": v(2592.2, 2125.14) * mm, "mid": v(2595.21, 2128.15) * mm, "end": v(2598.22, 2125.14) * mm});
            skLineSegment(sketch, "E2471", {"start": v(2598.22, 2125.14) * mm, "end": v(2638.18, 2125.14) * mm});
            skArc(sketch, "E2472", {"start": v(2638.18, 2125.14) * mm, "mid": v(2641.2, 2128.15) * mm, "end": v(2644.2, 2125.14) * mm});
            skLineSegment(sketch, "E2473", {"start": v(2644.2, 2125.14) * mm, "end": v(2644.2, 2089.14) * mm});
            skLineSegment(sketch, "E2474", {"start": v(2644.2, 2089.14) * mm, "end": v(2675.2, 2089.14) * mm});
            skLineSegment(sketch, "E2475", {"start": v(2675.2, 2089.14) * mm, "end": v(2675.2, 2101.12) * mm});
            skArc(sketch, "E2476", {"start": v(2675.2, 2101.12) * mm, "mid": v(2672.2, 2104.13) * mm, "end": v(2675.2, 2107.14) * mm});
            skLineSegment(sketch, "E2477", {"start": v(2675.2, 2107.14) * mm, "end": v(2693.2, 2107.14) * mm});
            skLineSegment(sketch, "E2478", {"start": v(2693.2, 2107.14) * mm, "end": v(2693.2, 2125.14) * mm});
            skLineSegment(sketch, "E2479", {"start": v(2693.2, 2125.14) * mm, "end": v(2675.2, 2125.14) * mm});
            skArc(sketch, "E2480", {"start": v(2675.2, 2125.14) * mm, "mid": v(2672.2, 2128.15) * mm, "end": v(2675.2, 2131.16) * mm});
            skLineSegment(sketch, "E2481", {"start": v(2675.2, 2131.16) * mm, "end": v(2675.2, 2206.12) * mm});
            skArc(sketch, "E2482", {"start": v(2675.2, 2206.12) * mm, "mid": v(2672.2, 2209.13) * mm, "end": v(2675.2, 2212.14) * mm});
            skLineSegment(sketch, "E2483", {"start": v(2675.2, 2212.14) * mm, "end": v(2690.2, 2212.14) * mm});
            skLineSegment(sketch, "E2484", {"start": v(2690.2, 2212.14) * mm, "end": v(2693.2, 2215.14) * mm});
            skLineSegment(sketch, "E2485", {"start": v(2693.2, 2215.14) * mm, "end": v(2693.2, 2249.14) * mm});
            skLineSegment(sketch, "E2486", {"start": v(2693.2, 2249.14) * mm, "end": v(2690.2, 2252.14) * mm});
            skLineSegment(sketch, "E2487", {"start": v(2690.2, 2252.14) * mm, "end": v(2675.2, 2252.14) * mm});
            skArc(sketch, "E2488", {"start": v(2675.2, 2252.14) * mm, "mid": v(2672.2, 2255.15) * mm, "end": v(2675.2, 2258.16) * mm});
            skLineSegment(sketch, "E2489", {"start": v(2675.2, 2258.16) * mm, "end": v(2675.2, 2333.12) * mm});
            skArc(sketch, "E2490", {"start": v(2675.2, 2333.12) * mm, "mid": v(2672.2, 2336.13) * mm, "end": v(2675.2, 2339.14) * mm});
            skLineSegment(sketch, "E2491", {"start": v(2675.2, 2339.14) * mm, "end": v(2693.2, 2339.14) * mm});
            skLineSegment(sketch, "E2492", {"start": v(2693.2, 2339.14) * mm, "end": v(2693.2, 2357.14) * mm});
            skLineSegment(sketch, "E2493", {"start": v(2693.2, 2357.14) * mm, "end": v(2675.2, 2357.14) * mm});
            skArc(sketch, "E2494", {"start": v(2675.2, 2357.14) * mm, "mid": v(2672.2, 2360.15) * mm, "end": v(2675.2, 2363.16) * mm});
            skLineSegment(sketch, "E2495", {"start": v(2675.2, 2363.16) * mm, "end": v(2675.2, 2375.14) * mm});
            skLineSegment(sketch, "E2496", {"start": v(2675.2, 2375.14) * mm, "end": v(2644.2, 2375.14) * mm});
            skLineSegment(sketch, "E2497", {"start": v(2644.2, 2375.14) * mm, "end": v(2644.2, 2339.18) * mm});
            skArc(sketch, "E2498", {"start": v(2644.2, 2339.18) * mm, "mid": v(2641.2, 2336.17) * mm, "end": v(2638.18, 2339.18) * mm});
            skLineSegment(sketch, "E2499", {"start": v(2638.18, 2339.18) * mm, "end": v(2598.22, 2339.18) * mm});
            skArc(sketch, "E2500", {"start": v(2598.22, 2339.18) * mm, "mid": v(2595.21, 2336.17) * mm, "end": v(2592.2, 2339.18) * mm});
            skLineSegment(sketch, "E2501", {"start": v(2592.2, 2339.18) * mm, "end": v(2592.2, 2375.14) * mm});
            skLineSegment(sketch, "E2502", {"start": v(2592.2, 2375.14) * mm, "end": v(2561.2, 2375.14) * mm});
            skLineSegment(sketch, "E2503", {"start": v(2561.2, 2375.14) * mm, "end": v(2561.2, 2363.16) * mm});
            skArc(sketch, "E2504", {"start": v(2561.2, 2363.16) * mm, "mid": v(2564.21, 2360.15) * mm, "end": v(2561.2, 2357.14) * mm});
            skLineSegment(sketch, "E2505", {"start": v(2561.2, 2357.14) * mm, "end": v(2543.2, 2357.14) * mm});
            skLineSegment(sketch, "E2506", {"start": v(2543.2, 2357.14) * mm, "end": v(2543.2, 2339.14) * mm});
            skLineSegment(sketch, "E2507", {"start": v(2543.2, 2339.14) * mm, "end": v(2561.2, 2339.14) * mm});
            skArc(sketch, "E2508", {"start": v(2561.2, 2339.14) * mm, "mid": v(2564.21, 2336.13) * mm, "end": v(2561.2, 2333.12) * mm});
            skLineSegment(sketch, "E2509", {"start": v(2561.2, 2333.12) * mm, "end": v(2561.2, 2258.16) * mm});
            skArc(sketch, "E2510", {"start": v(2561.2, 2258.16) * mm, "mid": v(2564.21, 2255.15) * mm, "end": v(2561.2, 2252.14) * mm});
            skLineSegment(sketch, "E2511", {"start": v(2561.2, 2252.14) * mm, "end": v(2546.2, 2252.14) * mm});
            skLineSegment(sketch, "E2512", {"start": v(2546.2, 2252.14) * mm, "end": v(2543.2, 2249.14) * mm});
            skLineSegment(sketch, "E2513", {"start": v(2543.2, 2249.14) * mm, "end": v(2543.2, 2215.14) * mm});
            skLineSegment(sketch, "E2514", {"start": v(2543.2, 2215.14) * mm, "end": v(2546.2, 2212.14) * mm});
            skLineSegment(sketch, "E2515", {"start": v(2546.2, 1905.53) * mm, "end": v(2561.2, 1905.53) * mm});
            skArc(sketch, "E2516", {"start": v(2561.2, 1905.53) * mm, "mid": v(2564.21, 1902.52) * mm, "end": v(2561.2, 1899.5) * mm});
            skLineSegment(sketch, "E2517", {"start": v(2561.2, 1899.5) * mm, "end": v(2561.2, 1824.55) * mm});
            skArc(sketch, "E2518", {"start": v(2561.2, 1824.55) * mm, "mid": v(2564.21, 1821.54) * mm, "end": v(2561.2, 1818.53) * mm});
            skLineSegment(sketch, "E2519", {"start": v(2561.2, 1818.53) * mm, "end": v(2543.2, 1818.53) * mm});
            skLineSegment(sketch, "E2520", {"start": v(2543.2, 1818.53) * mm, "end": v(2543.2, 1800.53) * mm});
            skLineSegment(sketch, "E2521", {"start": v(2543.2, 1800.53) * mm, "end": v(2561.2, 1800.53) * mm});
            skArc(sketch, "E2522", {"start": v(2561.2, 1800.53) * mm, "mid": v(2564.21, 1797.52) * mm, "end": v(2561.2, 1794.5) * mm});
            skLineSegment(sketch, "E2523", {"start": v(2561.2, 1794.5) * mm, "end": v(2561.2, 1782.53) * mm});
            skLineSegment(sketch, "E2524", {"start": v(2561.2, 1782.53) * mm, "end": v(2592.2, 1782.53) * mm});
            skLineSegment(sketch, "E2525", {"start": v(2592.2, 1782.53) * mm, "end": v(2592.2, 1818.53) * mm});
            skArc(sketch, "E2526", {"start": v(2592.2, 1818.53) * mm, "mid": v(2595.21, 1821.54) * mm, "end": v(2598.22, 1818.53) * mm});
            skLineSegment(sketch, "E2527", {"start": v(2598.22, 1818.53) * mm, "end": v(2638.18, 1818.53) * mm});
            skArc(sketch, "E2528", {"start": v(2638.18, 1818.53) * mm, "mid": v(2641.2, 1821.54) * mm, "end": v(2644.2, 1818.53) * mm});
            skLineSegment(sketch, "E2529", {"start": v(2644.2, 1818.53) * mm, "end": v(2644.2, 1782.53) * mm});
            skLineSegment(sketch, "E2530", {"start": v(2644.2, 1782.53) * mm, "end": v(2675.2, 1782.53) * mm});
            skLineSegment(sketch, "E2531", {"start": v(2675.2, 1782.53) * mm, "end": v(2675.2, 1794.5) * mm});
            skArc(sketch, "E2532", {"start": v(2675.2, 1794.5) * mm, "mid": v(2672.2, 1797.52) * mm, "end": v(2675.2, 1800.53) * mm});
            skLineSegment(sketch, "E2533", {"start": v(2675.2, 1800.53) * mm, "end": v(2693.2, 1800.53) * mm});
            skLineSegment(sketch, "E2534", {"start": v(2693.2, 1800.53) * mm, "end": v(2693.2, 1818.53) * mm});
            skLineSegment(sketch, "E2535", {"start": v(2693.2, 1818.53) * mm, "end": v(2675.2, 1818.53) * mm});
            skArc(sketch, "E2536", {"start": v(2675.2, 1818.53) * mm, "mid": v(2672.2, 1821.54) * mm, "end": v(2675.2, 1824.55) * mm});
            skLineSegment(sketch, "E2537", {"start": v(2675.2, 1824.55) * mm, "end": v(2675.2, 1899.5) * mm});
            skArc(sketch, "E2538", {"start": v(2675.2, 1899.5) * mm, "mid": v(2672.2, 1902.52) * mm, "end": v(2675.2, 1905.53) * mm});
            skLineSegment(sketch, "E2539", {"start": v(2675.2, 1905.53) * mm, "end": v(2690.2, 1905.53) * mm});
            skLineSegment(sketch, "E2540", {"start": v(2690.2, 1905.53) * mm, "end": v(2693.2, 1908.53) * mm});
            skLineSegment(sketch, "E2541", {"start": v(2693.2, 1908.53) * mm, "end": v(2693.2, 1942.53) * mm});
            skLineSegment(sketch, "E2542", {"start": v(2693.2, 1942.53) * mm, "end": v(2690.2, 1945.53) * mm});
            skLineSegment(sketch, "E2543", {"start": v(2690.2, 1945.53) * mm, "end": v(2675.2, 1945.53) * mm});
            skArc(sketch, "E2544", {"start": v(2675.2, 1945.53) * mm, "mid": v(2672.2, 1948.54) * mm, "end": v(2675.2, 1951.55) * mm});
            skLineSegment(sketch, "E2545", {"start": v(2675.2, 1951.55) * mm, "end": v(2675.2, 2026.5) * mm});
            skArc(sketch, "E2546", {"start": v(2675.2, 2026.5) * mm, "mid": v(2672.2, 2029.52) * mm, "end": v(2675.2, 2032.53) * mm});
            skLineSegment(sketch, "E2547", {"start": v(2675.2, 2032.53) * mm, "end": v(2693.2, 2032.53) * mm});
            skLineSegment(sketch, "E2548", {"start": v(2693.2, 2032.53) * mm, "end": v(2693.2, 2050.53) * mm});
            skLineSegment(sketch, "E2549", {"start": v(2693.2, 2050.53) * mm, "end": v(2675.2, 2050.53) * mm});
            skArc(sketch, "E2550", {"start": v(2675.2, 2050.53) * mm, "mid": v(2672.2, 2053.54) * mm, "end": v(2675.2, 2056.55) * mm});
            skLineSegment(sketch, "E2551", {"start": v(2675.2, 2056.55) * mm, "end": v(2675.2, 2068.53) * mm});
            skLineSegment(sketch, "E2552", {"start": v(2675.2, 2068.53) * mm, "end": v(2644.2, 2068.53) * mm});
            skLineSegment(sketch, "E2553", {"start": v(2644.2, 2068.53) * mm, "end": v(2644.2, 2032.57) * mm});
            skArc(sketch, "E2554", {"start": v(2644.2, 2032.57) * mm, "mid": v(2641.2, 2029.56) * mm, "end": v(2638.18, 2032.57) * mm});
            skLineSegment(sketch, "E2555", {"start": v(2638.18, 2032.57) * mm, "end": v(2598.22, 2032.57) * mm});
            skArc(sketch, "E2556", {"start": v(2598.22, 2032.57) * mm, "mid": v(2595.21, 2029.56) * mm, "end": v(2592.2, 2032.57) * mm});
            skLineSegment(sketch, "E2557", {"start": v(2592.2, 2032.57) * mm, "end": v(2592.2, 2068.53) * mm});
            skLineSegment(sketch, "E2558", {"start": v(2592.2, 2068.53) * mm, "end": v(2561.2, 2068.53) * mm});
            skLineSegment(sketch, "E2559", {"start": v(2561.2, 2068.53) * mm, "end": v(2561.2, 2056.55) * mm});
            skArc(sketch, "E2560", {"start": v(2561.2, 2056.55) * mm, "mid": v(2564.21, 2053.54) * mm, "end": v(2561.2, 2050.53) * mm});
            skLineSegment(sketch, "E2561", {"start": v(2561.2, 2050.53) * mm, "end": v(2543.2, 2050.53) * mm});
            skLineSegment(sketch, "E2562", {"start": v(2543.2, 2050.53) * mm, "end": v(2543.2, 2032.53) * mm});
            skLineSegment(sketch, "E2563", {"start": v(2543.2, 2032.53) * mm, "end": v(2561.2, 2032.53) * mm});
            skArc(sketch, "E2564", {"start": v(2561.2, 2032.53) * mm, "mid": v(2564.21, 2029.52) * mm, "end": v(2561.2, 2026.5) * mm});
            skLineSegment(sketch, "E2565", {"start": v(2561.2, 2026.5) * mm, "end": v(2561.2, 1951.55) * mm});
            skArc(sketch, "E2566", {"start": v(2561.2, 1951.55) * mm, "mid": v(2564.21, 1948.54) * mm, "end": v(2561.2, 1945.53) * mm});
            skLineSegment(sketch, "E2567", {"start": v(2561.2, 1945.53) * mm, "end": v(2546.2, 1945.53) * mm});
            skLineSegment(sketch, "E2568", {"start": v(2546.2, 1945.53) * mm, "end": v(2543.2, 1942.53) * mm});
            skLineSegment(sketch, "E2569", {"start": v(2543.2, 1942.53) * mm, "end": v(2543.2, 1908.53) * mm});
            skLineSegment(sketch, "E2570", {"start": v(2543.2, 1908.53) * mm, "end": v(2546.2, 1905.53) * mm});
            skLineSegment(sketch, "E2571", {"start": v(2376.2, 1905.53) * mm, "end": v(2391.2, 1905.53) * mm});
            skArc(sketch, "E2572", {"start": v(2391.2, 1905.53) * mm, "mid": v(2394.21, 1902.52) * mm, "end": v(2391.2, 1899.5) * mm});
            skLineSegment(sketch, "E2573", {"start": v(2391.2, 1899.5) * mm, "end": v(2391.2, 1824.55) * mm});
            skArc(sketch, "E2574", {"start": v(2391.2, 1824.55) * mm, "mid": v(2394.21, 1821.54) * mm, "end": v(2391.2, 1818.53) * mm});
            skLineSegment(sketch, "E2575", {"start": v(2391.2, 1818.53) * mm, "end": v(2373.2, 1818.53) * mm});
            skLineSegment(sketch, "E2576", {"start": v(2373.2, 1818.53) * mm, "end": v(2373.2, 1800.53) * mm});
            skLineSegment(sketch, "E2577", {"start": v(2373.2, 1800.53) * mm, "end": v(2391.2, 1800.53) * mm});
            skArc(sketch, "E2578", {"start": v(2391.2, 1800.53) * mm, "mid": v(2394.21, 1797.52) * mm, "end": v(2391.2, 1794.5) * mm});
            skLineSegment(sketch, "E2579", {"start": v(2391.2, 1794.5) * mm, "end": v(2391.2, 1782.53) * mm});
            skLineSegment(sketch, "E2580", {"start": v(2391.2, 1782.53) * mm, "end": v(2422.2, 1782.53) * mm});
            skLineSegment(sketch, "E2581", {"start": v(2422.2, 1782.53) * mm, "end": v(2422.2, 1818.53) * mm});
            skArc(sketch, "E2582", {"start": v(2422.2, 1818.53) * mm, "mid": v(2425.21, 1821.54) * mm, "end": v(2428.22, 1818.53) * mm});
            skLineSegment(sketch, "E2583", {"start": v(2428.22, 1818.53) * mm, "end": v(2468.18, 1818.53) * mm});
            skArc(sketch, "E2584", {"start": v(2468.18, 1818.53) * mm, "mid": v(2471.2, 1821.54) * mm, "end": v(2474.2, 1818.53) * mm});
            skLineSegment(sketch, "E2585", {"start": v(2474.2, 1818.53) * mm, "end": v(2474.2, 1782.53) * mm});
            skLineSegment(sketch, "E2586", {"start": v(2474.2, 1782.53) * mm, "end": v(2505.2, 1782.53) * mm});
            skLineSegment(sketch, "E2587", {"start": v(2505.2, 1782.53) * mm, "end": v(2505.2, 1794.5) * mm});
            skArc(sketch, "E2588", {"start": v(2505.2, 1794.5) * mm, "mid": v(2502.2, 1797.52) * mm, "end": v(2505.2, 1800.53) * mm});
            skLineSegment(sketch, "E2589", {"start": v(2505.2, 1800.53) * mm, "end": v(2523.2, 1800.53) * mm});
            skLineSegment(sketch, "E2590", {"start": v(2523.2, 1800.53) * mm, "end": v(2523.2, 1818.53) * mm});
            skLineSegment(sketch, "E2591", {"start": v(2523.2, 1818.53) * mm, "end": v(2505.2, 1818.53) * mm});
            skArc(sketch, "E2592", {"start": v(2505.2, 1818.53) * mm, "mid": v(2502.2, 1821.54) * mm, "end": v(2505.2, 1824.55) * mm});
            skLineSegment(sketch, "E2593", {"start": v(2505.2, 1824.55) * mm, "end": v(2505.2, 1899.5) * mm});
            skArc(sketch, "E2594", {"start": v(2505.2, 1899.5) * mm, "mid": v(2502.2, 1902.52) * mm, "end": v(2505.2, 1905.53) * mm});
            skLineSegment(sketch, "E2595", {"start": v(2505.2, 1905.53) * mm, "end": v(2520.2, 1905.53) * mm});
            skLineSegment(sketch, "E2596", {"start": v(2520.2, 1905.53) * mm, "end": v(2523.2, 1908.53) * mm});
            skLineSegment(sketch, "E2597", {"start": v(2523.2, 1908.53) * mm, "end": v(2523.2, 1942.53) * mm});
            skLineSegment(sketch, "E2598", {"start": v(2523.2, 1942.53) * mm, "end": v(2520.2, 1945.53) * mm});
            skLineSegment(sketch, "E2599", {"start": v(2520.2, 1945.53) * mm, "end": v(2505.2, 1945.53) * mm});
            skArc(sketch, "E2600", {"start": v(2505.2, 1945.53) * mm, "mid": v(2502.2, 1948.54) * mm, "end": v(2505.2, 1951.55) * mm});
            skLineSegment(sketch, "E2601", {"start": v(2505.2, 1951.55) * mm, "end": v(2505.2, 2026.5) * mm});
            skArc(sketch, "E2602", {"start": v(2505.2, 2026.5) * mm, "mid": v(2502.2, 2029.52) * mm, "end": v(2505.2, 2032.53) * mm});
            skLineSegment(sketch, "E2603", {"start": v(2505.2, 2032.53) * mm, "end": v(2523.2, 2032.53) * mm});
            skLineSegment(sketch, "E2604", {"start": v(2523.2, 2032.53) * mm, "end": v(2523.2, 2050.53) * mm});
            skLineSegment(sketch, "E2605", {"start": v(2523.2, 2050.53) * mm, "end": v(2505.2, 2050.53) * mm});
            skArc(sketch, "E2606", {"start": v(2505.2, 2050.53) * mm, "mid": v(2502.2, 2053.54) * mm, "end": v(2505.2, 2056.55) * mm});
            skLineSegment(sketch, "E2607", {"start": v(2505.2, 2056.55) * mm, "end": v(2505.2, 2068.53) * mm});
            skLineSegment(sketch, "E2608", {"start": v(2505.2, 2068.53) * mm, "end": v(2474.2, 2068.53) * mm});
            skLineSegment(sketch, "E2609", {"start": v(2474.2, 2068.53) * mm, "end": v(2474.2, 2032.57) * mm});
            skArc(sketch, "E2610", {"start": v(2474.2, 2032.57) * mm, "mid": v(2471.2, 2029.56) * mm, "end": v(2468.18, 2032.57) * mm});
            skLineSegment(sketch, "E2611", {"start": v(2468.18, 2032.57) * mm, "end": v(2428.22, 2032.57) * mm});
            skArc(sketch, "E2612", {"start": v(2428.22, 2032.57) * mm, "mid": v(2425.21, 2029.56) * mm, "end": v(2422.2, 2032.57) * mm});
            skLineSegment(sketch, "E2613", {"start": v(2422.2, 2032.57) * mm, "end": v(2422.2, 2068.53) * mm});
            skLineSegment(sketch, "E2614", {"start": v(2422.2, 2068.53) * mm, "end": v(2391.2, 2068.53) * mm});
            skLineSegment(sketch, "E2615", {"start": v(2391.2, 2068.53) * mm, "end": v(2391.2, 2056.55) * mm});
            skArc(sketch, "E2616", {"start": v(2391.2, 2056.55) * mm, "mid": v(2394.21, 2053.54) * mm, "end": v(2391.2, 2050.53) * mm});
            skLineSegment(sketch, "E2617", {"start": v(2391.2, 2050.53) * mm, "end": v(2373.2, 2050.53) * mm});
            skLineSegment(sketch, "E2618", {"start": v(2373.2, 2050.53) * mm, "end": v(2373.2, 2032.53) * mm});
            skLineSegment(sketch, "E2619", {"start": v(2373.2, 2032.53) * mm, "end": v(2391.2, 2032.53) * mm});
            skArc(sketch, "E2620", {"start": v(2391.2, 2032.53) * mm, "mid": v(2394.21, 2029.52) * mm, "end": v(2391.2, 2026.5) * mm});
            skLineSegment(sketch, "E2621", {"start": v(2391.2, 2026.5) * mm, "end": v(2391.2, 1951.55) * mm});
            skArc(sketch, "E2622", {"start": v(2391.2, 1951.55) * mm, "mid": v(2394.21, 1948.54) * mm, "end": v(2391.2, 1945.53) * mm});
            skLineSegment(sketch, "E2623", {"start": v(2391.2, 1945.53) * mm, "end": v(2376.2, 1945.53) * mm});
            skLineSegment(sketch, "E2624", {"start": v(2376.2, 1945.53) * mm, "end": v(2373.2, 1942.53) * mm});
            skLineSegment(sketch, "E2625", {"start": v(2373.2, 1942.53) * mm, "end": v(2373.2, 1908.53) * mm});
            skLineSegment(sketch, "E2626", {"start": v(2373.2, 1908.53) * mm, "end": v(2376.2, 1905.53) * mm});
            skLineSegment(sketch, "E2627", {"start": v(2206.2, 1905.53) * mm, "end": v(2221.2, 1905.53) * mm});
            skArc(sketch, "E2628", {"start": v(2221.2, 1905.53) * mm, "mid": v(2224.22, 1902.52) * mm, "end": v(2221.2, 1899.5) * mm});
            skLineSegment(sketch, "E2629", {"start": v(2221.2, 1899.5) * mm, "end": v(2221.2, 1824.55) * mm});
            skArc(sketch, "E2630", {"start": v(2221.2, 1824.55) * mm, "mid": v(2224.22, 1821.54) * mm, "end": v(2221.2, 1818.53) * mm});
            skLineSegment(sketch, "E2631", {"start": v(2221.2, 1818.53) * mm, "end": v(2203.2, 1818.53) * mm});
            skLineSegment(sketch, "E2632", {"start": v(2203.2, 1818.53) * mm, "end": v(2203.2, 1800.53) * mm});
            skLineSegment(sketch, "E2633", {"start": v(2203.2, 1800.53) * mm, "end": v(2221.2, 1800.53) * mm});
            skArc(sketch, "E2634", {"start": v(2221.2, 1800.53) * mm, "mid": v(2224.22, 1797.52) * mm, "end": v(2221.2, 1794.5) * mm});
            skLineSegment(sketch, "E2635", {"start": v(2221.2, 1794.5) * mm, "end": v(2221.2, 1782.53) * mm});
            skLineSegment(sketch, "E2636", {"start": v(2221.2, 1782.53) * mm, "end": v(2252.2, 1782.53) * mm});
            skLineSegment(sketch, "E2637", {"start": v(2252.2, 1782.53) * mm, "end": v(2252.2, 1818.53) * mm});
            skArc(sketch, "E2638", {"start": v(2252.2, 1818.53) * mm, "mid": v(2255.22, 1821.54) * mm, "end": v(2258.23, 1818.53) * mm});
            skLineSegment(sketch, "E2639", {"start": v(2258.23, 1818.53) * mm, "end": v(2298.18, 1818.53) * mm});
            skArc(sketch, "E2640", {"start": v(2298.18, 1818.53) * mm, "mid": v(2301.2, 1821.54) * mm, "end": v(2304.2, 1818.53) * mm});
            skLineSegment(sketch, "E2641", {"start": v(2304.2, 1818.53) * mm, "end": v(2304.2, 1782.53) * mm});
            skLineSegment(sketch, "E2642", {"start": v(2304.2, 1782.53) * mm, "end": v(2335.2, 1782.53) * mm});
            skLineSegment(sketch, "E2643", {"start": v(2335.2, 1782.53) * mm, "end": v(2335.2, 1794.5) * mm});
            skArc(sketch, "E2644", {"start": v(2335.2, 1794.5) * mm, "mid": v(2332.2, 1797.52) * mm, "end": v(2335.2, 1800.53) * mm});
            skLineSegment(sketch, "E2645", {"start": v(2335.2, 1800.53) * mm, "end": v(2353.2, 1800.53) * mm});
            skLineSegment(sketch, "E2646", {"start": v(2353.2, 1800.53) * mm, "end": v(2353.2, 1818.53) * mm});
            skLineSegment(sketch, "E2647", {"start": v(2353.2, 1818.53) * mm, "end": v(2335.2, 1818.53) * mm});
            skArc(sketch, "E2648", {"start": v(2335.2, 1818.53) * mm, "mid": v(2332.2, 1821.54) * mm, "end": v(2335.2, 1824.55) * mm});
            skLineSegment(sketch, "E2649", {"start": v(2335.2, 1824.55) * mm, "end": v(2335.2, 1899.5) * mm});
            skArc(sketch, "E2650", {"start": v(2335.2, 1899.5) * mm, "mid": v(2332.2, 1902.52) * mm, "end": v(2335.2, 1905.53) * mm});
            skLineSegment(sketch, "E2651", {"start": v(2335.2, 1905.53) * mm, "end": v(2350.2, 1905.53) * mm});
            skLineSegment(sketch, "E2652", {"start": v(2350.2, 1905.53) * mm, "end": v(2353.2, 1908.53) * mm});
            skLineSegment(sketch, "E2653", {"start": v(2353.2, 1908.53) * mm, "end": v(2353.2, 1942.53) * mm});
            skLineSegment(sketch, "E2654", {"start": v(2353.2, 1942.53) * mm, "end": v(2350.2, 1945.53) * mm});
            skLineSegment(sketch, "E2655", {"start": v(2350.2, 1945.53) * mm, "end": v(2335.2, 1945.53) * mm});
            skArc(sketch, "E2656", {"start": v(2335.2, 1945.53) * mm, "mid": v(2332.2, 1948.54) * mm, "end": v(2335.2, 1951.55) * mm});
            skLineSegment(sketch, "E2657", {"start": v(2335.2, 1951.55) * mm, "end": v(2335.2, 2026.5) * mm});
            skArc(sketch, "E2658", {"start": v(2335.2, 2026.5) * mm, "mid": v(2332.2, 2029.52) * mm, "end": v(2335.2, 2032.53) * mm});
            skLineSegment(sketch, "E2659", {"start": v(2335.2, 2032.53) * mm, "end": v(2353.2, 2032.53) * mm});
            skLineSegment(sketch, "E2660", {"start": v(2353.2, 2032.53) * mm, "end": v(2353.2, 2050.53) * mm});
            skLineSegment(sketch, "E2661", {"start": v(2353.2, 2050.53) * mm, "end": v(2335.2, 2050.53) * mm});
            skArc(sketch, "E2662", {"start": v(2335.2, 2050.53) * mm, "mid": v(2332.2, 2053.54) * mm, "end": v(2335.2, 2056.55) * mm});
            skLineSegment(sketch, "E2663", {"start": v(2335.2, 2056.55) * mm, "end": v(2335.2, 2068.53) * mm});
            skLineSegment(sketch, "E2664", {"start": v(2335.2, 2068.53) * mm, "end": v(2304.2, 2068.53) * mm});
            skLineSegment(sketch, "E2665", {"start": v(2304.2, 2068.53) * mm, "end": v(2304.2, 2032.57) * mm});
            skArc(sketch, "E2666", {"start": v(2304.2, 2032.57) * mm, "mid": v(2301.2, 2029.56) * mm, "end": v(2298.18, 2032.57) * mm});
            skLineSegment(sketch, "E2667", {"start": v(2298.18, 2032.57) * mm, "end": v(2258.23, 2032.57) * mm});
            skArc(sketch, "E2668", {"start": v(2258.23, 2032.57) * mm, "mid": v(2255.22, 2029.56) * mm, "end": v(2252.2, 2032.57) * mm});
            skLineSegment(sketch, "E2669", {"start": v(2252.2, 2032.57) * mm, "end": v(2252.2, 2068.53) * mm});
            skLineSegment(sketch, "E2670", {"start": v(2252.2, 2068.53) * mm, "end": v(2221.2, 2068.53) * mm});
            skLineSegment(sketch, "E2671", {"start": v(2221.2, 2068.53) * mm, "end": v(2221.2, 2056.55) * mm});
            skArc(sketch, "E2672", {"start": v(2221.2, 2056.55) * mm, "mid": v(2224.22, 2053.54) * mm, "end": v(2221.2, 2050.53) * mm});
            skLineSegment(sketch, "E2673", {"start": v(2221.2, 2050.53) * mm, "end": v(2203.2, 2050.53) * mm});
            skLineSegment(sketch, "E2674", {"start": v(2203.2, 2050.53) * mm, "end": v(2203.2, 2032.53) * mm});
            skLineSegment(sketch, "E2675", {"start": v(2203.2, 2032.53) * mm, "end": v(2221.2, 2032.53) * mm});
            skArc(sketch, "E2676", {"start": v(2221.2, 2032.53) * mm, "mid": v(2224.22, 2029.52) * mm, "end": v(2221.2, 2026.5) * mm});
            skLineSegment(sketch, "E2677", {"start": v(2221.2, 2026.5) * mm, "end": v(2221.2, 1951.55) * mm});
            skArc(sketch, "E2678", {"start": v(2221.2, 1951.55) * mm, "mid": v(2224.22, 1948.54) * mm, "end": v(2221.2, 1945.53) * mm});
            skLineSegment(sketch, "E2679", {"start": v(2221.2, 1945.53) * mm, "end": v(2206.2, 1945.53) * mm});
            skLineSegment(sketch, "E2680", {"start": v(2206.2, 1945.53) * mm, "end": v(2203.2, 1942.53) * mm});
            skLineSegment(sketch, "E2681", {"start": v(2203.2, 1942.53) * mm, "end": v(2203.2, 1908.53) * mm});
            skLineSegment(sketch, "E2682", {"start": v(2203.2, 1908.53) * mm, "end": v(2206.2, 1905.53) * mm});
            skArc(sketch, "E2683", {"start": v(2675.45, 620.4) * mm, "mid": v(2672.2, 623.54) * mm, "end": v(2675.2, 626.92) * mm});
            skLineSegment(sketch, "E2684", {"start": v(2675.2, 626.92) * mm, "end": v(2675.2, 794.38) * mm});
            skArc(sketch, "E2685", {"start": v(2675.2, 794.38) * mm, "mid": v(2672.19, 797.76) * mm, "end": v(2675.45, 800.9) * mm});
            skLineSegment(sketch, "E2686", {"start": v(2675.45, 800.9) * mm, "end": v(2693.2, 800.9) * mm});
            skLineSegment(sketch, "E2687", {"start": v(2693.2, 800.9) * mm, "end": v(2693.2, 920.4) * mm});
            skLineSegment(sketch, "E2688", {"start": v(2693.2, 920.4) * mm, "end": v(2675.45, 920.4) * mm});
            skArc(sketch, "E2689", {"start": v(2675.45, 920.4) * mm, "mid": v(2672.2, 923.54) * mm, "end": v(2675.2, 926.92) * mm});
            skLineSegment(sketch, "E2690", {"start": v(2675.2, 926.92) * mm, "end": v(2675.2, 1094.38) * mm});
            skArc(sketch, "E2691", {"start": v(2675.2, 1094.38) * mm, "mid": v(2672.19, 1097.76) * mm, "end": v(2675.45, 1100.9) * mm});
            skLineSegment(sketch, "E2692", {"start": v(2675.45, 1100.9) * mm, "end": v(2693.2, 1100.9) * mm});
            skLineSegment(sketch, "E2693", {"start": v(2693.2, 1100.9) * mm, "end": v(2693.2, 1220.4) * mm});
            skLineSegment(sketch, "E2694", {"start": v(2693.2, 1220.4) * mm, "end": v(2675.45, 1220.4) * mm});
            skArc(sketch, "E2695", {"start": v(2675.45, 1220.4) * mm, "mid": v(2672.2, 1223.54) * mm, "end": v(2675.2, 1226.92) * mm});
            skLineSegment(sketch, "E2696", {"start": v(2675.2, 1226.92) * mm, "end": v(2675.2, 1394.38) * mm});
            skArc(sketch, "E2697", {"start": v(2675.2, 1394.38) * mm, "mid": v(2672.19, 1397.76) * mm, "end": v(2675.45, 1400.9) * mm});
            skLineSegment(sketch, "E2698", {"start": v(2675.45, 1400.9) * mm, "end": v(2693.2, 1400.9) * mm});
            skLineSegment(sketch, "E2699", {"start": v(2693.2, 1400.9) * mm, "end": v(2693.2, 1520.4) * mm});
            skLineSegment(sketch, "E2700", {"start": v(2693.2, 1520.4) * mm, "end": v(2675.45, 1520.4) * mm});
            skArc(sketch, "E2701", {"start": v(2675.45, 1520.4) * mm, "mid": v(2672.2, 1523.54) * mm, "end": v(2675.2, 1526.92) * mm});
            skLineSegment(sketch, "E2702", {"start": v(2675.2, 1526.92) * mm, "end": v(2675.2, 1687.1) * mm});
            skLineSegment(sketch, "E2703", {"start": v(2675.2, 1687.1) * mm, "end": v(2630.7, 1687.1) * mm});
            skLineSegment(sketch, "E2704", {"start": v(2630.7, 1687.1) * mm, "end": v(2630.7, 1637.35) * mm});
            skArc(sketch, "E2705", {"start": v(2630.7, 1637.35) * mm, "mid": v(2627.56, 1634.1) * mm, "end": v(2624.18, 1637.1) * mm});
            skLineSegment(sketch, "E2706", {"start": v(2624.18, 1637.1) * mm, "end": v(2576.72, 1637.1) * mm});
            skArc(sketch, "E2707", {"start": v(2576.72, 1637.1) * mm, "mid": v(2573.34, 1634.08) * mm, "end": v(2570.2, 1637.35) * mm});
            skLineSegment(sketch, "E2708", {"start": v(2570.2, 1637.35) * mm, "end": v(2570.2, 1687.1) * mm});
            skLineSegment(sketch, "E2709", {"start": v(2570.2, 1687.1) * mm, "end": v(2530.7, 1687.1) * mm});
            skLineSegment(sketch, "E2710", {"start": v(2530.7, 1687.1) * mm, "end": v(2530.7, 1637.35) * mm});
            skArc(sketch, "E2711", {"start": v(2530.7, 1637.35) * mm, "mid": v(2527.56, 1634.1) * mm, "end": v(2524.18, 1637.1) * mm});
            skLineSegment(sketch, "E2712", {"start": v(2524.18, 1637.1) * mm, "end": v(2476.72, 1637.1) * mm});
            skArc(sketch, "E2713", {"start": v(2476.72, 1637.1) * mm, "mid": v(2473.34, 1634.08) * mm, "end": v(2470.2, 1637.35) * mm});
            skLineSegment(sketch, "E2714", {"start": v(2470.2, 1637.35) * mm, "end": v(2470.2, 1687.1) * mm});
            skLineSegment(sketch, "E2715", {"start": v(2470.2, 1687.1) * mm, "end": v(2425.7, 1687.1) * mm});
            skLineSegment(sketch, "E2716", {"start": v(2425.7, 1687.1) * mm, "end": v(2425.7, 1526.92) * mm});
            skArc(sketch, "E2717", {"start": v(2425.7, 1526.92) * mm, "mid": v(2428.72, 1523.54) * mm, "end": v(2425.45, 1520.4) * mm});
            skLineSegment(sketch, "E2718", {"start": v(2425.45, 1520.4) * mm, "end": v(2407.7, 1520.4) * mm});
            skLineSegment(sketch, "E2719", {"start": v(2407.7, 1520.4) * mm, "end": v(2407.7, 1400.9) * mm});
            skLineSegment(sketch, "E2720", {"start": v(2407.7, 1400.9) * mm, "end": v(2425.45, 1400.9) * mm});
            skArc(sketch, "E2721", {"start": v(2425.45, 1400.9) * mm, "mid": v(2428.71, 1397.76) * mm, "end": v(2425.7, 1394.38) * mm});
            skLineSegment(sketch, "E2722", {"start": v(2425.7, 1394.38) * mm, "end": v(2425.7, 1226.92) * mm});
            skArc(sketch, "E2723", {"start": v(2425.7, 1226.92) * mm, "mid": v(2428.72, 1223.54) * mm, "end": v(2425.45, 1220.4) * mm});
            skLineSegment(sketch, "E2724", {"start": v(2425.45, 1220.4) * mm, "end": v(2407.7, 1220.4) * mm});
            skLineSegment(sketch, "E2725", {"start": v(2407.7, 1220.4) * mm, "end": v(2407.7, 1100.9) * mm});
            skLineSegment(sketch, "E2726", {"start": v(2407.7, 1100.9) * mm, "end": v(2425.45, 1100.9) * mm});
            skArc(sketch, "E2727", {"start": v(2425.45, 1100.9) * mm, "mid": v(2428.71, 1097.76) * mm, "end": v(2425.7, 1094.38) * mm});
            skLineSegment(sketch, "E2728", {"start": v(2425.7, 1094.38) * mm, "end": v(2425.7, 926.92) * mm});
            skArc(sketch, "E2729", {"start": v(2425.7, 926.92) * mm, "mid": v(2428.72, 923.54) * mm, "end": v(2425.45, 920.4) * mm});
            skLineSegment(sketch, "E2730", {"start": v(2425.45, 920.4) * mm, "end": v(2407.7, 920.4) * mm});
            skLineSegment(sketch, "E2731", {"start": v(2407.7, 920.4) * mm, "end": v(2407.7, 800.9) * mm});
            skLineSegment(sketch, "E2732", {"start": v(2407.7, 800.9) * mm, "end": v(2425.45, 800.9) * mm});
            skArc(sketch, "E2733", {"start": v(2425.45, 800.9) * mm, "mid": v(2428.71, 797.76) * mm, "end": v(2425.7, 794.38) * mm});
            skLineSegment(sketch, "E2734", {"start": v(2425.7, 794.38) * mm, "end": v(2425.7, 626.92) * mm});
            skArc(sketch, "E2735", {"start": v(2425.7, 626.92) * mm, "mid": v(2428.72, 623.54) * mm, "end": v(2425.45, 620.4) * mm});
            skLineSegment(sketch, "E2736", {"start": v(2425.45, 620.4) * mm, "end": v(2407.7, 620.4) * mm});
            skLineSegment(sketch, "E2737", {"start": v(2407.7, 620.4) * mm, "end": v(2407.7, 500.9) * mm});
            skLineSegment(sketch, "E2738", {"start": v(2407.7, 500.9) * mm, "end": v(2425.45, 500.9) * mm});
            skArc(sketch, "E2739", {"start": v(2425.45, 500.9) * mm, "mid": v(2428.71, 497.76) * mm, "end": v(2425.7, 494.38) * mm});
            skLineSegment(sketch, "E2740", {"start": v(2425.7, 494.38) * mm, "end": v(2425.7, 406.92) * mm});
            skArc(sketch, "E2741", {"start": v(2425.7, 406.92) * mm, "mid": v(2428.72, 403.54) * mm, "end": v(2425.45, 400.4) * mm});
            skLineSegment(sketch, "E2742", {"start": v(2425.45, 400.4) * mm, "end": v(2407.7, 400.4) * mm});
            skLineSegment(sketch, "E2743", {"start": v(2407.7, 400.4) * mm, "end": v(2407.7, 317.16) * mm});
            skArc(sketch, "E2744", {"start": v(2407.7, 317.16) * mm, "mid": v(2410.72, 313.78) * mm, "end": v(2407.45, 310.64) * mm});
            skLineSegment(sketch, "E2745", {"start": v(2407.45, 310.64) * mm, "end": v(2317.94, 310.64) * mm});
            skLineSegment(sketch, "E2746", {"start": v(2317.94, 310.64) * mm, "end": v(2317.94, 292.89) * mm});
            skArc(sketch, "E2747", {"start": v(2317.94, 292.89) * mm, "mid": v(2314.8, 289.63) * mm, "end": v(2311.42, 292.64) * mm});
            skLineSegment(sketch, "E2748", {"start": v(2311.42, 292.64) * mm, "end": v(2223.96, 292.64) * mm});
            skArc(sketch, "E2749", {"start": v(2223.96, 292.64) * mm, "mid": v(2220.58, 289.62) * mm, "end": v(2217.44, 292.89) * mm});
            skLineSegment(sketch, "E2750", {"start": v(2217.44, 292.89) * mm, "end": v(2217.44, 310.64) * mm});
            skLineSegment(sketch, "E2751", {"start": v(2217.44, 310.64) * mm, "end": v(2097.94, 310.64) * mm});
            skLineSegment(sketch, "E2752", {"start": v(2097.94, 310.64) * mm, "end": v(2097.94, 292.89) * mm});
            skArc(sketch, "E2753", {"start": v(2097.94, 292.89) * mm, "mid": v(2094.8, 289.63) * mm, "end": v(2091.42, 292.64) * mm});
            skLineSegment(sketch, "E2754", {"start": v(2091.42, 292.64) * mm, "end": v(1923.96, 292.64) * mm});
            skArc(sketch, "E2755", {"start": v(1923.96, 292.64) * mm, "mid": v(1920.58, 289.62) * mm, "end": v(1917.44, 292.89) * mm});
            skLineSegment(sketch, "E2756", {"start": v(1917.44, 292.89) * mm, "end": v(1917.44, 310.64) * mm});
            skLineSegment(sketch, "E2757", {"start": v(1917.44, 310.64) * mm, "end": v(1797.94, 310.64) * mm});
            skLineSegment(sketch, "E2758", {"start": v(1797.94, 310.64) * mm, "end": v(1797.94, 292.89) * mm});
            skArc(sketch, "E2759", {"start": v(1797.94, 292.89) * mm, "mid": v(1794.8, 289.63) * mm, "end": v(1791.42, 292.64) * mm});
            skLineSegment(sketch, "E2760", {"start": v(1791.42, 292.64) * mm, "end": v(1784.63, 292.64) * mm});
            skLineSegment(sketch, "E2761", {"start": v(1784.63, 292.64) * mm, "end": v(1784.63, 254.16) * mm});
            skArc(sketch, "E2762", {"start": v(1784.63, 254.16) * mm, "mid": v(1787.65, 250.78) * mm, "end": v(1784.38, 247.64) * mm});
            skLineSegment(sketch, "E2763", {"start": v(1784.38, 247.64) * mm, "end": v(1734.63, 247.64) * mm});
            skLineSegment(sketch, "E2764", {"start": v(1734.63, 247.64) * mm, "end": v(1734.63, 188.14) * mm});
            skLineSegment(sketch, "E2765", {"start": v(1734.63, 188.14) * mm, "end": v(1784.38, 188.14) * mm});
            skArc(sketch, "E2766", {"start": v(1784.38, 188.14) * mm, "mid": v(1787.64, 185) * mm, "end": v(1784.63, 181.62) * mm});
            skLineSegment(sketch, "E2767", {"start": v(1784.63, 181.62) * mm, "end": v(1784.63, 154.16) * mm});
            skArc(sketch, "E2768", {"start": v(1784.63, 154.16) * mm, "mid": v(1787.65, 150.78) * mm, "end": v(1784.38, 147.64) * mm});
            skLineSegment(sketch, "E2769", {"start": v(1784.38, 147.64) * mm, "end": v(1734.63, 147.64) * mm});
            skLineSegment(sketch, "E2770", {"start": v(1734.63, 147.64) * mm, "end": v(1734.63, 88.14) * mm});
            skLineSegment(sketch, "E2771", {"start": v(1734.63, 88.14) * mm, "end": v(1784.38, 88.14) * mm});
            skArc(sketch, "E2772", {"start": v(1784.38, 88.14) * mm, "mid": v(1787.64, 85) * mm, "end": v(1784.63, 81.62) * mm});
            skLineSegment(sketch, "E2773", {"start": v(1784.63, 81.62) * mm, "end": v(1784.63, 43.14) * mm});
            skLineSegment(sketch, "E2774", {"start": v(1784.63, 43.14) * mm, "end": v(1791.42, 43.14) * mm});
            skArc(sketch, "E2775", {"start": v(1791.42, 43.14) * mm, "mid": v(1794.8, 46.16) * mm, "end": v(1797.94, 42.89) * mm});
            skLineSegment(sketch, "E2776", {"start": v(1797.94, 42.89) * mm, "end": v(1797.94, 25.14) * mm});
            skLineSegment(sketch, "E2777", {"start": v(1797.94, 25.14) * mm, "end": v(1917.44, 25.14) * mm});
            skLineSegment(sketch, "E2778", {"start": v(1917.44, 25.14) * mm, "end": v(1917.44, 42.89) * mm});
            skArc(sketch, "E2779", {"start": v(1917.44, 42.89) * mm, "mid": v(1920.58, 46.15) * mm, "end": v(1923.96, 43.14) * mm});
            skLineSegment(sketch, "E2780", {"start": v(1923.96, 43.14) * mm, "end": v(2091.42, 43.14) * mm});
            skArc(sketch, "E2781", {"start": v(2091.42, 43.14) * mm, "mid": v(2094.8, 46.16) * mm, "end": v(2097.94, 42.89) * mm});
            skLineSegment(sketch, "E2782", {"start": v(2097.94, 42.89) * mm, "end": v(2097.94, 25.14) * mm});
            skLineSegment(sketch, "E2783", {"start": v(2097.94, 25.14) * mm, "end": v(2217.44, 25.14) * mm});
            skLineSegment(sketch, "E2784", {"start": v(2217.44, 25.14) * mm, "end": v(2217.44, 42.89) * mm});
            skArc(sketch, "E2785", {"start": v(2217.44, 42.89) * mm, "mid": v(2220.58, 46.15) * mm, "end": v(2223.96, 43.14) * mm});
            skLineSegment(sketch, "E2786", {"start": v(2223.96, 43.14) * mm, "end": v(2311.42, 43.14) * mm});
            skArc(sketch, "E2787", {"start": v(2311.42, 43.14) * mm, "mid": v(2314.8, 46.16) * mm, "end": v(2317.94, 42.89) * mm});
            skLineSegment(sketch, "E2788", {"start": v(2317.94, 42.89) * mm, "end": v(2317.94, 25.14) * mm});
            skLineSegment(sketch, "E2789", {"start": v(2317.94, 25.14) * mm, "end": v(2443.2, 25.14) * mm});
            skLineSegment(sketch, "E2790", {"start": v(2443.2, 25.14) * mm, "end": v(2443.2, 42.89) * mm});
            skArc(sketch, "E2791", {"start": v(2443.2, 42.89) * mm, "mid": v(2446.35, 46.15) * mm, "end": v(2449.73, 43.14) * mm});
            skLineSegment(sketch, "E2792", {"start": v(2449.73, 43.14) * mm, "end": v(2657.2, 43.14) * mm});
            skLineSegment(sketch, "E2793", {"start": v(2657.2, 43.14) * mm, "end": v(2657.2, 56.62) * mm});
            skArc(sketch, "E2794", {"start": v(2657.2, 56.62) * mm, "mid": v(2654.19, 60) * mm, "end": v(2657.45, 63.14) * mm});
            skLineSegment(sketch, "E2795", {"start": v(2657.45, 63.14) * mm, "end": v(2675.2, 63.14) * mm});
            skLineSegment(sketch, "E2796", {"start": v(2675.2, 63.14) * mm, "end": v(2675.2, 87.64) * mm});
            skLineSegment(sketch, "E2797", {"start": v(2675.2, 87.64) * mm, "end": v(2631.72, 87.64) * mm});
            skArc(sketch, "E2798", {"start": v(2631.72, 87.64) * mm, "mid": v(2628.34, 84.62) * mm, "end": v(2625.2, 87.89) * mm});
            skLineSegment(sketch, "E2799", {"start": v(2625.2, 87.89) * mm, "end": v(2625.2, 247.89) * mm});
            skArc(sketch, "E2800", {"start": v(2625.2, 247.89) * mm, "mid": v(2628.34, 251.15) * mm, "end": v(2631.72, 248.14) * mm});
            skLineSegment(sketch, "E2801", {"start": v(2631.72, 248.14) * mm, "end": v(2675.2, 248.14) * mm});
            skLineSegment(sketch, "E2802", {"start": v(2675.2, 248.14) * mm, "end": v(2675.2, 274.38) * mm});
            skArc(sketch, "E2803", {"start": v(2675.2, 274.38) * mm, "mid": v(2672.19, 277.76) * mm, "end": v(2675.45, 280.9) * mm});
            skLineSegment(sketch, "E2804", {"start": v(2675.45, 280.9) * mm, "end": v(2693.2, 280.9) * mm});
            skLineSegment(sketch, "E2805", {"start": v(2693.2, 280.9) * mm, "end": v(2693.2, 400.4) * mm});
            skLineSegment(sketch, "E2806", {"start": v(2693.2, 400.4) * mm, "end": v(2675.45, 400.4) * mm});
            skArc(sketch, "E2807", {"start": v(2675.45, 400.4) * mm, "mid": v(2672.2, 403.54) * mm, "end": v(2675.2, 406.92) * mm});
            skLineSegment(sketch, "E2808", {"start": v(2675.2, 406.92) * mm, "end": v(2675.2, 494.38) * mm});
            skArc(sketch, "E2809", {"start": v(2675.2, 494.38) * mm, "mid": v(2672.19, 497.76) * mm, "end": v(2675.45, 500.9) * mm});
            skLineSegment(sketch, "E2810", {"start": v(2675.45, 500.9) * mm, "end": v(2693.2, 500.9) * mm});
            skLineSegment(sketch, "E2811", {"start": v(2693.2, 500.9) * mm, "end": v(2693.2, 620.4) * mm});
            skLineSegment(sketch, "E2812", {"start": v(2693.2, 620.4) * mm, "end": v(2675.45, 620.4) * mm});
            skLineSegment(sketch, "E2813", {"start": v(1605.7, 2313.66) * mm, "end": v(1605.7, 2357.14) * mm});
            skLineSegment(sketch, "E2814", {"start": v(1605.7, 2357.14) * mm, "end": v(1581.2, 2357.14) * mm});
            skLineSegment(sketch, "E2815", {"start": v(1581.2, 2357.14) * mm, "end": v(1581.2, 2339.39) * mm});
            skArc(sketch, "E2816", {"start": v(1581.2, 2339.39) * mm, "mid": v(1578.06, 2336.13) * mm, "end": v(1574.68, 2339.14) * mm});
            skLineSegment(sketch, "E2817", {"start": v(1574.68, 2339.14) * mm, "end": v(1561.2, 2339.14) * mm});
            skLineSegment(sketch, "E2818", {"start": v(1561.2, 2339.14) * mm, "end": v(1561.2, 2131.66) * mm});
            skArc(sketch, "E2819", {"start": v(1561.2, 2131.66) * mm, "mid": v(1564.22, 2128.28) * mm, "end": v(1560.95, 2125.14) * mm});
            skLineSegment(sketch, "E2820", {"start": v(1560.95, 2125.14) * mm, "end": v(1543.2, 2125.14) * mm});
            skLineSegment(sketch, "E2821", {"start": v(1543.2, 2125.14) * mm, "end": v(1543.2, 1999.87) * mm});
            skLineSegment(sketch, "E2822", {"start": v(1543.2, 1999.87) * mm, "end": v(1560.95, 1999.87) * mm});
            skArc(sketch, "E2823", {"start": v(1560.95, 1999.87) * mm, "mid": v(1564.21, 1996.73) * mm, "end": v(1561.2, 1993.35) * mm});
            skLineSegment(sketch, "E2824", {"start": v(1561.2, 1993.35) * mm, "end": v(1561.2, 1905.9) * mm});
            skArc(sketch, "E2825", {"start": v(1561.2, 1905.9) * mm, "mid": v(1564.22, 1902.51) * mm, "end": v(1560.95, 1899.37) * mm});
            skLineSegment(sketch, "E2826", {"start": v(1560.95, 1899.37) * mm, "end": v(1543.2, 1899.37) * mm});
            skLineSegment(sketch, "E2827", {"start": v(1543.2, 1899.37) * mm, "end": v(1543.2, 1779.87) * mm});
            skLineSegment(sketch, "E2828", {"start": v(1543.2, 1779.87) * mm, "end": v(1560.95, 1779.87) * mm});
            skArc(sketch, "E2829", {"start": v(1560.95, 1779.87) * mm, "mid": v(1564.21, 1776.73) * mm, "end": v(1561.2, 1773.35) * mm});
            skLineSegment(sketch, "E2830", {"start": v(1561.2, 1773.35) * mm, "end": v(1561.2, 1605.9) * mm});
            skArc(sketch, "E2831", {"start": v(1561.2, 1605.9) * mm, "mid": v(1564.22, 1602.51) * mm, "end": v(1560.95, 1599.37) * mm});
            skLineSegment(sketch, "E2832", {"start": v(1560.95, 1599.37) * mm, "end": v(1543.2, 1599.37) * mm});
            skLineSegment(sketch, "E2833", {"start": v(1543.2, 1599.37) * mm, "end": v(1543.2, 1479.87) * mm});
            skLineSegment(sketch, "E2834", {"start": v(1543.2, 1479.87) * mm, "end": v(1560.95, 1479.87) * mm});
            skArc(sketch, "E2835", {"start": v(1560.95, 1479.87) * mm, "mid": v(1564.21, 1476.73) * mm, "end": v(1561.2, 1473.35) * mm});
            skLineSegment(sketch, "E2836", {"start": v(1561.2, 1473.35) * mm, "end": v(1561.2, 1305.9) * mm});
            skArc(sketch, "E2837", {"start": v(1561.2, 1305.9) * mm, "mid": v(1564.22, 1302.51) * mm, "end": v(1560.95, 1299.37) * mm});
            skLineSegment(sketch, "E2838", {"start": v(1560.95, 1299.37) * mm, "end": v(1543.2, 1299.37) * mm});
            skLineSegment(sketch, "E2839", {"start": v(1543.2, 1299.37) * mm, "end": v(1543.2, 1179.87) * mm});
            skLineSegment(sketch, "E2840", {"start": v(1543.2, 1179.87) * mm, "end": v(1560.95, 1179.87) * mm});
            skArc(sketch, "E2841", {"start": v(1560.95, 1179.87) * mm, "mid": v(1564.21, 1176.73) * mm, "end": v(1561.2, 1173.35) * mm});
            skLineSegment(sketch, "E2842", {"start": v(1561.2, 1173.35) * mm, "end": v(1561.2, 1005.9) * mm});
            skArc(sketch, "E2843", {"start": v(1561.2, 1005.9) * mm, "mid": v(1564.22, 1002.51) * mm, "end": v(1560.95, 999.37) * mm});
            skLineSegment(sketch, "E2844", {"start": v(1560.95, 999.37) * mm, "end": v(1543.2, 999.37) * mm});
            skLineSegment(sketch, "E2845", {"start": v(1543.2, 999.37) * mm, "end": v(1543.2, 879.87) * mm});
            skLineSegment(sketch, "E2846", {"start": v(1543.2, 879.87) * mm, "end": v(1560.95, 879.87) * mm});
            skArc(sketch, "E2847", {"start": v(1560.95, 879.87) * mm, "mid": v(1564.21, 876.73) * mm, "end": v(1561.2, 873.35) * mm});
            skLineSegment(sketch, "E2848", {"start": v(1561.2, 873.35) * mm, "end": v(1561.2, 713.18) * mm});
            skLineSegment(sketch, "E2849", {"start": v(1561.2, 713.18) * mm, "end": v(1605.7, 713.18) * mm});
            skLineSegment(sketch, "E2850", {"start": v(1605.7, 713.18) * mm, "end": v(1605.7, 762.93) * mm});
            skArc(sketch, "E2851", {"start": v(1605.7, 762.93) * mm, "mid": v(1608.84, 766.19) * mm, "end": v(1612.22, 763.18) * mm});
            skLineSegment(sketch, "E2852", {"start": v(1612.22, 763.18) * mm, "end": v(1659.68, 763.18) * mm});
            skArc(sketch, "E2853", {"start": v(1659.68, 763.18) * mm, "mid": v(1663.06, 766.2) * mm, "end": v(1666.2, 762.93) * mm});
            skLineSegment(sketch, "E2854", {"start": v(1666.2, 762.93) * mm, "end": v(1666.2, 713.18) * mm});
            skLineSegment(sketch, "E2855", {"start": v(1666.2, 713.18) * mm, "end": v(1705.7, 713.18) * mm});
            skLineSegment(sketch, "E2856", {"start": v(1705.7, 713.18) * mm, "end": v(1705.7, 762.93) * mm});
            skArc(sketch, "E2857", {"start": v(1705.7, 762.93) * mm, "mid": v(1708.84, 766.19) * mm, "end": v(1712.22, 763.18) * mm});
            skLineSegment(sketch, "E2858", {"start": v(1712.22, 763.18) * mm, "end": v(1759.68, 763.18) * mm});
            skArc(sketch, "E2859", {"start": v(1759.68, 763.18) * mm, "mid": v(1763.06, 766.2) * mm, "end": v(1766.2, 762.93) * mm});
            skLineSegment(sketch, "E2860", {"start": v(1766.2, 762.93) * mm, "end": v(1766.2, 713.18) * mm});
            skLineSegment(sketch, "E2861", {"start": v(1766.2, 713.18) * mm, "end": v(1810.7, 713.18) * mm});
            skLineSegment(sketch, "E2862", {"start": v(1810.7, 713.18) * mm, "end": v(1810.7, 873.35) * mm});
            skArc(sketch, "E2863", {"start": v(1810.7, 873.35) * mm, "mid": v(1807.69, 876.73) * mm, "end": v(1810.95, 879.87) * mm});
            skLineSegment(sketch, "E2864", {"start": v(1810.95, 879.87) * mm, "end": v(1828.7, 879.87) * mm});
            skLineSegment(sketch, "E2865", {"start": v(1828.7, 879.87) * mm, "end": v(1828.7, 999.37) * mm});
            skLineSegment(sketch, "E2866", {"start": v(1828.7, 999.37) * mm, "end": v(1810.95, 999.37) * mm});
            skArc(sketch, "E2867", {"start": v(1810.95, 999.37) * mm, "mid": v(1807.7, 1002.51) * mm, "end": v(1810.7, 1005.9) * mm});
            skLineSegment(sketch, "E2868", {"start": v(1810.7, 1005.9) * mm, "end": v(1810.7, 1173.35) * mm});
            skArc(sketch, "E2869", {"start": v(1810.7, 1173.35) * mm, "mid": v(1807.69, 1176.73) * mm, "end": v(1810.95, 1179.87) * mm});
            skLineSegment(sketch, "E2870", {"start": v(1810.95, 1179.87) * mm, "end": v(1828.7, 1179.87) * mm});
            skLineSegment(sketch, "E2871", {"start": v(1828.7, 1179.87) * mm, "end": v(1828.7, 1299.37) * mm});
            skLineSegment(sketch, "E2872", {"start": v(1828.7, 1299.37) * mm, "end": v(1810.95, 1299.37) * mm});
            skArc(sketch, "E2873", {"start": v(1810.95, 1299.37) * mm, "mid": v(1807.7, 1302.51) * mm, "end": v(1810.7, 1305.9) * mm});
            skLineSegment(sketch, "E2874", {"start": v(1810.7, 1305.9) * mm, "end": v(1810.7, 1473.35) * mm});
            skArc(sketch, "E2875", {"start": v(1810.7, 1473.35) * mm, "mid": v(1807.69, 1476.73) * mm, "end": v(1810.95, 1479.87) * mm});
            skLineSegment(sketch, "E2876", {"start": v(1810.95, 1479.87) * mm, "end": v(1828.7, 1479.87) * mm});
            skLineSegment(sketch, "E2877", {"start": v(1828.7, 1479.87) * mm, "end": v(1828.7, 1599.37) * mm});
            skLineSegment(sketch, "E2878", {"start": v(1828.7, 1599.37) * mm, "end": v(1810.95, 1599.37) * mm});
            skArc(sketch, "E2879", {"start": v(1810.95, 1599.37) * mm, "mid": v(1807.7, 1602.51) * mm, "end": v(1810.7, 1605.9) * mm});
            skLineSegment(sketch, "E2880", {"start": v(1810.7, 1605.9) * mm, "end": v(1810.7, 1773.35) * mm});
            skArc(sketch, "E2881", {"start": v(1810.7, 1773.35) * mm, "mid": v(1807.69, 1776.73) * mm, "end": v(1810.95, 1779.87) * mm});
            skLineSegment(sketch, "E2882", {"start": v(1810.95, 1779.87) * mm, "end": v(1828.7, 1779.87) * mm});
            skLineSegment(sketch, "E2883", {"start": v(1828.7, 1779.87) * mm, "end": v(1828.7, 1899.37) * mm});
            skLineSegment(sketch, "E2884", {"start": v(1828.7, 1899.37) * mm, "end": v(1810.95, 1899.37) * mm});
            skArc(sketch, "E2885", {"start": v(1810.95, 1899.37) * mm, "mid": v(1807.7, 1902.51) * mm, "end": v(1810.7, 1905.9) * mm});
            skLineSegment(sketch, "E2886", {"start": v(1810.7, 1905.9) * mm, "end": v(1810.7, 1993.35) * mm});
            skArc(sketch, "E2887", {"start": v(1810.7, 1993.35) * mm, "mid": v(1807.69, 1996.73) * mm, "end": v(1810.95, 1999.87) * mm});
            skLineSegment(sketch, "E2888", {"start": v(1810.95, 1999.87) * mm, "end": v(1828.7, 1999.87) * mm});
            skLineSegment(sketch, "E2889", {"start": v(1828.7, 1999.87) * mm, "end": v(1828.7, 2089.39) * mm});
            skArc(sketch, "E2890", {"start": v(1828.7, 2089.39) * mm, "mid": v(1831.84, 2092.65) * mm, "end": v(1835.22, 2089.64) * mm});
            skLineSegment(sketch, "E2891", {"start": v(1835.22, 2089.64) * mm, "end": v(1918.47, 2089.64) * mm});
            skLineSegment(sketch, "E2892", {"start": v(1918.47, 2089.64) * mm, "end": v(1918.47, 2107.39) * mm});
            skArc(sketch, "E2893", {"start": v(1918.47, 2107.39) * mm, "mid": v(1921.61, 2110.65) * mm, "end": v(1925, 2107.64) * mm});
            skLineSegment(sketch, "E2894", {"start": v(1925, 2107.64) * mm, "end": v(2012.45, 2107.64) * mm});
            skArc(sketch, "E2895", {"start": v(2012.45, 2107.64) * mm, "mid": v(2015.83, 2110.66) * mm, "end": v(2018.97, 2107.39) * mm});
            skLineSegment(sketch, "E2896", {"start": v(2018.97, 2107.39) * mm, "end": v(2018.97, 2089.64) * mm});
            skLineSegment(sketch, "E2897", {"start": v(2018.97, 2089.64) * mm, "end": v(2138.47, 2089.64) * mm});
            skLineSegment(sketch, "E2898", {"start": v(2138.47, 2089.64) * mm, "end": v(2138.47, 2107.39) * mm});
            skArc(sketch, "E2899", {"start": v(2138.47, 2107.39) * mm, "mid": v(2141.61, 2110.65) * mm, "end": v(2145, 2107.64) * mm});
            skLineSegment(sketch, "E2900", {"start": v(2145, 2107.64) * mm, "end": v(2312.45, 2107.64) * mm});
            skArc(sketch, "E2901", {"start": v(2312.45, 2107.64) * mm, "mid": v(2315.83, 2110.66) * mm, "end": v(2318.97, 2107.39) * mm});
            skLineSegment(sketch, "E2902", {"start": v(2318.97, 2107.39) * mm, "end": v(2318.97, 2089.64) * mm});
            skLineSegment(sketch, "E2903", {"start": v(2318.97, 2089.64) * mm, "end": v(2438.47, 2089.64) * mm});
            skLineSegment(sketch, "E2904", {"start": v(2438.47, 2089.64) * mm, "end": v(2438.47, 2107.39) * mm});
            skArc(sketch, "E2905", {"start": v(2438.47, 2107.39) * mm, "mid": v(2441.61, 2110.65) * mm, "end": v(2445, 2107.64) * mm});
            skLineSegment(sketch, "E2906", {"start": v(2445, 2107.64) * mm, "end": v(2451.77, 2107.64) * mm});
            skLineSegment(sketch, "E2907", {"start": v(2451.77, 2107.64) * mm, "end": v(2451.77, 2146.12) * mm});
            skArc(sketch, "E2908", {"start": v(2451.77, 2146.12) * mm, "mid": v(2448.76, 2149.5) * mm, "end": v(2452.02, 2152.64) * mm});
            skLineSegment(sketch, "E2909", {"start": v(2452.02, 2152.64) * mm, "end": v(2501.77, 2152.64) * mm});
            skLineSegment(sketch, "E2910", {"start": v(2501.77, 2152.64) * mm, "end": v(2501.77, 2212.14) * mm});
            skLineSegment(sketch, "E2911", {"start": v(2501.77, 2212.14) * mm, "end": v(2452.02, 2212.14) * mm});
            skArc(sketch, "E2912", {"start": v(2452.02, 2212.14) * mm, "mid": v(2448.77, 2215.28) * mm, "end": v(2451.77, 2218.66) * mm});
            skLineSegment(sketch, "E2913", {"start": v(2451.77, 2218.66) * mm, "end": v(2451.77, 2246.12) * mm});
            skArc(sketch, "E2914", {"start": v(2451.77, 2246.12) * mm, "mid": v(2448.76, 2249.5) * mm, "end": v(2452.02, 2252.64) * mm});
            skLineSegment(sketch, "E2915", {"start": v(2452.02, 2252.64) * mm, "end": v(2501.77, 2252.64) * mm});
            skLineSegment(sketch, "E2916", {"start": v(2501.77, 2252.64) * mm, "end": v(2501.77, 2312.14) * mm});
            skLineSegment(sketch, "E2917", {"start": v(2501.77, 2312.14) * mm, "end": v(2452.02, 2312.14) * mm});
            skArc(sketch, "E2918", {"start": v(2452.02, 2312.14) * mm, "mid": v(2448.77, 2315.28) * mm, "end": v(2451.77, 2318.66) * mm});
            skLineSegment(sketch, "E2919", {"start": v(2451.77, 2318.66) * mm, "end": v(2451.77, 2357.14) * mm});
            skLineSegment(sketch, "E2920", {"start": v(2451.77, 2357.14) * mm, "end": v(2445, 2357.14) * mm});
            skArc(sketch, "E2921", {"start": v(2445, 2357.14) * mm, "mid": v(2441.6, 2354.12) * mm, "end": v(2438.47, 2357.39) * mm});
            skLineSegment(sketch, "E2922", {"start": v(2438.47, 2357.39) * mm, "end": v(2438.47, 2375.14) * mm});
            skLineSegment(sketch, "E2923", {"start": v(2438.47, 2375.14) * mm, "end": v(2318.97, 2375.14) * mm});
            skLineSegment(sketch, "E2924", {"start": v(2318.97, 2375.14) * mm, "end": v(2318.97, 2357.39) * mm});
            skArc(sketch, "E2925", {"start": v(2318.97, 2357.39) * mm, "mid": v(2315.83, 2354.13) * mm, "end": v(2312.45, 2357.14) * mm});
            skLineSegment(sketch, "E2926", {"start": v(2312.45, 2357.14) * mm, "end": v(2145, 2357.14) * mm});
            skArc(sketch, "E2927", {"start": v(2145, 2357.14) * mm, "mid": v(2141.6, 2354.12) * mm, "end": v(2138.47, 2357.39) * mm});
            skLineSegment(sketch, "E2928", {"start": v(2138.47, 2357.39) * mm, "end": v(2138.47, 2375.14) * mm});
            skLineSegment(sketch, "E2929", {"start": v(2138.47, 2375.14) * mm, "end": v(2018.97, 2375.14) * mm});
            skLineSegment(sketch, "E2930", {"start": v(2018.97, 2375.14) * mm, "end": v(2018.97, 2357.39) * mm});
            skArc(sketch, "E2931", {"start": v(2018.97, 2357.39) * mm, "mid": v(2015.83, 2354.13) * mm, "end": v(2012.45, 2357.14) * mm});
            skLineSegment(sketch, "E2932", {"start": v(2012.45, 2357.14) * mm, "end": v(1925, 2357.14) * mm});
            skArc(sketch, "E2933", {"start": v(1925, 2357.14) * mm, "mid": v(1921.6, 2354.12) * mm, "end": v(1918.47, 2357.39) * mm});
            skLineSegment(sketch, "E2934", {"start": v(1918.47, 2357.39) * mm, "end": v(1918.47, 2375.14) * mm});
            skLineSegment(sketch, "E2935", {"start": v(1918.47, 2375.14) * mm, "end": v(1798.97, 2375.14) * mm});
            skLineSegment(sketch, "E2936", {"start": v(1798.97, 2375.14) * mm, "end": v(1798.97, 2357.39) * mm});
            skArc(sketch, "E2937", {"start": v(1798.97, 2357.39) * mm, "mid": v(1795.83, 2354.13) * mm, "end": v(1792.45, 2357.14) * mm});
            skLineSegment(sketch, "E2938", {"start": v(1792.45, 2357.14) * mm, "end": v(1766.2, 2357.14) * mm});
            skLineSegment(sketch, "E2939", {"start": v(1766.2, 2357.14) * mm, "end": v(1766.2, 2313.66) * mm});
            skArc(sketch, "E2940", {"start": v(1766.2, 2313.66) * mm, "mid": v(1769.22, 2310.28) * mm, "end": v(1765.95, 2307.14) * mm});
            skLineSegment(sketch, "E2941", {"start": v(1765.95, 2307.14) * mm, "end": v(1605.95, 2307.14) * mm});
            skArc(sketch, "E2942", {"start": v(1605.95, 2307.14) * mm, "mid": v(1602.7, 2310.28) * mm, "end": v(1605.7, 2313.66) * mm});
            skLineSegment(sketch, "E2943", {"start": v(2324.7, 331.22) * mm, "end": v(2324.7, 381.22) * mm});
            skArc(sketch, "E2944", {"start": v(2324.7, 381.22) * mm, "mid": v(2327.71, 384.23) * mm, "end": v(2330.72, 381.22) * mm});
            skLineSegment(sketch, "E2945", {"start": v(2330.72, 381.22) * mm, "end": v(2369.7, 381.22) * mm});
            skLineSegment(sketch, "E2946", {"start": v(2369.7, 381.22) * mm, "end": v(2369.7, 388.5) * mm});
            skArc(sketch, "E2947", {"start": v(2369.7, 388.5) * mm, "mid": v(2366.7, 391.51) * mm, "end": v(2369.7, 394.52) * mm});
            skLineSegment(sketch, "E2948", {"start": v(2369.7, 394.52) * mm, "end": v(2387.7, 394.52) * mm});
            skLineSegment(sketch, "E2949", {"start": v(2387.7, 394.52) * mm, "end": v(2387.7, 514.02) * mm});
            skLineSegment(sketch, "E2950", {"start": v(2387.7, 514.02) * mm, "end": v(2369.7, 514.02) * mm});
            skArc(sketch, "E2951", {"start": v(2369.7, 514.02) * mm, "mid": v(2366.7, 517.03) * mm, "end": v(2369.7, 520.04) * mm});
            skLineSegment(sketch, "E2952", {"start": v(2369.7, 520.04) * mm, "end": v(2369.7, 617.84) * mm});
            skLineSegment(sketch, "E2953", {"start": v(2369.7, 617.84) * mm, "end": v(2325.72, 617.84) * mm});
            skArc(sketch, "E2954", {"start": v(2325.72, 617.84) * mm, "mid": v(2322.71, 614.83) * mm, "end": v(2319.7, 617.84) * mm});
            skLineSegment(sketch, "E2955", {"start": v(2319.7, 617.84) * mm, "end": v(2319.7, 777.84) * mm});
            skArc(sketch, "E2956", {"start": v(2319.7, 777.84) * mm, "mid": v(2322.71, 780.85) * mm, "end": v(2325.72, 777.84) * mm});
            skLineSegment(sketch, "E2957", {"start": v(2325.72, 777.84) * mm, "end": v(2369.7, 777.84) * mm});
            skLineSegment(sketch, "E2958", {"start": v(2369.7, 777.84) * mm, "end": v(2369.7, 875.14) * mm});
            skArc(sketch, "E2959", {"start": v(2369.7, 875.14) * mm, "mid": v(2366.7, 878.15) * mm, "end": v(2369.7, 881.16) * mm});
            skLineSegment(sketch, "E2960", {"start": v(2369.7, 881.16) * mm, "end": v(2387.7, 881.16) * mm});
            skLineSegment(sketch, "E2961", {"start": v(2387.7, 881.16) * mm, "end": v(2387.7, 1000.66) * mm});
            skLineSegment(sketch, "E2962", {"start": v(2387.7, 1000.66) * mm, "end": v(2369.7, 1000.66) * mm});
            skArc(sketch, "E2963", {"start": v(2369.7, 1000.66) * mm, "mid": v(2366.7, 1003.67) * mm, "end": v(2369.7, 1006.68) * mm});
            skLineSegment(sketch, "E2964", {"start": v(2369.7, 1006.68) * mm, "end": v(2369.7, 1175.14) * mm});
            skArc(sketch, "E2965", {"start": v(2369.7, 1175.14) * mm, "mid": v(2366.7, 1178.15) * mm, "end": v(2369.7, 1181.16) * mm});
            skLineSegment(sketch, "E2966", {"start": v(2369.7, 1181.16) * mm, "end": v(2387.7, 1181.16) * mm});
            skLineSegment(sketch, "E2967", {"start": v(2387.7, 1181.16) * mm, "end": v(2387.7, 1300.66) * mm});
            skLineSegment(sketch, "E2968", {"start": v(2387.7, 1300.66) * mm, "end": v(2369.7, 1300.66) * mm});
            skArc(sketch, "E2969", {"start": v(2369.7, 1300.66) * mm, "mid": v(2366.7, 1303.67) * mm, "end": v(2369.7, 1306.68) * mm});
            skLineSegment(sketch, "E2970", {"start": v(2369.7, 1306.68) * mm, "end": v(2369.7, 1475.14) * mm});
            skArc(sketch, "E2971", {"start": v(2369.7, 1475.14) * mm, "mid": v(2366.7, 1478.15) * mm, "end": v(2369.7, 1481.16) * mm});
            skLineSegment(sketch, "E2972", {"start": v(2369.7, 1481.16) * mm, "end": v(2387.7, 1481.16) * mm});
            skLineSegment(sketch, "E2973", {"start": v(2387.7, 1481.16) * mm, "end": v(2387.7, 1600.66) * mm});
            skLineSegment(sketch, "E2974", {"start": v(2387.7, 1600.66) * mm, "end": v(2369.7, 1600.66) * mm});
            skArc(sketch, "E2975", {"start": v(2369.7, 1600.66) * mm, "mid": v(2366.7, 1603.67) * mm, "end": v(2369.7, 1606.68) * mm});
            skLineSegment(sketch, "E2976", {"start": v(2369.7, 1606.68) * mm, "end": v(2369.7, 1767.36) * mm});
            skLineSegment(sketch, "E2977", {"start": v(2369.7, 1767.36) * mm, "end": v(2325.2, 1767.36) * mm});
            skLineSegment(sketch, "E2978", {"start": v(2325.2, 1767.36) * mm, "end": v(2325.2, 1717.36) * mm});
            skArc(sketch, "E2979", {"start": v(2325.2, 1717.36) * mm, "mid": v(2322.2, 1714.35) * mm, "end": v(2319.18, 1717.36) * mm});
            skLineSegment(sketch, "E2980", {"start": v(2319.18, 1717.36) * mm, "end": v(2270.72, 1717.36) * mm});
            skArc(sketch, "E2981", {"start": v(2270.72, 1717.36) * mm, "mid": v(2267.71, 1714.35) * mm, "end": v(2264.7, 1717.36) * mm});
            skLineSegment(sketch, "E2982", {"start": v(2264.7, 1717.36) * mm, "end": v(2264.7, 1767.36) * mm});
            skLineSegment(sketch, "E2983", {"start": v(2264.7, 1767.36) * mm, "end": v(2225.2, 1767.36) * mm});
            skLineSegment(sketch, "E2984", {"start": v(2225.2, 1767.36) * mm, "end": v(2225.2, 1717.36) * mm});
            skArc(sketch, "E2985", {"start": v(2225.2, 1717.36) * mm, "mid": v(2222.2, 1714.35) * mm, "end": v(2219.18, 1717.36) * mm});
            skLineSegment(sketch, "E2986", {"start": v(2219.18, 1717.36) * mm, "end": v(2170.72, 1717.36) * mm});
            skArc(sketch, "E2987", {"start": v(2170.72, 1717.36) * mm, "mid": v(2167.71, 1714.35) * mm, "end": v(2164.7, 1717.36) * mm});
            skLineSegment(sketch, "E2988", {"start": v(2164.7, 1717.36) * mm, "end": v(2164.7, 1767.36) * mm});
            skLineSegment(sketch, "E2989", {"start": v(2164.7, 1767.36) * mm, "end": v(2120.2, 1767.36) * mm});
            skLineSegment(sketch, "E2990", {"start": v(2120.2, 1767.36) * mm, "end": v(2120.2, 1606.68) * mm});
            skArc(sketch, "E2991", {"start": v(2120.2, 1606.68) * mm, "mid": v(2123.21, 1603.67) * mm, "end": v(2120.2, 1600.66) * mm});
            skLineSegment(sketch, "E2992", {"start": v(2120.2, 1600.66) * mm, "end": v(2102.2, 1600.66) * mm});
            skLineSegment(sketch, "E2993", {"start": v(2102.2, 1600.66) * mm, "end": v(2102.2, 1481.16) * mm});
            skLineSegment(sketch, "E2994", {"start": v(2102.2, 1481.16) * mm, "end": v(2120.2, 1481.16) * mm});
            skArc(sketch, "E2995", {"start": v(2120.2, 1481.16) * mm, "mid": v(2123.21, 1478.15) * mm, "end": v(2120.2, 1475.14) * mm});
            skLineSegment(sketch, "E2996", {"start": v(2120.2, 1475.14) * mm, "end": v(2120.2, 1306.68) * mm});
            skArc(sketch, "E2997", {"start": v(2120.2, 1306.68) * mm, "mid": v(2123.21, 1303.67) * mm, "end": v(2120.2, 1300.66) * mm});
            skLineSegment(sketch, "E2998", {"start": v(2120.2, 1300.66) * mm, "end": v(2102.2, 1300.66) * mm});
            skLineSegment(sketch, "E2999", {"start": v(2102.2, 1300.66) * mm, "end": v(2102.2, 1181.16) * mm});
            skLineSegment(sketch, "E3000", {"start": v(2102.2, 1181.16) * mm, "end": v(2120.2, 1181.16) * mm});
            skArc(sketch, "E3001", {"start": v(2120.2, 1181.16) * mm, "mid": v(2123.21, 1178.15) * mm, "end": v(2120.2, 1175.14) * mm});
            skLineSegment(sketch, "E3002", {"start": v(2120.2, 1175.14) * mm, "end": v(2120.2, 1006.68) * mm});
            skArc(sketch, "E3003", {"start": v(2120.2, 1006.68) * mm, "mid": v(2123.21, 1003.67) * mm, "end": v(2120.2, 1000.66) * mm});
            skLineSegment(sketch, "E3004", {"start": v(2120.2, 1000.66) * mm, "end": v(2102.2, 1000.66) * mm});
            skLineSegment(sketch, "E3005", {"start": v(2102.2, 1000.66) * mm, "end": v(2102.2, 881.16) * mm});
            skLineSegment(sketch, "E3006", {"start": v(2102.2, 881.16) * mm, "end": v(2120.2, 881.16) * mm});
            skArc(sketch, "E3007", {"start": v(2120.2, 881.16) * mm, "mid": v(2123.21, 878.15) * mm, "end": v(2120.2, 875.14) * mm});
            skLineSegment(sketch, "E3008", {"start": v(2120.2, 875.14) * mm, "end": v(2120.2, 763.36) * mm});
            skArc(sketch, "E3009", {"start": v(2120.2, 763.36) * mm, "mid": v(2123.21, 760.35) * mm, "end": v(2120.2, 757.34) * mm});
            skLineSegment(sketch, "E3010", {"start": v(2120.2, 757.34) * mm, "end": v(2102.2, 757.34) * mm});
            skLineSegment(sketch, "E3011", {"start": v(2102.2, 757.34) * mm, "end": v(2102.2, 637.84) * mm});
            skLineSegment(sketch, "E3012", {"start": v(2102.2, 637.84) * mm, "end": v(2120.2, 637.84) * mm});
            skArc(sketch, "E3013", {"start": v(2120.2, 637.84) * mm, "mid": v(2123.21, 634.83) * mm, "end": v(2120.2, 631.82) * mm});
            skLineSegment(sketch, "E3014", {"start": v(2120.2, 631.82) * mm, "end": v(2120.2, 520.04) * mm});
            skArc(sketch, "E3015", {"start": v(2120.2, 520.04) * mm, "mid": v(2123.21, 517.03) * mm, "end": v(2120.2, 514.02) * mm});
            skLineSegment(sketch, "E3016", {"start": v(2120.2, 514.02) * mm, "end": v(2102.2, 514.02) * mm});
            skLineSegment(sketch, "E3017", {"start": v(2102.2, 514.02) * mm, "end": v(2102.2, 394.52) * mm});
            skLineSegment(sketch, "E3018", {"start": v(2102.2, 394.52) * mm, "end": v(2120.2, 394.52) * mm});
            skArc(sketch, "E3019", {"start": v(2120.2, 394.52) * mm, "mid": v(2123.21, 391.51) * mm, "end": v(2120.2, 388.5) * mm});
            skLineSegment(sketch, "E3020", {"start": v(2120.2, 388.5) * mm, "end": v(2120.2, 381.22) * mm});
            skLineSegment(sketch, "E3021", {"start": v(2120.2, 381.22) * mm, "end": v(2159.18, 381.22) * mm});
            skArc(sketch, "E3022", {"start": v(2159.18, 381.22) * mm, "mid": v(2162.2, 384.23) * mm, "end": v(2165.2, 381.22) * mm});
            skLineSegment(sketch, "E3023", {"start": v(2165.2, 381.22) * mm, "end": v(2165.2, 331.22) * mm});
            skLineSegment(sketch, "E3024", {"start": v(2165.2, 331.22) * mm, "end": v(2224.7, 331.22) * mm});
            skLineSegment(sketch, "E3025", {"start": v(2224.7, 331.22) * mm, "end": v(2224.7, 381.22) * mm});
            skArc(sketch, "E3026", {"start": v(2224.7, 381.22) * mm, "mid": v(2227.71, 384.23) * mm, "end": v(2230.72, 381.22) * mm});
            skLineSegment(sketch, "E3027", {"start": v(2230.72, 381.22) * mm, "end": v(2259.18, 381.22) * mm});
            skArc(sketch, "E3028", {"start": v(2259.18, 381.22) * mm, "mid": v(2262.2, 384.23) * mm, "end": v(2265.2, 381.22) * mm});
            skLineSegment(sketch, "E3029", {"start": v(2265.2, 381.22) * mm, "end": v(2265.2, 331.22) * mm});
            skLineSegment(sketch, "E3030", {"start": v(2265.2, 331.22) * mm, "end": v(2324.7, 331.22) * mm});
            skLineSegment(sketch, "E3031", {"start": v(1877.69, 60.89) * mm, "end": v(1877.69, 42.89) * mm});
            skLineSegment(sketch, "E3032", {"start": v(1877.69, 42.89) * mm, "end": v(1837.69, 42.89) * mm});
            skLineSegment(sketch, "E3033", {"start": v(1837.69, 42.89) * mm, "end": v(1837.69, 60.89) * mm});
            skLineSegment(sketch, "E3034", {"start": v(1837.69, 60.89) * mm, "end": v(1877.69, 60.89) * mm});
            skLineSegment(sketch, "E3035", {"start": v(2177.69, 60.89) * mm, "end": v(2177.69, 42.89) * mm});
            skLineSegment(sketch, "E3036", {"start": v(2177.69, 42.89) * mm, "end": v(2137.69, 42.89) * mm});
            skLineSegment(sketch, "E3037", {"start": v(2137.69, 42.89) * mm, "end": v(2137.69, 60.89) * mm});
            skLineSegment(sketch, "E3038", {"start": v(2137.69, 60.89) * mm, "end": v(2177.69, 60.89) * mm});
            skLineSegment(sketch, "E3039", {"start": v(2397.69, 60.89) * mm, "end": v(2397.69, 42.89) * mm});
            skLineSegment(sketch, "E3040", {"start": v(2397.69, 42.89) * mm, "end": v(2357.69, 42.89) * mm});
            skLineSegment(sketch, "E3041", {"start": v(2357.69, 42.89) * mm, "end": v(2357.69, 60.89) * mm});
            skLineSegment(sketch, "E3042", {"start": v(2357.69, 60.89) * mm, "end": v(2397.69, 60.89) * mm});
            skLineSegment(sketch, "E3043", {"start": v(1877.69, 292.89) * mm, "end": v(1877.69, 274.89) * mm});
            skLineSegment(sketch, "E3044", {"start": v(1877.69, 274.89) * mm, "end": v(1837.69, 274.89) * mm});
            skLineSegment(sketch, "E3045", {"start": v(1837.69, 274.89) * mm, "end": v(1837.69, 292.89) * mm});
            skLineSegment(sketch, "E3046", {"start": v(1837.69, 292.89) * mm, "end": v(1877.69, 292.89) * mm});
            skLineSegment(sketch, "E3047", {"start": v(2177.69, 292.89) * mm, "end": v(2177.69, 274.89) * mm});
            skLineSegment(sketch, "E3048", {"start": v(2177.69, 274.89) * mm, "end": v(2137.69, 274.89) * mm});
            skLineSegment(sketch, "E3049", {"start": v(2137.69, 274.89) * mm, "end": v(2137.69, 292.89) * mm});
            skLineSegment(sketch, "E3050", {"start": v(2137.69, 292.89) * mm, "end": v(2177.69, 292.89) * mm});
            skLineSegment(sketch, "E3051", {"start": v(2397.69, 292.89) * mm, "end": v(2397.69, 274.89) * mm});
            skLineSegment(sketch, "E3052", {"start": v(2397.69, 274.89) * mm, "end": v(2357.69, 274.89) * mm});
            skLineSegment(sketch, "E3053", {"start": v(2357.69, 274.89) * mm, "end": v(2357.69, 292.89) * mm});
            skLineSegment(sketch, "E3054", {"start": v(2357.69, 292.89) * mm, "end": v(2397.69, 292.89) * mm});
            skLineSegment(sketch, "E3055", {"start": v(2657.45, 360.65) * mm, "end": v(2675.45, 360.65) * mm});
            skLineSegment(sketch, "E3056", {"start": v(2675.45, 360.65) * mm, "end": v(2675.45, 320.65) * mm});
            skLineSegment(sketch, "E3057", {"start": v(2675.45, 320.65) * mm, "end": v(2657.45, 320.65) * mm});
            skLineSegment(sketch, "E3058", {"start": v(2657.45, 320.65) * mm, "end": v(2657.45, 360.65) * mm});
            skLineSegment(sketch, "E3059", {"start": v(2443.45, 360.65) * mm, "end": v(2443.45, 320.65) * mm});
            skLineSegment(sketch, "E3060", {"start": v(2443.45, 320.65) * mm, "end": v(2425.45, 320.65) * mm});
            skLineSegment(sketch, "E3061", {"start": v(2425.45, 320.65) * mm, "end": v(2425.45, 360.65) * mm});
            skLineSegment(sketch, "E3062", {"start": v(2425.45, 360.65) * mm, "end": v(2443.45, 360.65) * mm});
            skLineSegment(sketch, "E3063", {"start": v(2657.45, 580.65) * mm, "end": v(2675.45, 580.65) * mm});
            skLineSegment(sketch, "E3064", {"start": v(2675.45, 580.65) * mm, "end": v(2675.45, 540.65) * mm});
            skLineSegment(sketch, "E3065", {"start": v(2675.45, 540.65) * mm, "end": v(2657.45, 540.65) * mm});
            skLineSegment(sketch, "E3066", {"start": v(2657.45, 540.65) * mm, "end": v(2657.45, 580.65) * mm});
            skLineSegment(sketch, "E3067", {"start": v(2443.45, 580.65) * mm, "end": v(2443.45, 540.65) * mm});
            skLineSegment(sketch, "E3068", {"start": v(2443.45, 540.65) * mm, "end": v(2425.45, 540.65) * mm});
            skLineSegment(sketch, "E3069", {"start": v(2425.45, 540.65) * mm, "end": v(2425.45, 580.65) * mm});
            skLineSegment(sketch, "E3070", {"start": v(2425.45, 580.65) * mm, "end": v(2443.45, 580.65) * mm});
            skLineSegment(sketch, "E3071", {"start": v(2657.45, 880.65) * mm, "end": v(2675.45, 880.65) * mm});
            skLineSegment(sketch, "E3072", {"start": v(2675.45, 880.65) * mm, "end": v(2675.45, 840.65) * mm});
            skLineSegment(sketch, "E3073", {"start": v(2675.45, 840.65) * mm, "end": v(2657.45, 840.65) * mm});
            skLineSegment(sketch, "E3074", {"start": v(2657.45, 840.65) * mm, "end": v(2657.45, 880.65) * mm});
            skLineSegment(sketch, "E3075", {"start": v(2443.45, 880.65) * mm, "end": v(2443.45, 840.65) * mm});
            skLineSegment(sketch, "E3076", {"start": v(2443.45, 840.65) * mm, "end": v(2425.45, 840.65) * mm});
            skLineSegment(sketch, "E3077", {"start": v(2425.45, 840.65) * mm, "end": v(2425.45, 880.65) * mm});
            skLineSegment(sketch, "E3078", {"start": v(2425.45, 880.65) * mm, "end": v(2443.45, 880.65) * mm});
            skLineSegment(sketch, "E3079", {"start": v(2657.45, 1440.65) * mm, "end": v(2657.45, 1480.65) * mm});
            skLineSegment(sketch, "E3080", {"start": v(2657.45, 1480.65) * mm, "end": v(2675.45, 1480.65) * mm});
            skLineSegment(sketch, "E3081", {"start": v(2675.45, 1480.65) * mm, "end": v(2675.45, 1440.65) * mm});
            skLineSegment(sketch, "E3082", {"start": v(2675.45, 1440.65) * mm, "end": v(2657.45, 1440.65) * mm});
            skLineSegment(sketch, "E3083", {"start": v(2657.45, 1180.65) * mm, "end": v(2675.45, 1180.65) * mm});
            skLineSegment(sketch, "E3084", {"start": v(2675.45, 1180.65) * mm, "end": v(2675.45, 1140.65) * mm});
            skLineSegment(sketch, "E3085", {"start": v(2675.45, 1140.65) * mm, "end": v(2657.45, 1140.65) * mm});
            skLineSegment(sketch, "E3086", {"start": v(2657.45, 1140.65) * mm, "end": v(2657.45, 1180.65) * mm});
            skLineSegment(sketch, "E3087", {"start": v(2443.45, 1440.65) * mm, "end": v(2425.45, 1440.65) * mm});
            skLineSegment(sketch, "E3088", {"start": v(2425.45, 1440.65) * mm, "end": v(2425.45, 1480.65) * mm});
            skLineSegment(sketch, "E3089", {"start": v(2425.45, 1480.65) * mm, "end": v(2443.45, 1480.65) * mm});
            skLineSegment(sketch, "E3090", {"start": v(2443.45, 1480.65) * mm, "end": v(2443.45, 1440.65) * mm});
            skLineSegment(sketch, "E3091", {"start": v(2530.45, 1169.65) * mm, "end": v(2570.45, 1169.65) * mm});
            skLineSegment(sketch, "E3092", {"start": v(2570.45, 1169.65) * mm, "end": v(2570.45, 1151.65) * mm});
            skLineSegment(sketch, "E3093", {"start": v(2570.45, 1151.65) * mm, "end": v(2530.45, 1151.65) * mm});
            skLineSegment(sketch, "E3094", {"start": v(2530.45, 1151.65) * mm, "end": v(2530.45, 1169.65) * mm});
            skLineSegment(sketch, "E3095", {"start": v(2443.45, 1180.65) * mm, "end": v(2443.45, 1140.65) * mm});
            skLineSegment(sketch, "E3096", {"start": v(2443.45, 1140.65) * mm, "end": v(2425.45, 1140.65) * mm});
            skLineSegment(sketch, "E3097", {"start": v(2425.45, 1140.65) * mm, "end": v(2425.45, 1180.65) * mm});
            skLineSegment(sketch, "E3098", {"start": v(2425.45, 1180.65) * mm, "end": v(2443.45, 1180.65) * mm});
            skArc(sketch, "E3099", {"start": v(2526.72, 1469.9) * mm, "mid": v(2523.34, 1472.91) * mm, "end": v(2520.2, 1469.65) * mm});
            skLineSegment(sketch, "E3100", {"start": v(2520.2, 1469.65) * mm, "end": v(2520.2, 1451.65) * mm});
            skArc(sketch, "E3101", {"start": v(2520.2, 1451.65) * mm, "mid": v(2523.34, 1448.39) * mm, "end": v(2526.72, 1451.4) * mm});
            skLineSegment(sketch, "E3102", {"start": v(2526.72, 1451.4) * mm, "end": v(2574.19, 1451.4) * mm});
            skArc(sketch, "E3103", {"start": v(2574.19, 1451.4) * mm, "mid": v(2577.57, 1448.4) * mm, "end": v(2580.7, 1451.65) * mm});
            skLineSegment(sketch, "E3104", {"start": v(2580.7, 1451.65) * mm, "end": v(2580.7, 1469.65) * mm});
            skArc(sketch, "E3105", {"start": v(2580.7, 1469.65) * mm, "mid": v(2577.57, 1472.92) * mm, "end": v(2574.19, 1469.9) * mm});
            skLineSegment(sketch, "E3106", {"start": v(2574.19, 1469.9) * mm, "end": v(2526.72, 1469.9) * mm});
            skArc(sketch, "E3107", {"start": v(2526.72, 869.9) * mm, "mid": v(2523.34, 872.91) * mm, "end": v(2520.2, 869.65) * mm});
            skLineSegment(sketch, "E3108", {"start": v(2520.2, 869.65) * mm, "end": v(2520.2, 851.65) * mm});
            skArc(sketch, "E3109", {"start": v(2520.2, 851.65) * mm, "mid": v(2523.34, 848.39) * mm, "end": v(2526.72, 851.4) * mm});
            skLineSegment(sketch, "E3110", {"start": v(2526.72, 851.4) * mm, "end": v(2574.19, 851.4) * mm});
            skArc(sketch, "E3111", {"start": v(2574.19, 851.4) * mm, "mid": v(2577.57, 848.4) * mm, "end": v(2580.7, 851.65) * mm});
            skLineSegment(sketch, "E3112", {"start": v(2580.7, 851.65) * mm, "end": v(2580.7, 869.65) * mm});
            skArc(sketch, "E3113", {"start": v(2580.7, 869.65) * mm, "mid": v(2577.57, 872.92) * mm, "end": v(2574.19, 869.9) * mm});
            skLineSegment(sketch, "E3114", {"start": v(2574.19, 869.9) * mm, "end": v(2526.72, 869.9) * mm});
            skArc(sketch, "E3115", {"start": v(2526.72, 349.9) * mm, "mid": v(2523.34, 352.91) * mm, "end": v(2520.2, 349.65) * mm});
            skLineSegment(sketch, "E3116", {"start": v(2520.2, 349.65) * mm, "end": v(2520.2, 331.65) * mm});
            skArc(sketch, "E3117", {"start": v(2520.2, 331.65) * mm, "mid": v(2523.34, 328.39) * mm, "end": v(2526.72, 331.4) * mm});
            skLineSegment(sketch, "E3118", {"start": v(2526.72, 331.4) * mm, "end": v(2574.19, 331.4) * mm});
            skArc(sketch, "E3119", {"start": v(2574.19, 331.4) * mm, "mid": v(2577.57, 328.4) * mm, "end": v(2580.7, 331.65) * mm});
            skLineSegment(sketch, "E3120", {"start": v(2580.7, 331.65) * mm, "end": v(2580.7, 349.65) * mm});
            skArc(sketch, "E3121", {"start": v(2580.7, 349.65) * mm, "mid": v(2577.57, 352.92) * mm, "end": v(2574.19, 349.9) * mm});
            skLineSegment(sketch, "E3122", {"start": v(2574.19, 349.9) * mm, "end": v(2526.72, 349.9) * mm});
            skArc(sketch, "E3123", {"start": v(2425.45, 208.14) * mm, "mid": v(2422.19, 205) * mm, "end": v(2425.2, 201.62) * mm});
            skLineSegment(sketch, "E3124", {"start": v(2425.2, 201.62) * mm, "end": v(2425.2, 134.16) * mm});
            skArc(sketch, "E3125", {"start": v(2425.2, 134.16) * mm, "mid": v(2422.2, 130.78) * mm, "end": v(2425.45, 127.64) * mm});
            skLineSegment(sketch, "E3126", {"start": v(2425.45, 127.64) * mm, "end": v(2443.45, 127.64) * mm});
            skArc(sketch, "E3127", {"start": v(2443.45, 127.64) * mm, "mid": v(2446.72, 130.78) * mm, "end": v(2443.7, 134.16) * mm});
            skLineSegment(sketch, "E3128", {"start": v(2443.7, 134.16) * mm, "end": v(2443.7, 201.62) * mm});
            skArc(sketch, "E3129", {"start": v(2443.7, 201.62) * mm, "mid": v(2446.71, 205) * mm, "end": v(2443.45, 208.14) * mm});
            skLineSegment(sketch, "E3130", {"start": v(2443.45, 208.14) * mm, "end": v(2425.45, 208.14) * mm});
            skLineSegment(sketch, "E3131", {"start": v(1578.95, 959.62) * mm, "end": v(1578.95, 919.62) * mm});
            skLineSegment(sketch, "E3132", {"start": v(1578.95, 919.62) * mm, "end": v(1560.95, 919.62) * mm});
            skLineSegment(sketch, "E3133", {"start": v(1560.95, 919.62) * mm, "end": v(1560.95, 959.62) * mm});
            skLineSegment(sketch, "E3134", {"start": v(1560.95, 959.62) * mm, "end": v(1578.95, 959.62) * mm});
            skLineSegment(sketch, "E3135", {"start": v(1810.95, 959.62) * mm, "end": v(1810.95, 919.62) * mm});
            skLineSegment(sketch, "E3136", {"start": v(1810.95, 919.62) * mm, "end": v(1792.95, 919.62) * mm});
            skLineSegment(sketch, "E3137", {"start": v(1792.95, 919.62) * mm, "end": v(1792.95, 959.62) * mm});
            skLineSegment(sketch, "E3138", {"start": v(1792.95, 959.62) * mm, "end": v(1810.95, 959.62) * mm});
            skLineSegment(sketch, "E3139", {"start": v(1578.95, 1259.62) * mm, "end": v(1578.95, 1219.62) * mm});
            skLineSegment(sketch, "E3140", {"start": v(1578.95, 1219.62) * mm, "end": v(1560.95, 1219.62) * mm});
            skLineSegment(sketch, "E3141", {"start": v(1560.95, 1219.62) * mm, "end": v(1560.95, 1259.62) * mm});
            skLineSegment(sketch, "E3142", {"start": v(1560.95, 1259.62) * mm, "end": v(1578.95, 1259.62) * mm});
            skLineSegment(sketch, "E3143", {"start": v(1705.95, 1248.62) * mm, "end": v(1705.95, 1230.62) * mm});
            skLineSegment(sketch, "E3144", {"start": v(1705.95, 1230.62) * mm, "end": v(1665.95, 1230.62) * mm});
            skLineSegment(sketch, "E3145", {"start": v(1665.95, 1230.62) * mm, "end": v(1665.95, 1248.62) * mm});
            skLineSegment(sketch, "E3146", {"start": v(1665.95, 1248.62) * mm, "end": v(1705.95, 1248.62) * mm});
            skLineSegment(sketch, "E3147", {"start": v(1810.95, 1259.62) * mm, "end": v(1810.95, 1219.62) * mm});
            skLineSegment(sketch, "E3148", {"start": v(1810.95, 1219.62) * mm, "end": v(1792.95, 1219.62) * mm});
            skLineSegment(sketch, "E3149", {"start": v(1792.95, 1219.62) * mm, "end": v(1792.95, 1259.62) * mm});
            skLineSegment(sketch, "E3150", {"start": v(1792.95, 1259.62) * mm, "end": v(1810.95, 1259.62) * mm});
            skLineSegment(sketch, "E3151", {"start": v(1578.95, 1559.62) * mm, "end": v(1578.95, 1519.62) * mm});
            skLineSegment(sketch, "E3152", {"start": v(1578.95, 1519.62) * mm, "end": v(1560.95, 1519.62) * mm});
            skLineSegment(sketch, "E3153", {"start": v(1560.95, 1519.62) * mm, "end": v(1560.95, 1559.62) * mm});
            skLineSegment(sketch, "E3154", {"start": v(1560.95, 1559.62) * mm, "end": v(1578.95, 1559.62) * mm});
            skLineSegment(sketch, "E3155", {"start": v(1810.95, 1559.62) * mm, "end": v(1810.95, 1519.62) * mm});
            skLineSegment(sketch, "E3156", {"start": v(1810.95, 1519.62) * mm, "end": v(1792.95, 1519.62) * mm});
            skLineSegment(sketch, "E3157", {"start": v(1792.95, 1519.62) * mm, "end": v(1792.95, 1559.62) * mm});
            skLineSegment(sketch, "E3158", {"start": v(1792.95, 1559.62) * mm, "end": v(1810.95, 1559.62) * mm});
            skLineSegment(sketch, "E3159", {"start": v(1578.95, 1859.62) * mm, "end": v(1578.95, 1819.62) * mm});
            skLineSegment(sketch, "E3160", {"start": v(1578.95, 1819.62) * mm, "end": v(1560.95, 1819.62) * mm});
            skLineSegment(sketch, "E3161", {"start": v(1560.95, 1819.62) * mm, "end": v(1560.95, 1859.62) * mm});
            skLineSegment(sketch, "E3162", {"start": v(1560.95, 1859.62) * mm, "end": v(1578.95, 1859.62) * mm});
            skLineSegment(sketch, "E3163", {"start": v(1578.95, 2079.62) * mm, "end": v(1578.95, 2039.62) * mm});
            skLineSegment(sketch, "E3164", {"start": v(1578.95, 2039.62) * mm, "end": v(1560.95, 2039.62) * mm});
            skLineSegment(sketch, "E3165", {"start": v(1560.95, 2039.62) * mm, "end": v(1560.95, 2079.62) * mm});
            skLineSegment(sketch, "E3166", {"start": v(1560.95, 2079.62) * mm, "end": v(1578.95, 2079.62) * mm});
            skLineSegment(sketch, "E3167", {"start": v(1810.95, 1859.62) * mm, "end": v(1810.95, 1819.62) * mm});
            skLineSegment(sketch, "E3168", {"start": v(1810.95, 1819.62) * mm, "end": v(1792.95, 1819.62) * mm});
            skLineSegment(sketch, "E3169", {"start": v(1792.95, 1819.62) * mm, "end": v(1792.95, 1859.62) * mm});
            skLineSegment(sketch, "E3170", {"start": v(1792.95, 1859.62) * mm, "end": v(1810.95, 1859.62) * mm});
            skLineSegment(sketch, "E3171", {"start": v(2358.72, 2125.39) * mm, "end": v(2398.72, 2125.39) * mm});
            skLineSegment(sketch, "E3172", {"start": v(2398.72, 2125.39) * mm, "end": v(2398.72, 2107.39) * mm});
            skLineSegment(sketch, "E3173", {"start": v(2398.72, 2107.39) * mm, "end": v(2358.72, 2107.39) * mm});
            skLineSegment(sketch, "E3174", {"start": v(2358.72, 2107.39) * mm, "end": v(2358.72, 2125.39) * mm});
            skLineSegment(sketch, "E3175", {"start": v(1810.95, 2079.62) * mm, "end": v(1810.95, 2039.62) * mm});
            skLineSegment(sketch, "E3176", {"start": v(1810.95, 2039.62) * mm, "end": v(1792.95, 2039.62) * mm});
            skLineSegment(sketch, "E3177", {"start": v(1792.95, 2039.62) * mm, "end": v(1792.95, 2079.62) * mm});
            skLineSegment(sketch, "E3178", {"start": v(1792.95, 2079.62) * mm, "end": v(1810.95, 2079.62) * mm});
            skLineSegment(sketch, "E3179", {"start": v(2358.72, 2339.39) * mm, "end": v(2358.72, 2357.39) * mm});
            skLineSegment(sketch, "E3180", {"start": v(2358.72, 2357.39) * mm, "end": v(2398.72, 2357.39) * mm});
            skLineSegment(sketch, "E3181", {"start": v(2398.72, 2357.39) * mm, "end": v(2398.72, 2339.39) * mm});
            skLineSegment(sketch, "E3182", {"start": v(2398.72, 2339.39) * mm, "end": v(2358.72, 2339.39) * mm});
            skLineSegment(sketch, "E3183", {"start": v(1878.72, 2125.39) * mm, "end": v(1878.72, 2107.39) * mm});
            skLineSegment(sketch, "E3184", {"start": v(1878.72, 2107.39) * mm, "end": v(1838.72, 2107.39) * mm});
            skLineSegment(sketch, "E3185", {"start": v(1838.72, 2107.39) * mm, "end": v(1838.72, 2125.39) * mm});
            skLineSegment(sketch, "E3186", {"start": v(1838.72, 2125.39) * mm, "end": v(1878.72, 2125.39) * mm});
            skLineSegment(sketch, "E3187", {"start": v(1878.72, 2339.39) * mm, "end": v(1838.72, 2339.39) * mm});
            skLineSegment(sketch, "E3188", {"start": v(1838.72, 2339.39) * mm, "end": v(1838.72, 2357.39) * mm});
            skLineSegment(sketch, "E3189", {"start": v(1838.72, 2357.39) * mm, "end": v(1878.72, 2357.39) * mm});
            skLineSegment(sketch, "E3190", {"start": v(1878.72, 2357.39) * mm, "end": v(1878.72, 2339.39) * mm});
            skLineSegment(sketch, "E3191", {"start": v(2058.72, 2125.39) * mm, "end": v(2098.72, 2125.39) * mm});
            skLineSegment(sketch, "E3192", {"start": v(2098.72, 2125.39) * mm, "end": v(2098.72, 2107.39) * mm});
            skLineSegment(sketch, "E3193", {"start": v(2098.72, 2107.39) * mm, "end": v(2058.72, 2107.39) * mm});
            skLineSegment(sketch, "E3194", {"start": v(2058.72, 2107.39) * mm, "end": v(2058.72, 2125.39) * mm});
            skLineSegment(sketch, "E3195", {"start": v(2058.72, 2339.39) * mm, "end": v(2058.72, 2357.39) * mm});
            skLineSegment(sketch, "E3196", {"start": v(2058.72, 2357.39) * mm, "end": v(2098.72, 2357.39) * mm});
            skLineSegment(sketch, "E3197", {"start": v(2098.72, 2357.39) * mm, "end": v(2098.72, 2339.39) * mm});
            skLineSegment(sketch, "E3198", {"start": v(2098.72, 2339.39) * mm, "end": v(2058.72, 2339.39) * mm});
            skArc(sketch, "E3199", {"start": v(2387.72, 2202.14) * mm, "mid": v(2390.99, 2205.28) * mm, "end": v(2387.97, 2208.66) * mm});
            skLineSegment(sketch, "E3200", {"start": v(2387.97, 2208.66) * mm, "end": v(2387.97, 2256.12) * mm});
            skArc(sketch, "E3201", {"start": v(2387.97, 2256.12) * mm, "mid": v(2390.98, 2259.5) * mm, "end": v(2387.72, 2262.64) * mm});
            skLineSegment(sketch, "E3202", {"start": v(2387.72, 2262.64) * mm, "end": v(2369.72, 2262.64) * mm});
            skArc(sketch, "E3203", {"start": v(2369.72, 2262.64) * mm, "mid": v(2366.46, 2259.5) * mm, "end": v(2369.47, 2256.12) * mm});
            skLineSegment(sketch, "E3204", {"start": v(2369.47, 2256.12) * mm, "end": v(2369.47, 2208.66) * mm});
            skArc(sketch, "E3205", {"start": v(2369.47, 2208.66) * mm, "mid": v(2366.46, 2205.28) * mm, "end": v(2369.72, 2202.14) * mm});
            skLineSegment(sketch, "E3206", {"start": v(2369.72, 2202.14) * mm, "end": v(2387.72, 2202.14) * mm});
            skArc(sketch, "E3207", {"start": v(1867.72, 2202.14) * mm, "mid": v(1870.99, 2205.28) * mm, "end": v(1867.97, 2208.66) * mm});
            skLineSegment(sketch, "E3208", {"start": v(1867.97, 2208.66) * mm, "end": v(1867.97, 2256.12) * mm});
            skArc(sketch, "E3209", {"start": v(1867.97, 2256.12) * mm, "mid": v(1870.98, 2259.5) * mm, "end": v(1867.72, 2262.64) * mm});
            skLineSegment(sketch, "E3210", {"start": v(1867.72, 2262.64) * mm, "end": v(1849.72, 2262.64) * mm});
            skArc(sketch, "E3211", {"start": v(1849.72, 2262.64) * mm, "mid": v(1846.46, 2259.5) * mm, "end": v(1849.47, 2256.12) * mm});
            skLineSegment(sketch, "E3212", {"start": v(1849.47, 2256.12) * mm, "end": v(1849.47, 2208.66) * mm});
            skArc(sketch, "E3213", {"start": v(1849.47, 2208.66) * mm, "mid": v(1846.46, 2205.28) * mm, "end": v(1849.72, 2202.14) * mm});
            skLineSegment(sketch, "E3214", {"start": v(1849.72, 2202.14) * mm, "end": v(1867.72, 2202.14) * mm});
            skArc(sketch, "E3215", {"start": v(1726.2, 2125.39) * mm, "mid": v(1723.07, 2128.65) * mm, "end": v(1719.69, 2125.64) * mm});
            skLineSegment(sketch, "E3216", {"start": v(1719.69, 2125.64) * mm, "end": v(1652.22, 2125.64) * mm});
            skArc(sketch, "E3217", {"start": v(1652.22, 2125.64) * mm, "mid": v(1648.84, 2128.65) * mm, "end": v(1645.7, 2125.39) * mm});
            skLineSegment(sketch, "E3218", {"start": v(1645.7, 2125.39) * mm, "end": v(1645.7, 2107.39) * mm});
            skArc(sketch, "E3219", {"start": v(1645.7, 2107.39) * mm, "mid": v(1648.84, 2104.12) * mm, "end": v(1652.22, 2107.14) * mm});
            skLineSegment(sketch, "E3220", {"start": v(1652.22, 2107.14) * mm, "end": v(1719.69, 2107.14) * mm});
            skArc(sketch, "E3221", {"start": v(1719.69, 2107.14) * mm, "mid": v(1723.07, 2104.13) * mm, "end": v(1726.2, 2107.39) * mm});
            skLineSegment(sketch, "E3222", {"start": v(1726.2, 2107.39) * mm, "end": v(1726.2, 2125.39) * mm});
            skLineSegment(sketch, "E3223", {"start": v(1902.95, 426.99) * mm, "end": v(1902.95, 535.45) * mm});
            skArc(sketch, "E3224", {"start": v(1902.95, 535.45) * mm, "mid": v(1905.96, 538.46) * mm, "end": v(1902.95, 541.47) * mm});
            skLineSegment(sketch, "E3225", {"start": v(1902.95, 541.47) * mm, "end": v(1884.45, 541.47) * mm});
            skArc(sketch, "E3226", {"start": v(1884.45, 541.47) * mm, "mid": v(1881.44, 538.46) * mm, "end": v(1884.45, 535.45) * mm});
            skLineSegment(sketch, "E3227", {"start": v(1884.45, 535.45) * mm, "end": v(1884.45, 426.99) * mm});
            skArc(sketch, "E3228", {"start": v(1884.45, 426.99) * mm, "mid": v(1881.44, 423.98) * mm, "end": v(1884.45, 420.97) * mm});
            skLineSegment(sketch, "E3229", {"start": v(1884.45, 420.97) * mm, "end": v(1902.95, 420.97) * mm});
            skArc(sketch, "E3230", {"start": v(1902.95, 420.97) * mm, "mid": v(1905.96, 423.98) * mm, "end": v(1902.95, 426.99) * mm});
            skLineSegment(sketch, "E3231", {"start": v(2016.54, 535.45) * mm, "end": v(2016.54, 426.99) * mm});
            skArc(sketch, "E3232", {"start": v(2016.54, 426.99) * mm, "mid": v(2013.53, 423.98) * mm, "end": v(2016.54, 420.97) * mm});
            skLineSegment(sketch, "E3233", {"start": v(2016.54, 420.97) * mm, "end": v(2035.04, 420.97) * mm});
            skArc(sketch, "E3234", {"start": v(2035.04, 420.97) * mm, "mid": v(2038.05, 423.98) * mm, "end": v(2035.04, 426.99) * mm});
            skLineSegment(sketch, "E3235", {"start": v(2035.04, 426.99) * mm, "end": v(2035.04, 535.45) * mm});
            skArc(sketch, "E3236", {"start": v(2035.04, 535.45) * mm, "mid": v(2038.05, 538.46) * mm, "end": v(2035.04, 541.47) * mm});
            skLineSegment(sketch, "E3237", {"start": v(2035.04, 541.47) * mm, "end": v(2016.54, 541.47) * mm});
            skArc(sketch, "E3238", {"start": v(2016.54, 541.47) * mm, "mid": v(2013.53, 538.46) * mm, "end": v(2016.54, 535.45) * mm});
            skLineSegment(sketch, "E3239", {"start": v(2035.04, 726.99) * mm, "end": v(2035.04, 835.45) * mm});
            skArc(sketch, "E3240", {"start": v(2035.04, 835.45) * mm, "mid": v(2038.05, 838.46) * mm, "end": v(2035.04, 841.47) * mm});
            skLineSegment(sketch, "E3241", {"start": v(2035.04, 841.47) * mm, "end": v(2016.54, 841.47) * mm});
            skArc(sketch, "E3242", {"start": v(2016.54, 841.47) * mm, "mid": v(2013.53, 838.46) * mm, "end": v(2016.54, 835.45) * mm});
            skLineSegment(sketch, "E3243", {"start": v(2016.54, 835.45) * mm, "end": v(2016.54, 726.99) * mm});
            skArc(sketch, "E3244", {"start": v(2016.54, 726.99) * mm, "mid": v(2013.53, 723.98) * mm, "end": v(2016.54, 720.97) * mm});
            skLineSegment(sketch, "E3245", {"start": v(2016.54, 720.97) * mm, "end": v(2035.04, 720.97) * mm});
            skArc(sketch, "E3246", {"start": v(2035.04, 720.97) * mm, "mid": v(2038.05, 723.98) * mm, "end": v(2035.04, 726.99) * mm});
            skLineSegment(sketch, "E3247", {"start": v(2035.04, 1441.47) * mm, "end": v(2016.54, 1441.47) * mm});
            skArc(sketch, "E3248", {"start": v(2016.54, 1441.47) * mm, "mid": v(2013.53, 1438.46) * mm, "end": v(2016.54, 1435.45) * mm});
            skLineSegment(sketch, "E3249", {"start": v(2016.54, 1435.45) * mm, "end": v(2016.54, 1326.99) * mm});
            skArc(sketch, "E3250", {"start": v(2016.54, 1326.99) * mm, "mid": v(2013.53, 1323.98) * mm, "end": v(2016.54, 1320.97) * mm});
            skLineSegment(sketch, "E3251", {"start": v(2016.54, 1320.97) * mm, "end": v(2035.04, 1320.97) * mm});
            skArc(sketch, "E3252", {"start": v(2035.04, 1320.97) * mm, "mid": v(2038.05, 1323.98) * mm, "end": v(2035.04, 1326.99) * mm});
            skLineSegment(sketch, "E3253", {"start": v(2035.04, 1326.99) * mm, "end": v(2035.04, 1435.45) * mm});
            skArc(sketch, "E3254", {"start": v(2035.04, 1435.45) * mm, "mid": v(2038.05, 1438.46) * mm, "end": v(2035.04, 1441.47) * mm});
            skLineSegment(sketch, "E3255", {"start": v(2035.04, 1626.99) * mm, "end": v(2035.04, 1735.45) * mm});
            skArc(sketch, "E3256", {"start": v(2035.04, 1735.45) * mm, "mid": v(2038.05, 1738.46) * mm, "end": v(2035.04, 1741.47) * mm});
            skLineSegment(sketch, "E3257", {"start": v(2035.04, 1741.47) * mm, "end": v(2016.54, 1741.47) * mm});
            skArc(sketch, "E3258", {"start": v(2016.54, 1741.47) * mm, "mid": v(2013.53, 1738.46) * mm, "end": v(2016.54, 1735.45) * mm});
            skLineSegment(sketch, "E3259", {"start": v(2016.54, 1735.45) * mm, "end": v(2016.54, 1626.99) * mm});
            skArc(sketch, "E3260", {"start": v(2016.54, 1626.99) * mm, "mid": v(2013.53, 1623.98) * mm, "end": v(2016.54, 1620.97) * mm});
            skLineSegment(sketch, "E3261", {"start": v(2016.54, 1620.97) * mm, "end": v(2035.04, 1620.97) * mm});
            skArc(sketch, "E3262", {"start": v(2035.04, 1620.97) * mm, "mid": v(2038.05, 1623.98) * mm, "end": v(2035.04, 1626.99) * mm});
            skLineSegment(sketch, "E3263", {"start": v(2035.04, 1846.99) * mm, "end": v(2035.04, 1955.45) * mm});
            skArc(sketch, "E3264", {"start": v(2035.04, 1955.45) * mm, "mid": v(2038.05, 1958.46) * mm, "end": v(2035.04, 1961.47) * mm});
            skLineSegment(sketch, "E3265", {"start": v(2035.04, 1961.47) * mm, "end": v(2016.54, 1961.47) * mm});
            skArc(sketch, "E3266", {"start": v(2016.54, 1961.47) * mm, "mid": v(2013.53, 1958.46) * mm, "end": v(2016.54, 1955.45) * mm});
            skLineSegment(sketch, "E3267", {"start": v(2016.54, 1955.45) * mm, "end": v(2016.54, 1846.99) * mm});
            skArc(sketch, "E3268", {"start": v(2016.54, 1846.99) * mm, "mid": v(2013.53, 1843.98) * mm, "end": v(2016.54, 1840.97) * mm});
            skLineSegment(sketch, "E3269", {"start": v(2016.54, 1840.97) * mm, "end": v(2035.04, 1840.97) * mm});
            skArc(sketch, "E3270", {"start": v(2035.04, 1840.97) * mm, "mid": v(2038.05, 1843.98) * mm, "end": v(2035.04, 1846.99) * mm});
            skLineSegment(sketch, "E3271", {"start": v(1884.45, 1955.45) * mm, "end": v(1884.45, 1846.99) * mm});
            skArc(sketch, "E3272", {"start": v(1884.45, 1846.99) * mm, "mid": v(1881.44, 1843.98) * mm, "end": v(1884.45, 1840.97) * mm});
            skLineSegment(sketch, "E3273", {"start": v(1884.45, 1840.97) * mm, "end": v(1902.95, 1840.97) * mm});
            skArc(sketch, "E3274", {"start": v(1902.95, 1840.97) * mm, "mid": v(1905.96, 1843.98) * mm, "end": v(1902.95, 1846.99) * mm});
            skLineSegment(sketch, "E3275", {"start": v(1902.95, 1846.99) * mm, "end": v(1902.95, 1955.45) * mm});
            skArc(sketch, "E3276", {"start": v(1902.95, 1955.45) * mm, "mid": v(1905.96, 1958.46) * mm, "end": v(1902.95, 1961.47) * mm});
            skLineSegment(sketch, "E3277", {"start": v(1902.95, 1961.47) * mm, "end": v(1884.45, 1961.47) * mm});
            skArc(sketch, "E3278", {"start": v(1884.45, 1961.47) * mm, "mid": v(1881.44, 1958.46) * mm, "end": v(1884.45, 1955.45) * mm});
            skLineSegment(sketch, "E3279", {"start": v(1902.95, 1626.99) * mm, "end": v(1902.95, 1735.45) * mm});
            skArc(sketch, "E3280", {"start": v(1902.95, 1735.45) * mm, "mid": v(1905.96, 1738.46) * mm, "end": v(1902.95, 1741.47) * mm});
            skLineSegment(sketch, "E3281", {"start": v(1902.95, 1741.47) * mm, "end": v(1884.45, 1741.47) * mm});
            skArc(sketch, "E3282", {"start": v(1884.45, 1741.47) * mm, "mid": v(1881.44, 1738.46) * mm, "end": v(1884.45, 1735.45) * mm});
            skLineSegment(sketch, "E3283", {"start": v(1884.45, 1735.45) * mm, "end": v(1884.45, 1626.99) * mm});
            skArc(sketch, "E3284", {"start": v(1884.45, 1626.99) * mm, "mid": v(1881.44, 1623.98) * mm, "end": v(1884.45, 1620.97) * mm});
            skLineSegment(sketch, "E3285", {"start": v(1884.45, 1620.97) * mm, "end": v(1902.95, 1620.97) * mm});
            skArc(sketch, "E3286", {"start": v(1902.95, 1620.97) * mm, "mid": v(1905.96, 1623.98) * mm, "end": v(1902.95, 1626.99) * mm});
            skLineSegment(sketch, "E3287", {"start": v(1902.95, 1326.99) * mm, "end": v(1902.95, 1435.45) * mm});
            skArc(sketch, "E3288", {"start": v(1902.95, 1435.45) * mm, "mid": v(1905.96, 1438.46) * mm, "end": v(1902.95, 1441.47) * mm});
            skLineSegment(sketch, "E3289", {"start": v(1902.95, 1441.47) * mm, "end": v(1884.45, 1441.47) * mm});
            skArc(sketch, "E3290", {"start": v(1884.45, 1441.47) * mm, "mid": v(1881.44, 1438.46) * mm, "end": v(1884.45, 1435.45) * mm});
            skLineSegment(sketch, "E3291", {"start": v(1884.45, 1435.45) * mm, "end": v(1884.45, 1326.99) * mm});
            skArc(sketch, "E3292", {"start": v(1884.45, 1326.99) * mm, "mid": v(1881.44, 1323.98) * mm, "end": v(1884.45, 1320.97) * mm});
            skLineSegment(sketch, "E3293", {"start": v(1884.45, 1320.97) * mm, "end": v(1902.95, 1320.97) * mm});
            skArc(sketch, "E3294", {"start": v(1902.95, 1320.97) * mm, "mid": v(1905.96, 1323.98) * mm, "end": v(1902.95, 1326.99) * mm});
            skLineSegment(sketch, "E3295", {"start": v(1902.95, 1090.47) * mm, "end": v(1902.95, 1135.45) * mm});
            skArc(sketch, "E3296", {"start": v(1902.95, 1135.45) * mm, "mid": v(1905.96, 1138.46) * mm, "end": v(1902.95, 1141.47) * mm});
            skLineSegment(sketch, "E3297", {"start": v(1902.95, 1141.47) * mm, "end": v(1884.45, 1141.47) * mm});
            skArc(sketch, "E3298", {"start": v(1884.45, 1141.47) * mm, "mid": v(1881.44, 1138.46) * mm, "end": v(1884.45, 1135.45) * mm});
            skLineSegment(sketch, "E3299", {"start": v(1884.45, 1135.45) * mm, "end": v(1884.45, 1026.99) * mm});
            skArc(sketch, "E3300", {"start": v(1884.45, 1026.99) * mm, "mid": v(1881.44, 1023.98) * mm, "end": v(1884.45, 1020.97) * mm});
            skLineSegment(sketch, "E3301", {"start": v(1884.45, 1020.97) * mm, "end": v(1902.95, 1020.97) * mm});
            skArc(sketch, "E3302", {"start": v(1902.95, 1020.97) * mm, "mid": v(1905.96, 1023.98) * mm, "end": v(1902.95, 1026.99) * mm});
            skLineSegment(sketch, "E3303", {"start": v(1902.95, 1026.99) * mm, "end": v(1902.95, 1071.97) * mm});
            skLineSegment(sketch, "E3304", {"start": v(1902.95, 1071.97) * mm, "end": v(1928.02, 1071.97) * mm});
            skArc(sketch, "E3305", {"start": v(1928.02, 1071.97) * mm, "mid": v(1931.03, 1068.96) * mm, "end": v(1934.04, 1071.97) * mm});
            skLineSegment(sketch, "E3306", {"start": v(1934.04, 1071.97) * mm, "end": v(1934.04, 1090.47) * mm});
            skArc(sketch, "E3307", {"start": v(1934.04, 1090.47) * mm, "mid": v(1931.03, 1093.48) * mm, "end": v(1928.02, 1090.47) * mm});
            skLineSegment(sketch, "E3308", {"start": v(1928.02, 1090.47) * mm, "end": v(1902.95, 1090.47) * mm});
            skLineSegment(sketch, "E3309", {"start": v(1902.95, 726.99) * mm, "end": v(1902.95, 835.45) * mm});
            skArc(sketch, "E3310", {"start": v(1902.95, 835.45) * mm, "mid": v(1905.96, 838.46) * mm, "end": v(1902.95, 841.47) * mm});
            skLineSegment(sketch, "E3311", {"start": v(1902.95, 841.47) * mm, "end": v(1884.45, 841.47) * mm});
            skArc(sketch, "E3312", {"start": v(1884.45, 841.47) * mm, "mid": v(1881.44, 838.46) * mm, "end": v(1884.45, 835.45) * mm});
            skLineSegment(sketch, "E3313", {"start": v(1884.45, 835.45) * mm, "end": v(1884.45, 726.99) * mm});
            skArc(sketch, "E3314", {"start": v(1884.45, 726.99) * mm, "mid": v(1881.44, 723.98) * mm, "end": v(1884.45, 720.97) * mm});
            skLineSegment(sketch, "E3315", {"start": v(1884.45, 720.97) * mm, "end": v(1902.95, 720.97) * mm});
            skArc(sketch, "E3316", {"start": v(1902.95, 720.97) * mm, "mid": v(1905.96, 723.98) * mm, "end": v(1902.95, 726.99) * mm});
            skLineSegment(sketch, "E3317", {"start": v(2035.04, 1026.99) * mm, "end": v(2035.04, 1135.45) * mm});
            skArc(sketch, "E3318", {"start": v(2035.04, 1135.45) * mm, "mid": v(2038.05, 1138.46) * mm, "end": v(2035.04, 1141.47) * mm});
            skLineSegment(sketch, "E3319", {"start": v(2035.04, 1141.47) * mm, "end": v(2016.54, 1141.47) * mm});
            skArc(sketch, "E3320", {"start": v(2016.54, 1141.47) * mm, "mid": v(2013.53, 1138.46) * mm, "end": v(2016.54, 1135.45) * mm});
            skLineSegment(sketch, "E3321", {"start": v(2016.54, 1135.45) * mm, "end": v(2016.54, 1090.47) * mm});
            skLineSegment(sketch, "E3322", {"start": v(2016.54, 1090.47) * mm, "end": v(1991.56, 1090.47) * mm});
            skArc(sketch, "E3323", {"start": v(1991.56, 1090.47) * mm, "mid": v(1988.55, 1093.48) * mm, "end": v(1985.54, 1090.47) * mm});
            skLineSegment(sketch, "E3324", {"start": v(1985.54, 1090.47) * mm, "end": v(1985.54, 1071.97) * mm});
            skArc(sketch, "E3325", {"start": v(1985.54, 1071.97) * mm, "mid": v(1988.55, 1068.96) * mm, "end": v(1991.56, 1071.97) * mm});
            skLineSegment(sketch, "E3326", {"start": v(1991.56, 1071.97) * mm, "end": v(2016.54, 1071.97) * mm});
            skLineSegment(sketch, "E3327", {"start": v(2016.54, 1071.97) * mm, "end": v(2016.54, 1026.99) * mm});
            skArc(sketch, "E3328", {"start": v(2016.54, 1026.99) * mm, "mid": v(2013.53, 1023.98) * mm, "end": v(2016.54, 1020.97) * mm});
            skLineSegment(sketch, "E3329", {"start": v(2016.54, 1020.97) * mm, "end": v(2035.04, 1020.97) * mm});
            skArc(sketch, "E3330", {"start": v(2035.04, 1020.97) * mm, "mid": v(2038.05, 1023.98) * mm, "end": v(2035.04, 1026.99) * mm});
            skLineSegment(sketch, "E3331", {"start": v(2220.72, 931.66) * mm, "end": v(2269.18, 931.66) * mm});
            skArc(sketch, "E3332", {"start": v(2269.18, 931.66) * mm, "mid": v(2272.2, 928.65) * mm, "end": v(2275.2, 931.66) * mm});
            skLineSegment(sketch, "E3333", {"start": v(2275.2, 931.66) * mm, "end": v(2275.2, 950.16) * mm});
            skArc(sketch, "E3334", {"start": v(2275.2, 950.16) * mm, "mid": v(2272.2, 953.17) * mm, "end": v(2269.18, 950.16) * mm});
            skLineSegment(sketch, "E3335", {"start": v(2269.18, 950.16) * mm, "end": v(2220.72, 950.16) * mm});
            skArc(sketch, "E3336", {"start": v(2220.72, 950.16) * mm, "mid": v(2217.71, 953.17) * mm, "end": v(2214.7, 950.16) * mm});
            skLineSegment(sketch, "E3337", {"start": v(2214.7, 950.16) * mm, "end": v(2214.7, 931.66) * mm});
            skArc(sketch, "E3338", {"start": v(2214.7, 931.66) * mm, "mid": v(2217.71, 928.65) * mm, "end": v(2220.72, 931.66) * mm});
            skLineSegment(sketch, "E3339", {"start": v(2220.72, 1231.66) * mm, "end": v(2269.18, 1231.66) * mm});
            skArc(sketch, "E3340", {"start": v(2269.18, 1231.66) * mm, "mid": v(2272.2, 1228.65) * mm, "end": v(2275.2, 1231.66) * mm});
            skLineSegment(sketch, "E3341", {"start": v(2275.2, 1231.66) * mm, "end": v(2275.2, 1250.16) * mm});
            skArc(sketch, "E3342", {"start": v(2275.2, 1250.16) * mm, "mid": v(2272.2, 1253.17) * mm, "end": v(2269.18, 1250.16) * mm});
            skLineSegment(sketch, "E3343", {"start": v(2269.18, 1250.16) * mm, "end": v(2220.72, 1250.16) * mm});
            skArc(sketch, "E3344", {"start": v(2220.72, 1250.16) * mm, "mid": v(2217.71, 1253.17) * mm, "end": v(2214.7, 1250.16) * mm});
            skLineSegment(sketch, "E3345", {"start": v(2214.7, 1250.16) * mm, "end": v(2214.7, 1231.66) * mm});
            skArc(sketch, "E3346", {"start": v(2214.7, 1231.66) * mm, "mid": v(2217.71, 1228.65) * mm, "end": v(2220.72, 1231.66) * mm});
            skLineSegment(sketch, "E3347", {"start": v(2220.72, 445.02) * mm, "end": v(2269.18, 445.02) * mm});
            skArc(sketch, "E3348", {"start": v(2269.18, 445.02) * mm, "mid": v(2272.2, 442.01) * mm, "end": v(2275.2, 445.02) * mm});
            skLineSegment(sketch, "E3349", {"start": v(2275.2, 445.02) * mm, "end": v(2275.2, 463.52) * mm});
            skArc(sketch, "E3350", {"start": v(2275.2, 463.52) * mm, "mid": v(2272.2, 466.53) * mm, "end": v(2269.18, 463.52) * mm});
            skLineSegment(sketch, "E3351", {"start": v(2269.18, 463.52) * mm, "end": v(2220.72, 463.52) * mm});
            skArc(sketch, "E3352", {"start": v(2220.72, 463.52) * mm, "mid": v(2217.71, 466.53) * mm, "end": v(2214.7, 463.52) * mm});
            skLineSegment(sketch, "E3353", {"start": v(2214.7, 463.52) * mm, "end": v(2214.7, 445.02) * mm});
            skArc(sketch, "E3354", {"start": v(2214.7, 445.02) * mm, "mid": v(2217.71, 442.01) * mm, "end": v(2220.72, 445.02) * mm});
            skLineSegment(sketch, "E3355", {"start": v(2224.95, 1531.91) * mm, "end": v(2224.95, 1549.91) * mm});
            skLineSegment(sketch, "E3356", {"start": v(2224.95, 1549.91) * mm, "end": v(2264.95, 1549.91) * mm});
            skLineSegment(sketch, "E3357", {"start": v(2264.95, 1549.91) * mm, "end": v(2264.95, 1531.91) * mm});
            skLineSegment(sketch, "E3358", {"start": v(2264.95, 1531.91) * mm, "end": v(2224.95, 1531.91) * mm});
            skLineSegment(sketch, "E3359", {"start": v(2351.95, 1520.91) * mm, "end": v(2351.95, 1560.91) * mm});
            skLineSegment(sketch, "E3360", {"start": v(2351.95, 1560.91) * mm, "end": v(2369.95, 1560.91) * mm});
            skLineSegment(sketch, "E3361", {"start": v(2369.95, 1560.91) * mm, "end": v(2369.95, 1520.91) * mm});
            skLineSegment(sketch, "E3362", {"start": v(2369.95, 1520.91) * mm, "end": v(2351.95, 1520.91) * mm});
            skLineSegment(sketch, "E3363", {"start": v(2137.95, 1520.91) * mm, "end": v(2119.95, 1520.91) * mm});
            skLineSegment(sketch, "E3364", {"start": v(2119.95, 1520.91) * mm, "end": v(2119.95, 1560.91) * mm});
            skLineSegment(sketch, "E3365", {"start": v(2119.95, 1560.91) * mm, "end": v(2137.95, 1560.91) * mm});
            skLineSegment(sketch, "E3366", {"start": v(2137.95, 1560.91) * mm, "end": v(2137.95, 1520.91) * mm});
            skLineSegment(sketch, "E3367", {"start": v(2351.95, 1220.91) * mm, "end": v(2351.95, 1260.91) * mm});
            skLineSegment(sketch, "E3368", {"start": v(2351.95, 1260.91) * mm, "end": v(2369.95, 1260.91) * mm});
            skLineSegment(sketch, "E3369", {"start": v(2369.95, 1260.91) * mm, "end": v(2369.95, 1220.91) * mm});
            skLineSegment(sketch, "E3370", {"start": v(2369.95, 1220.91) * mm, "end": v(2351.95, 1220.91) * mm});
            skLineSegment(sketch, "E3371", {"start": v(2137.95, 1220.91) * mm, "end": v(2119.95, 1220.91) * mm});
            skLineSegment(sketch, "E3372", {"start": v(2119.95, 1220.91) * mm, "end": v(2119.95, 1260.91) * mm});
            skLineSegment(sketch, "E3373", {"start": v(2119.95, 1260.91) * mm, "end": v(2137.95, 1260.91) * mm});
            skLineSegment(sketch, "E3374", {"start": v(2137.95, 1260.91) * mm, "end": v(2137.95, 1220.91) * mm});
            skLineSegment(sketch, "E3375", {"start": v(2351.95, 474.27) * mm, "end": v(2369.95, 474.27) * mm});
            skLineSegment(sketch, "E3376", {"start": v(2369.95, 474.27) * mm, "end": v(2369.95, 434.27) * mm});
            skLineSegment(sketch, "E3377", {"start": v(2369.95, 434.27) * mm, "end": v(2351.95, 434.27) * mm});
            skLineSegment(sketch, "E3378", {"start": v(2351.95, 434.27) * mm, "end": v(2351.95, 474.27) * mm});
            skLineSegment(sketch, "E3379", {"start": v(2137.95, 474.27) * mm, "end": v(2137.95, 434.27) * mm});
            skLineSegment(sketch, "E3380", {"start": v(2137.95, 434.27) * mm, "end": v(2119.95, 434.27) * mm});
            skLineSegment(sketch, "E3381", {"start": v(2119.95, 434.27) * mm, "end": v(2119.95, 474.27) * mm});
            skLineSegment(sketch, "E3382", {"start": v(2119.95, 474.27) * mm, "end": v(2137.95, 474.27) * mm});
            skLineSegment(sketch, "E3383", {"start": v(2351.95, 920.91) * mm, "end": v(2351.95, 960.91) * mm});
            skLineSegment(sketch, "E3384", {"start": v(2351.95, 960.91) * mm, "end": v(2369.95, 960.91) * mm});
            skLineSegment(sketch, "E3385", {"start": v(2369.95, 960.91) * mm, "end": v(2369.95, 920.91) * mm});
            skLineSegment(sketch, "E3386", {"start": v(2369.95, 920.91) * mm, "end": v(2351.95, 920.91) * mm});
            skLineSegment(sketch, "E3387", {"start": v(2137.95, 920.91) * mm, "end": v(2119.95, 920.91) * mm});
            skLineSegment(sketch, "E3388", {"start": v(2119.95, 920.91) * mm, "end": v(2119.95, 960.91) * mm});
            skLineSegment(sketch, "E3389", {"start": v(2119.95, 960.91) * mm, "end": v(2137.95, 960.91) * mm});
            skLineSegment(sketch, "E3390", {"start": v(2137.95, 960.91) * mm, "end": v(2137.95, 920.91) * mm});
            skLineSegment(sketch, "E3391", {"start": v(2137.95, 717.6) * mm, "end": v(2137.95, 677.6) * mm});
            skLineSegment(sketch, "E3392", {"start": v(2137.95, 677.6) * mm, "end": v(2119.95, 677.6) * mm});
            skLineSegment(sketch, "E3393", {"start": v(2119.95, 677.6) * mm, "end": v(2119.95, 717.6) * mm});
            skLineSegment(sketch, "E3394", {"start": v(2119.95, 717.6) * mm, "end": v(2137.95, 717.6) * mm});
            skLineSegment(sketch, "E3395", {"start": v(2559.17, 568.2) * mm, "end": v(2519.18, 568.2) * mm});
            skLineSegment(sketch, "E3396", {"start": v(2519.18, 568.2) * mm, "end": v(2519.18, 593.07) * mm});
            skLineSegment(sketch, "E3397", {"start": v(2538.29, 568.2) * mm, "end": v(2538.29, 591.28) * mm});
            skLineSegment(sketch, "E3398", {"start": v(2559.16, 654.5) * mm, "end": v(2519.18, 676.97) * mm});
            skLineSegment(sketch, "E3399", {"start": v(2559.17, 685.77) * mm, "end": v(2519.18, 685.77) * mm});
            skLineSegment(sketch, "E3400", {"start": v(2519.18, 685.77) * mm, "end": v(2519.18, 710.63) * mm});
            skLineSegment(sketch, "E3401", {"start": v(2538.29, 685.77) * mm, "end": v(2538.29, 708.84) * mm});
            skLineSegment(sketch, "E3402", {"start": v(2195.16, 2261.05) * mm, "end": v(2195.16, 2221.06) * mm});
            skLineSegment(sketch, "E3403", {"start": v(2195.16, 2221.06) * mm, "end": v(2170.3, 2221.06) * mm});
            skLineSegment(sketch, "E3404", {"start": v(2195.16, 2240.17) * mm, "end": v(2172.1, 2240.17) * mm});
            skLineSegment(sketch, "E3405", {"start": v(2108.86, 2261.04) * mm, "end": v(2086.4, 2221.06) * mm});
            skLineSegment(sketch, "E3406", {"start": v(2077.6, 2261.04) * mm, "end": v(2077.6, 2221.06) * mm});
            skLineSegment(sketch, "E3407", {"start": v(2077.6, 2221.06) * mm, "end": v(2062.94, 2221.06) * mm});
            skLineSegment(sketch, "E3408", {"start": v(2062.94, 2221.06) * mm, "end": v(2062.6, 2221.08) * mm});
            skLineSegment(sketch, "E3409", {"start": v(2062.6, 2221.08) * mm, "end": v(2062.25, 2221.1) * mm});
            skLineSegment(sketch, "E3410", {"start": v(2062.25, 2221.1) * mm, "end": v(2061.9, 2221.14) * mm});
            skLineSegment(sketch, "E3411", {"start": v(2061.9, 2221.14) * mm, "end": v(2061.56, 2221.18) * mm});
            skLineSegment(sketch, "E3412", {"start": v(2061.56, 2221.18) * mm, "end": v(2061.22, 2221.23) * mm});
            skLineSegment(sketch, "E3413", {"start": v(2061.22, 2221.23) * mm, "end": v(2060.88, 2221.3) * mm});
            skLineSegment(sketch, "E3414", {"start": v(2060.88, 2221.3) * mm, "end": v(2060.54, 2221.36) * mm});
            skLineSegment(sketch, "E3415", {"start": v(2060.54, 2221.36) * mm, "end": v(2060.2, 2221.44) * mm});
            skLineSegment(sketch, "E3416", {"start": v(2060.2, 2221.44) * mm, "end": v(2059.87, 2221.52) * mm});
            skLineSegment(sketch, "E3417", {"start": v(2059.87, 2221.52) * mm, "end": v(2059.54, 2221.61) * mm});
            skLineSegment(sketch, "E3418", {"start": v(2059.54, 2221.61) * mm, "end": v(2059.21, 2221.72) * mm});
            skLineSegment(sketch, "E3419", {"start": v(2059.21, 2221.72) * mm, "end": v(2058.89, 2221.83) * mm});
            skLineSegment(sketch, "E3420", {"start": v(2058.89, 2221.83) * mm, "end": v(2058.57, 2221.94) * mm});
            skLineSegment(sketch, "E3421", {"start": v(2058.57, 2221.94) * mm, "end": v(2058.25, 2222.07) * mm});
            skLineSegment(sketch, "E3422", {"start": v(2058.25, 2222.07) * mm, "end": v(2057.93, 2222.2) * mm});
            skLineSegment(sketch, "E3423", {"start": v(2057.93, 2222.2) * mm, "end": v(2057.62, 2222.34) * mm});
            skLineSegment(sketch, "E3424", {"start": v(2057.62, 2222.34) * mm, "end": v(2057.31, 2222.5) * mm});
            skLineSegment(sketch, "E3425", {"start": v(2057.31, 2222.5) * mm, "end": v(2057, 2222.65) * mm});
            skLineSegment(sketch, "E3426", {"start": v(2057, 2222.65) * mm, "end": v(2056.7, 2222.81) * mm});
            skLineSegment(sketch, "E3427", {"start": v(2056.7, 2222.81) * mm, "end": v(2056.41, 2222.99) * mm});
            skLineSegment(sketch, "E3428", {"start": v(2056.41, 2222.99) * mm, "end": v(2056.12, 2223.17) * mm});
            skLineSegment(sketch, "E3429", {"start": v(2056.12, 2223.17) * mm, "end": v(2055.83, 2223.35) * mm});
            skLineSegment(sketch, "E3430", {"start": v(2055.83, 2223.35) * mm, "end": v(2055.55, 2223.55) * mm});
            skLineSegment(sketch, "E3431", {"start": v(2055.55, 2223.55) * mm, "end": v(2055.27, 2223.75) * mm});
            skLineSegment(sketch, "E3432", {"start": v(2055.27, 2223.75) * mm, "end": v(2055, 2223.96) * mm});
            skLineSegment(sketch, "E3433", {"start": v(2055, 2223.96) * mm, "end": v(2054.73, 2224.17) * mm});
            skLineSegment(sketch, "E3434", {"start": v(2054.73, 2224.17) * mm, "end": v(2054.46, 2224.4) * mm});
            skLineSegment(sketch, "E3435", {"start": v(2054.46, 2224.4) * mm, "end": v(2054.2, 2224.62) * mm});
            skLineSegment(sketch, "E3436", {"start": v(2054.2, 2224.62) * mm, "end": v(2053.95, 2224.86) * mm});
            skLineSegment(sketch, "E3437", {"start": v(2053.95, 2224.86) * mm, "end": v(2053.7, 2225.1) * mm});
            skLineSegment(sketch, "E3438", {"start": v(2053.7, 2225.1) * mm, "end": v(2053.46, 2225.35) * mm});
            skLineSegment(sketch, "E3439", {"start": v(2053.46, 2225.35) * mm, "end": v(2053.23, 2225.6) * mm});
            skLineSegment(sketch, "E3440", {"start": v(2053.23, 2225.6) * mm, "end": v(2052.83, 2226.02) * mm});
            skLineSegment(sketch, "E3441", {"start": v(2052.83, 2226.02) * mm, "end": v(2052.44, 2226.44) * mm});
            skLineSegment(sketch, "E3442", {"start": v(2052.44, 2226.44) * mm, "end": v(2052.06, 2226.87) * mm});
            skLineSegment(sketch, "E3443", {"start": v(2052.06, 2226.87) * mm, "end": v(2051.7, 2227.31) * mm});
            skLineSegment(sketch, "E3444", {"start": v(2051.7, 2227.31) * mm, "end": v(2051.34, 2227.76) * mm});
            skLineSegment(sketch, "E3445", {"start": v(2051.34, 2227.76) * mm, "end": v(2051, 2228.21) * mm});
            skLineSegment(sketch, "E3446", {"start": v(2051, 2228.21) * mm, "end": v(2050.67, 2228.68) * mm});
            skLineSegment(sketch, "E3447", {"start": v(2050.67, 2228.68) * mm, "end": v(2050.35, 2229.15) * mm});
            skLineSegment(sketch, "E3448", {"start": v(2050.35, 2229.15) * mm, "end": v(2050.04, 2229.63) * mm});
            skLineSegment(sketch, "E3449", {"start": v(2050.04, 2229.63) * mm, "end": v(2049.75, 2230.11) * mm});
            skLineSegment(sketch, "E3450", {"start": v(2049.75, 2230.11) * mm, "end": v(2049.47, 2230.6) * mm});
            skLineSegment(sketch, "E3451", {"start": v(2049.47, 2230.6) * mm, "end": v(2049.2, 2231.1) * mm});
            skLineSegment(sketch, "E3452", {"start": v(2049.2, 2231.1) * mm, "end": v(2048.94, 2231.61) * mm});
            skLineSegment(sketch, "E3453", {"start": v(2048.94, 2231.61) * mm, "end": v(2048.7, 2232.12) * mm});
            skLineSegment(sketch, "E3454", {"start": v(2048.7, 2232.12) * mm, "end": v(2048.47, 2232.64) * mm});
            skLineSegment(sketch, "E3455", {"start": v(2048.47, 2232.64) * mm, "end": v(2048.25, 2233.16) * mm});
            skLineSegment(sketch, "E3456", {"start": v(2048.25, 2233.16) * mm, "end": v(2048.05, 2233.7) * mm});
            skLineSegment(sketch, "E3457", {"start": v(2048.05, 2233.7) * mm, "end": v(2047.85, 2234.22) * mm});
            skLineSegment(sketch, "E3458", {"start": v(2047.85, 2234.22) * mm, "end": v(2047.68, 2234.76) * mm});
            skLineSegment(sketch, "E3459", {"start": v(2047.68, 2234.76) * mm, "end": v(2047.51, 2235.3) * mm});
            skLineSegment(sketch, "E3460", {"start": v(2047.51, 2235.3) * mm, "end": v(2047.36, 2235.85) * mm});
            skLineSegment(sketch, "E3461", {"start": v(2047.36, 2235.85) * mm, "end": v(2047.22, 2236.4) * mm});
            skLineSegment(sketch, "E3462", {"start": v(2047.22, 2236.4) * mm, "end": v(2047.1, 2236.96) * mm});
            skLineSegment(sketch, "E3463", {"start": v(2047.1, 2236.96) * mm, "end": v(2046.99, 2237.51) * mm});
            skLineSegment(sketch, "E3464", {"start": v(2046.99, 2237.51) * mm, "end": v(2046.9, 2238.07) * mm});
            skLineSegment(sketch, "E3465", {"start": v(2046.9, 2238.07) * mm, "end": v(2046.8, 2238.64) * mm});
            skLineSegment(sketch, "E3466", {"start": v(2046.8, 2238.64) * mm, "end": v(2046.74, 2239.2) * mm});
            skLineSegment(sketch, "E3467", {"start": v(2046.74, 2239.2) * mm, "end": v(2046.69, 2239.77) * mm});
            skLineSegment(sketch, "E3468", {"start": v(2046.69, 2239.77) * mm, "end": v(2046.65, 2240.34) * mm});
            skLineSegment(sketch, "E3469", {"start": v(2046.65, 2240.34) * mm, "end": v(2046.62, 2240.91) * mm});
            skLineSegment(sketch, "E3470", {"start": v(2046.62, 2240.91) * mm, "end": v(2046.6, 2241.49) * mm});
            skLineSegment(sketch, "E3471", {"start": v(2046.6, 2241.49) * mm, "end": v(2046.61, 2242.06) * mm});
            skLineSegment(sketch, "E3472", {"start": v(2046.61, 2242.06) * mm, "end": v(2046.6, 2242.55) * mm});
            skLineSegment(sketch, "E3473", {"start": v(2046.6, 2242.55) * mm, "end": v(2046.6, 2243.03) * mm});
            skLineSegment(sketch, "E3474", {"start": v(2046.6, 2243.03) * mm, "end": v(2046.61, 2243.5) * mm});
            skLineSegment(sketch, "E3475", {"start": v(2046.61, 2243.5) * mm, "end": v(2046.64, 2243.99) * mm});
            skLineSegment(sketch, "E3476", {"start": v(2046.64, 2243.99) * mm, "end": v(2046.67, 2244.46) * mm});
            skLineSegment(sketch, "E3477", {"start": v(2046.67, 2244.46) * mm, "end": v(2046.72, 2244.94) * mm});
            skLineSegment(sketch, "E3478", {"start": v(2046.72, 2244.94) * mm, "end": v(2046.78, 2245.41) * mm});
            skLineSegment(sketch, "E3479", {"start": v(2046.78, 2245.41) * mm, "end": v(2046.85, 2245.88) * mm});
            skLineSegment(sketch, "E3480", {"start": v(2046.85, 2245.88) * mm, "end": v(2046.94, 2246.35) * mm});
            skLineSegment(sketch, "E3481", {"start": v(2046.94, 2246.35) * mm, "end": v(2047.03, 2246.82) * mm});
            skLineSegment(sketch, "E3482", {"start": v(2047.03, 2246.82) * mm, "end": v(2047.14, 2247.28) * mm});
            skLineSegment(sketch, "E3483", {"start": v(2047.14, 2247.28) * mm, "end": v(2047.25, 2247.75) * mm});
            skLineSegment(sketch, "E3484", {"start": v(2047.25, 2247.75) * mm, "end": v(2047.38, 2248.2) * mm});
            skLineSegment(sketch, "E3485", {"start": v(2047.38, 2248.2) * mm, "end": v(2047.52, 2248.66) * mm});
            skLineSegment(sketch, "E3486", {"start": v(2047.52, 2248.66) * mm, "end": v(2047.67, 2249.1) * mm});
            skLineSegment(sketch, "E3487", {"start": v(2047.67, 2249.1) * mm, "end": v(2047.83, 2249.56) * mm});
            skLineSegment(sketch, "E3488", {"start": v(2047.83, 2249.56) * mm, "end": v(2048, 2250) * mm});
            skLineSegment(sketch, "E3489", {"start": v(2048, 2250) * mm, "end": v(2048.18, 2250.44) * mm});
            skLineSegment(sketch, "E3490", {"start": v(2048.18, 2250.44) * mm, "end": v(2048.38, 2250.87) * mm});
            skLineSegment(sketch, "E3491", {"start": v(2048.38, 2250.87) * mm, "end": v(2048.58, 2251.3) * mm});
            skLineSegment(sketch, "E3492", {"start": v(2048.58, 2251.3) * mm, "end": v(2048.8, 2251.73) * mm});
            skLineSegment(sketch, "E3493", {"start": v(2048.8, 2251.73) * mm, "end": v(2049.02, 2252.15) * mm});
            skLineSegment(sketch, "E3494", {"start": v(2049.02, 2252.15) * mm, "end": v(2049.25, 2252.56) * mm});
            skLineSegment(sketch, "E3495", {"start": v(2049.25, 2252.56) * mm, "end": v(2049.5, 2252.97) * mm});
            skLineSegment(sketch, "E3496", {"start": v(2049.5, 2252.97) * mm, "end": v(2049.76, 2253.37) * mm});
            skLineSegment(sketch, "E3497", {"start": v(2049.76, 2253.37) * mm, "end": v(2050.02, 2253.77) * mm});
            skLineSegment(sketch, "E3498", {"start": v(2050.02, 2253.77) * mm, "end": v(2050.3, 2254.16) * mm});
            skLineSegment(sketch, "E3499", {"start": v(2050.3, 2254.16) * mm, "end": v(2050.58, 2254.54) * mm});
            skLineSegment(sketch, "E3500", {"start": v(2050.58, 2254.54) * mm, "end": v(2050.88, 2254.92) * mm});
            skLineSegment(sketch, "E3501", {"start": v(2050.88, 2254.92) * mm, "end": v(2051.18, 2255.3) * mm});
            skLineSegment(sketch, "E3502", {"start": v(2051.18, 2255.3) * mm, "end": v(2051.5, 2255.65) * mm});
            skLineSegment(sketch, "E3503", {"start": v(2051.5, 2255.65) * mm, "end": v(2051.82, 2256) * mm});
            skLineSegment(sketch, "E3504", {"start": v(2051.82, 2256) * mm, "end": v(2052.1, 2256.3) * mm});
            skLineSegment(sketch, "E3505", {"start": v(2052.1, 2256.3) * mm, "end": v(2052.38, 2256.57) * mm});
            skLineSegment(sketch, "E3506", {"start": v(2052.38, 2256.57) * mm, "end": v(2052.66, 2256.84) * mm});
            skLineSegment(sketch, "E3507", {"start": v(2052.66, 2256.84) * mm, "end": v(2052.96, 2257.1) * mm});
            skLineSegment(sketch, "E3508", {"start": v(2052.96, 2257.1) * mm, "end": v(2053.26, 2257.36) * mm});
            skLineSegment(sketch, "E3509", {"start": v(2053.26, 2257.36) * mm, "end": v(2053.56, 2257.6) * mm});
            skLineSegment(sketch, "E3510", {"start": v(2053.56, 2257.6) * mm, "end": v(2053.87, 2257.84) * mm});
            skLineSegment(sketch, "E3511", {"start": v(2053.87, 2257.84) * mm, "end": v(2054.19, 2258.07) * mm});
            skLineSegment(sketch, "E3512", {"start": v(2054.19, 2258.07) * mm, "end": v(2054.5, 2258.3) * mm});
            skLineSegment(sketch, "E3513", {"start": v(2054.5, 2258.3) * mm, "end": v(2054.83, 2258.5) * mm});
            skLineSegment(sketch, "E3514", {"start": v(2054.83, 2258.5) * mm, "end": v(2055.16, 2258.72) * mm});
            skLineSegment(sketch, "E3515", {"start": v(2055.16, 2258.72) * mm, "end": v(2055.5, 2258.91) * mm});
            skLineSegment(sketch, "E3516", {"start": v(2055.5, 2258.91) * mm, "end": v(2055.84, 2259.1) * mm});
            skLineSegment(sketch, "E3517", {"start": v(2055.84, 2259.1) * mm, "end": v(2056.18, 2259.29) * mm});
            skLineSegment(sketch, "E3518", {"start": v(2056.18, 2259.29) * mm, "end": v(2056.53, 2259.46) * mm});
            skLineSegment(sketch, "E3519", {"start": v(2056.53, 2259.46) * mm, "end": v(2056.88, 2259.62) * mm});
            skLineSegment(sketch, "E3520", {"start": v(2056.88, 2259.62) * mm, "end": v(2057.24, 2259.78) * mm});
            skLineSegment(sketch, "E3521", {"start": v(2057.24, 2259.78) * mm, "end": v(2057.6, 2259.93) * mm});
            skLineSegment(sketch, "E3522", {"start": v(2057.6, 2259.93) * mm, "end": v(2057.96, 2260.07) * mm});
            skLineSegment(sketch, "E3523", {"start": v(2057.96, 2260.07) * mm, "end": v(2058.33, 2260.2) * mm});
            skLineSegment(sketch, "E3524", {"start": v(2058.33, 2260.2) * mm, "end": v(2058.7, 2260.32) * mm});
            skLineSegment(sketch, "E3525", {"start": v(2058.7, 2260.32) * mm, "end": v(2059.08, 2260.43) * mm});
            skLineSegment(sketch, "E3526", {"start": v(2059.08, 2260.43) * mm, "end": v(2059.45, 2260.53) * mm});
            skLineSegment(sketch, "E3527", {"start": v(2059.45, 2260.53) * mm, "end": v(2059.83, 2260.62) * mm});
            skLineSegment(sketch, "E3528", {"start": v(2059.83, 2260.62) * mm, "end": v(2060.21, 2260.7) * mm});
            skLineSegment(sketch, "E3529", {"start": v(2060.21, 2260.7) * mm, "end": v(2060.6, 2260.78) * mm});
            skLineSegment(sketch, "E3530", {"start": v(2060.6, 2260.78) * mm, "end": v(2060.98, 2260.85) * mm});
            skLineSegment(sketch, "E3531", {"start": v(2060.98, 2260.85) * mm, "end": v(2061.37, 2260.9) * mm});
            skLineSegment(sketch, "E3532", {"start": v(2061.37, 2260.9) * mm, "end": v(2061.76, 2260.95) * mm});
            skLineSegment(sketch, "E3533", {"start": v(2061.76, 2260.95) * mm, "end": v(2062.15, 2261) * mm});
            skLineSegment(sketch, "E3534", {"start": v(2062.15, 2261) * mm, "end": v(2062.54, 2261.02) * mm});
            skLineSegment(sketch, "E3535", {"start": v(2062.54, 2261.02) * mm, "end": v(2062.94, 2261.04) * mm});
            skLineSegment(sketch, "E3536", {"start": v(2062.94, 2261.04) * mm, "end": v(2077.6, 2261.04) * mm});
            skLineSegment(sketch, "E3537", {"start": v(1944.8, 1189.72) * mm, "end": v(1967.85, 1189.73) * mm});
            skLineSegment(sketch, "E3538", {"start": v(1967.85, 1189.73) * mm, "end": v(1968.14, 1189.73) * mm});
            skLineSegment(sketch, "E3539", {"start": v(1968.14, 1189.73) * mm, "end": v(1968.44, 1189.72) * mm});
            skLineSegment(sketch, "E3540", {"start": v(1968.44, 1189.72) * mm, "end": v(1968.73, 1189.7) * mm});
            skLineSegment(sketch, "E3541", {"start": v(1968.73, 1189.7) * mm, "end": v(1969.03, 1189.68) * mm});
            skLineSegment(sketch, "E3542", {"start": v(1969.03, 1189.68) * mm, "end": v(1969.6, 1189.6) * mm});
            skLineSegment(sketch, "E3543", {"start": v(1969.6, 1189.6) * mm, "end": v(1970.19, 1189.5) * mm});
            skLineSegment(sketch, "E3544", {"start": v(1970.19, 1189.5) * mm, "end": v(1970.76, 1189.37) * mm});
            skLineSegment(sketch, "E3545", {"start": v(1970.76, 1189.37) * mm, "end": v(1971.32, 1189.2) * mm});
            skLineSegment(sketch, "E3546", {"start": v(1971.32, 1189.2) * mm, "end": v(1971.87, 1189.02) * mm});
            skLineSegment(sketch, "E3547", {"start": v(1971.87, 1189.02) * mm, "end": v(1972.41, 1188.8) * mm});
            skLineSegment(sketch, "E3548", {"start": v(1972.41, 1188.8) * mm, "end": v(1972.95, 1188.56) * mm});
            skLineSegment(sketch, "E3549", {"start": v(1972.95, 1188.56) * mm, "end": v(1973.46, 1188.3) * mm});
            skLineSegment(sketch, "E3550", {"start": v(1973.46, 1188.3) * mm, "end": v(1973.97, 1188) * mm});
            skLineSegment(sketch, "E3551", {"start": v(1973.97, 1188) * mm, "end": v(1974.46, 1187.68) * mm});
            skLineSegment(sketch, "E3552", {"start": v(1974.46, 1187.68) * mm, "end": v(1974.93, 1187.33) * mm});
            skLineSegment(sketch, "E3553", {"start": v(1974.93, 1187.33) * mm, "end": v(1975.16, 1187.15) * mm});
            skLineSegment(sketch, "E3554", {"start": v(1975.16, 1187.15) * mm, "end": v(1975.39, 1186.96) * mm});
            skLineSegment(sketch, "E3555", {"start": v(1975.39, 1186.96) * mm, "end": v(1975.6, 1186.77) * mm});
            skLineSegment(sketch, "E3556", {"start": v(1975.6, 1186.77) * mm, "end": v(1975.83, 1186.57) * mm});
            skLineSegment(sketch, "E3557", {"start": v(1975.83, 1186.57) * mm, "end": v(1976.04, 1186.36) * mm});
            skLineSegment(sketch, "E3558", {"start": v(1976.04, 1186.36) * mm, "end": v(1976.25, 1186.15) * mm});
            skLineSegment(sketch, "E3559", {"start": v(1976.25, 1186.15) * mm, "end": v(1976.47, 1185.92) * mm});
            skLineSegment(sketch, "E3560", {"start": v(1976.47, 1185.92) * mm, "end": v(1976.69, 1185.68) * mm});
            skLineSegment(sketch, "E3561", {"start": v(1976.69, 1185.68) * mm, "end": v(1976.9, 1185.44) * mm});
            skLineSegment(sketch, "E3562", {"start": v(1976.9, 1185.44) * mm, "end": v(1977.1, 1185.2) * mm});
            skLineSegment(sketch, "E3563", {"start": v(1977.1, 1185.2) * mm, "end": v(1977.3, 1184.95) * mm});
            skLineSegment(sketch, "E3564", {"start": v(1977.3, 1184.95) * mm, "end": v(1977.5, 1184.7) * mm});
            skLineSegment(sketch, "E3565", {"start": v(1977.5, 1184.7) * mm, "end": v(1977.69, 1184.44) * mm});
            skLineSegment(sketch, "E3566", {"start": v(1977.69, 1184.44) * mm, "end": v(1977.87, 1184.17) * mm});
            skLineSegment(sketch, "E3567", {"start": v(1977.87, 1184.17) * mm, "end": v(1978.04, 1183.9) * mm});
            skLineSegment(sketch, "E3568", {"start": v(1978.04, 1183.9) * mm, "end": v(1978.2, 1183.63) * mm});
            skLineSegment(sketch, "E3569", {"start": v(1978.2, 1183.63) * mm, "end": v(1978.37, 1183.36) * mm});
            skLineSegment(sketch, "E3570", {"start": v(1978.37, 1183.36) * mm, "end": v(1978.52, 1183.08) * mm});
            skLineSegment(sketch, "E3571", {"start": v(1978.52, 1183.08) * mm, "end": v(1978.67, 1182.8) * mm});
            skLineSegment(sketch, "E3572", {"start": v(1978.67, 1182.8) * mm, "end": v(1978.8, 1182.51) * mm});
            skLineSegment(sketch, "E3573", {"start": v(1978.8, 1182.51) * mm, "end": v(1978.94, 1182.23) * mm});
            skLineSegment(sketch, "E3574", {"start": v(1978.94, 1182.23) * mm, "end": v(1979.07, 1181.93) * mm});
            skLineSegment(sketch, "E3575", {"start": v(1979.07, 1181.93) * mm, "end": v(1979.18, 1181.64) * mm});
            skLineSegment(sketch, "E3576", {"start": v(1979.18, 1181.64) * mm, "end": v(1979.3, 1181.34) * mm});
            skLineSegment(sketch, "E3577", {"start": v(1979.3, 1181.34) * mm, "end": v(1979.4, 1181.04) * mm});
            skLineSegment(sketch, "E3578", {"start": v(1979.4, 1181.04) * mm, "end": v(1979.5, 1180.74) * mm});
            skLineSegment(sketch, "E3579", {"start": v(1979.5, 1180.74) * mm, "end": v(1979.58, 1180.44) * mm});
            skLineSegment(sketch, "E3580", {"start": v(1979.58, 1180.44) * mm, "end": v(1979.67, 1180.13) * mm});
            skLineSegment(sketch, "E3581", {"start": v(1979.67, 1180.13) * mm, "end": v(1979.74, 1179.82) * mm});
            skLineSegment(sketch, "E3582", {"start": v(1979.74, 1179.82) * mm, "end": v(1979.8, 1179.5) * mm});
            skLineSegment(sketch, "E3583", {"start": v(1979.8, 1179.5) * mm, "end": v(1979.87, 1179.2) * mm});
            skLineSegment(sketch, "E3584", {"start": v(1979.87, 1179.2) * mm, "end": v(1979.92, 1178.88) * mm});
            skLineSegment(sketch, "E3585", {"start": v(1979.92, 1178.88) * mm, "end": v(1979.96, 1178.56) * mm});
            skLineSegment(sketch, "E3586", {"start": v(1979.96, 1178.56) * mm, "end": v(1980, 1178.25) * mm});
            skLineSegment(sketch, "E3587", {"start": v(1980, 1178.25) * mm, "end": v(1980.03, 1177.93) * mm});
            skLineSegment(sketch, "E3588", {"start": v(1980.03, 1177.93) * mm, "end": v(1980.05, 1177.6) * mm});
            skLineSegment(sketch, "E3589", {"start": v(1980.05, 1177.6) * mm, "end": v(1980.06, 1177.29) * mm});
            skLineSegment(sketch, "E3590", {"start": v(1980.06, 1177.29) * mm, "end": v(1980.06, 1176.96) * mm});
            skLineSegment(sketch, "E3591", {"start": v(1980.06, 1176.96) * mm, "end": v(1980.06, 1176.64) * mm});
            skLineSegment(sketch, "E3592", {"start": v(1980.06, 1176.64) * mm, "end": v(1980.06, 1176.32) * mm});
            skLineSegment(sketch, "E3593", {"start": v(1980.06, 1176.32) * mm, "end": v(1980.04, 1176) * mm});
            skLineSegment(sketch, "E3594", {"start": v(1980.04, 1176) * mm, "end": v(1980.02, 1175.68) * mm});
            skLineSegment(sketch, "E3595", {"start": v(1980.02, 1175.68) * mm, "end": v(1980, 1175.37) * mm});
            skLineSegment(sketch, "E3596", {"start": v(1980, 1175.37) * mm, "end": v(1979.95, 1175.05) * mm});
            skLineSegment(sketch, "E3597", {"start": v(1979.95, 1175.05) * mm, "end": v(1979.9, 1174.74) * mm});
            skLineSegment(sketch, "E3598", {"start": v(1979.9, 1174.74) * mm, "end": v(1979.85, 1174.42) * mm});
            skLineSegment(sketch, "E3599", {"start": v(1979.85, 1174.42) * mm, "end": v(1979.8, 1174.11) * mm});
            skLineSegment(sketch, "E3600", {"start": v(1979.8, 1174.11) * mm, "end": v(1979.72, 1173.8) * mm});
            skLineSegment(sketch, "E3601", {"start": v(1979.72, 1173.8) * mm, "end": v(1979.65, 1173.5) * mm});
            skLineSegment(sketch, "E3602", {"start": v(1979.65, 1173.5) * mm, "end": v(1979.56, 1173.19) * mm});
            skLineSegment(sketch, "E3603", {"start": v(1979.56, 1173.19) * mm, "end": v(1979.47, 1172.89) * mm});
            skLineSegment(sketch, "E3604", {"start": v(1979.47, 1172.89) * mm, "end": v(1979.37, 1172.59) * mm});
            skLineSegment(sketch, "E3605", {"start": v(1979.37, 1172.59) * mm, "end": v(1979.27, 1172.29) * mm});
            skLineSegment(sketch, "E3606", {"start": v(1979.27, 1172.29) * mm, "end": v(1979.16, 1172) * mm});
            skLineSegment(sketch, "E3607", {"start": v(1979.16, 1172) * mm, "end": v(1979.04, 1171.7) * mm});
            skLineSegment(sketch, "E3608", {"start": v(1979.04, 1171.7) * mm, "end": v(1978.9, 1171.4) * mm});
            skLineSegment(sketch, "E3609", {"start": v(1978.9, 1171.4) * mm, "end": v(1978.77, 1171.12) * mm});
            skLineSegment(sketch, "E3610", {"start": v(1978.77, 1171.12) * mm, "end": v(1978.63, 1170.84) * mm});
            skLineSegment(sketch, "E3611", {"start": v(1978.63, 1170.84) * mm, "end": v(1978.48, 1170.56) * mm});
            skLineSegment(sketch, "E3612", {"start": v(1978.48, 1170.56) * mm, "end": v(1978.33, 1170.28) * mm});
            skLineSegment(sketch, "E3613", {"start": v(1978.33, 1170.28) * mm, "end": v(1978.17, 1170.01) * mm});
            skLineSegment(sketch, "E3614", {"start": v(1978.17, 1170.01) * mm, "end": v(1978, 1169.74) * mm});
            skLineSegment(sketch, "E3615", {"start": v(1978, 1169.74) * mm, "end": v(1977.82, 1169.48) * mm});
            skLineSegment(sketch, "E3616", {"start": v(1977.82, 1169.48) * mm, "end": v(1977.64, 1169.22) * mm});
            skLineSegment(sketch, "E3617", {"start": v(1977.64, 1169.22) * mm, "end": v(1977.45, 1168.96) * mm});
            skLineSegment(sketch, "E3618", {"start": v(1977.45, 1168.96) * mm, "end": v(1977.26, 1168.7) * mm});
            skLineSegment(sketch, "E3619", {"start": v(1977.26, 1168.7) * mm, "end": v(1977.06, 1168.46) * mm});
            skLineSegment(sketch, "E3620", {"start": v(1977.06, 1168.46) * mm, "end": v(1976.85, 1168.22) * mm});
            skLineSegment(sketch, "E3621", {"start": v(1976.85, 1168.22) * mm, "end": v(1976.63, 1167.98) * mm});
            skLineSegment(sketch, "E3622", {"start": v(1976.63, 1167.98) * mm, "end": v(1976.41, 1167.75) * mm});
            skLineSegment(sketch, "E3623", {"start": v(1976.41, 1167.75) * mm, "end": v(1976.2, 1167.53) * mm});
            skLineSegment(sketch, "E3624", {"start": v(1976.2, 1167.53) * mm, "end": v(1975.98, 1167.32) * mm});
            skLineSegment(sketch, "E3625", {"start": v(1975.98, 1167.32) * mm, "end": v(1975.76, 1167.11) * mm});
            skLineSegment(sketch, "E3626", {"start": v(1975.76, 1167.11) * mm, "end": v(1975.54, 1166.91) * mm});
            skLineSegment(sketch, "E3627", {"start": v(1975.54, 1166.91) * mm, "end": v(1975.3, 1166.72) * mm});
            skLineSegment(sketch, "E3628", {"start": v(1975.3, 1166.72) * mm, "end": v(1975.07, 1166.53) * mm});
            skLineSegment(sketch, "E3629", {"start": v(1975.07, 1166.53) * mm, "end": v(1974.83, 1166.35) * mm});
            skLineSegment(sketch, "E3630", {"start": v(1974.83, 1166.35) * mm, "end": v(1974.6, 1166.18) * mm});
            skLineSegment(sketch, "E3631", {"start": v(1974.6, 1166.18) * mm, "end": v(1974.34, 1166) * mm});
            skLineSegment(sketch, "E3632", {"start": v(1974.34, 1166) * mm, "end": v(1974.1, 1165.85) * mm});
            skLineSegment(sketch, "E3633", {"start": v(1974.1, 1165.85) * mm, "end": v(1973.84, 1165.7) * mm});
            skLineSegment(sketch, "E3634", {"start": v(1973.84, 1165.7) * mm, "end": v(1973.58, 1165.54) * mm});
            skLineSegment(sketch, "E3635", {"start": v(1973.58, 1165.54) * mm, "end": v(1973.05, 1165.27) * mm});
            skLineSegment(sketch, "E3636", {"start": v(1973.05, 1165.27) * mm, "end": v(1972.5, 1165.02) * mm});
            skLineSegment(sketch, "E3637", {"start": v(1972.5, 1165.02) * mm, "end": v(1971.96, 1164.8) * mm});
            skLineSegment(sketch, "E3638", {"start": v(1971.96, 1164.8) * mm, "end": v(1971.67, 1164.7) * mm});
            skLineSegment(sketch, "E3639", {"start": v(1971.67, 1164.7) * mm, "end": v(1971.4, 1164.6) * mm});
            skLineSegment(sketch, "E3640", {"start": v(1971.4, 1164.6) * mm, "end": v(1971.1, 1164.51) * mm});
            skLineSegment(sketch, "E3641", {"start": v(1971.1, 1164.51) * mm, "end": v(1970.82, 1164.43) * mm});
            skLineSegment(sketch, "E3642", {"start": v(1970.82, 1164.43) * mm, "end": v(1970.53, 1164.36) * mm});
            skLineSegment(sketch, "E3643", {"start": v(1970.53, 1164.36) * mm, "end": v(1970.24, 1164.3) * mm});
            skLineSegment(sketch, "E3644", {"start": v(1970.24, 1164.3) * mm, "end": v(1969.94, 1164.24) * mm});
            skLineSegment(sketch, "E3645", {"start": v(1969.94, 1164.24) * mm, "end": v(1969.65, 1164.18) * mm});
            skLineSegment(sketch, "E3646", {"start": v(1969.65, 1164.18) * mm, "end": v(1969.35, 1164.14) * mm});
            skLineSegment(sketch, "E3647", {"start": v(1969.35, 1164.14) * mm, "end": v(1969.05, 1164.1) * mm});
            skLineSegment(sketch, "E3648", {"start": v(1969.05, 1164.1) * mm, "end": v(1968.75, 1164.08) * mm});
            skLineSegment(sketch, "E3649", {"start": v(1968.75, 1164.08) * mm, "end": v(1968.45, 1164.06) * mm});
            skLineSegment(sketch, "E3650", {"start": v(1968.45, 1164.06) * mm, "end": v(1968.15, 1164.05) * mm});
            skLineSegment(sketch, "E3651", {"start": v(1968.15, 1164.05) * mm, "end": v(1967.85, 1164.04) * mm});
            skLineSegment(sketch, "E3652", {"start": v(1967.85, 1164.04) * mm, "end": v(1944.8, 1164.04) * mm});
            skLineSegment(sketch, "E3653", {"start": v(1979.76, 1197.63) * mm, "end": v(1944.8, 1197.63) * mm});
            skLineSegment(sketch, "E3654", {"start": v(1944.8, 1197.63) * mm, "end": v(1944.8, 1198.96) * mm});
            skLineSegment(sketch, "E3655", {"start": v(1944.8, 1198.96) * mm, "end": v(1979.76, 1221.92) * mm});
            skLineSegment(sketch, "E3656", {"start": v(1979.76, 1221.92) * mm, "end": v(1979.76, 1223.32) * mm});
            skLineSegment(sketch, "E3657", {"start": v(1979.76, 1223.32) * mm, "end": v(1944.81, 1223.32) * mm});
            skLineSegment(sketch, "E3658", {"start": v(1979.77, 1231.22) * mm, "end": v(1944.8, 1231.22) * mm});
            skLineSegment(sketch, "E3659", {"start": v(1944.8, 1231.22) * mm, "end": v(1944.8, 1244.04) * mm});
            skLineSegment(sketch, "E3660", {"start": v(1944.8, 1244.04) * mm, "end": v(1944.8, 1244.35) * mm});
            skLineSegment(sketch, "E3661", {"start": v(1944.8, 1244.35) * mm, "end": v(1944.83, 1244.65) * mm});
            skLineSegment(sketch, "E3662", {"start": v(1944.83, 1244.65) * mm, "end": v(1944.86, 1244.95) * mm});
            skLineSegment(sketch, "E3663", {"start": v(1944.86, 1244.95) * mm, "end": v(1944.9, 1245.25) * mm});
            skLineSegment(sketch, "E3664", {"start": v(1944.9, 1245.25) * mm, "end": v(1944.94, 1245.55) * mm});
            skLineSegment(sketch, "E3665", {"start": v(1944.94, 1245.55) * mm, "end": v(1945, 1245.85) * mm});
            skLineSegment(sketch, "E3666", {"start": v(1945, 1245.85) * mm, "end": v(1945.05, 1246.14) * mm});
            skLineSegment(sketch, "E3667", {"start": v(1945.05, 1246.14) * mm, "end": v(1945.12, 1246.44) * mm});
            skLineSegment(sketch, "E3668", {"start": v(1945.12, 1246.44) * mm, "end": v(1945.2, 1246.73) * mm});
            skLineSegment(sketch, "E3669", {"start": v(1945.2, 1246.73) * mm, "end": v(1945.27, 1247.02) * mm});
            skLineSegment(sketch, "E3670", {"start": v(1945.27, 1247.02) * mm, "end": v(1945.36, 1247.3) * mm});
            skLineSegment(sketch, "E3671", {"start": v(1945.36, 1247.3) * mm, "end": v(1945.46, 1247.59) * mm});
            skLineSegment(sketch, "E3672", {"start": v(1945.46, 1247.59) * mm, "end": v(1945.67, 1248.15) * mm});
            skLineSegment(sketch, "E3673", {"start": v(1945.67, 1248.15) * mm, "end": v(1945.91, 1248.7) * mm});
            skLineSegment(sketch, "E3674", {"start": v(1945.91, 1248.7) * mm, "end": v(1946.18, 1249.23) * mm});
            skLineSegment(sketch, "E3675", {"start": v(1946.18, 1249.23) * mm, "end": v(1946.47, 1249.76) * mm});
            skLineSegment(sketch, "E3676", {"start": v(1946.47, 1249.76) * mm, "end": v(1946.63, 1250.01) * mm});
            skLineSegment(sketch, "E3677", {"start": v(1946.63, 1250.01) * mm, "end": v(1946.8, 1250.26) * mm});
            skLineSegment(sketch, "E3678", {"start": v(1946.8, 1250.26) * mm, "end": v(1946.96, 1250.51) * mm});
            skLineSegment(sketch, "E3679", {"start": v(1946.96, 1250.51) * mm, "end": v(1947.14, 1250.76) * mm});
            skLineSegment(sketch, "E3680", {"start": v(1947.14, 1250.76) * mm, "end": v(1947.32, 1251) * mm});
            skLineSegment(sketch, "E3681", {"start": v(1947.32, 1251) * mm, "end": v(1947.51, 1251.23) * mm});
            skLineSegment(sketch, "E3682", {"start": v(1947.51, 1251.23) * mm, "end": v(1947.7, 1251.46) * mm});
            skLineSegment(sketch, "E3683", {"start": v(1947.7, 1251.46) * mm, "end": v(1947.9, 1251.69) * mm});
            skLineSegment(sketch, "E3684", {"start": v(1947.9, 1251.69) * mm, "end": v(1948.11, 1251.9) * mm});
            skLineSegment(sketch, "E3685", {"start": v(1948.11, 1251.9) * mm, "end": v(1948.33, 1252.12) * mm});
            skLineSegment(sketch, "E3686", {"start": v(1948.33, 1252.12) * mm, "end": v(1948.54, 1252.33) * mm});
            skLineSegment(sketch, "E3687", {"start": v(1948.54, 1252.33) * mm, "end": v(1948.77, 1252.54) * mm});
            skLineSegment(sketch, "E3688", {"start": v(1948.77, 1252.54) * mm, "end": v(1949.13, 1252.9) * mm});
            skLineSegment(sketch, "E3689", {"start": v(1949.13, 1252.9) * mm, "end": v(1949.5, 1253.23) * mm});
            skLineSegment(sketch, "E3690", {"start": v(1949.5, 1253.23) * mm, "end": v(1949.88, 1253.56) * mm});
            skLineSegment(sketch, "E3691", {"start": v(1949.88, 1253.56) * mm, "end": v(1950.26, 1253.88) * mm});
            skLineSegment(sketch, "E3692", {"start": v(1950.26, 1253.88) * mm, "end": v(1950.65, 1254.2) * mm});
            skLineSegment(sketch, "E3693", {"start": v(1950.65, 1254.2) * mm, "end": v(1951.05, 1254.5) * mm});
            skLineSegment(sketch, "E3694", {"start": v(1951.05, 1254.5) * mm, "end": v(1951.46, 1254.78) * mm});
            skLineSegment(sketch, "E3695", {"start": v(1951.46, 1254.78) * mm, "end": v(1951.87, 1255.06) * mm});
            skLineSegment(sketch, "E3696", {"start": v(1951.87, 1255.06) * mm, "end": v(1952.29, 1255.33) * mm});
            skLineSegment(sketch, "E3697", {"start": v(1952.29, 1255.33) * mm, "end": v(1952.71, 1255.59) * mm});
            skLineSegment(sketch, "E3698", {"start": v(1952.71, 1255.59) * mm, "end": v(1953.14, 1255.83) * mm});
            skLineSegment(sketch, "E3699", {"start": v(1953.14, 1255.83) * mm, "end": v(1953.58, 1256.07) * mm});
            skLineSegment(sketch, "E3700", {"start": v(1953.58, 1256.07) * mm, "end": v(1954.02, 1256.3) * mm});
            skLineSegment(sketch, "E3701", {"start": v(1954.02, 1256.3) * mm, "end": v(1954.47, 1256.5) * mm});
            skLineSegment(sketch, "E3702", {"start": v(1954.47, 1256.5) * mm, "end": v(1954.92, 1256.7) * mm});
            skLineSegment(sketch, "E3703", {"start": v(1954.92, 1256.7) * mm, "end": v(1955.38, 1256.9) * mm});
            skLineSegment(sketch, "E3704", {"start": v(1955.38, 1256.9) * mm, "end": v(1955.84, 1257.08) * mm});
            skLineSegment(sketch, "E3705", {"start": v(1955.84, 1257.08) * mm, "end": v(1956.3, 1257.24) * mm});
            skLineSegment(sketch, "E3706", {"start": v(1956.3, 1257.24) * mm, "end": v(1956.78, 1257.4) * mm});
            skLineSegment(sketch, "E3707", {"start": v(1956.78, 1257.4) * mm, "end": v(1957.25, 1257.54) * mm});
            skLineSegment(sketch, "E3708", {"start": v(1957.25, 1257.54) * mm, "end": v(1957.73, 1257.68) * mm});
            skLineSegment(sketch, "E3709", {"start": v(1957.73, 1257.68) * mm, "end": v(1958.21, 1257.8) * mm});
            skLineSegment(sketch, "E3710", {"start": v(1958.21, 1257.8) * mm, "end": v(1958.7, 1257.9) * mm});
            skLineSegment(sketch, "E3711", {"start": v(1958.7, 1257.9) * mm, "end": v(1959.19, 1258) * mm});
            skLineSegment(sketch, "E3712", {"start": v(1959.19, 1258) * mm, "end": v(1959.68, 1258.09) * mm});
            skLineSegment(sketch, "E3713", {"start": v(1959.68, 1258.09) * mm, "end": v(1960.17, 1258.16) * mm});
            skLineSegment(sketch, "E3714", {"start": v(1960.17, 1258.16) * mm, "end": v(1960.66, 1258.22) * mm});
            skLineSegment(sketch, "E3715", {"start": v(1960.66, 1258.22) * mm, "end": v(1961.16, 1258.27) * mm});
            skLineSegment(sketch, "E3716", {"start": v(1961.16, 1258.27) * mm, "end": v(1961.66, 1258.3) * mm});
            skLineSegment(sketch, "E3717", {"start": v(1961.66, 1258.3) * mm, "end": v(1962.16, 1258.32) * mm});
            skLineSegment(sketch, "E3718", {"start": v(1962.16, 1258.32) * mm, "end": v(1962.66, 1258.33) * mm});
            skLineSegment(sketch, "E3719", {"start": v(1962.66, 1258.33) * mm, "end": v(1963.17, 1258.33) * mm});
            skLineSegment(sketch, "E3720", {"start": v(1963.17, 1258.33) * mm, "end": v(1963.59, 1258.34) * mm});
            skLineSegment(sketch, "E3721", {"start": v(1963.59, 1258.34) * mm, "end": v(1964.01, 1258.34) * mm});
            skLineSegment(sketch, "E3722", {"start": v(1964.01, 1258.34) * mm, "end": v(1964.43, 1258.33) * mm});
            skLineSegment(sketch, "E3723", {"start": v(1964.43, 1258.33) * mm, "end": v(1964.85, 1258.3) * mm});
            skLineSegment(sketch, "E3724", {"start": v(1964.85, 1258.3) * mm, "end": v(1965.27, 1258.28) * mm});
            skLineSegment(sketch, "E3725", {"start": v(1965.27, 1258.28) * mm, "end": v(1965.68, 1258.23) * mm});
            skLineSegment(sketch, "E3726", {"start": v(1965.68, 1258.23) * mm, "end": v(1966.1, 1258.18) * mm});
            skLineSegment(sketch, "E3727", {"start": v(1966.1, 1258.18) * mm, "end": v(1966.51, 1258.12) * mm});
            skLineSegment(sketch, "E3728", {"start": v(1966.51, 1258.12) * mm, "end": v(1966.92, 1258.05) * mm});
            skLineSegment(sketch, "E3729", {"start": v(1966.92, 1258.05) * mm, "end": v(1967.33, 1257.97) * mm});
            skLineSegment(sketch, "E3730", {"start": v(1967.33, 1257.97) * mm, "end": v(1967.74, 1257.87) * mm});
            skLineSegment(sketch, "E3731", {"start": v(1967.74, 1257.87) * mm, "end": v(1968.14, 1257.77) * mm});
            skLineSegment(sketch, "E3732", {"start": v(1968.14, 1257.77) * mm, "end": v(1968.54, 1257.66) * mm});
            skLineSegment(sketch, "E3733", {"start": v(1968.54, 1257.66) * mm, "end": v(1968.94, 1257.54) * mm});
            skLineSegment(sketch, "E3734", {"start": v(1968.94, 1257.54) * mm, "end": v(1969.33, 1257.4) * mm});
            skLineSegment(sketch, "E3735", {"start": v(1969.33, 1257.4) * mm, "end": v(1969.72, 1257.27) * mm});
            skLineSegment(sketch, "E3736", {"start": v(1969.72, 1257.27) * mm, "end": v(1970.11, 1257.12) * mm});
            skLineSegment(sketch, "E3737", {"start": v(1970.11, 1257.12) * mm, "end": v(1970.5, 1256.96) * mm});
            skLineSegment(sketch, "E3738", {"start": v(1970.5, 1256.96) * mm, "end": v(1970.87, 1256.79) * mm});
            skLineSegment(sketch, "E3739", {"start": v(1970.87, 1256.79) * mm, "end": v(1971.25, 1256.6) * mm});
            skLineSegment(sketch, "E3740", {"start": v(1971.25, 1256.6) * mm, "end": v(1971.62, 1256.42) * mm});
            skLineSegment(sketch, "E3741", {"start": v(1971.62, 1256.42) * mm, "end": v(1971.99, 1256.22) * mm});
            skLineSegment(sketch, "E3742", {"start": v(1971.99, 1256.22) * mm, "end": v(1972.35, 1256.02) * mm});
            skLineSegment(sketch, "E3743", {"start": v(1972.35, 1256.02) * mm, "end": v(1972.7, 1255.8) * mm});
            skLineSegment(sketch, "E3744", {"start": v(1972.7, 1255.8) * mm, "end": v(1973.06, 1255.58) * mm});
            skLineSegment(sketch, "E3745", {"start": v(1973.06, 1255.58) * mm, "end": v(1973.4, 1255.35) * mm});
            skLineSegment(sketch, "E3746", {"start": v(1973.4, 1255.35) * mm, "end": v(1973.75, 1255.1) * mm});
            skLineSegment(sketch, "E3747", {"start": v(1973.75, 1255.1) * mm, "end": v(1974.09, 1254.86) * mm});
            skLineSegment(sketch, "E3748", {"start": v(1974.09, 1254.86) * mm, "end": v(1974.42, 1254.6) * mm});
            skLineSegment(sketch, "E3749", {"start": v(1974.42, 1254.6) * mm, "end": v(1974.74, 1254.33) * mm});
            skLineSegment(sketch, "E3750", {"start": v(1974.74, 1254.33) * mm, "end": v(1975.06, 1254.05) * mm});
            skLineSegment(sketch, "E3751", {"start": v(1975.06, 1254.05) * mm, "end": v(1975.37, 1253.77) * mm});
            skLineSegment(sketch, "E3752", {"start": v(1975.37, 1253.77) * mm, "end": v(1975.62, 1253.53) * mm});
            skLineSegment(sketch, "E3753", {"start": v(1975.62, 1253.53) * mm, "end": v(1975.86, 1253.29) * mm});
            skLineSegment(sketch, "E3754", {"start": v(1975.86, 1253.29) * mm, "end": v(1976.1, 1253.03) * mm});
            skLineSegment(sketch, "E3755", {"start": v(1976.1, 1253.03) * mm, "end": v(1976.33, 1252.78) * mm});
            skLineSegment(sketch, "E3756", {"start": v(1976.33, 1252.78) * mm, "end": v(1976.55, 1252.52) * mm});
            skLineSegment(sketch, "E3757", {"start": v(1976.55, 1252.52) * mm, "end": v(1976.76, 1252.25) * mm});
            skLineSegment(sketch, "E3758", {"start": v(1976.76, 1252.25) * mm, "end": v(1976.97, 1251.98) * mm});
            skLineSegment(sketch, "E3759", {"start": v(1976.97, 1251.98) * mm, "end": v(1977.18, 1251.7) * mm});
            skLineSegment(sketch, "E3760", {"start": v(1977.18, 1251.7) * mm, "end": v(1977.37, 1251.42) * mm});
            skLineSegment(sketch, "E3761", {"start": v(1977.37, 1251.42) * mm, "end": v(1977.56, 1251.14) * mm});
            skLineSegment(sketch, "E3762", {"start": v(1977.56, 1251.14) * mm, "end": v(1977.74, 1250.85) * mm});
            skLineSegment(sketch, "E3763", {"start": v(1977.74, 1250.85) * mm, "end": v(1977.91, 1250.56) * mm});
            skLineSegment(sketch, "E3764", {"start": v(1977.91, 1250.56) * mm, "end": v(1978.08, 1250.26) * mm});
            skLineSegment(sketch, "E3765", {"start": v(1978.08, 1250.26) * mm, "end": v(1978.24, 1249.96) * mm});
            skLineSegment(sketch, "E3766", {"start": v(1978.24, 1249.96) * mm, "end": v(1978.39, 1249.65) * mm});
            skLineSegment(sketch, "E3767", {"start": v(1978.39, 1249.65) * mm, "end": v(1978.53, 1249.34) * mm});
            skLineSegment(sketch, "E3768", {"start": v(1978.53, 1249.34) * mm, "end": v(1978.67, 1249.03) * mm});
            skLineSegment(sketch, "E3769", {"start": v(1978.67, 1249.03) * mm, "end": v(1978.8, 1248.72) * mm});
            skLineSegment(sketch, "E3770", {"start": v(1978.8, 1248.72) * mm, "end": v(1978.92, 1248.4) * mm});
            skLineSegment(sketch, "E3771", {"start": v(1978.92, 1248.4) * mm, "end": v(1979.03, 1248.08) * mm});
            skLineSegment(sketch, "E3772", {"start": v(1979.03, 1248.08) * mm, "end": v(1979.14, 1247.75) * mm});
            skLineSegment(sketch, "E3773", {"start": v(1979.14, 1247.75) * mm, "end": v(1979.24, 1247.43) * mm});
            skLineSegment(sketch, "E3774", {"start": v(1979.24, 1247.43) * mm, "end": v(1979.33, 1247.1) * mm});
            skLineSegment(sketch, "E3775", {"start": v(1979.33, 1247.1) * mm, "end": v(1979.4, 1246.76) * mm});
            skLineSegment(sketch, "E3776", {"start": v(1979.4, 1246.76) * mm, "end": v(1979.48, 1246.43) * mm});
            skLineSegment(sketch, "E3777", {"start": v(1979.48, 1246.43) * mm, "end": v(1979.55, 1246.1) * mm});
            skLineSegment(sketch, "E3778", {"start": v(1979.55, 1246.1) * mm, "end": v(1979.6, 1245.76) * mm});
            skLineSegment(sketch, "E3779", {"start": v(1979.6, 1245.76) * mm, "end": v(1979.66, 1245.42) * mm});
            skLineSegment(sketch, "E3780", {"start": v(1979.66, 1245.42) * mm, "end": v(1979.7, 1245.08) * mm});
            skLineSegment(sketch, "E3781", {"start": v(1979.7, 1245.08) * mm, "end": v(1979.73, 1244.73) * mm});
            skLineSegment(sketch, "E3782", {"start": v(1979.73, 1244.73) * mm, "end": v(1979.75, 1244.4) * mm});
            skLineSegment(sketch, "E3783", {"start": v(1979.75, 1244.4) * mm, "end": v(1979.77, 1244.04) * mm});
            skLineSegment(sketch, "E3784", {"start": v(1979.77, 1244.04) * mm, "end": v(1979.77, 1231.22) * mm});
            skLineSegment(sketch, "E3785", {"start": v(1979.76, 1289.25) * mm, "end": v(1979.76, 1266.23) * mm});
            skLineSegment(sketch, "E3786", {"start": v(1979.76, 1266.23) * mm, "end": v(1944.8, 1266.23) * mm});
            skLineSegment(sketch, "E3787", {"start": v(1944.8, 1266.23) * mm, "end": v(1944.8, 1289.25) * mm});
            skLineSegment(sketch, "E3788", {"start": v(1961.65, 1266.23) * mm, "end": v(1961.65, 1286.36) * mm});
            skLineSegment(sketch, "E3789", {"start": v(1979.76, 1296.95) * mm, "end": v(1944.8, 1296.95) * mm});
            skLineSegment(sketch, "E3790", {"start": v(1944.8, 1296.95) * mm, "end": v(1944.8, 1312.32) * mm});
            skLineSegment(sketch, "E3791", {"start": v(1944.8, 1312.32) * mm, "end": v(1944.8, 1312.75) * mm});
            skLineSegment(sketch, "E3792", {"start": v(1944.8, 1312.75) * mm, "end": v(1944.83, 1313.18) * mm});
            skLineSegment(sketch, "E3793", {"start": v(1944.83, 1313.18) * mm, "end": v(1944.87, 1313.6) * mm});
            skLineSegment(sketch, "E3794", {"start": v(1944.87, 1313.6) * mm, "end": v(1944.94, 1314.03) * mm});
            skLineSegment(sketch, "E3795", {"start": v(1944.94, 1314.03) * mm, "end": v(1945.03, 1314.45) * mm});
            skLineSegment(sketch, "E3796", {"start": v(1945.03, 1314.45) * mm, "end": v(1945.14, 1314.86) * mm});
            skLineSegment(sketch, "E3797", {"start": v(1945.14, 1314.86) * mm, "end": v(1945.28, 1315.26) * mm});
            skLineSegment(sketch, "E3798", {"start": v(1945.28, 1315.26) * mm, "end": v(1945.43, 1315.66) * mm});
            skLineSegment(sketch, "E3799", {"start": v(1945.43, 1315.66) * mm, "end": v(1945.6, 1316.05) * mm});
            skLineSegment(sketch, "E3800", {"start": v(1945.6, 1316.05) * mm, "end": v(1945.8, 1316.43) * mm});
            skLineSegment(sketch, "E3801", {"start": v(1945.8, 1316.43) * mm, "end": v(1946, 1316.8) * mm});
            skLineSegment(sketch, "E3802", {"start": v(1946, 1316.8) * mm, "end": v(1946.23, 1317.16) * mm});
            skLineSegment(sketch, "E3803", {"start": v(1946.23, 1317.16) * mm, "end": v(1946.48, 1317.5) * mm});
            skLineSegment(sketch, "E3804", {"start": v(1946.48, 1317.5) * mm, "end": v(1946.75, 1317.85) * mm});
            skLineSegment(sketch, "E3805", {"start": v(1946.75, 1317.85) * mm, "end": v(1947.03, 1318.17) * mm});
            skLineSegment(sketch, "E3806", {"start": v(1947.03, 1318.17) * mm, "end": v(1947.34, 1318.48) * mm});
            skLineSegment(sketch, "E3807", {"start": v(1947.34, 1318.48) * mm, "end": v(1947.64, 1318.78) * mm});
            skLineSegment(sketch, "E3808", {"start": v(1947.64, 1318.78) * mm, "end": v(1947.96, 1319.06) * mm});
            skLineSegment(sketch, "E3809", {"start": v(1947.96, 1319.06) * mm, "end": v(1948.3, 1319.32) * mm});
            skLineSegment(sketch, "E3810", {"start": v(1948.3, 1319.32) * mm, "end": v(1948.64, 1319.57) * mm});
            skLineSegment(sketch, "E3811", {"start": v(1948.64, 1319.57) * mm, "end": v(1949, 1319.8) * mm});
            skLineSegment(sketch, "E3812", {"start": v(1949, 1319.8) * mm, "end": v(1949.37, 1320) * mm});
            skLineSegment(sketch, "E3813", {"start": v(1949.37, 1320) * mm, "end": v(1949.74, 1320.2) * mm});
            skLineSegment(sketch, "E3814", {"start": v(1949.74, 1320.2) * mm, "end": v(1950.13, 1320.37) * mm});
            skLineSegment(sketch, "E3815", {"start": v(1950.13, 1320.37) * mm, "end": v(1950.52, 1320.52) * mm});
            skLineSegment(sketch, "E3816", {"start": v(1950.52, 1320.52) * mm, "end": v(1950.93, 1320.66) * mm});
            skLineSegment(sketch, "E3817", {"start": v(1950.93, 1320.66) * mm, "end": v(1951.33, 1320.77) * mm});
            skLineSegment(sketch, "E3818", {"start": v(1951.33, 1320.77) * mm, "end": v(1951.75, 1320.86) * mm});
            skLineSegment(sketch, "E3819", {"start": v(1951.75, 1320.86) * mm, "end": v(1952.16, 1320.94) * mm});
            skLineSegment(sketch, "E3820", {"start": v(1952.16, 1320.94) * mm, "end": v(1952.59, 1320.99) * mm});
            skLineSegment(sketch, "E3821", {"start": v(1952.59, 1320.99) * mm, "end": v(1953.01, 1321.02) * mm});
            skLineSegment(sketch, "E3822", {"start": v(1953.01, 1321.02) * mm, "end": v(1953.44, 1321.03) * mm});
            skLineSegment(sketch, "E3823", {"start": v(1953.44, 1321.03) * mm, "end": v(1953.88, 1321.03) * mm});
            skLineSegment(sketch, "E3824", {"start": v(1953.88, 1321.03) * mm, "end": v(1954.32, 1321.01) * mm});
            skLineSegment(sketch, "E3825", {"start": v(1954.32, 1321.01) * mm, "end": v(1954.75, 1320.97) * mm});
            skLineSegment(sketch, "E3826", {"start": v(1954.75, 1320.97) * mm, "end": v(1955.18, 1320.9) * mm});
            skLineSegment(sketch, "E3827", {"start": v(1955.18, 1320.9) * mm, "end": v(1955.6, 1320.82) * mm});
            skLineSegment(sketch, "E3828", {"start": v(1955.6, 1320.82) * mm, "end": v(1956.02, 1320.71) * mm});
            skLineSegment(sketch, "E3829", {"start": v(1956.02, 1320.71) * mm, "end": v(1956.44, 1320.59) * mm});
            skLineSegment(sketch, "E3830", {"start": v(1956.44, 1320.59) * mm, "end": v(1956.84, 1320.44) * mm});
            skLineSegment(sketch, "E3831", {"start": v(1956.84, 1320.44) * mm, "end": v(1957.24, 1320.27) * mm});
            skLineSegment(sketch, "E3832", {"start": v(1957.24, 1320.27) * mm, "end": v(1957.63, 1320.08) * mm});
            skLineSegment(sketch, "E3833", {"start": v(1957.63, 1320.08) * mm, "end": v(1958.01, 1319.87) * mm});
            skLineSegment(sketch, "E3834", {"start": v(1958.01, 1319.87) * mm, "end": v(1958.38, 1319.64) * mm});
            skLineSegment(sketch, "E3835", {"start": v(1958.38, 1319.64) * mm, "end": v(1958.74, 1319.4) * mm});
            skLineSegment(sketch, "E3836", {"start": v(1958.74, 1319.4) * mm, "end": v(1959.08, 1319.13) * mm});
            skLineSegment(sketch, "E3837", {"start": v(1959.08, 1319.13) * mm, "end": v(1959.42, 1318.85) * mm});
            skLineSegment(sketch, "E3838", {"start": v(1959.42, 1318.85) * mm, "end": v(1959.74, 1318.55) * mm});
            skLineSegment(sketch, "E3839", {"start": v(1959.74, 1318.55) * mm, "end": v(1960.04, 1318.23) * mm});
            skLineSegment(sketch, "E3840", {"start": v(1960.04, 1318.23) * mm, "end": v(1960.32, 1317.9) * mm});
            skLineSegment(sketch, "E3841", {"start": v(1960.32, 1317.9) * mm, "end": v(1960.59, 1317.56) * mm});
            skLineSegment(sketch, "E3842", {"start": v(1960.59, 1317.56) * mm, "end": v(1960.83, 1317.2) * mm});
            skLineSegment(sketch, "E3843", {"start": v(1960.83, 1317.2) * mm, "end": v(1961.06, 1316.84) * mm});
            skLineSegment(sketch, "E3844", {"start": v(1961.06, 1316.84) * mm, "end": v(1961.27, 1316.47) * mm});
            skLineSegment(sketch, "E3845", {"start": v(1961.27, 1316.47) * mm, "end": v(1961.46, 1316.08) * mm});
            skLineSegment(sketch, "E3846", {"start": v(1961.46, 1316.08) * mm, "end": v(1961.64, 1315.69) * mm});
            skLineSegment(sketch, "E3847", {"start": v(1961.64, 1315.69) * mm, "end": v(1961.79, 1315.29) * mm});
            skLineSegment(sketch, "E3848", {"start": v(1961.79, 1315.29) * mm, "end": v(1961.92, 1314.88) * mm});
            skLineSegment(sketch, "E3849", {"start": v(1961.92, 1314.88) * mm, "end": v(1962.03, 1314.46) * mm});
            skLineSegment(sketch, "E3850", {"start": v(1962.03, 1314.46) * mm, "end": v(1962.12, 1314.04) * mm});
            skLineSegment(sketch, "E3851", {"start": v(1962.12, 1314.04) * mm, "end": v(1962.2, 1313.62) * mm});
            skLineSegment(sketch, "E3852", {"start": v(1962.2, 1313.62) * mm, "end": v(1962.24, 1313.18) * mm});
            skLineSegment(sketch, "E3853", {"start": v(1962.24, 1313.18) * mm, "end": v(1962.27, 1312.75) * mm});
            skLineSegment(sketch, "E3854", {"start": v(1962.27, 1312.75) * mm, "end": v(1962.27, 1312.32) * mm});
            skLineSegment(sketch, "E3855", {"start": v(1962.27, 1312.32) * mm, "end": v(1962.27, 1296.95) * mm});
            skLineSegment(sketch, "E3856", {"start": v(1962.27, 1312.32) * mm, "end": v(1962.27, 1312.67) * mm});
            skLineSegment(sketch, "E3857", {"start": v(1962.27, 1312.67) * mm, "end": v(1962.3, 1313.03) * mm});
            skLineSegment(sketch, "E3858", {"start": v(1962.3, 1313.03) * mm, "end": v(1962.33, 1313.38) * mm});
            skLineSegment(sketch, "E3859", {"start": v(1962.33, 1313.38) * mm, "end": v(1962.39, 1313.74) * mm});
            skLineSegment(sketch, "E3860", {"start": v(1962.39, 1313.74) * mm, "end": v(1962.46, 1314.08) * mm});
            skLineSegment(sketch, "E3861", {"start": v(1962.46, 1314.08) * mm, "end": v(1962.55, 1314.42) * mm});
            skLineSegment(sketch, "E3862", {"start": v(1962.55, 1314.42) * mm, "end": v(1962.66, 1314.76) * mm});
            skLineSegment(sketch, "E3863", {"start": v(1962.66, 1314.76) * mm, "end": v(1962.79, 1315.1) * mm});
            skLineSegment(sketch, "E3864", {"start": v(1962.79, 1315.1) * mm, "end": v(1962.93, 1315.41) * mm});
            skLineSegment(sketch, "E3865", {"start": v(1962.93, 1315.41) * mm, "end": v(1963.08, 1315.73) * mm});
            skLineSegment(sketch, "E3866", {"start": v(1963.08, 1315.73) * mm, "end": v(1963.26, 1316.04) * mm});
            skLineSegment(sketch, "E3867", {"start": v(1963.26, 1316.04) * mm, "end": v(1963.45, 1316.34) * mm});
            skLineSegment(sketch, "E3868", {"start": v(1963.45, 1316.34) * mm, "end": v(1963.65, 1316.63) * mm});
            skLineSegment(sketch, "E3869", {"start": v(1963.65, 1316.63) * mm, "end": v(1963.87, 1316.9) * mm});
            skLineSegment(sketch, "E3870", {"start": v(1963.87, 1316.9) * mm, "end": v(1964.1, 1317.18) * mm});
            skLineSegment(sketch, "E3871", {"start": v(1964.1, 1317.18) * mm, "end": v(1964.36, 1317.44) * mm});
            skLineSegment(sketch, "E3872", {"start": v(1964.36, 1317.44) * mm, "end": v(1964.8, 1317.73) * mm});
            skLineSegment(sketch, "E3873", {"start": v(1964.8, 1317.73) * mm, "end": v(1965.24, 1318.01) * mm});
            skLineSegment(sketch, "E3874", {"start": v(1965.24, 1318.01) * mm, "end": v(1965.7, 1318.27) * mm});
            skLineSegment(sketch, "E3875", {"start": v(1965.7, 1318.27) * mm, "end": v(1966.17, 1318.5) * mm});
            skLineSegment(sketch, "E3876", {"start": v(1966.17, 1318.5) * mm, "end": v(1966.65, 1318.72) * mm});
            skLineSegment(sketch, "E3877", {"start": v(1966.65, 1318.72) * mm, "end": v(1967.14, 1318.9) * mm});
            skLineSegment(sketch, "E3878", {"start": v(1967.14, 1318.9) * mm, "end": v(1967.64, 1319.08) * mm});
            skLineSegment(sketch, "E3879", {"start": v(1967.64, 1319.08) * mm, "end": v(1968.14, 1319.23) * mm});
            skLineSegment(sketch, "E3880", {"start": v(1968.14, 1319.23) * mm, "end": v(1968.65, 1319.35) * mm});
            skLineSegment(sketch, "E3881", {"start": v(1968.65, 1319.35) * mm, "end": v(1969.16, 1319.46) * mm});
            skLineSegment(sketch, "E3882", {"start": v(1969.16, 1319.46) * mm, "end": v(1969.68, 1319.54) * mm});
            skLineSegment(sketch, "E3883", {"start": v(1969.68, 1319.54) * mm, "end": v(1970.2, 1319.6) * mm});
            skLineSegment(sketch, "E3884", {"start": v(1970.2, 1319.6) * mm, "end": v(1970.72, 1319.63) * mm});
            skLineSegment(sketch, "E3885", {"start": v(1970.72, 1319.63) * mm, "end": v(1971.25, 1319.64) * mm});
            skLineSegment(sketch, "E3886", {"start": v(1971.25, 1319.64) * mm, "end": v(1971.78, 1319.63) * mm});
            skLineSegment(sketch, "E3887", {"start": v(1971.78, 1319.63) * mm, "end": v(1972.3, 1319.59) * mm});
            skLineSegment(sketch, "E3888", {"start": v(1972.3, 1319.59) * mm, "end": v(1972.78, 1319.58) * mm});
            skLineSegment(sketch, "E3889", {"start": v(1972.78, 1319.58) * mm, "end": v(1973.25, 1319.58) * mm});
            skLineSegment(sketch, "E3890", {"start": v(1973.25, 1319.58) * mm, "end": v(1973.72, 1319.6) * mm});
            skLineSegment(sketch, "E3891", {"start": v(1973.72, 1319.6) * mm, "end": v(1974.19, 1319.61) * mm});
            skLineSegment(sketch, "E3892", {"start": v(1974.19, 1319.61) * mm, "end": v(1974.66, 1319.64) * mm});
            skLineSegment(sketch, "E3893", {"start": v(1974.66, 1319.64) * mm, "end": v(1975.13, 1319.67) * mm});
            skLineSegment(sketch, "E3894", {"start": v(1975.13, 1319.67) * mm, "end": v(1975.6, 1319.72) * mm});
            skLineSegment(sketch, "E3895", {"start": v(1975.6, 1319.72) * mm, "end": v(1976.07, 1319.77) * mm});
            skLineSegment(sketch, "E3896", {"start": v(1976.07, 1319.77) * mm, "end": v(1976.53, 1319.83) * mm});
            skLineSegment(sketch, "E3897", {"start": v(1976.53, 1319.83) * mm, "end": v(1977, 1319.9) * mm});
            skLineSegment(sketch, "E3898", {"start": v(1977, 1319.9) * mm, "end": v(1977.47, 1319.98) * mm});
            skLineSegment(sketch, "E3899", {"start": v(1977.47, 1319.98) * mm, "end": v(1977.93, 1320.06) * mm});
            skLineSegment(sketch, "E3900", {"start": v(1977.93, 1320.06) * mm, "end": v(1978.39, 1320.16) * mm});
            skLineSegment(sketch, "E3901", {"start": v(1978.39, 1320.16) * mm, "end": v(1978.85, 1320.26) * mm});
            skLineSegment(sketch, "E3902", {"start": v(1978.85, 1320.26) * mm, "end": v(1979.3, 1320.37) * mm});
            skLineSegment(sketch, "E3903", {"start": v(1979.3, 1320.37) * mm, "end": v(1979.76, 1320.5) * mm});
            skLineSegment(sketch, "E3904", {"start": v(2263.2, 616.84) * mm, "end": v(2223.21, 616.84) * mm});
            skLineSegment(sketch, "E3905", {"start": v(2223.21, 616.84) * mm, "end": v(2223.21, 641.7) * mm});
            skLineSegment(sketch, "E3906", {"start": v(2242.32, 616.84) * mm, "end": v(2242.32, 639.91) * mm});
            skLineSegment(sketch, "E3907", {"start": v(2263.19, 703.14) * mm, "end": v(2223.21, 725.6) * mm});
            skLineSegment(sketch, "E3908", {"start": v(2263.18, 760.72) * mm, "end": v(2263.18, 734.4) * mm});
            skLineSegment(sketch, "E3909", {"start": v(2263.18, 734.4) * mm, "end": v(2223.23, 734.4) * mm});
            skLineSegment(sketch, "E3910", {"start": v(2223.23, 734.4) * mm, "end": v(2223.23, 760.72) * mm});
            skLineSegment(sketch, "E3911", {"start": v(2242.48, 734.4) * mm, "end": v(2242.48, 757.42) * mm});
            skArc(sketch, "E3912", {"start": v(1983.8, 1901.22) * mm, "mid": v(1984.67, 1899.1) * mm, "end": v(1986.8, 1898.22) * mm});
            skArc(sketch, "E3913", {"start": v(1986.8, 1898.22) * mm, "mid": v(1988.92, 1899.1) * mm, "end": v(1989.8, 1901.22) * mm});
            skArc(sketch, "E3914", {"start": v(1989.8, 1901.22) * mm, "mid": v(1988.92, 1903.34) * mm, "end": v(1986.8, 1904.22) * mm});
            skArc(sketch, "E3915", {"start": v(1986.8, 1904.22) * mm, "mid": v(1984.67, 1903.34) * mm, "end": v(1983.8, 1901.22) * mm});
            skArc(sketch, "E3916", {"start": v(1929.7, 1901.22) * mm, "mid": v(1930.58, 1899.1) * mm, "end": v(1932.7, 1898.22) * mm});
            skArc(sketch, "E3917", {"start": v(1932.7, 1898.22) * mm, "mid": v(1934.83, 1899.1) * mm, "end": v(1935.7, 1901.22) * mm});
            skArc(sketch, "E3918", {"start": v(1935.7, 1901.22) * mm, "mid": v(1934.83, 1903.34) * mm, "end": v(1932.7, 1904.22) * mm});
            skArc(sketch, "E3919", {"start": v(1932.7, 1904.22) * mm, "mid": v(1930.58, 1903.34) * mm, "end": v(1929.7, 1901.22) * mm});
            skArc(sketch, "E3920", {"start": v(1983.8, 1681.22) * mm, "mid": v(1984.67, 1679.1) * mm, "end": v(1986.8, 1678.22) * mm});
            skArc(sketch, "E3921", {"start": v(1986.8, 1678.22) * mm, "mid": v(1988.92, 1679.1) * mm, "end": v(1989.8, 1681.22) * mm});
            skArc(sketch, "E3922", {"start": v(1989.8, 1681.22) * mm, "mid": v(1988.92, 1683.34) * mm, "end": v(1986.8, 1684.22) * mm});
            skArc(sketch, "E3923", {"start": v(1986.8, 1684.22) * mm, "mid": v(1984.67, 1683.34) * mm, "end": v(1983.8, 1681.22) * mm});
            skArc(sketch, "E3924", {"start": v(1929.7, 1681.22) * mm, "mid": v(1930.58, 1679.1) * mm, "end": v(1932.7, 1678.22) * mm});
            skArc(sketch, "E3925", {"start": v(1932.7, 1678.22) * mm, "mid": v(1934.83, 1679.1) * mm, "end": v(1935.7, 1681.22) * mm});
            skArc(sketch, "E3926", {"start": v(1935.7, 1681.22) * mm, "mid": v(1934.83, 1683.34) * mm, "end": v(1932.7, 1684.22) * mm});
            skArc(sketch, "E3927", {"start": v(1932.7, 1684.22) * mm, "mid": v(1930.58, 1683.34) * mm, "end": v(1929.7, 1681.22) * mm});
            skArc(sketch, "E3928", {"start": v(1983.8, 1531.22) * mm, "mid": v(1984.67, 1529.1) * mm, "end": v(1986.8, 1528.22) * mm});
            skArc(sketch, "E3929", {"start": v(1986.8, 1528.22) * mm, "mid": v(1988.92, 1529.1) * mm, "end": v(1989.8, 1531.22) * mm});
            skArc(sketch, "E3930", {"start": v(1989.8, 1531.22) * mm, "mid": v(1988.92, 1533.34) * mm, "end": v(1986.8, 1534.22) * mm});
            skArc(sketch, "E3931", {"start": v(1986.8, 1534.22) * mm, "mid": v(1984.67, 1533.34) * mm, "end": v(1983.8, 1531.22) * mm});
            skArc(sketch, "E3932", {"start": v(1929.7, 1531.22) * mm, "mid": v(1930.58, 1529.1) * mm, "end": v(1932.7, 1528.22) * mm});
            skArc(sketch, "E3933", {"start": v(1932.7, 1528.22) * mm, "mid": v(1934.83, 1529.1) * mm, "end": v(1935.7, 1531.22) * mm});
            skArc(sketch, "E3934", {"start": v(1935.7, 1531.22) * mm, "mid": v(1934.83, 1533.34) * mm, "end": v(1932.7, 1534.22) * mm});
            skArc(sketch, "E3935", {"start": v(1932.7, 1534.22) * mm, "mid": v(1930.58, 1533.34) * mm, "end": v(1929.7, 1531.22) * mm});
            skArc(sketch, "E3936", {"start": v(1983.8, 1381.22) * mm, "mid": v(1984.67, 1379.1) * mm, "end": v(1986.8, 1378.22) * mm});
            skArc(sketch, "E3937", {"start": v(1986.8, 1378.22) * mm, "mid": v(1988.92, 1379.1) * mm, "end": v(1989.8, 1381.22) * mm});
            skArc(sketch, "E3938", {"start": v(1989.8, 1381.22) * mm, "mid": v(1988.92, 1383.34) * mm, "end": v(1986.8, 1384.22) * mm});
            skArc(sketch, "E3939", {"start": v(1986.8, 1384.22) * mm, "mid": v(1984.67, 1383.34) * mm, "end": v(1983.8, 1381.22) * mm});
            skArc(sketch, "E3940", {"start": v(1929.7, 1381.22) * mm, "mid": v(1930.58, 1379.1) * mm, "end": v(1932.7, 1378.22) * mm});
            skArc(sketch, "E3941", {"start": v(1932.7, 1378.22) * mm, "mid": v(1934.83, 1379.1) * mm, "end": v(1935.7, 1381.22) * mm});
            skArc(sketch, "E3942", {"start": v(1935.7, 1381.22) * mm, "mid": v(1934.83, 1383.34) * mm, "end": v(1932.7, 1384.22) * mm});
            skArc(sketch, "E3943", {"start": v(1932.7, 1384.22) * mm, "mid": v(1930.58, 1383.34) * mm, "end": v(1929.7, 1381.22) * mm});
            skArc(sketch, "E3944", {"start": v(1983.8, 1231.22) * mm, "mid": v(1984.67, 1229.1) * mm, "end": v(1986.8, 1228.22) * mm});
            skArc(sketch, "E3945", {"start": v(1986.8, 1228.22) * mm, "mid": v(1988.92, 1229.1) * mm, "end": v(1989.8, 1231.22) * mm});
            skArc(sketch, "E3946", {"start": v(1989.8, 1231.22) * mm, "mid": v(1988.92, 1233.34) * mm, "end": v(1986.8, 1234.22) * mm});
            skArc(sketch, "E3947", {"start": v(1986.8, 1234.22) * mm, "mid": v(1984.67, 1233.34) * mm, "end": v(1983.8, 1231.22) * mm});
            skArc(sketch, "E3948", {"start": v(1929.7, 1231.22) * mm, "mid": v(1930.58, 1229.1) * mm, "end": v(1932.7, 1228.22) * mm});
            skArc(sketch, "E3949", {"start": v(1932.7, 1228.22) * mm, "mid": v(1934.83, 1229.1) * mm, "end": v(1935.7, 1231.22) * mm});
            skArc(sketch, "E3950", {"start": v(1935.7, 1231.22) * mm, "mid": v(1934.83, 1233.34) * mm, "end": v(1932.7, 1234.22) * mm});
            skArc(sketch, "E3951", {"start": v(1932.7, 1234.22) * mm, "mid": v(1930.58, 1233.34) * mm, "end": v(1929.7, 1231.22) * mm});
            skArc(sketch, "E3952", {"start": v(1983.8, 1111.22) * mm, "mid": v(1984.67, 1109.1) * mm, "end": v(1986.8, 1108.22) * mm});
            skArc(sketch, "E3953", {"start": v(1986.8, 1108.22) * mm, "mid": v(1988.92, 1109.1) * mm, "end": v(1989.8, 1111.22) * mm});
            skArc(sketch, "E3954", {"start": v(1989.8, 1111.22) * mm, "mid": v(1988.92, 1113.34) * mm, "end": v(1986.8, 1114.22) * mm});
            skArc(sketch, "E3955", {"start": v(1986.8, 1114.22) * mm, "mid": v(1984.67, 1113.34) * mm, "end": v(1983.8, 1111.22) * mm});
            skArc(sketch, "E3956", {"start": v(1929.7, 1111.22) * mm, "mid": v(1930.58, 1109.1) * mm, "end": v(1932.7, 1108.22) * mm});
            skArc(sketch, "E3957", {"start": v(1932.7, 1108.22) * mm, "mid": v(1934.83, 1109.1) * mm, "end": v(1935.7, 1111.22) * mm});
            skArc(sketch, "E3958", {"start": v(1935.7, 1111.22) * mm, "mid": v(1934.83, 1113.34) * mm, "end": v(1932.7, 1114.22) * mm});
            skArc(sketch, "E3959", {"start": v(1932.7, 1114.22) * mm, "mid": v(1930.58, 1113.34) * mm, "end": v(1929.7, 1111.22) * mm});
            skArc(sketch, "E3960", {"start": v(1983.8, 931.22) * mm, "mid": v(1984.67, 929.1) * mm, "end": v(1986.8, 928.22) * mm});
            skArc(sketch, "E3961", {"start": v(1986.8, 928.22) * mm, "mid": v(1988.92, 929.1) * mm, "end": v(1989.8, 931.22) * mm});
            skArc(sketch, "E3962", {"start": v(1989.8, 931.22) * mm, "mid": v(1988.92, 933.34) * mm, "end": v(1986.8, 934.22) * mm});
            skArc(sketch, "E3963", {"start": v(1986.8, 934.22) * mm, "mid": v(1984.67, 933.34) * mm, "end": v(1983.8, 931.22) * mm});
            skArc(sketch, "E3964", {"start": v(1929.7, 931.22) * mm, "mid": v(1930.58, 929.1) * mm, "end": v(1932.7, 928.22) * mm});
            skArc(sketch, "E3965", {"start": v(1932.7, 928.22) * mm, "mid": v(1934.83, 929.1) * mm, "end": v(1935.7, 931.22) * mm});
            skArc(sketch, "E3966", {"start": v(1935.7, 931.22) * mm, "mid": v(1934.83, 933.34) * mm, "end": v(1932.7, 934.22) * mm});
            skArc(sketch, "E3967", {"start": v(1932.7, 934.22) * mm, "mid": v(1930.58, 933.34) * mm, "end": v(1929.7, 931.22) * mm});
            skArc(sketch, "E3968", {"start": v(1983.8, 781.22) * mm, "mid": v(1984.67, 779.1) * mm, "end": v(1986.8, 778.22) * mm});
            skArc(sketch, "E3969", {"start": v(1986.8, 778.22) * mm, "mid": v(1988.92, 779.1) * mm, "end": v(1989.8, 781.22) * mm});
            skArc(sketch, "E3970", {"start": v(1989.8, 781.22) * mm, "mid": v(1988.92, 783.34) * mm, "end": v(1986.8, 784.22) * mm});
            skArc(sketch, "E3971", {"start": v(1986.8, 784.22) * mm, "mid": v(1984.67, 783.34) * mm, "end": v(1983.8, 781.22) * mm});
            skArc(sketch, "E3972", {"start": v(1929.7, 781.22) * mm, "mid": v(1930.58, 779.1) * mm, "end": v(1932.7, 778.22) * mm});
            skArc(sketch, "E3973", {"start": v(1932.7, 778.22) * mm, "mid": v(1934.83, 779.1) * mm, "end": v(1935.7, 781.22) * mm});
            skArc(sketch, "E3974", {"start": v(1935.7, 781.22) * mm, "mid": v(1934.83, 783.34) * mm, "end": v(1932.7, 784.22) * mm});
            skArc(sketch, "E3975", {"start": v(1932.7, 784.22) * mm, "mid": v(1930.58, 783.34) * mm, "end": v(1929.7, 781.22) * mm});
            skArc(sketch, "E3976", {"start": v(1983.8, 631.22) * mm, "mid": v(1984.67, 629.1) * mm, "end": v(1986.8, 628.22) * mm});
            skArc(sketch, "E3977", {"start": v(1986.8, 628.22) * mm, "mid": v(1988.92, 629.1) * mm, "end": v(1989.8, 631.22) * mm});
            skArc(sketch, "E3978", {"start": v(1989.8, 631.22) * mm, "mid": v(1988.92, 633.34) * mm, "end": v(1986.8, 634.22) * mm});
            skArc(sketch, "E3979", {"start": v(1986.8, 634.22) * mm, "mid": v(1984.67, 633.34) * mm, "end": v(1983.8, 631.22) * mm});
            skArc(sketch, "E3980", {"start": v(1929.7, 631.22) * mm, "mid": v(1930.58, 629.1) * mm, "end": v(1932.7, 628.22) * mm});
            skArc(sketch, "E3981", {"start": v(1932.7, 628.22) * mm, "mid": v(1934.83, 629.1) * mm, "end": v(1935.7, 631.22) * mm});
            skArc(sketch, "E3982", {"start": v(1935.7, 631.22) * mm, "mid": v(1934.83, 633.34) * mm, "end": v(1932.7, 634.22) * mm});
            skArc(sketch, "E3983", {"start": v(1932.7, 634.22) * mm, "mid": v(1930.58, 633.34) * mm, "end": v(1929.7, 631.22) * mm});
            skArc(sketch, "E3984", {"start": v(1983.8, 481.22) * mm, "mid": v(1984.67, 479.1) * mm, "end": v(1986.8, 478.22) * mm});
            skArc(sketch, "E3985", {"start": v(1986.8, 478.22) * mm, "mid": v(1988.92, 479.1) * mm, "end": v(1989.8, 481.22) * mm});
            skArc(sketch, "E3986", {"start": v(1989.8, 481.22) * mm, "mid": v(1988.92, 483.34) * mm, "end": v(1986.8, 484.22) * mm});
            skArc(sketch, "E3987", {"start": v(1986.8, 484.22) * mm, "mid": v(1984.67, 483.34) * mm, "end": v(1983.8, 481.22) * mm});
            skArc(sketch, "E3988", {"start": v(1929.7, 481.22) * mm, "mid": v(1930.58, 479.1) * mm, "end": v(1932.7, 478.22) * mm});
            skArc(sketch, "E3989", {"start": v(1932.7, 478.22) * mm, "mid": v(1934.83, 479.1) * mm, "end": v(1935.7, 481.22) * mm});
            skArc(sketch, "E3990", {"start": v(1935.7, 481.22) * mm, "mid": v(1934.83, 483.34) * mm, "end": v(1932.7, 484.22) * mm});
            skArc(sketch, "E3991", {"start": v(1932.7, 484.22) * mm, "mid": v(1930.58, 483.34) * mm, "end": v(1929.7, 481.22) * mm});
            skArc(sketch, "E3992", {"start": v(1983.8, 1051.22) * mm, "mid": v(1984.67, 1049.1) * mm, "end": v(1986.8, 1048.22) * mm});
            skArc(sketch, "E3993", {"start": v(1986.8, 1048.22) * mm, "mid": v(1988.92, 1049.1) * mm, "end": v(1989.8, 1051.22) * mm});
            skArc(sketch, "E3994", {"start": v(1989.8, 1051.22) * mm, "mid": v(1988.92, 1053.34) * mm, "end": v(1986.8, 1054.22) * mm});
            skArc(sketch, "E3995", {"start": v(1986.8, 1054.22) * mm, "mid": v(1984.67, 1053.34) * mm, "end": v(1983.8, 1051.22) * mm});
            skArc(sketch, "E3996", {"start": v(1929.7, 1051.22) * mm, "mid": v(1930.58, 1049.1) * mm, "end": v(1932.7, 1048.22) * mm});
            skArc(sketch, "E3997", {"start": v(1932.7, 1048.22) * mm, "mid": v(1934.83, 1049.1) * mm, "end": v(1935.7, 1051.22) * mm});
            skArc(sketch, "E3998", {"start": v(1935.7, 1051.22) * mm, "mid": v(1934.83, 1053.34) * mm, "end": v(1932.7, 1054.22) * mm});
            skArc(sketch, "E3999", {"start": v(1932.7, 1054.22) * mm, "mid": v(1930.58, 1053.34) * mm, "end": v(1929.7, 1051.22) * mm});
            skArc(sketch, "E4000", {"start": v(1983.8, 1790.87) * mm, "mid": v(1984.67, 1788.75) * mm, "end": v(1986.8, 1787.87) * mm});
            skArc(sketch, "E4001", {"start": v(1986.8, 1787.87) * mm, "mid": v(1988.92, 1788.75) * mm, "end": v(1989.8, 1790.87) * mm});
            skArc(sketch, "E4002", {"start": v(1989.8, 1790.87) * mm, "mid": v(1988.92, 1793) * mm, "end": v(1986.8, 1793.87) * mm});
            skArc(sketch, "E4003", {"start": v(1986.8, 1793.87) * mm, "mid": v(1984.67, 1793) * mm, "end": v(1983.8, 1790.87) * mm});
            skArc(sketch, "E4004", {"start": v(1929.7, 1790.87) * mm, "mid": v(1930.58, 1788.75) * mm, "end": v(1932.7, 1787.87) * mm});
            skArc(sketch, "E4005", {"start": v(1932.7, 1787.87) * mm, "mid": v(1934.83, 1788.75) * mm, "end": v(1935.7, 1790.87) * mm});
            skArc(sketch, "E4006", {"start": v(1935.7, 1790.87) * mm, "mid": v(1934.83, 1793) * mm, "end": v(1932.7, 1793.87) * mm});
            skArc(sketch, "E4007", {"start": v(1932.7, 1793.87) * mm, "mid": v(1930.58, 1793) * mm, "end": v(1929.7, 1790.87) * mm});
            skArc(sketch, "E4008", {"start": v(1983.8, 364.11) * mm, "mid": v(1984.67, 362) * mm, "end": v(1986.8, 361.11) * mm});
            skArc(sketch, "E4009", {"start": v(1986.8, 361.11) * mm, "mid": v(1988.92, 362) * mm, "end": v(1989.8, 364.11) * mm});
            skArc(sketch, "E4010", {"start": v(1989.8, 364.11) * mm, "mid": v(1988.92, 366.24) * mm, "end": v(1986.8, 367.11) * mm});
            skArc(sketch, "E4011", {"start": v(1986.8, 367.11) * mm, "mid": v(1984.67, 366.24) * mm, "end": v(1983.8, 364.11) * mm});
            skArc(sketch, "E4012", {"start": v(1929.7, 364.11) * mm, "mid": v(1930.58, 362) * mm, "end": v(1932.7, 361.11) * mm});
            skArc(sketch, "E4013", {"start": v(1932.7, 361.11) * mm, "mid": v(1934.83, 362) * mm, "end": v(1935.7, 364.11) * mm});
            skArc(sketch, "E4014", {"start": v(1935.7, 364.11) * mm, "mid": v(1934.83, 366.24) * mm, "end": v(1932.7, 367.11) * mm});
            skArc(sketch, "E4015", {"start": v(1932.7, 367.11) * mm, "mid": v(1930.58, 366.24) * mm, "end": v(1929.7, 364.11) * mm});
            skArc(sketch, "E4016", {"start": v(1538.45, 23) * mm, "mid": v(1536.33, 22.12) * mm, "end": v(1535.45, 20) * mm});
            skArc(sketch, "E4017", {"start": v(1535.45, 20) * mm, "mid": v(1536.33, 17.88) * mm, "end": v(1538.45, 17) * mm});
            skArc(sketch, "E4018", {"start": v(1538.45, 17) * mm, "mid": v(1540.57, 17.88) * mm, "end": v(1541.45, 20) * mm});
            skArc(sketch, "E4019", {"start": v(1541.45, 20) * mm, "mid": v(1540.57, 22.12) * mm, "end": v(1538.45, 23) * mm});
            skArc(sketch, "E4020", {"start": v(2069.54, 27.78) * mm, "mid": v(2067.42, 26.9) * mm, "end": v(2066.54, 24.78) * mm});
            skArc(sketch, "E4021", {"start": v(2066.54, 24.78) * mm, "mid": v(2067.42, 22.66) * mm, "end": v(2069.54, 21.78) * mm});
            skArc(sketch, "E4022", {"start": v(2069.54, 21.78) * mm, "mid": v(2071.66, 22.66) * mm, "end": v(2072.54, 24.78) * mm});
            skArc(sketch, "E4023", {"start": v(2072.54, 24.78) * mm, "mid": v(2071.66, 26.9) * mm, "end": v(2069.54, 27.78) * mm});
            skArc(sketch, "E4024", {"start": v(2696.38, 31.62) * mm, "mid": v(2694.25, 30.75) * mm, "end": v(2693.38, 28.62) * mm});
            skArc(sketch, "E4025", {"start": v(2693.38, 28.62) * mm, "mid": v(2694.25, 26.5) * mm, "end": v(2696.38, 25.62) * mm});
            skArc(sketch, "E4026", {"start": v(2696.38, 25.62) * mm, "mid": v(2698.5, 26.5) * mm, "end": v(2699.38, 28.62) * mm});
            skArc(sketch, "E4027", {"start": v(2699.38, 28.62) * mm, "mid": v(2698.5, 30.75) * mm, "end": v(2696.38, 31.62) * mm});
            skArc(sketch, "E4028", {"start": v(2696.38, 712.3) * mm, "mid": v(2694.25, 711.42) * mm, "end": v(2693.38, 709.3) * mm});
            skArc(sketch, "E4029", {"start": v(2693.38, 709.3) * mm, "mid": v(2694.25, 707.18) * mm, "end": v(2696.38, 706.3) * mm});
            skArc(sketch, "E4030", {"start": v(2696.38, 706.3) * mm, "mid": v(2698.5, 707.18) * mm, "end": v(2699.38, 709.3) * mm});
            skArc(sketch, "E4031", {"start": v(2699.38, 709.3) * mm, "mid": v(2698.5, 711.42) * mm, "end": v(2696.38, 712.3) * mm});
            skArc(sketch, "E4032", {"start": v(2352.2, 696.91) * mm, "mid": v(2350.07, 696.04) * mm, "end": v(2349.2, 693.91) * mm});
            skArc(sketch, "E4033", {"start": v(2349.2, 693.91) * mm, "mid": v(2350.07, 691.8) * mm, "end": v(2352.2, 690.91) * mm});
            skArc(sketch, "E4034", {"start": v(2352.2, 690.91) * mm, "mid": v(2354.31, 691.8) * mm, "end": v(2355.2, 693.91) * mm});
            skArc(sketch, "E4035", {"start": v(2355.2, 693.91) * mm, "mid": v(2354.31, 696.04) * mm, "end": v(2352.2, 696.91) * mm});
            skArc(sketch, "E4036", {"start": v(2090.7, 587.31) * mm, "mid": v(2088.57, 586.44) * mm, "end": v(2087.7, 584.31) * mm});
            skArc(sketch, "E4037", {"start": v(2087.7, 584.31) * mm, "mid": v(2088.57, 582.2) * mm, "end": v(2090.7, 581.31) * mm});
            skArc(sketch, "E4038", {"start": v(2090.7, 581.31) * mm, "mid": v(2092.81, 582.2) * mm, "end": v(2093.7, 584.31) * mm});
            skArc(sketch, "E4039", {"start": v(2093.7, 584.31) * mm, "mid": v(2092.81, 586.44) * mm, "end": v(2090.7, 587.31) * mm});
            skArc(sketch, "E4040", {"start": v(1627.3, 681.53) * mm, "mid": v(1625.17, 680.65) * mm, "end": v(1624.3, 678.53) * mm});
            skArc(sketch, "E4041", {"start": v(1624.3, 678.53) * mm, "mid": v(1625.17, 676.41) * mm, "end": v(1627.3, 675.53) * mm});
            skArc(sketch, "E4042", {"start": v(1627.3, 675.53) * mm, "mid": v(1629.42, 676.41) * mm, "end": v(1630.3, 678.53) * mm});
            skArc(sketch, "E4043", {"start": v(1630.3, 678.53) * mm, "mid": v(1629.42, 680.65) * mm, "end": v(1627.3, 681.53) * mm});
            skArc(sketch, "E4044", {"start": v(1538.85, 1396.82) * mm, "mid": v(1536.72, 1395.94) * mm, "end": v(1535.85, 1393.82) * mm});
            skArc(sketch, "E4045", {"start": v(1535.85, 1393.82) * mm, "mid": v(1536.72, 1391.7) * mm, "end": v(1538.85, 1390.82) * mm});
            skArc(sketch, "E4046", {"start": v(1538.85, 1390.82) * mm, "mid": v(1540.97, 1391.7) * mm, "end": v(1541.85, 1393.82) * mm});
            skArc(sketch, "E4047", {"start": v(1541.85, 1393.82) * mm, "mid": v(1540.97, 1395.94) * mm, "end": v(1538.85, 1396.82) * mm});
            skArc(sketch, "E4048", {"start": v(2098.38, 1143) * mm, "mid": v(2096.26, 1142.13) * mm, "end": v(2095.38, 1140) * mm});
            skArc(sketch, "E4049", {"start": v(2095.38, 1140) * mm, "mid": v(2096.26, 1137.88) * mm, "end": v(2098.38, 1137) * mm});
            skArc(sketch, "E4050", {"start": v(2098.38, 1137) * mm, "mid": v(2100.5, 1137.88) * mm, "end": v(2101.38, 1140) * mm});
            skArc(sketch, "E4051", {"start": v(2101.38, 1140) * mm, "mid": v(2100.5, 1142.13) * mm, "end": v(2098.38, 1143) * mm});
            skArc(sketch, "E4052", {"start": v(2696.38, 1360.28) * mm, "mid": v(2694.25, 1359.4) * mm, "end": v(2693.38, 1357.28) * mm});
            skArc(sketch, "E4053", {"start": v(2693.38, 1357.28) * mm, "mid": v(2694.25, 1355.16) * mm, "end": v(2696.38, 1354.28) * mm});
            skArc(sketch, "E4054", {"start": v(2696.38, 1354.28) * mm, "mid": v(2698.5, 1355.16) * mm, "end": v(2699.38, 1357.28) * mm});
            skArc(sketch, "E4055", {"start": v(2699.38, 1357.28) * mm, "mid": v(2698.5, 1359.4) * mm, "end": v(2696.38, 1360.28) * mm});
            skArc(sketch, "E4056", {"start": v(2406.03, 1748.69) * mm, "mid": v(2403.91, 1747.81) * mm, "end": v(2403.03, 1745.69) * mm});
            skArc(sketch, "E4057", {"start": v(2403.03, 1745.69) * mm, "mid": v(2403.91, 1743.57) * mm, "end": v(2406.03, 1742.69) * mm});
            skArc(sketch, "E4058", {"start": v(2406.03, 1742.69) * mm, "mid": v(2408.15, 1743.57) * mm, "end": v(2409.03, 1745.69) * mm});
            skArc(sketch, "E4059", {"start": v(2409.03, 1745.69) * mm, "mid": v(2408.15, 1747.81) * mm, "end": v(2406.03, 1748.69) * mm});
            skArc(sketch, "E4060", {"start": v(2106.07, 1810.22) * mm, "mid": v(2103.95, 1809.34) * mm, "end": v(2103.07, 1807.22) * mm});
            skArc(sketch, "E4061", {"start": v(2103.07, 1807.22) * mm, "mid": v(2103.95, 1805.1) * mm, "end": v(2106.07, 1804.22) * mm});
            skArc(sketch, "E4062", {"start": v(2106.07, 1804.22) * mm, "mid": v(2108.2, 1805.1) * mm, "end": v(2109.07, 1807.22) * mm});
            skArc(sketch, "E4063", {"start": v(2109.07, 1807.22) * mm, "mid": v(2108.2, 1809.34) * mm, "end": v(2106.07, 1810.22) * mm});
            skArc(sketch, "E4064", {"start": v(1535, 1956.35) * mm, "mid": v(1532.88, 1955.48) * mm, "end": v(1532, 1953.35) * mm});
            skArc(sketch, "E4065", {"start": v(1532, 1953.35) * mm, "mid": v(1532.88, 1951.23) * mm, "end": v(1535, 1950.35) * mm});
            skArc(sketch, "E4066", {"start": v(1535, 1950.35) * mm, "mid": v(1537.12, 1951.23) * mm, "end": v(1538, 1953.35) * mm});
            skArc(sketch, "E4067", {"start": v(1538, 1953.35) * mm, "mid": v(1537.12, 1955.48) * mm, "end": v(1535, 1956.35) * mm});
            skArc(sketch, "E4068", {"start": v(1740.74, 2379.37) * mm, "mid": v(1738.62, 2378.5) * mm, "end": v(1737.74, 2376.37) * mm});
            skArc(sketch, "E4069", {"start": v(1737.74, 2376.37) * mm, "mid": v(1738.62, 2374.25) * mm, "end": v(1740.74, 2373.37) * mm});
            skArc(sketch, "E4070", {"start": v(1740.74, 2373.37) * mm, "mid": v(1742.86, 2374.25) * mm, "end": v(1743.74, 2376.37) * mm});
            skArc(sketch, "E4071", {"start": v(1743.74, 2376.37) * mm, "mid": v(1742.86, 2378.5) * mm, "end": v(1740.74, 2379.37) * mm});
            skArc(sketch, "E4072", {"start": v(2184.9, 2379.37) * mm, "mid": v(2182.79, 2378.5) * mm, "end": v(2181.9, 2376.37) * mm});
            skArc(sketch, "E4073", {"start": v(2181.9, 2376.37) * mm, "mid": v(2182.79, 2374.25) * mm, "end": v(2184.9, 2373.37) * mm});
            skArc(sketch, "E4074", {"start": v(2184.9, 2373.37) * mm, "mid": v(2187.03, 2374.25) * mm, "end": v(2187.9, 2376.37) * mm});
            skArc(sketch, "E4075", {"start": v(2187.9, 2376.37) * mm, "mid": v(2187.03, 2378.5) * mm, "end": v(2184.9, 2379.37) * mm});
            skArc(sketch, "E4076", {"start": v(2698.3, 2381.3) * mm, "mid": v(2696.18, 2380.42) * mm, "end": v(2695.3, 2378.3) * mm});
            skArc(sketch, "E4077", {"start": v(2695.3, 2378.3) * mm, "mid": v(2696.18, 2376.17) * mm, "end": v(2698.3, 2375.3) * mm});
            skArc(sketch, "E4078", {"start": v(2698.3, 2375.3) * mm, "mid": v(2700.42, 2376.17) * mm, "end": v(2701.3, 2378.3) * mm});
            skArc(sketch, "E4079", {"start": v(2701.3, 2378.3) * mm, "mid": v(2700.42, 2380.42) * mm, "end": v(2698.3, 2381.3) * mm});
            skArc(sketch, "E4080", {"start": v(2486.79, 2125.56) * mm, "mid": v(2484.67, 2124.68) * mm, "end": v(2483.79, 2122.56) * mm});
            skArc(sketch, "E4081", {"start": v(2483.79, 2122.56) * mm, "mid": v(2484.67, 2120.44) * mm, "end": v(2486.79, 2119.56) * mm});
            skArc(sketch, "E4082", {"start": v(2486.79, 2119.56) * mm, "mid": v(2488.91, 2120.44) * mm, "end": v(2489.79, 2122.56) * mm});
            skArc(sketch, "E4083", {"start": v(2489.79, 2122.56) * mm, "mid": v(2488.91, 2124.68) * mm, "end": v(2486.79, 2125.56) * mm});
            skLineSegment(sketch, "E4084", {"start": v(2273.45, 157.89) * mm, "end": v(2413.45, 157.89) * mm});
            skLineSegment(sketch, "E4085", {"start": v(2413.45, 157.89) * mm, "end": v(2413.45, 177.89) * mm});
            skLineSegment(sketch, "E4086", {"start": v(2413.45, 177.89) * mm, "end": v(2273.45, 177.89) * mm});
            skLineSegment(sketch, "E4087", {"start": v(2273.45, 177.89) * mm, "end": v(2273.45, 157.89) * mm});
            skLineSegment(sketch, "E4088", {"start": v(1695.95, 1955.39) * mm, "end": v(1695.95, 2095.39) * mm});
            skLineSegment(sketch, "E4089", {"start": v(1695.95, 2095.39) * mm, "end": v(1675.95, 2095.39) * mm});
            skLineSegment(sketch, "E4090", {"start": v(1675.95, 2095.39) * mm, "end": v(1675.95, 1955.39) * mm});
            skLineSegment(sketch, "E4091", {"start": v(1675.95, 1955.39) * mm, "end": v(1695.95, 1955.39) * mm});
            skSolve(sketch);
        }
        {
            var Q0;
            Q0=makeQuery(id+"F5.imprint","IMPRINT",FACE,{"disambiguationData":[TD([[makeQuery(id+"F5.imprint","IMPRINT",EDGE,{"derivedFrom":sQuery(id+"F5.wireOp",EDGE,"E2813")}),1.0]])]});
            extrude(context, id + "F6", {"entities" : qUnion([Q0]), "depth" : 18 * mm});
        }
        {
            var Q0;
            Q0=makeQuery(id+"F5.imprint","IMPRINT",FACE,{"disambiguationData":[TD([[makeQuery(id+"F5.imprint","IMPRINT",EDGE,{"derivedFrom":sQuery(id+"F5.wireOp",EDGE,"E2943")}),1.0]])]});
            extrude(context, id + "F7", {"entities" : qUnion([Q0]), "depth" : 18 * mm});
        }
        {
            var Q0;
            Q0=makeQuery(id+"F5.imprint","IMPRINT",FACE,{"disambiguationData":[TD([[makeQuery(id+"F5.imprint","IMPRINT",EDGE,{"derivedFrom":sQuery(id+"F5.wireOp",EDGE,"E2683")}),1.0]])]});
            extrude(context, id + "F8", {"entities" : qUnion([Q0]), "depth" : 18 * mm});
        }
        {
            var Q0;
            Q0=makeQuery(id+"F0.imprint","IMPRINT",FACE,{"disambiguationData":[TD([[makeQuery(id+"F0.imprint","IMPRINT",EDGE,{"derivedFrom":sQuery(id+"F0.wireOp",EDGE,"E0")}),1.0]])]});
            extrude(context, id + "F9", {"entities" : qUnion([Q0]), "depth" : 18 * mm});
        }
        {
            var Q0;
            Q0=makeQuery(id+"F5.imprint","IMPRINT",FACE,{"disambiguationData":[TD([[makeQuery(id+"F5.imprint","IMPRINT",EDGE,{"derivedFrom":sQuery(id+"F5.wireOp",EDGE,"E2339")}),-1.0]])]});
            extrude(context, id + "F10", {"entities" : qUnion([Q0]), "depth" : 18 * mm});
        }
    });
